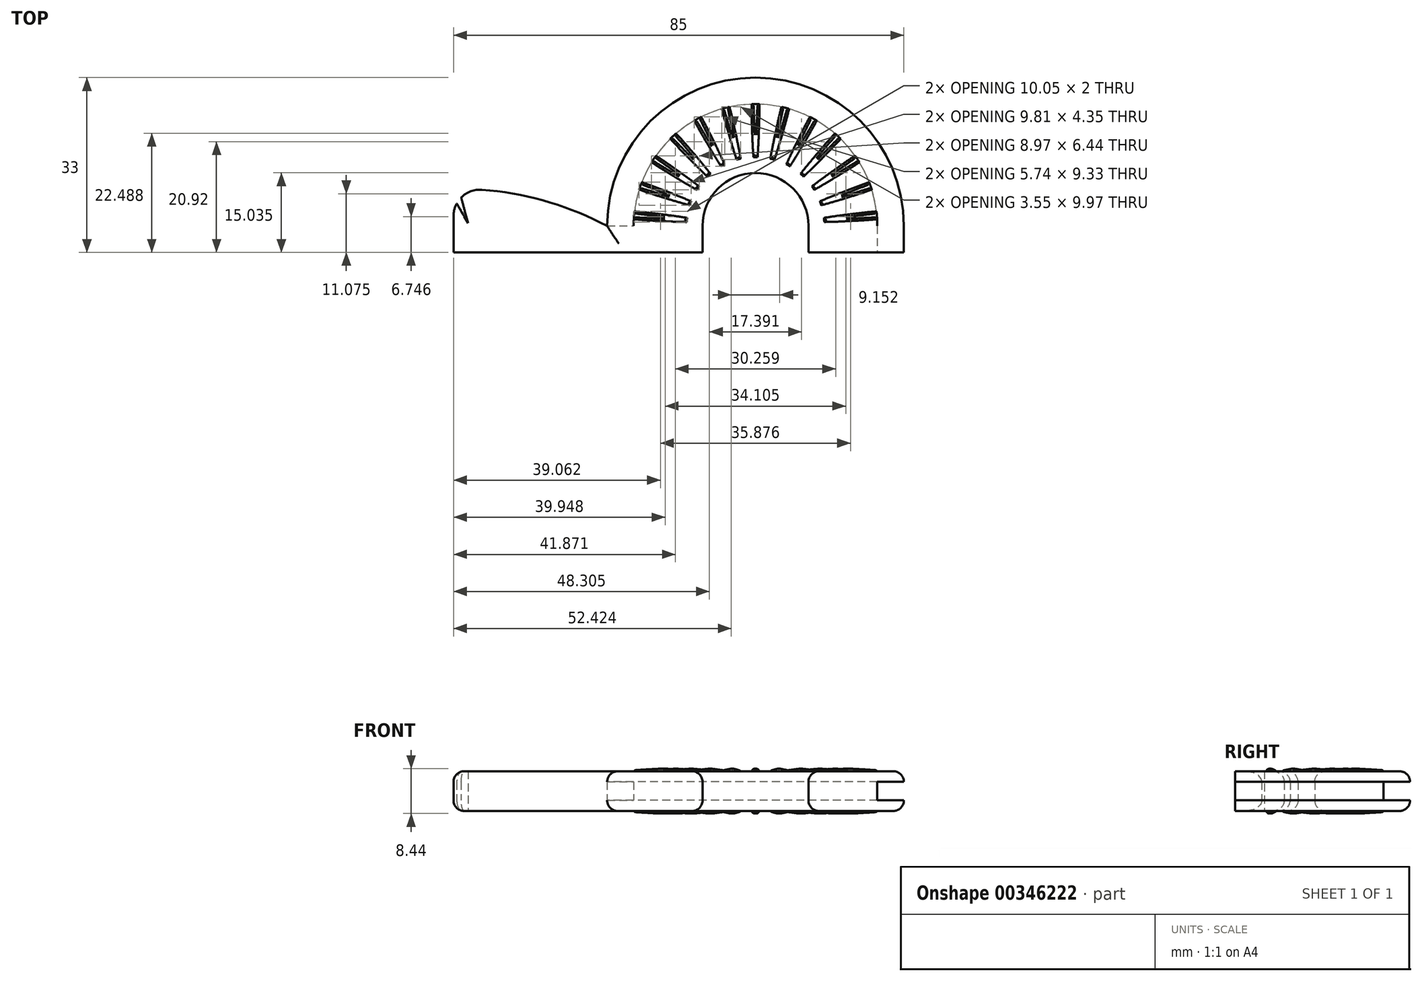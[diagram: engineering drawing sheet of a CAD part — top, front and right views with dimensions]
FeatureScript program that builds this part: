
annotation { "Feature Type Name" : "Feature", "Feature Type Description" : "" }
export const myFeature = defineFeature(function(context is Context, id is Id, definition is map)
    precondition{}
    {
        {
            var Q0;
            Q0=qCreatedBy(makeId("Top.planeOp"),FACE);
            var sketch = newSketch(context, id + "F0", { "sketchPlane" : qUnion([Q0])});
            skLineSegment(sketch, "E0", {"start": v(-57, 0) * mm, "end": v(28, 0) * mm});
            skLineSegment(sketch, "E1", {"start": v(-57, 0) * mm, "end": v(-57, 12) * mm});
            skArc(sketch, "E2", {"start": v(28, 5) * mm, "mid": v(0, 33) * mm, "end": v(-28, 5) * mm});
            skLineSegment(sketch, "E3", {"start": v(28, 5) * mm, "end": v(28, 0) * mm});
            skArc(sketch, "E4", {"start": v(23, 5) * mm, "mid": v(0, 28) * mm, "end": v(-23, 5) * mm});
            skLineSegment(sketch, "E5", {"start": v(-28, 5) * mm, "end": v(-23, 5) * mm});
            skLineSegment(sketch, "E6", {"start": v(23, 5) * mm, "end": v(28, 5) * mm});
            skLineSegment(sketch, "E7", {"start": v(23, 5) * mm, "end": v(23, 0) * mm});
            skLineSegment(sketch, "E8", {"start": v(-57, 12) * mm, "end": v(-42, 12) * mm});
            skLineSegment(sketch, "E9", {"start": v(-42, 12) * mm, "end": v(-28, 5) * mm});
            skPoint(sketch, "E10", {"position": v(-10, 0) * mm});
            skPoint(sketch, "E11", {"position": v(10, 0) * mm});
            skArc(sketch, "E12", {"start": v(10, 5) * mm, "mid": v(0, 15) * mm, "end": v(-10, 5) * mm});
            skLineSegment(sketch, "E13", {"start": v(-13, 5) * mm, "end": v(0, 5) * mm, "construction": true});
            skLineSegment(sketch, "E14", {"start": v(10, 5) * mm, "end": v(10, 0) * mm});
            skLineSegment(sketch, "E15", {"start": v(-10, 5) * mm, "end": v(-10, 0) * mm});
            skLineSegment(sketch, "E16", {"start": v(-22.97, 6.19) * mm, "end": v(-12.98, 5.67) * mm});
            skLineSegment(sketch, "E17", {"start": v(-12.9, 6.6) * mm, "end": v(-22.83, 7.82) * mm});
            skLineSegment(sketch, "E18.1.0", {"start": v(-21.98, 11.77) * mm, "end": v(-12.42, 8.83) * mm});
            skLineSegment(sketch, "E18.1.1", {"start": v(-12.12, 9.7) * mm, "end": v(-21.44, 13.32) * mm});
            skLineSegment(sketch, "E18.2.0", {"start": v(-19.66, 16.94) * mm, "end": v(-11.1, 11.75) * mm});
            skLineSegment(sketch, "E18.2.1", {"start": v(-10.6, 12.53) * mm, "end": v(-18.75, 18.32) * mm});
            skLineSegment(sketch, "E18.anchor1", {"start": v(-12.98, 5.67) * mm, "end": v(-22.97, 6.19) * mm, "construction": true});
            skLineSegment(sketch, "E18.anchor2", {"start": v(12.9, 6.6) * mm, "end": v(22.83, 7.82) * mm, "construction": true});
            skLineSegment(sketch, "E19.1.3.0", {"start": v(-16.13, 21.4) * mm, "end": v(-9.12, 14.26) * mm});
            skLineSegment(sketch, "E19.3.3.0", {"start": v(-8.43, 14.9) * mm, "end": v(-14.92, 22.5) * mm});
            skLineSegment(sketch, "E19.1.4.0", {"start": v(-11.63, 24.84) * mm, "end": v(-6.57, 16.21) * mm});
            skLineSegment(sketch, "E19.3.4.0", {"start": v(-5.76, 16.66) * mm, "end": v(-10.19, 25.62) * mm});
            skLineSegment(sketch, "E19.1.5.0", {"start": v(-6.42, 27.09) * mm, "end": v(-3.63, 17.48) * mm});
            skLineSegment(sketch, "E19.3.5.0", {"start": v(-2.73, 17.71) * mm, "end": v(-4.83, 27.49) * mm});
            skLineSegment(sketch, "E19.1.6.0", {"start": v(-0.82, 27.99) * mm, "end": v(-0.46, 18) * mm});
            skLineSegment(sketch, "E19.3.6.0", {"start": v(0.46, 18) * mm, "end": v(0.82, 27.99) * mm});
            skLineSegment(sketch, "E19.1.7.0", {"start": v(4.83, 27.49) * mm, "end": v(2.73, 17.71) * mm});
            skLineSegment(sketch, "E19.3.7.0", {"start": v(3.63, 17.48) * mm, "end": v(6.42, 27.09) * mm});
            skLineSegment(sketch, "E19.1.8.0", {"start": v(10.19, 25.62) * mm, "end": v(5.76, 16.66) * mm});
            skLineSegment(sketch, "E19.3.8.0", {"start": v(6.57, 16.21) * mm, "end": v(11.63, 24.84) * mm});
            skLineSegment(sketch, "E19.1.9.0", {"start": v(14.92, 22.5) * mm, "end": v(8.43, 14.9) * mm});
            skLineSegment(sketch, "E19.3.9.0", {"start": v(9.12, 14.26) * mm, "end": v(16.13, 21.4) * mm});
            skLineSegment(sketch, "E19.1.10.0", {"start": v(18.75, 18.32) * mm, "end": v(10.6, 12.53) * mm});
            skLineSegment(sketch, "E19.3.10.0", {"start": v(11.1, 11.75) * mm, "end": v(19.66, 16.94) * mm});
            skLineSegment(sketch, "E19.1.11.0", {"start": v(21.44, 13.32) * mm, "end": v(12.12, 9.7) * mm});
            skLineSegment(sketch, "E19.3.11.0", {"start": v(12.42, 8.83) * mm, "end": v(21.98, 11.77) * mm});
            skLineSegment(sketch, "E19.1.12.0", {"start": v(22.83, 7.82) * mm, "end": v(12.9, 6.6) * mm});
            skLineSegment(sketch, "E19.3.12.0", {"start": v(12.98, 5.67) * mm, "end": v(22.97, 6.19) * mm});
            skArc(sketch, "E20", {"start": v(13, 5) * mm, "mid": v(0, 18) * mm, "end": v(-13, 5) * mm});
            skLineSegment(sketch, "E21.trimOffspring", {"start": v(10, 5) * mm, "end": v(13, 5) * mm, "construction": true});
            skPoint(sketch, "E22.orphan", {"position": v(-27.79, 8.43) * mm});
            skPoint(sketch, "E23.orphan", {"position": v(-26.76, 13.24) * mm});
            skPoint(sketch, "E24.orphan", {"position": v(-27.96, 6.44) * mm});
            skPoint(sketch, "E25.orphan", {"position": v(-26.1, 15.13) * mm});
            skPoint(sketch, "E26.orphan", {"position": v(-23.93, 19.54) * mm});
            skPoint(sketch, "E27.orphan", {"position": v(-22.83, 21.21) * mm});
            skPoint(sketch, "E28.orphan", {"position": v(-19.64, 24.96) * mm});
            skPoint(sketch, "E29.orphan", {"position": v(-18.17, 26.3) * mm});
            skPoint(sketch, "E30.orphan", {"position": v(-14.16, 29.16) * mm});
            skPoint(sketch, "E31.orphan", {"position": v(-12.4, 30.1) * mm});
            skPoint(sketch, "E32.orphan", {"position": v(-7.82, 31.89) * mm});
            skPoint(sketch, "E33.orphan", {"position": v(-5.88, 32.38) * mm});
            skPoint(sketch, "E34.orphan", {"position": v(-1, 32.98) * mm});
            skPoint(sketch, "E35.orphan", {"position": v(1, 32.98) * mm});
            skPoint(sketch, "E36.orphan", {"position": v(5.88, 32.38) * mm});
            skPoint(sketch, "E37.orphan", {"position": v(7.82, 31.89) * mm});
            skPoint(sketch, "E38.orphan", {"position": v(12.4, 30.1) * mm});
            skPoint(sketch, "E39.orphan", {"position": v(14.16, 29.16) * mm});
            skPoint(sketch, "E40.orphan", {"position": v(18.17, 26.3) * mm});
            skPoint(sketch, "E41.orphan", {"position": v(19.64, 24.96) * mm});
            skPoint(sketch, "E42.orphan", {"position": v(22.83, 21.21) * mm});
            skPoint(sketch, "E43.orphan", {"position": v(23.93, 19.54) * mm});
            skPoint(sketch, "E44.orphan", {"position": v(26.1, 15.13) * mm});
            skPoint(sketch, "E45.orphan", {"position": v(26.76, 13.24) * mm});
            skPoint(sketch, "E46.orphan", {"position": v(27.79, 8.43) * mm});
            skPoint(sketch, "E47.orphan", {"position": v(27.96, 6.44) * mm});
            skLineSegment(sketch, "E48", {"start": v(-57, 10.29) * mm, "end": v(-54.25, 5.53) * mm});
            skLineSegment(sketch, "E49", {"start": v(-54.25, 5.53) * mm, "end": v(-55.98, 12) * mm});
            skSolve(sketch);
        }
        {
            var Q0;
            {var subQ0=sQuery(id+"F0.wireOp",EDGE,"E3");Q0=makeQuery(id+"F0.imprint","IMPRINT",FACE,{"disambiguationData":[TD([[makeQuery(id+"F0.imprint","IMPRINT",EDGE,{"derivedFrom":subQ0}),-1.0]])]});}
            var Q1;
            {var subQ0=sQuery(id+"F0.wireOp",EDGE,"E5");Q1=makeQuery(id+"F0.imprint","IMPRINT",FACE,{"disambiguationData":[TD([[makeQuery(id+"F0.imprint","IMPRINT",EDGE,{"derivedFrom":subQ0}),1.0]])]});}
            var Q2;
            {var subQ4=sQuery(id+"F0.wireOp",EDGE,"E1");Q2=makeQuery(id+"F0.imprint","IMPRINT",FACE,{"disambiguationData":[TD([[makeQuery(id+"F0.imprint","IMPRINT",EDGE,{"derivedFrom":subQ4}),-1.0]])]});}
            var Q3;
            {var subQ0=sQuery(id+"F0.wireOp",EDGE,"E6");Q3=makeQuery(id+"F0.imprint","IMPRINT",FACE,{"disambiguationData":[TD([[makeQuery(id+"F0.imprint","IMPRINT",EDGE,{"derivedFrom":subQ0}),1.0]])]});}
            var Q4;
            {var subQ0=sQuery(id+"F0.wireOp",EDGE,"E19.1.12.0");var subQ1=sQuery(id+"F0.wireOp",EDGE,"E2");var subQ2=makeQuery(id+"F0.imprint","INTERSECT",VERTEX,{"derivedFrom":[subQ1,subQ0]});Q4=makeQuery(id+"F0.imprint","IMPRINT",FACE,{"disambiguationData":[TD([[makeQuery(id+"F0.imprint","IMPRINT",EDGE,{"disambiguationData":[TD([[subQ2,1.0]])],"derivedFrom":subQ1}),1.0]])]});}
            var Q5;
            {var subQ0=sQuery(id+"F0.wireOp",EDGE,"E19.3.11.0");var subQ1=sQuery(id+"F0.wireOp",EDGE,"E2");var subQ2=makeQuery(id+"F0.imprint","INTERSECT",VERTEX,{"derivedFrom":[subQ1,subQ0]});Q5=makeQuery(id+"F0.imprint","IMPRINT",FACE,{"disambiguationData":[TD([[makeQuery(id+"F0.imprint","IMPRINT",EDGE,{"disambiguationData":[TD([[subQ2,1.0]])],"derivedFrom":subQ1}),1.0]])]});}
            var Q6;
            {var subQ0=sQuery(id+"F0.wireOp",EDGE,"E19.1.11.0");var subQ1=sQuery(id+"F0.wireOp",EDGE,"E2");var subQ2=makeQuery(id+"F0.imprint","INTERSECT",VERTEX,{"derivedFrom":[subQ1,subQ0]});Q6=makeQuery(id+"F0.imprint","IMPRINT",FACE,{"disambiguationData":[TD([[makeQuery(id+"F0.imprint","IMPRINT",EDGE,{"disambiguationData":[TD([[subQ2,1.0]])],"derivedFrom":subQ1}),1.0]])]});}
            var Q7;
            {var subQ0=sQuery(id+"F0.wireOp",EDGE,"E19.3.10.0");var subQ1=sQuery(id+"F0.wireOp",EDGE,"E2");var subQ2=makeQuery(id+"F0.imprint","INTERSECT",VERTEX,{"derivedFrom":[subQ1,subQ0]});Q7=makeQuery(id+"F0.imprint","IMPRINT",FACE,{"disambiguationData":[TD([[makeQuery(id+"F0.imprint","IMPRINT",EDGE,{"disambiguationData":[TD([[subQ2,1.0]])],"derivedFrom":subQ1}),1.0]])]});}
            var Q8;
            {var subQ0=sQuery(id+"F0.wireOp",EDGE,"E19.1.10.0");var subQ1=sQuery(id+"F0.wireOp",EDGE,"E2");var subQ2=makeQuery(id+"F0.imprint","INTERSECT",VERTEX,{"derivedFrom":[subQ1,subQ0]});Q8=makeQuery(id+"F0.imprint","IMPRINT",FACE,{"disambiguationData":[TD([[makeQuery(id+"F0.imprint","IMPRINT",EDGE,{"disambiguationData":[TD([[subQ2,1.0]])],"derivedFrom":subQ1}),1.0]])]});}
            var Q9;
            {var subQ0=sQuery(id+"F0.wireOp",EDGE,"E19.3.9.0");var subQ1=sQuery(id+"F0.wireOp",EDGE,"E2");var subQ2=makeQuery(id+"F0.imprint","INTERSECT",VERTEX,{"derivedFrom":[subQ1,subQ0]});Q9=makeQuery(id+"F0.imprint","IMPRINT",FACE,{"disambiguationData":[TD([[makeQuery(id+"F0.imprint","IMPRINT",EDGE,{"disambiguationData":[TD([[subQ2,1.0]])],"derivedFrom":subQ1}),1.0]])]});}
            var Q10;
            {var subQ0=sQuery(id+"F0.wireOp",EDGE,"E19.1.9.0");var subQ1=sQuery(id+"F0.wireOp",EDGE,"E2");var subQ2=makeQuery(id+"F0.imprint","INTERSECT",VERTEX,{"derivedFrom":[subQ1,subQ0]});Q10=makeQuery(id+"F0.imprint","IMPRINT",FACE,{"disambiguationData":[TD([[makeQuery(id+"F0.imprint","IMPRINT",EDGE,{"disambiguationData":[TD([[subQ2,1.0]])],"derivedFrom":subQ1}),1.0]])]});}
            var Q11;
            {var subQ0=sQuery(id+"F0.wireOp",EDGE,"E19.3.8.0");var subQ1=sQuery(id+"F0.wireOp",EDGE,"E2");var subQ2=makeQuery(id+"F0.imprint","INTERSECT",VERTEX,{"derivedFrom":[subQ1,subQ0]});Q11=makeQuery(id+"F0.imprint","IMPRINT",FACE,{"disambiguationData":[TD([[makeQuery(id+"F0.imprint","IMPRINT",EDGE,{"disambiguationData":[TD([[subQ2,1.0]])],"derivedFrom":subQ1}),1.0]])]});}
            var Q12;
            {var subQ0=sQuery(id+"F0.wireOp",EDGE,"E19.1.8.0");var subQ1=sQuery(id+"F0.wireOp",EDGE,"E2");var subQ2=makeQuery(id+"F0.imprint","INTERSECT",VERTEX,{"derivedFrom":[subQ1,subQ0]});Q12=makeQuery(id+"F0.imprint","IMPRINT",FACE,{"disambiguationData":[TD([[makeQuery(id+"F0.imprint","IMPRINT",EDGE,{"disambiguationData":[TD([[subQ2,1.0]])],"derivedFrom":subQ1}),1.0]])]});}
            var Q13;
            {var subQ0=sQuery(id+"F0.wireOp",EDGE,"E19.3.7.0");var subQ1=sQuery(id+"F0.wireOp",EDGE,"E2");var subQ2=makeQuery(id+"F0.imprint","INTERSECT",VERTEX,{"derivedFrom":[subQ1,subQ0]});Q13=makeQuery(id+"F0.imprint","IMPRINT",FACE,{"disambiguationData":[TD([[makeQuery(id+"F0.imprint","IMPRINT",EDGE,{"disambiguationData":[TD([[subQ2,1.0]])],"derivedFrom":subQ1}),1.0]])]});}
            var Q14;
            {var subQ0=sQuery(id+"F0.wireOp",EDGE,"E19.1.7.0");var subQ1=sQuery(id+"F0.wireOp",EDGE,"E2");var subQ2=makeQuery(id+"F0.imprint","INTERSECT",VERTEX,{"derivedFrom":[subQ1,subQ0]});Q14=makeQuery(id+"F0.imprint","IMPRINT",FACE,{"disambiguationData":[TD([[makeQuery(id+"F0.imprint","IMPRINT",EDGE,{"disambiguationData":[TD([[subQ2,1.0]])],"derivedFrom":subQ1}),1.0]])]});}
            var Q15;
            {var subQ0=sQuery(id+"F0.wireOp",EDGE,"E19.3.6.0");var subQ1=sQuery(id+"F0.wireOp",EDGE,"E2");var subQ2=makeQuery(id+"F0.imprint","INTERSECT",VERTEX,{"derivedFrom":[subQ1,subQ0]});Q15=makeQuery(id+"F0.imprint","IMPRINT",FACE,{"disambiguationData":[TD([[makeQuery(id+"F0.imprint","IMPRINT",EDGE,{"disambiguationData":[TD([[subQ2,1.0]])],"derivedFrom":subQ1}),1.0]])]});}
            var Q16;
            {var subQ0=sQuery(id+"F0.wireOp",EDGE,"E19.1.6.0");var subQ1=sQuery(id+"F0.wireOp",EDGE,"E2");var subQ2=makeQuery(id+"F0.imprint","INTERSECT",VERTEX,{"derivedFrom":[subQ1,subQ0]});Q16=makeQuery(id+"F0.imprint","IMPRINT",FACE,{"disambiguationData":[TD([[makeQuery(id+"F0.imprint","IMPRINT",EDGE,{"disambiguationData":[TD([[subQ2,1.0]])],"derivedFrom":subQ1}),1.0]])]});}
            var Q17;
            {var subQ0=sQuery(id+"F0.wireOp",EDGE,"E19.3.5.0");var subQ1=sQuery(id+"F0.wireOp",EDGE,"E2");var subQ2=makeQuery(id+"F0.imprint","INTERSECT",VERTEX,{"derivedFrom":[subQ1,subQ0]});Q17=makeQuery(id+"F0.imprint","IMPRINT",FACE,{"disambiguationData":[TD([[makeQuery(id+"F0.imprint","IMPRINT",EDGE,{"disambiguationData":[TD([[subQ2,1.0]])],"derivedFrom":subQ1}),1.0]])]});}
            var Q18;
            {var subQ0=sQuery(id+"F0.wireOp",EDGE,"E19.1.5.0");var subQ1=sQuery(id+"F0.wireOp",EDGE,"E2");var subQ2=makeQuery(id+"F0.imprint","INTERSECT",VERTEX,{"derivedFrom":[subQ1,subQ0]});Q18=makeQuery(id+"F0.imprint","IMPRINT",FACE,{"disambiguationData":[TD([[makeQuery(id+"F0.imprint","IMPRINT",EDGE,{"disambiguationData":[TD([[subQ2,1.0]])],"derivedFrom":subQ1}),1.0]])]});}
            var Q19;
            {var subQ0=sQuery(id+"F0.wireOp",EDGE,"E19.3.4.0");var subQ1=sQuery(id+"F0.wireOp",EDGE,"E2");var subQ2=makeQuery(id+"F0.imprint","INTERSECT",VERTEX,{"derivedFrom":[subQ1,subQ0]});Q19=makeQuery(id+"F0.imprint","IMPRINT",FACE,{"disambiguationData":[TD([[makeQuery(id+"F0.imprint","IMPRINT",EDGE,{"disambiguationData":[TD([[subQ2,1.0]])],"derivedFrom":subQ1}),1.0]])]});}
            var Q20;
            {var subQ0=sQuery(id+"F0.wireOp",EDGE,"E19.1.4.0");var subQ1=sQuery(id+"F0.wireOp",EDGE,"E2");var subQ2=makeQuery(id+"F0.imprint","INTERSECT",VERTEX,{"derivedFrom":[subQ1,subQ0]});Q20=makeQuery(id+"F0.imprint","IMPRINT",FACE,{"disambiguationData":[TD([[makeQuery(id+"F0.imprint","IMPRINT",EDGE,{"disambiguationData":[TD([[subQ2,1.0]])],"derivedFrom":subQ1}),1.0]])]});}
            var Q21;
            {var subQ0=sQuery(id+"F0.wireOp",EDGE,"E19.3.3.0");var subQ1=sQuery(id+"F0.wireOp",EDGE,"E2");var subQ2=makeQuery(id+"F0.imprint","INTERSECT",VERTEX,{"derivedFrom":[subQ1,subQ0]});Q21=makeQuery(id+"F0.imprint","IMPRINT",FACE,{"disambiguationData":[TD([[makeQuery(id+"F0.imprint","IMPRINT",EDGE,{"disambiguationData":[TD([[subQ2,1.0]])],"derivedFrom":subQ1}),1.0]])]});}
            var Q22;
            {var subQ0=sQuery(id+"F0.wireOp",EDGE,"E19.1.3.0");var subQ1=sQuery(id+"F0.wireOp",EDGE,"E2");var subQ2=makeQuery(id+"F0.imprint","INTERSECT",VERTEX,{"derivedFrom":[subQ1,subQ0]});Q22=makeQuery(id+"F0.imprint","IMPRINT",FACE,{"disambiguationData":[TD([[makeQuery(id+"F0.imprint","IMPRINT",EDGE,{"disambiguationData":[TD([[subQ2,1.0]])],"derivedFrom":subQ1}),1.0]])]});}
            var Q23;
            {var subQ0=sQuery(id+"F0.wireOp",EDGE,"E18.2.1");var subQ1=sQuery(id+"F0.wireOp",EDGE,"E2");var subQ2=makeQuery(id+"F0.imprint","INTERSECT",VERTEX,{"derivedFrom":[subQ1,subQ0]});Q23=makeQuery(id+"F0.imprint","IMPRINT",FACE,{"disambiguationData":[TD([[makeQuery(id+"F0.imprint","IMPRINT",EDGE,{"disambiguationData":[TD([[subQ2,1.0]])],"derivedFrom":subQ1}),1.0]])]});}
            var Q24;
            {var subQ0=sQuery(id+"F0.wireOp",EDGE,"E18.2.0");var subQ1=sQuery(id+"F0.wireOp",EDGE,"E2");var subQ2=makeQuery(id+"F0.imprint","INTERSECT",VERTEX,{"derivedFrom":[subQ1,subQ0]});Q24=makeQuery(id+"F0.imprint","IMPRINT",FACE,{"disambiguationData":[TD([[makeQuery(id+"F0.imprint","IMPRINT",EDGE,{"disambiguationData":[TD([[subQ2,1.0]])],"derivedFrom":subQ1}),1.0]])]});}
            var Q25;
            {var subQ0=sQuery(id+"F0.wireOp",EDGE,"E18.1.1");var subQ1=sQuery(id+"F0.wireOp",EDGE,"E2");var subQ2=makeQuery(id+"F0.imprint","INTERSECT",VERTEX,{"derivedFrom":[subQ1,subQ0]});Q25=makeQuery(id+"F0.imprint","IMPRINT",FACE,{"disambiguationData":[TD([[makeQuery(id+"F0.imprint","IMPRINT",EDGE,{"disambiguationData":[TD([[subQ2,1.0]])],"derivedFrom":subQ1}),1.0]])]});}
            var Q26;
            {var subQ0=sQuery(id+"F0.wireOp",EDGE,"E18.1.0");var subQ1=sQuery(id+"F0.wireOp",EDGE,"E2");var subQ2=makeQuery(id+"F0.imprint","INTERSECT",VERTEX,{"derivedFrom":[subQ1,subQ0]});Q26=makeQuery(id+"F0.imprint","IMPRINT",FACE,{"disambiguationData":[TD([[makeQuery(id+"F0.imprint","IMPRINT",EDGE,{"disambiguationData":[TD([[subQ2,1.0]])],"derivedFrom":subQ1}),1.0]])]});}
            var Q27;
            {var subQ0=sQuery(id+"F0.wireOp",EDGE,"E17");var subQ1=sQuery(id+"F0.wireOp",EDGE,"E2");var subQ2=makeQuery(id+"F0.imprint","INTERSECT",VERTEX,{"derivedFrom":[subQ1,subQ0]});Q27=makeQuery(id+"F0.imprint","IMPRINT",FACE,{"disambiguationData":[TD([[makeQuery(id+"F0.imprint","IMPRINT",EDGE,{"disambiguationData":[TD([[subQ2,1.0]])],"derivedFrom":subQ1}),1.0]])]});}
            var Q28;
            {var subQ0=sQuery(id+"F0.wireOp",EDGE,"E16");var subQ1=sQuery(id+"F0.wireOp",EDGE,"E2");var subQ2=makeQuery(id+"F0.imprint","INTERSECT",VERTEX,{"derivedFrom":[subQ1,subQ0]});Q28=makeQuery(id+"F0.imprint","IMPRINT",FACE,{"disambiguationData":[TD([[makeQuery(id+"F0.imprint","IMPRINT",EDGE,{"disambiguationData":[TD([[subQ2,1.0]])],"derivedFrom":subQ1}),1.0]])]});}
            var Q29;
            {var subQ4=sQuery(id+"F0.wireOp",EDGE,"E7");Q29=makeQuery(id+"F0.imprint","IMPRINT",FACE,{"disambiguationData":[TD([[makeQuery(id+"F0.imprint","IMPRINT",EDGE,{"derivedFrom":subQ4}),-1.0]])]});}
            var Q30;
            {var subQ0=sQuery(id+"F0.wireOp",EDGE,"E17");var subQ1=sQuery(id+"F0.wireOp",EDGE,"E4");var subQ2=makeQuery(id+"F0.imprint","INTERSECT",VERTEX,{"derivedFrom":[subQ1,subQ0]});Q30=makeQuery(id+"F0.imprint","IMPRINT",FACE,{"disambiguationData":[TD([[makeQuery(id+"F0.imprint","IMPRINT",EDGE,{"disambiguationData":[TD([[subQ2,-1.0]])],"derivedFrom":subQ1}),1.0]])]});}
            var Q31;
            {var subQ0=sQuery(id+"F0.wireOp",EDGE,"E18.1.0");var subQ1=sQuery(id+"F0.wireOp",EDGE,"E4");var subQ2=makeQuery(id+"F0.imprint","INTERSECT",VERTEX,{"derivedFrom":[subQ1,subQ0]});Q31=makeQuery(id+"F0.imprint","IMPRINT",FACE,{"disambiguationData":[TD([[makeQuery(id+"F0.imprint","IMPRINT",EDGE,{"disambiguationData":[TD([[subQ2,-1.0]])],"derivedFrom":subQ1}),1.0]])]});}
            var Q32;
            {var subQ0=sQuery(id+"F0.wireOp",EDGE,"E18.1.1");var subQ1=sQuery(id+"F0.wireOp",EDGE,"E4");var subQ2=makeQuery(id+"F0.imprint","INTERSECT",VERTEX,{"derivedFrom":[subQ1,subQ0]});Q32=makeQuery(id+"F0.imprint","IMPRINT",FACE,{"disambiguationData":[TD([[makeQuery(id+"F0.imprint","IMPRINT",EDGE,{"disambiguationData":[TD([[subQ2,-1.0]])],"derivedFrom":subQ1}),1.0]])]});}
            var Q33;
            {var subQ0=sQuery(id+"F0.wireOp",EDGE,"E18.2.0");var subQ1=sQuery(id+"F0.wireOp",EDGE,"E4");var subQ2=makeQuery(id+"F0.imprint","INTERSECT",VERTEX,{"derivedFrom":[subQ1,subQ0]});Q33=makeQuery(id+"F0.imprint","IMPRINT",FACE,{"disambiguationData":[TD([[makeQuery(id+"F0.imprint","IMPRINT",EDGE,{"disambiguationData":[TD([[subQ2,-1.0]])],"derivedFrom":subQ1}),1.0]])]});}
            var Q34;
            {var subQ0=sQuery(id+"F0.wireOp",EDGE,"E18.2.1");var subQ1=sQuery(id+"F0.wireOp",EDGE,"E4");var subQ2=makeQuery(id+"F0.imprint","INTERSECT",VERTEX,{"derivedFrom":[subQ1,subQ0]});Q34=makeQuery(id+"F0.imprint","IMPRINT",FACE,{"disambiguationData":[TD([[makeQuery(id+"F0.imprint","IMPRINT",EDGE,{"disambiguationData":[TD([[subQ2,-1.0]])],"derivedFrom":subQ1}),1.0]])]});}
            var Q35;
            {var subQ0=sQuery(id+"F0.wireOp",EDGE,"E19.1.3.0");var subQ1=sQuery(id+"F0.wireOp",EDGE,"E4");var subQ2=makeQuery(id+"F0.imprint","INTERSECT",VERTEX,{"derivedFrom":[subQ1,subQ0]});Q35=makeQuery(id+"F0.imprint","IMPRINT",FACE,{"disambiguationData":[TD([[makeQuery(id+"F0.imprint","IMPRINT",EDGE,{"disambiguationData":[TD([[subQ2,-1.0]])],"derivedFrom":subQ1}),1.0]])]});}
            var Q36;
            {var subQ0=sQuery(id+"F0.wireOp",EDGE,"E19.3.5.0");var subQ1=sQuery(id+"F0.wireOp",EDGE,"E4");var subQ2=makeQuery(id+"F0.imprint","INTERSECT",VERTEX,{"derivedFrom":[subQ1,subQ0]});Q36=makeQuery(id+"F0.imprint","IMPRINT",FACE,{"disambiguationData":[TD([[makeQuery(id+"F0.imprint","IMPRINT",EDGE,{"disambiguationData":[TD([[subQ2,-1.0]])],"derivedFrom":subQ1}),1.0]])]});}
            var Q37;
            {var subQ0=sQuery(id+"F0.wireOp",EDGE,"E19.3.3.0");var subQ1=sQuery(id+"F0.wireOp",EDGE,"E4");var subQ2=makeQuery(id+"F0.imprint","INTERSECT",VERTEX,{"derivedFrom":[subQ1,subQ0]});Q37=makeQuery(id+"F0.imprint","IMPRINT",FACE,{"disambiguationData":[TD([[makeQuery(id+"F0.imprint","IMPRINT",EDGE,{"disambiguationData":[TD([[subQ2,-1.0]])],"derivedFrom":subQ1}),1.0]])]});}
            var Q38;
            {var subQ0=sQuery(id+"F0.wireOp",EDGE,"E19.1.4.0");var subQ1=sQuery(id+"F0.wireOp",EDGE,"E4");var subQ2=makeQuery(id+"F0.imprint","INTERSECT",VERTEX,{"derivedFrom":[subQ1,subQ0]});Q38=makeQuery(id+"F0.imprint","IMPRINT",FACE,{"disambiguationData":[TD([[makeQuery(id+"F0.imprint","IMPRINT",EDGE,{"disambiguationData":[TD([[subQ2,-1.0]])],"derivedFrom":subQ1}),1.0]])]});}
            var Q39;
            {var subQ0=sQuery(id+"F0.wireOp",EDGE,"E19.3.4.0");var subQ1=sQuery(id+"F0.wireOp",EDGE,"E4");var subQ2=makeQuery(id+"F0.imprint","INTERSECT",VERTEX,{"derivedFrom":[subQ1,subQ0]});Q39=makeQuery(id+"F0.imprint","IMPRINT",FACE,{"disambiguationData":[TD([[makeQuery(id+"F0.imprint","IMPRINT",EDGE,{"disambiguationData":[TD([[subQ2,-1.0]])],"derivedFrom":subQ1}),1.0]])]});}
            var Q40;
            {var subQ0=sQuery(id+"F0.wireOp",EDGE,"E19.1.5.0");var subQ1=sQuery(id+"F0.wireOp",EDGE,"E4");var subQ2=makeQuery(id+"F0.imprint","INTERSECT",VERTEX,{"derivedFrom":[subQ1,subQ0]});Q40=makeQuery(id+"F0.imprint","IMPRINT",FACE,{"disambiguationData":[TD([[makeQuery(id+"F0.imprint","IMPRINT",EDGE,{"disambiguationData":[TD([[subQ2,-1.0]])],"derivedFrom":subQ1}),1.0]])]});}
            var Q41;
            {var subQ0=sQuery(id+"F0.wireOp",EDGE,"E19.1.7.0");var subQ1=sQuery(id+"F0.wireOp",EDGE,"E4");var subQ2=makeQuery(id+"F0.imprint","INTERSECT",VERTEX,{"derivedFrom":[subQ1,subQ0]});Q41=makeQuery(id+"F0.imprint","IMPRINT",FACE,{"disambiguationData":[TD([[makeQuery(id+"F0.imprint","IMPRINT",EDGE,{"disambiguationData":[TD([[subQ2,-1.0]])],"derivedFrom":subQ1}),1.0]])]});}
            var Q42;
            {var subQ0=sQuery(id+"F0.wireOp",EDGE,"E19.3.11.0");var subQ1=sQuery(id+"F0.wireOp",EDGE,"E4");var subQ2=makeQuery(id+"F0.imprint","INTERSECT",VERTEX,{"derivedFrom":[subQ1,subQ0]});Q42=makeQuery(id+"F0.imprint","IMPRINT",FACE,{"disambiguationData":[TD([[makeQuery(id+"F0.imprint","IMPRINT",EDGE,{"disambiguationData":[TD([[subQ2,-1.0]])],"derivedFrom":subQ1}),1.0]])]});}
            var Q43;
            {var subQ0=sQuery(id+"F0.wireOp",EDGE,"E19.3.6.0");var subQ1=sQuery(id+"F0.wireOp",EDGE,"E4");var subQ2=makeQuery(id+"F0.imprint","INTERSECT",VERTEX,{"derivedFrom":[subQ1,subQ0]});Q43=makeQuery(id+"F0.imprint","IMPRINT",FACE,{"disambiguationData":[TD([[makeQuery(id+"F0.imprint","IMPRINT",EDGE,{"disambiguationData":[TD([[subQ2,-1.0]])],"derivedFrom":subQ1}),1.0]])]});}
            var Q44;
            {var subQ0=sQuery(id+"F0.wireOp",EDGE,"E19.1.10.0");var subQ1=sQuery(id+"F0.wireOp",EDGE,"E4");var subQ2=makeQuery(id+"F0.imprint","INTERSECT",VERTEX,{"derivedFrom":[subQ1,subQ0]});Q44=makeQuery(id+"F0.imprint","IMPRINT",FACE,{"disambiguationData":[TD([[makeQuery(id+"F0.imprint","IMPRINT",EDGE,{"disambiguationData":[TD([[subQ2,-1.0]])],"derivedFrom":subQ1}),1.0]])]});}
            var Q45;
            {var subQ0=sQuery(id+"F0.wireOp",EDGE,"E19.3.8.0");var subQ1=sQuery(id+"F0.wireOp",EDGE,"E4");var subQ2=makeQuery(id+"F0.imprint","INTERSECT",VERTEX,{"derivedFrom":[subQ1,subQ0]});Q45=makeQuery(id+"F0.imprint","IMPRINT",FACE,{"disambiguationData":[TD([[makeQuery(id+"F0.imprint","IMPRINT",EDGE,{"disambiguationData":[TD([[subQ2,-1.0]])],"derivedFrom":subQ1}),1.0]])]});}
            var Q46;
            {var subQ0=sQuery(id+"F0.wireOp",EDGE,"E19.1.11.0");var subQ1=sQuery(id+"F0.wireOp",EDGE,"E4");var subQ2=makeQuery(id+"F0.imprint","INTERSECT",VERTEX,{"derivedFrom":[subQ1,subQ0]});Q46=makeQuery(id+"F0.imprint","IMPRINT",FACE,{"disambiguationData":[TD([[makeQuery(id+"F0.imprint","IMPRINT",EDGE,{"disambiguationData":[TD([[subQ2,-1.0]])],"derivedFrom":subQ1}),1.0]])]});}
            var Q47;
            {var subQ0=sQuery(id+"F0.wireOp",EDGE,"E19.1.6.0");var subQ1=sQuery(id+"F0.wireOp",EDGE,"E4");var subQ2=makeQuery(id+"F0.imprint","INTERSECT",VERTEX,{"derivedFrom":[subQ1,subQ0]});Q47=makeQuery(id+"F0.imprint","IMPRINT",FACE,{"disambiguationData":[TD([[makeQuery(id+"F0.imprint","IMPRINT",EDGE,{"disambiguationData":[TD([[subQ2,-1.0]])],"derivedFrom":subQ1}),1.0]])]});}
            var Q48;
            {var subQ0=sQuery(id+"F0.wireOp",EDGE,"E19.3.9.0");var subQ1=sQuery(id+"F0.wireOp",EDGE,"E4");var subQ2=makeQuery(id+"F0.imprint","INTERSECT",VERTEX,{"derivedFrom":[subQ1,subQ0]});Q48=makeQuery(id+"F0.imprint","IMPRINT",FACE,{"disambiguationData":[TD([[makeQuery(id+"F0.imprint","IMPRINT",EDGE,{"disambiguationData":[TD([[subQ2,-1.0]])],"derivedFrom":subQ1}),1.0]])]});}
            var Q49;
            {var subQ0=sQuery(id+"F0.wireOp",EDGE,"E19.1.8.0");var subQ1=sQuery(id+"F0.wireOp",EDGE,"E4");var subQ2=makeQuery(id+"F0.imprint","INTERSECT",VERTEX,{"derivedFrom":[subQ1,subQ0]});Q49=makeQuery(id+"F0.imprint","IMPRINT",FACE,{"disambiguationData":[TD([[makeQuery(id+"F0.imprint","IMPRINT",EDGE,{"disambiguationData":[TD([[subQ2,-1.0]])],"derivedFrom":subQ1}),1.0]])]});}
            var Q50;
            {var subQ0=sQuery(id+"F0.wireOp",EDGE,"E19.3.10.0");var subQ1=sQuery(id+"F0.wireOp",EDGE,"E4");var subQ2=makeQuery(id+"F0.imprint","INTERSECT",VERTEX,{"derivedFrom":[subQ1,subQ0]});Q50=makeQuery(id+"F0.imprint","IMPRINT",FACE,{"disambiguationData":[TD([[makeQuery(id+"F0.imprint","IMPRINT",EDGE,{"disambiguationData":[TD([[subQ2,-1.0]])],"derivedFrom":subQ1}),1.0]])]});}
            var Q51;
            {var subQ0=sQuery(id+"F0.wireOp",EDGE,"E19.3.12.0");var subQ1=sQuery(id+"F0.wireOp",EDGE,"E4");var subQ2=makeQuery(id+"F0.imprint","INTERSECT",VERTEX,{"derivedFrom":[subQ1,subQ0]});Q51=makeQuery(id+"F0.imprint","IMPRINT",FACE,{"disambiguationData":[TD([[makeQuery(id+"F0.imprint","IMPRINT",EDGE,{"disambiguationData":[TD([[subQ2,-1.0]])],"derivedFrom":subQ1}),1.0]])]});}
            var Q52;
            {var subQ0=sQuery(id+"F0.wireOp",EDGE,"E19.3.7.0");var subQ1=sQuery(id+"F0.wireOp",EDGE,"E4");var subQ2=makeQuery(id+"F0.imprint","INTERSECT",VERTEX,{"derivedFrom":[subQ1,subQ0]});Q52=makeQuery(id+"F0.imprint","IMPRINT",FACE,{"disambiguationData":[TD([[makeQuery(id+"F0.imprint","IMPRINT",EDGE,{"disambiguationData":[TD([[subQ2,-1.0]])],"derivedFrom":subQ1}),1.0]])]});}
            var Q53;
            {var subQ0=sQuery(id+"F0.wireOp",EDGE,"E19.1.12.0");var subQ1=sQuery(id+"F0.wireOp",EDGE,"E4");var subQ2=makeQuery(id+"F0.imprint","INTERSECT",VERTEX,{"derivedFrom":[subQ1,subQ0]});Q53=makeQuery(id+"F0.imprint","IMPRINT",FACE,{"disambiguationData":[TD([[makeQuery(id+"F0.imprint","IMPRINT",EDGE,{"disambiguationData":[TD([[subQ2,-1.0]])],"derivedFrom":subQ1}),1.0]])]});}
            var Q54;
            {var subQ0=sQuery(id+"F0.wireOp",EDGE,"E19.1.9.0");var subQ1=sQuery(id+"F0.wireOp",EDGE,"E4");var subQ2=makeQuery(id+"F0.imprint","INTERSECT",VERTEX,{"derivedFrom":[subQ1,subQ0]});Q54=makeQuery(id+"F0.imprint","IMPRINT",FACE,{"disambiguationData":[TD([[makeQuery(id+"F0.imprint","IMPRINT",EDGE,{"disambiguationData":[TD([[subQ2,-1.0]])],"derivedFrom":subQ1}),1.0]])]});}
            extrude(context, id + "F1", {"entities" : qUnion([Q0, Q1, Q2, Q3, Q4, Q5, Q6, Q7, Q8, Q9, Q10, Q11, Q12, Q13, Q14, Q15, Q16, Q17, Q18, Q19, Q20, Q21, Q22, Q23, Q24, Q25, Q26, Q27, Q28, Q29, Q30, Q31, Q32, Q33, Q34, Q35, Q36, Q37, Q38, Q39, Q40, Q41, Q42, Q43, Q44, Q45, Q46, Q47, Q48, Q49, Q50, Q51, Q52, Q53, Q54]), "depth" : 7.5 * mm});
        }
        {
            var Q0;
            {var subQ0=sQuery(id+"F0.wireOp",EDGE,"E19.1.12.0");Q0=makeQuery(id+"F0.imprint","IMPRINT",FACE,{"disambiguationData":[TD([[makeQuery(id+"F0.imprint","IMPRINT",EDGE,{"derivedFrom":subQ0}),1.0]])]});}
            var Q1;
            {var subQ0=sQuery(id+"F0.wireOp",EDGE,"E19.1.11.0");Q1=makeQuery(id+"F0.imprint","IMPRINT",FACE,{"disambiguationData":[TD([[makeQuery(id+"F0.imprint","IMPRINT",EDGE,{"derivedFrom":subQ0}),1.0]])]});}
            var Q2;
            {var subQ0=sQuery(id+"F0.wireOp",EDGE,"E19.1.10.0");Q2=makeQuery(id+"F0.imprint","IMPRINT",FACE,{"disambiguationData":[TD([[makeQuery(id+"F0.imprint","IMPRINT",EDGE,{"derivedFrom":subQ0}),1.0]])]});}
            var Q3;
            {var subQ0=sQuery(id+"F0.wireOp",EDGE,"E19.1.9.0");Q3=makeQuery(id+"F0.imprint","IMPRINT",FACE,{"disambiguationData":[TD([[makeQuery(id+"F0.imprint","IMPRINT",EDGE,{"derivedFrom":subQ0}),1.0]])]});}
            var Q4;
            {var subQ0=sQuery(id+"F0.wireOp",EDGE,"E19.1.8.0");Q4=makeQuery(id+"F0.imprint","IMPRINT",FACE,{"disambiguationData":[TD([[makeQuery(id+"F0.imprint","IMPRINT",EDGE,{"derivedFrom":subQ0}),1.0]])]});}
            var Q5;
            {var subQ0=sQuery(id+"F0.wireOp",EDGE,"E19.1.7.0");Q5=makeQuery(id+"F0.imprint","IMPRINT",FACE,{"disambiguationData":[TD([[makeQuery(id+"F0.imprint","IMPRINT",EDGE,{"derivedFrom":subQ0}),1.0]])]});}
            var Q6;
            {var subQ0=sQuery(id+"F0.wireOp",EDGE,"E19.1.6.0");Q6=makeQuery(id+"F0.imprint","IMPRINT",FACE,{"disambiguationData":[TD([[makeQuery(id+"F0.imprint","IMPRINT",EDGE,{"derivedFrom":subQ0}),1.0]])]});}
            var Q7;
            {var subQ0=sQuery(id+"F0.wireOp",EDGE,"E19.1.5.0");Q7=makeQuery(id+"F0.imprint","IMPRINT",FACE,{"disambiguationData":[TD([[makeQuery(id+"F0.imprint","IMPRINT",EDGE,{"derivedFrom":subQ0}),1.0]])]});}
            var Q8;
            {var subQ0=sQuery(id+"F0.wireOp",EDGE,"E19.1.4.0");Q8=makeQuery(id+"F0.imprint","IMPRINT",FACE,{"disambiguationData":[TD([[makeQuery(id+"F0.imprint","IMPRINT",EDGE,{"derivedFrom":subQ0}),1.0]])]});}
            var Q9;
            {var subQ0=sQuery(id+"F0.wireOp",EDGE,"E19.1.3.0");Q9=makeQuery(id+"F0.imprint","IMPRINT",FACE,{"disambiguationData":[TD([[makeQuery(id+"F0.imprint","IMPRINT",EDGE,{"derivedFrom":subQ0}),1.0]])]});}
            var Q10;
            {var subQ0=sQuery(id+"F0.wireOp",EDGE,"E18.2.0");Q10=makeQuery(id+"F0.imprint","IMPRINT",FACE,{"disambiguationData":[TD([[makeQuery(id+"F0.imprint","IMPRINT",EDGE,{"derivedFrom":subQ0}),1.0]])]});}
            var Q11;
            {var subQ0=sQuery(id+"F0.wireOp",EDGE,"E18.1.0");Q11=makeQuery(id+"F0.imprint","IMPRINT",FACE,{"disambiguationData":[TD([[makeQuery(id+"F0.imprint","IMPRINT",EDGE,{"derivedFrom":subQ0}),1.0]])]});}
            var Q12;
            {var subQ0=sQuery(id+"F0.wireOp",EDGE,"E16");Q12=makeQuery(id+"F0.imprint","IMPRINT",FACE,{"disambiguationData":[TD([[makeQuery(id+"F0.imprint","IMPRINT",EDGE,{"derivedFrom":subQ0}),1.0]])]});}
            extrude(context, id + "F2", {"entities" : qUnion([Q0, Q1, Q2, Q3, Q4, Q5, Q6, Q7, Q8, Q9, Q10, Q11, Q12]), "operationType" : NewBodyOperationType.ADD, "depth" : 8 * mm, "hasSecondDirection" : true, "secondDirectionOppositeDirection" : true, "secondDirectionDepth" : 0.5 * mm});
        }
        {
            var Q0;
            Q0=makeQuery(id+"F0.imprint","IMPRINT",FACE,{"disambiguationData":[TD([[makeQuery(id+"F0.imprint","IMPRINT",EDGE,{"derivedFrom":sQuery(id+"F0.wireOp",EDGE,"E2")}),1.0]])]});
            var Q1;
            {var subQ0=sQuery(id+"F0.wireOp",EDGE,"E3");Q1=makeQuery(id+"F0.imprint","IMPRINT",FACE,{"disambiguationData":[TD([[makeQuery(id+"F0.imprint","IMPRINT",EDGE,{"derivedFrom":subQ0}),-1.0]])]});}
            extrude(context, id + "F3", {"entities" : qUnion([Q0, Q1]), "operationType" : NewBodyOperationType.REMOVE, "depth" : 5.5 * mm, "hasSecondDirection" : true, "secondDirectionOppositeDirection" : false, "secondDirectionDepth" : 2 * mm});
        }
        {
            var Q0;
            Q0=makeQuery(id+"F1.opExtrude","SWEPT_EDGE",EDGE,{"disambiguationData":[OSD([sQuery(id+"F0.wireOp",EDGE,"E8"),sQuery(id+"F0.wireOp",EDGE,"E9")])]});
            fillet(context, id + "F4", {"entities" : qUnion([Q0]), "radius" : 60 * mm, "tangentPropagation" : true, "allowEdgeOverflow" : false});
        }
        {
            var Q0;
            Q0=makeQuery(id+"F1.opExtrude","SWEPT_EDGE",EDGE,{"disambiguationData":[OSD([sQuery(id+"F0.wireOp",EDGE,"E1"),sQuery(id+"F0.wireOp",EDGE,"E8")])]});
            fillet(context, id + "F5", {"entities" : qUnion([Q0]), "radius" : 5 * mm, "tangentPropagation" : true, "allowEdgeOverflow" : false});
        }
        {
            var Q0;
            Q0=makeQuery(id+"F1.opExtrude","CAP_EDGE",EDGE,{"disambiguationData":[OSD([sQuery(id+"F0.wireOp",EDGE,"E12")])],"isStart":false});
            var Q1;
            Q1=makeQuery(id+"F1.opExtrude","CAP_EDGE",EDGE,{"disambiguationData":[OSD([sQuery(id+"F0.wireOp",EDGE,"E12")])],"isStart":true});
            var Q2;
            Q2=makeQuery(id+"F1.opExtrude","CAP_EDGE",EDGE,{"disambiguationData":[OSD([sQuery(id+"F0.wireOp",EDGE,"E2")])],"isStart":false});
            var Q3;
            Q3=makeQuery(id+"F1.opExtrude","CAP_EDGE",EDGE,{"disambiguationData":[OSD([sQuery(id+"F0.wireOp",EDGE,"E2")])],"isStart":true});
            var Q4;
            {var subQ0=sQuery(id+"F0.wireOp",EDGE,"E9");var subQ1=sQuery(id+"F0.wireOp",EDGE,"E8");Q4=makeQuery(id+"F4.opFillet","BLEND_EDGE",EDGE,{"blendedFrom":[makeQuery(id+"F1.opExtrude","SWEPT_EDGE",EDGE,{"disambiguationData":[OSD([subQ1,subQ0])]}),makeQuery(id+"F1.opExtrude","CAP_FACE",FACE,{"disambiguationData":[OSD([sQuery(id+"F0.wireOp",EDGE,"E0"),sQuery(id+"F0.wireOp",EDGE,"E1"),sQuery(id+"F0.wireOp",EDGE,"E2"),sQuery(id+"F0.wireOp",EDGE,"E3"),subQ1,subQ0,sQuery(id+"F0.wireOp",EDGE,"E12"),sQuery(id+"F0.wireOp",EDGE,"E14"),sQuery(id+"F0.wireOp",EDGE,"E15")])],"isStart":false})],"blendedInto":[makeQuery(id+"F1.opExtrude","CAP_FACE",FACE,{"disambiguationData":[OSD([sQuery(id+"F0.wireOp",EDGE,"E0"),sQuery(id+"F0.wireOp",EDGE,"E1"),sQuery(id+"F0.wireOp",EDGE,"E2"),sQuery(id+"F0.wireOp",EDGE,"E3"),subQ1,subQ0,sQuery(id+"F0.wireOp",EDGE,"E12"),sQuery(id+"F0.wireOp",EDGE,"E14"),sQuery(id+"F0.wireOp",EDGE,"E15")])],"isStart":false})]});}
            var Q5;
            {var subQ0=sQuery(id+"F0.wireOp",EDGE,"E9");var subQ1=sQuery(id+"F0.wireOp",EDGE,"E8");Q5=makeQuery(id+"F4.opFillet","BLEND_EDGE",EDGE,{"blendedFrom":[makeQuery(id+"F1.opExtrude","SWEPT_EDGE",EDGE,{"disambiguationData":[OSD([subQ1,subQ0])]}),makeQuery(id+"F1.opExtrude","CAP_FACE",FACE,{"disambiguationData":[OSD([sQuery(id+"F0.wireOp",EDGE,"E0"),sQuery(id+"F0.wireOp",EDGE,"E1"),sQuery(id+"F0.wireOp",EDGE,"E2"),sQuery(id+"F0.wireOp",EDGE,"E3"),subQ1,subQ0,sQuery(id+"F0.wireOp",EDGE,"E12"),sQuery(id+"F0.wireOp",EDGE,"E14"),sQuery(id+"F0.wireOp",EDGE,"E15")])],"isStart":true})],"blendedInto":[makeQuery(id+"F1.opExtrude","CAP_FACE",FACE,{"disambiguationData":[OSD([sQuery(id+"F0.wireOp",EDGE,"E0"),sQuery(id+"F0.wireOp",EDGE,"E1"),sQuery(id+"F0.wireOp",EDGE,"E2"),sQuery(id+"F0.wireOp",EDGE,"E3"),subQ1,subQ0,sQuery(id+"F0.wireOp",EDGE,"E12"),sQuery(id+"F0.wireOp",EDGE,"E14"),sQuery(id+"F0.wireOp",EDGE,"E15")])],"isStart":true})]});}
            fillet(context, id + "F6", {"entities" : qUnion([Q0, Q1, Q2, Q3, Q4, Q5]), "radius" : 2 * mm, "tangentPropagation" : true, "allowEdgeOverflow" : false});
        }
        {
            var Q0;
            {var subQ0=sQuery(id+"F0.wireOp",EDGE,"E4");Q0=makeQuery(id+"F2.opExtrude","CAP_EDGE",EDGE,{"disambiguationData":[OSD([subQ0]),TDD([makeQuery(id+"F0.imprint","IMPRINT",EDGE,{"disambiguationData":[TD([[makeQuery(id+"F0.imprint","INTERSECT",VERTEX,{"derivedFrom":[subQ0,sQuery(id+"F0.wireOp",EDGE,"E16")]}),1.0]])],"derivedFrom":subQ0})])],"isStart":false});}
            var Q1;
            {var subQ0=sQuery(id+"F0.wireOp",EDGE,"E20");Q1=makeQuery(id+"F2.opExtrude","CAP_EDGE",EDGE,{"disambiguationData":[OSD([subQ0]),TDD([makeQuery(id+"F0.imprint","IMPRINT",EDGE,{"disambiguationData":[TD([[makeQuery(id+"F0.imprint","INTERSECT",VERTEX,{"derivedFrom":[sQuery(id+"F0.wireOp",EDGE,"E16"),subQ0]}),1.0]])],"derivedFrom":subQ0})])],"isStart":false});}
            chamfer(context, id + "F7", {"entities" : qUnion([Q0, Q1]), "chamferType" : ChamferType.TWO_OFFSETS, "width1" : 0.3 * mm, "oppositeDirection" : true, "width2" : 5 * mm, "tangentPropagation" : true});
        }
        {
            var Q0;
            {var subQ0=sQuery(id+"F0.wireOp",EDGE,"E4");Q0=makeQuery(id+"F2.opExtrude","CAP_EDGE",EDGE,{"disambiguationData":[OSD([subQ0]),TDD([makeQuery(id+"F0.imprint","IMPRINT",EDGE,{"disambiguationData":[TD([[makeQuery(id+"F0.imprint","INTERSECT",VERTEX,{"derivedFrom":[subQ0,sQuery(id+"F0.wireOp",EDGE,"E18.1.0")]}),1.0]])],"derivedFrom":subQ0})])],"isStart":false});}
            var Q1;
            {var subQ0=sQuery(id+"F0.wireOp",EDGE,"E4");Q1=makeQuery(id+"F2.opExtrude","CAP_EDGE",EDGE,{"disambiguationData":[OSD([subQ0]),TDD([makeQuery(id+"F0.imprint","IMPRINT",EDGE,{"disambiguationData":[TD([[makeQuery(id+"F0.imprint","INTERSECT",VERTEX,{"derivedFrom":[subQ0,sQuery(id+"F0.wireOp",EDGE,"E18.2.0")]}),1.0]])],"derivedFrom":subQ0})])],"isStart":false});}
            var Q2;
            {var subQ0=sQuery(id+"F0.wireOp",EDGE,"E4");Q2=makeQuery(id+"F2.opExtrude","CAP_EDGE",EDGE,{"disambiguationData":[OSD([subQ0]),TDD([makeQuery(id+"F0.imprint","IMPRINT",EDGE,{"disambiguationData":[TD([[makeQuery(id+"F0.imprint","INTERSECT",VERTEX,{"derivedFrom":[subQ0,sQuery(id+"F0.wireOp",EDGE,"E19.1.3.0")]}),1.0]])],"derivedFrom":subQ0})])],"isStart":false});}
            var Q3;
            {var subQ0=sQuery(id+"F0.wireOp",EDGE,"E4");Q3=makeQuery(id+"F2.opExtrude","CAP_EDGE",EDGE,{"disambiguationData":[OSD([subQ0]),TDD([makeQuery(id+"F0.imprint","IMPRINT",EDGE,{"disambiguationData":[TD([[makeQuery(id+"F0.imprint","INTERSECT",VERTEX,{"derivedFrom":[subQ0,sQuery(id+"F0.wireOp",EDGE,"E19.1.4.0")]}),1.0]])],"derivedFrom":subQ0})])],"isStart":false});}
            var Q4;
            {var subQ0=sQuery(id+"F0.wireOp",EDGE,"E4");Q4=makeQuery(id+"F2.opExtrude","CAP_EDGE",EDGE,{"disambiguationData":[OSD([subQ0]),TDD([makeQuery(id+"F0.imprint","IMPRINT",EDGE,{"disambiguationData":[TD([[makeQuery(id+"F0.imprint","INTERSECT",VERTEX,{"derivedFrom":[subQ0,sQuery(id+"F0.wireOp",EDGE,"E19.1.5.0")]}),1.0]])],"derivedFrom":subQ0})])],"isStart":false});}
            var Q5;
            {var subQ0=sQuery(id+"F0.wireOp",EDGE,"E4");Q5=makeQuery(id+"F2.opExtrude","CAP_EDGE",EDGE,{"disambiguationData":[OSD([subQ0]),TDD([makeQuery(id+"F0.imprint","IMPRINT",EDGE,{"disambiguationData":[TD([[makeQuery(id+"F0.imprint","INTERSECT",VERTEX,{"derivedFrom":[subQ0,sQuery(id+"F0.wireOp",EDGE,"E19.1.6.0")]}),1.0]])],"derivedFrom":subQ0})])],"isStart":false});}
            var Q6;
            {var subQ0=sQuery(id+"F0.wireOp",EDGE,"E4");Q6=makeQuery(id+"F2.opExtrude","CAP_EDGE",EDGE,{"disambiguationData":[OSD([subQ0]),TDD([makeQuery(id+"F0.imprint","IMPRINT",EDGE,{"disambiguationData":[TD([[makeQuery(id+"F0.imprint","INTERSECT",VERTEX,{"derivedFrom":[subQ0,sQuery(id+"F0.wireOp",EDGE,"E19.1.7.0")]}),1.0]])],"derivedFrom":subQ0})])],"isStart":false});}
            var Q7;
            {var subQ0=sQuery(id+"F0.wireOp",EDGE,"E4");Q7=makeQuery(id+"F2.opExtrude","CAP_EDGE",EDGE,{"disambiguationData":[OSD([subQ0]),TDD([makeQuery(id+"F0.imprint","IMPRINT",EDGE,{"disambiguationData":[TD([[makeQuery(id+"F0.imprint","INTERSECT",VERTEX,{"derivedFrom":[subQ0,sQuery(id+"F0.wireOp",EDGE,"E19.1.8.0")]}),1.0]])],"derivedFrom":subQ0})])],"isStart":false});}
            var Q8;
            {var subQ0=sQuery(id+"F0.wireOp",EDGE,"E4");Q8=makeQuery(id+"F2.opExtrude","CAP_EDGE",EDGE,{"disambiguationData":[OSD([subQ0]),TDD([makeQuery(id+"F0.imprint","IMPRINT",EDGE,{"disambiguationData":[TD([[makeQuery(id+"F0.imprint","INTERSECT",VERTEX,{"derivedFrom":[subQ0,sQuery(id+"F0.wireOp",EDGE,"E19.1.9.0")]}),1.0]])],"derivedFrom":subQ0})])],"isStart":false});}
            var Q9;
            {var subQ0=sQuery(id+"F0.wireOp",EDGE,"E4");Q9=makeQuery(id+"F2.opExtrude","CAP_EDGE",EDGE,{"disambiguationData":[OSD([subQ0]),TDD([makeQuery(id+"F0.imprint","IMPRINT",EDGE,{"disambiguationData":[TD([[makeQuery(id+"F0.imprint","INTERSECT",VERTEX,{"derivedFrom":[subQ0,sQuery(id+"F0.wireOp",EDGE,"E19.1.10.0")]}),1.0]])],"derivedFrom":subQ0})])],"isStart":false});}
            var Q10;
            {var subQ0=sQuery(id+"F0.wireOp",EDGE,"E4");Q10=makeQuery(id+"F2.opExtrude","CAP_EDGE",EDGE,{"disambiguationData":[OSD([subQ0]),TDD([makeQuery(id+"F0.imprint","IMPRINT",EDGE,{"disambiguationData":[TD([[makeQuery(id+"F0.imprint","INTERSECT",VERTEX,{"derivedFrom":[subQ0,sQuery(id+"F0.wireOp",EDGE,"E19.1.11.0")]}),1.0]])],"derivedFrom":subQ0})])],"isStart":false});}
            var Q11;
            {var subQ0=sQuery(id+"F0.wireOp",EDGE,"E4");Q11=makeQuery(id+"F2.opExtrude","CAP_EDGE",EDGE,{"disambiguationData":[OSD([subQ0]),TDD([makeQuery(id+"F0.imprint","IMPRINT",EDGE,{"disambiguationData":[TD([[makeQuery(id+"F0.imprint","INTERSECT",VERTEX,{"derivedFrom":[subQ0,sQuery(id+"F0.wireOp",EDGE,"E19.1.12.0")]}),1.0]])],"derivedFrom":subQ0})])],"isStart":false});}
            var Q12;
            {var subQ0=sQuery(id+"F0.wireOp",EDGE,"E20");Q12=makeQuery(id+"F2.opExtrude","CAP_EDGE",EDGE,{"disambiguationData":[OSD([subQ0]),TDD([makeQuery(id+"F0.imprint","IMPRINT",EDGE,{"disambiguationData":[TD([[makeQuery(id+"F0.imprint","INTERSECT",VERTEX,{"derivedFrom":[sQuery(id+"F0.wireOp",EDGE,"E19.1.12.0"),subQ0]}),1.0]])],"derivedFrom":subQ0})])],"isStart":true});}
            var Q13;
            {var subQ0=sQuery(id+"F0.wireOp",EDGE,"E20");Q13=makeQuery(id+"F2.opExtrude","CAP_EDGE",EDGE,{"disambiguationData":[OSD([subQ0]),TDD([makeQuery(id+"F0.imprint","IMPRINT",EDGE,{"disambiguationData":[TD([[makeQuery(id+"F0.imprint","INTERSECT",VERTEX,{"derivedFrom":[sQuery(id+"F0.wireOp",EDGE,"E19.1.11.0"),subQ0]}),1.0]])],"derivedFrom":subQ0})])],"isStart":true});}
            var Q14;
            {var subQ0=sQuery(id+"F0.wireOp",EDGE,"E20");Q14=makeQuery(id+"F2.opExtrude","CAP_EDGE",EDGE,{"disambiguationData":[OSD([subQ0]),TDD([makeQuery(id+"F0.imprint","IMPRINT",EDGE,{"disambiguationData":[TD([[makeQuery(id+"F0.imprint","INTERSECT",VERTEX,{"derivedFrom":[sQuery(id+"F0.wireOp",EDGE,"E19.1.10.0"),subQ0]}),1.0]])],"derivedFrom":subQ0})])],"isStart":true});}
            var Q15;
            {var subQ0=sQuery(id+"F0.wireOp",EDGE,"E20");Q15=makeQuery(id+"F2.opExtrude","CAP_EDGE",EDGE,{"disambiguationData":[OSD([subQ0]),TDD([makeQuery(id+"F0.imprint","IMPRINT",EDGE,{"disambiguationData":[TD([[makeQuery(id+"F0.imprint","INTERSECT",VERTEX,{"derivedFrom":[sQuery(id+"F0.wireOp",EDGE,"E19.1.9.0"),subQ0]}),1.0]])],"derivedFrom":subQ0})])],"isStart":true});}
            var Q16;
            {var subQ0=sQuery(id+"F0.wireOp",EDGE,"E20");Q16=makeQuery(id+"F2.opExtrude","CAP_EDGE",EDGE,{"disambiguationData":[OSD([subQ0]),TDD([makeQuery(id+"F0.imprint","IMPRINT",EDGE,{"disambiguationData":[TD([[makeQuery(id+"F0.imprint","INTERSECT",VERTEX,{"derivedFrom":[sQuery(id+"F0.wireOp",EDGE,"E19.1.8.0"),subQ0]}),1.0]])],"derivedFrom":subQ0})])],"isStart":true});}
            var Q17;
            {var subQ0=sQuery(id+"F0.wireOp",EDGE,"E20");Q17=makeQuery(id+"F2.opExtrude","CAP_EDGE",EDGE,{"disambiguationData":[OSD([subQ0]),TDD([makeQuery(id+"F0.imprint","IMPRINT",EDGE,{"disambiguationData":[TD([[makeQuery(id+"F0.imprint","INTERSECT",VERTEX,{"derivedFrom":[sQuery(id+"F0.wireOp",EDGE,"E19.1.7.0"),subQ0]}),1.0]])],"derivedFrom":subQ0})])],"isStart":true});}
            var Q18;
            {var subQ0=sQuery(id+"F0.wireOp",EDGE,"E20");Q18=makeQuery(id+"F2.opExtrude","CAP_EDGE",EDGE,{"disambiguationData":[OSD([subQ0]),TDD([makeQuery(id+"F0.imprint","IMPRINT",EDGE,{"disambiguationData":[TD([[makeQuery(id+"F0.imprint","INTERSECT",VERTEX,{"derivedFrom":[sQuery(id+"F0.wireOp",EDGE,"E19.1.6.0"),subQ0]}),1.0]])],"derivedFrom":subQ0})])],"isStart":true});}
            var Q19;
            {var subQ0=sQuery(id+"F0.wireOp",EDGE,"E20");Q19=makeQuery(id+"F2.opExtrude","CAP_EDGE",EDGE,{"disambiguationData":[OSD([subQ0]),TDD([makeQuery(id+"F0.imprint","IMPRINT",EDGE,{"disambiguationData":[TD([[makeQuery(id+"F0.imprint","INTERSECT",VERTEX,{"derivedFrom":[sQuery(id+"F0.wireOp",EDGE,"E19.1.5.0"),subQ0]}),1.0]])],"derivedFrom":subQ0})])],"isStart":true});}
            var Q20;
            {var subQ0=sQuery(id+"F0.wireOp",EDGE,"E20");Q20=makeQuery(id+"F2.opExtrude","CAP_EDGE",EDGE,{"disambiguationData":[OSD([subQ0]),TDD([makeQuery(id+"F0.imprint","IMPRINT",EDGE,{"disambiguationData":[TD([[makeQuery(id+"F0.imprint","INTERSECT",VERTEX,{"derivedFrom":[sQuery(id+"F0.wireOp",EDGE,"E16"),subQ0]}),1.0]])],"derivedFrom":subQ0})])],"isStart":true});}
            var Q21;
            {var subQ0=sQuery(id+"F0.wireOp",EDGE,"E20");Q21=makeQuery(id+"F2.opExtrude","CAP_EDGE",EDGE,{"disambiguationData":[OSD([subQ0]),TDD([makeQuery(id+"F0.imprint","IMPRINT",EDGE,{"disambiguationData":[TD([[makeQuery(id+"F0.imprint","INTERSECT",VERTEX,{"derivedFrom":[sQuery(id+"F0.wireOp",EDGE,"E18.1.0"),subQ0]}),1.0]])],"derivedFrom":subQ0})])],"isStart":true});}
            var Q22;
            {var subQ0=sQuery(id+"F0.wireOp",EDGE,"E20");Q22=makeQuery(id+"F2.opExtrude","CAP_EDGE",EDGE,{"disambiguationData":[OSD([subQ0]),TDD([makeQuery(id+"F0.imprint","IMPRINT",EDGE,{"disambiguationData":[TD([[makeQuery(id+"F0.imprint","INTERSECT",VERTEX,{"derivedFrom":[sQuery(id+"F0.wireOp",EDGE,"E18.2.0"),subQ0]}),1.0]])],"derivedFrom":subQ0})])],"isStart":true});}
            var Q23;
            {var subQ0=sQuery(id+"F0.wireOp",EDGE,"E20");Q23=makeQuery(id+"F2.opExtrude","CAP_EDGE",EDGE,{"disambiguationData":[OSD([subQ0]),TDD([makeQuery(id+"F0.imprint","IMPRINT",EDGE,{"disambiguationData":[TD([[makeQuery(id+"F0.imprint","INTERSECT",VERTEX,{"derivedFrom":[sQuery(id+"F0.wireOp",EDGE,"E19.1.3.0"),subQ0]}),1.0]])],"derivedFrom":subQ0})])],"isStart":true});}
            var Q24;
            {var subQ0=sQuery(id+"F0.wireOp",EDGE,"E20");Q24=makeQuery(id+"F2.opExtrude","CAP_EDGE",EDGE,{"disambiguationData":[OSD([subQ0]),TDD([makeQuery(id+"F0.imprint","IMPRINT",EDGE,{"disambiguationData":[TD([[makeQuery(id+"F0.imprint","INTERSECT",VERTEX,{"derivedFrom":[sQuery(id+"F0.wireOp",EDGE,"E19.1.4.0"),subQ0]}),1.0]])],"derivedFrom":subQ0})])],"isStart":true});}
            chamfer(context, id + "F8", {"entities" : qUnion([Q0, Q1, Q2, Q3, Q4, Q5, Q6, Q7, Q8, Q9, Q10, Q11, Q12, Q13, Q14, Q15, Q16, Q17, Q18, Q19, Q20, Q21, Q22, Q23, Q24]), "chamferType" : ChamferType.TWO_OFFSETS, "width1" : 0.3 * mm, "oppositeDirection" : true, "width2" : 5 * mm, "tangentPropagation" : true});
        }
        {
            var Q0;
            {var subQ0=sQuery(id+"F0.wireOp",EDGE,"E4");Q0=makeQuery(id+"F2.opExtrude","CAP_EDGE",EDGE,{"disambiguationData":[OSD([subQ0]),TDD([makeQuery(id+"F0.imprint","IMPRINT",EDGE,{"disambiguationData":[TD([[makeQuery(id+"F0.imprint","INTERSECT",VERTEX,{"derivedFrom":[subQ0,sQuery(id+"F0.wireOp",EDGE,"E19.1.12.0")]}),1.0]])],"derivedFrom":subQ0})])],"isStart":true});}
            var Q1;
            {var subQ0=sQuery(id+"F0.wireOp",EDGE,"E4");Q1=makeQuery(id+"F2.opExtrude","CAP_EDGE",EDGE,{"disambiguationData":[OSD([subQ0]),TDD([makeQuery(id+"F0.imprint","IMPRINT",EDGE,{"disambiguationData":[TD([[makeQuery(id+"F0.imprint","INTERSECT",VERTEX,{"derivedFrom":[subQ0,sQuery(id+"F0.wireOp",EDGE,"E19.1.11.0")]}),1.0]])],"derivedFrom":subQ0})])],"isStart":true});}
            var Q2;
            {var subQ0=sQuery(id+"F0.wireOp",EDGE,"E4");Q2=makeQuery(id+"F2.opExtrude","CAP_EDGE",EDGE,{"disambiguationData":[OSD([subQ0]),TDD([makeQuery(id+"F0.imprint","IMPRINT",EDGE,{"disambiguationData":[TD([[makeQuery(id+"F0.imprint","INTERSECT",VERTEX,{"derivedFrom":[subQ0,sQuery(id+"F0.wireOp",EDGE,"E19.1.10.0")]}),1.0]])],"derivedFrom":subQ0})])],"isStart":true});}
            var Q3;
            {var subQ0=sQuery(id+"F0.wireOp",EDGE,"E4");Q3=makeQuery(id+"F2.opExtrude","CAP_EDGE",EDGE,{"disambiguationData":[OSD([subQ0]),TDD([makeQuery(id+"F0.imprint","IMPRINT",EDGE,{"disambiguationData":[TD([[makeQuery(id+"F0.imprint","INTERSECT",VERTEX,{"derivedFrom":[subQ0,sQuery(id+"F0.wireOp",EDGE,"E19.1.9.0")]}),1.0]])],"derivedFrom":subQ0})])],"isStart":true});}
            var Q4;
            {var subQ0=sQuery(id+"F0.wireOp",EDGE,"E4");Q4=makeQuery(id+"F2.opExtrude","CAP_EDGE",EDGE,{"disambiguationData":[OSD([subQ0]),TDD([makeQuery(id+"F0.imprint","IMPRINT",EDGE,{"disambiguationData":[TD([[makeQuery(id+"F0.imprint","INTERSECT",VERTEX,{"derivedFrom":[subQ0,sQuery(id+"F0.wireOp",EDGE,"E19.1.8.0")]}),1.0]])],"derivedFrom":subQ0})])],"isStart":true});}
            var Q5;
            {var subQ0=sQuery(id+"F0.wireOp",EDGE,"E4");Q5=makeQuery(id+"F2.opExtrude","CAP_EDGE",EDGE,{"disambiguationData":[OSD([subQ0]),TDD([makeQuery(id+"F0.imprint","IMPRINT",EDGE,{"disambiguationData":[TD([[makeQuery(id+"F0.imprint","INTERSECT",VERTEX,{"derivedFrom":[subQ0,sQuery(id+"F0.wireOp",EDGE,"E19.1.7.0")]}),1.0]])],"derivedFrom":subQ0})])],"isStart":true});}
            var Q6;
            {var subQ0=sQuery(id+"F0.wireOp",EDGE,"E4");Q6=makeQuery(id+"F2.opExtrude","CAP_EDGE",EDGE,{"disambiguationData":[OSD([subQ0]),TDD([makeQuery(id+"F0.imprint","IMPRINT",EDGE,{"disambiguationData":[TD([[makeQuery(id+"F0.imprint","INTERSECT",VERTEX,{"derivedFrom":[subQ0,sQuery(id+"F0.wireOp",EDGE,"E19.1.6.0")]}),1.0]])],"derivedFrom":subQ0})])],"isStart":true});}
            var Q7;
            {var subQ0=sQuery(id+"F0.wireOp",EDGE,"E4");Q7=makeQuery(id+"F2.opExtrude","CAP_EDGE",EDGE,{"disambiguationData":[OSD([subQ0]),TDD([makeQuery(id+"F0.imprint","IMPRINT",EDGE,{"disambiguationData":[TD([[makeQuery(id+"F0.imprint","INTERSECT",VERTEX,{"derivedFrom":[subQ0,sQuery(id+"F0.wireOp",EDGE,"E19.1.5.0")]}),1.0]])],"derivedFrom":subQ0})])],"isStart":true});}
            var Q8;
            {var subQ0=sQuery(id+"F0.wireOp",EDGE,"E4");Q8=makeQuery(id+"F2.opExtrude","CAP_EDGE",EDGE,{"disambiguationData":[OSD([subQ0]),TDD([makeQuery(id+"F0.imprint","IMPRINT",EDGE,{"disambiguationData":[TD([[makeQuery(id+"F0.imprint","INTERSECT",VERTEX,{"derivedFrom":[subQ0,sQuery(id+"F0.wireOp",EDGE,"E19.1.4.0")]}),1.0]])],"derivedFrom":subQ0})])],"isStart":true});}
            var Q9;
            {var subQ0=sQuery(id+"F0.wireOp",EDGE,"E4");Q9=makeQuery(id+"F2.opExtrude","CAP_EDGE",EDGE,{"disambiguationData":[OSD([subQ0]),TDD([makeQuery(id+"F0.imprint","IMPRINT",EDGE,{"disambiguationData":[TD([[makeQuery(id+"F0.imprint","INTERSECT",VERTEX,{"derivedFrom":[subQ0,sQuery(id+"F0.wireOp",EDGE,"E19.1.3.0")]}),1.0]])],"derivedFrom":subQ0})])],"isStart":true});}
            var Q10;
            {var subQ0=sQuery(id+"F0.wireOp",EDGE,"E4");Q10=makeQuery(id+"F2.opExtrude","CAP_EDGE",EDGE,{"disambiguationData":[OSD([subQ0]),TDD([makeQuery(id+"F0.imprint","IMPRINT",EDGE,{"disambiguationData":[TD([[makeQuery(id+"F0.imprint","INTERSECT",VERTEX,{"derivedFrom":[subQ0,sQuery(id+"F0.wireOp",EDGE,"E18.2.0")]}),1.0]])],"derivedFrom":subQ0})])],"isStart":true});}
            var Q11;
            {var subQ0=sQuery(id+"F0.wireOp",EDGE,"E4");Q11=makeQuery(id+"F2.opExtrude","CAP_EDGE",EDGE,{"disambiguationData":[OSD([subQ0]),TDD([makeQuery(id+"F0.imprint","IMPRINT",EDGE,{"disambiguationData":[TD([[makeQuery(id+"F0.imprint","INTERSECT",VERTEX,{"derivedFrom":[subQ0,sQuery(id+"F0.wireOp",EDGE,"E18.1.0")]}),1.0]])],"derivedFrom":subQ0})])],"isStart":true});}
            var Q12;
            {var subQ0=sQuery(id+"F0.wireOp",EDGE,"E4");Q12=makeQuery(id+"F2.opExtrude","CAP_EDGE",EDGE,{"disambiguationData":[OSD([subQ0]),TDD([makeQuery(id+"F0.imprint","IMPRINT",EDGE,{"disambiguationData":[TD([[makeQuery(id+"F0.imprint","INTERSECT",VERTEX,{"derivedFrom":[subQ0,sQuery(id+"F0.wireOp",EDGE,"E16")]}),1.0]])],"derivedFrom":subQ0})])],"isStart":true});}
            var Q13;
            {var subQ0=sQuery(id+"F0.wireOp",EDGE,"E20");Q13=makeQuery(id+"F2.opExtrude","CAP_EDGE",EDGE,{"disambiguationData":[OSD([subQ0]),TDD([makeQuery(id+"F0.imprint","IMPRINT",EDGE,{"disambiguationData":[TD([[makeQuery(id+"F0.imprint","INTERSECT",VERTEX,{"derivedFrom":[sQuery(id+"F0.wireOp",EDGE,"E18.1.0"),subQ0]}),1.0]])],"derivedFrom":subQ0})])],"isStart":false});}
            var Q14;
            {var subQ0=sQuery(id+"F0.wireOp",EDGE,"E20");Q14=makeQuery(id+"F2.opExtrude","CAP_EDGE",EDGE,{"disambiguationData":[OSD([subQ0]),TDD([makeQuery(id+"F0.imprint","IMPRINT",EDGE,{"disambiguationData":[TD([[makeQuery(id+"F0.imprint","INTERSECT",VERTEX,{"derivedFrom":[sQuery(id+"F0.wireOp",EDGE,"E18.2.0"),subQ0]}),1.0]])],"derivedFrom":subQ0})])],"isStart":false});}
            var Q15;
            {var subQ0=sQuery(id+"F0.wireOp",EDGE,"E20");Q15=makeQuery(id+"F2.opExtrude","CAP_EDGE",EDGE,{"disambiguationData":[OSD([subQ0]),TDD([makeQuery(id+"F0.imprint","IMPRINT",EDGE,{"disambiguationData":[TD([[makeQuery(id+"F0.imprint","INTERSECT",VERTEX,{"derivedFrom":[sQuery(id+"F0.wireOp",EDGE,"E19.1.3.0"),subQ0]}),1.0]])],"derivedFrom":subQ0})])],"isStart":false});}
            var Q16;
            {var subQ0=sQuery(id+"F0.wireOp",EDGE,"E20");Q16=makeQuery(id+"F2.opExtrude","CAP_EDGE",EDGE,{"disambiguationData":[OSD([subQ0]),TDD([makeQuery(id+"F0.imprint","IMPRINT",EDGE,{"disambiguationData":[TD([[makeQuery(id+"F0.imprint","INTERSECT",VERTEX,{"derivedFrom":[sQuery(id+"F0.wireOp",EDGE,"E19.1.4.0"),subQ0]}),1.0]])],"derivedFrom":subQ0})])],"isStart":false});}
            var Q17;
            {var subQ0=sQuery(id+"F0.wireOp",EDGE,"E20");Q17=makeQuery(id+"F2.opExtrude","CAP_EDGE",EDGE,{"disambiguationData":[OSD([subQ0]),TDD([makeQuery(id+"F0.imprint","IMPRINT",EDGE,{"disambiguationData":[TD([[makeQuery(id+"F0.imprint","INTERSECT",VERTEX,{"derivedFrom":[sQuery(id+"F0.wireOp",EDGE,"E19.1.5.0"),subQ0]}),1.0]])],"derivedFrom":subQ0})])],"isStart":false});}
            var Q18;
            {var subQ0=sQuery(id+"F0.wireOp",EDGE,"E20");Q18=makeQuery(id+"F2.opExtrude","CAP_EDGE",EDGE,{"disambiguationData":[OSD([subQ0]),TDD([makeQuery(id+"F0.imprint","IMPRINT",EDGE,{"disambiguationData":[TD([[makeQuery(id+"F0.imprint","INTERSECT",VERTEX,{"derivedFrom":[sQuery(id+"F0.wireOp",EDGE,"E19.1.6.0"),subQ0]}),1.0]])],"derivedFrom":subQ0})])],"isStart":false});}
            var Q19;
            {var subQ0=sQuery(id+"F0.wireOp",EDGE,"E20");Q19=makeQuery(id+"F2.opExtrude","CAP_EDGE",EDGE,{"disambiguationData":[OSD([subQ0]),TDD([makeQuery(id+"F0.imprint","IMPRINT",EDGE,{"disambiguationData":[TD([[makeQuery(id+"F0.imprint","INTERSECT",VERTEX,{"derivedFrom":[sQuery(id+"F0.wireOp",EDGE,"E19.1.7.0"),subQ0]}),1.0]])],"derivedFrom":subQ0})])],"isStart":false});}
            var Q20;
            {var subQ0=sQuery(id+"F0.wireOp",EDGE,"E20");Q20=makeQuery(id+"F2.opExtrude","CAP_EDGE",EDGE,{"disambiguationData":[OSD([subQ0]),TDD([makeQuery(id+"F0.imprint","IMPRINT",EDGE,{"disambiguationData":[TD([[makeQuery(id+"F0.imprint","INTERSECT",VERTEX,{"derivedFrom":[sQuery(id+"F0.wireOp",EDGE,"E19.1.8.0"),subQ0]}),1.0]])],"derivedFrom":subQ0})])],"isStart":false});}
            var Q21;
            {var subQ0=sQuery(id+"F0.wireOp",EDGE,"E20");Q21=makeQuery(id+"F2.opExtrude","CAP_EDGE",EDGE,{"disambiguationData":[OSD([subQ0]),TDD([makeQuery(id+"F0.imprint","IMPRINT",EDGE,{"disambiguationData":[TD([[makeQuery(id+"F0.imprint","INTERSECT",VERTEX,{"derivedFrom":[sQuery(id+"F0.wireOp",EDGE,"E19.1.9.0"),subQ0]}),1.0]])],"derivedFrom":subQ0})])],"isStart":false});}
            var Q22;
            {var subQ0=sQuery(id+"F0.wireOp",EDGE,"E20");Q22=makeQuery(id+"F2.opExtrude","CAP_EDGE",EDGE,{"disambiguationData":[OSD([subQ0]),TDD([makeQuery(id+"F0.imprint","IMPRINT",EDGE,{"disambiguationData":[TD([[makeQuery(id+"F0.imprint","INTERSECT",VERTEX,{"derivedFrom":[sQuery(id+"F0.wireOp",EDGE,"E19.1.10.0"),subQ0]}),1.0]])],"derivedFrom":subQ0})])],"isStart":false});}
            var Q23;
            {var subQ0=sQuery(id+"F0.wireOp",EDGE,"E20");Q23=makeQuery(id+"F2.opExtrude","CAP_EDGE",EDGE,{"disambiguationData":[OSD([subQ0]),TDD([makeQuery(id+"F0.imprint","IMPRINT",EDGE,{"disambiguationData":[TD([[makeQuery(id+"F0.imprint","INTERSECT",VERTEX,{"derivedFrom":[sQuery(id+"F0.wireOp",EDGE,"E19.1.11.0"),subQ0]}),1.0]])],"derivedFrom":subQ0})])],"isStart":false});}
            var Q24;
            {var subQ0=sQuery(id+"F0.wireOp",EDGE,"E20");Q24=makeQuery(id+"F2.opExtrude","CAP_EDGE",EDGE,{"disambiguationData":[OSD([subQ0]),TDD([makeQuery(id+"F0.imprint","IMPRINT",EDGE,{"disambiguationData":[TD([[makeQuery(id+"F0.imprint","INTERSECT",VERTEX,{"derivedFrom":[sQuery(id+"F0.wireOp",EDGE,"E19.1.12.0"),subQ0]}),1.0]])],"derivedFrom":subQ0})])],"isStart":false});}
            chamfer(context, id + "F9", {"entities" : qUnion([Q0, Q1, Q2, Q3, Q4, Q5, Q6, Q7, Q8, Q9, Q10, Q11, Q12, Q13, Q14, Q15, Q16, Q17, Q18, Q19, Q20, Q21, Q22, Q23, Q24]), "chamferType" : ChamferType.TWO_OFFSETS, "width1" : 0.3 * mm, "oppositeDirection" : false, "width2" : 5 * mm, "tangentPropagation" : true});
        }
        {
            var Q0;
            {var subQ0=sQuery(id+"F0.wireOp",EDGE,"E16");var subQ1=sQuery(id+"F0.wireOp",EDGE,"E4");var subQ2=sQuery(id+"F0.wireOp",EDGE,"E17");var subQ3=makeQuery(id+"F0.imprint","IMPRINT",EDGE,{"disambiguationData":[TD([[makeQuery(id+"F0.imprint","INTERSECT",VERTEX,{"derivedFrom":[subQ1,subQ0]}),1.0]])],"derivedFrom":subQ1});var subQ4=sQuery(id+"F0.wireOp",EDGE,"E20");Q0=makeQuery(id+"F7.opChamfer","BLEND_EDGE",EDGE,{"blendedFrom":[makeQuery(id+"F2.opExtrude","CAP_EDGE",EDGE,{"disambiguationData":[OSD([subQ1]),TDD([subQ3])],"isStart":false}),makeQuery(id+"F2.boolean.opBoolean","SPLIT",FACE,{"disambiguationData":[TD([makeQuery(id+"F2.opExtrude","CAP_FACE",FACE,{"disambiguationData":[OSD([subQ1,subQ0,subQ2,subQ4])],"isStart":false})])],"derivedFrom":makeQuery(id+"F2.opExtrude","SWEPT_FACE",FACE,{"disambiguationData":[OSD([subQ0])]})})],"blendedInto":[makeQuery(id+"F2.boolean.opBoolean","SPLIT",FACE,{"disambiguationData":[TD([makeQuery(id+"F2.opExtrude","CAP_FACE",FACE,{"disambiguationData":[OSD([subQ1,subQ0,subQ2,subQ4])],"isStart":false})])],"derivedFrom":makeQuery(id+"F2.opExtrude","SWEPT_FACE",FACE,{"disambiguationData":[OSD([subQ0])]})})]});}
            var Q1;
            {var subQ0=sQuery(id+"F0.wireOp",EDGE,"E16");var subQ1=sQuery(id+"F0.wireOp",EDGE,"E4");var subQ2=sQuery(id+"F0.wireOp",EDGE,"E17");var subQ3=makeQuery(id+"F0.imprint","IMPRINT",EDGE,{"disambiguationData":[TD([[makeQuery(id+"F0.imprint","INTERSECT",VERTEX,{"derivedFrom":[subQ1,subQ0]}),1.0]])],"derivedFrom":subQ1});var subQ4=sQuery(id+"F0.wireOp",EDGE,"E20");Q1=makeQuery(id+"F7.opChamfer","BLEND_EDGE",EDGE,{"blendedFrom":[makeQuery(id+"F2.opExtrude","CAP_EDGE",EDGE,{"disambiguationData":[OSD([subQ1]),TDD([subQ3])],"isStart":false}),makeQuery(id+"F2.boolean.opBoolean","SPLIT",FACE,{"disambiguationData":[TD([makeQuery(id+"F2.opExtrude","CAP_FACE",FACE,{"disambiguationData":[OSD([subQ1,subQ0,subQ2,subQ4])],"isStart":false})])],"derivedFrom":makeQuery(id+"F2.opExtrude","SWEPT_FACE",FACE,{"disambiguationData":[OSD([subQ2])]})})],"blendedInto":[makeQuery(id+"F2.boolean.opBoolean","SPLIT",FACE,{"disambiguationData":[TD([makeQuery(id+"F2.opExtrude","CAP_FACE",FACE,{"disambiguationData":[OSD([subQ1,subQ0,subQ2,subQ4])],"isStart":false})])],"derivedFrom":makeQuery(id+"F2.opExtrude","SWEPT_FACE",FACE,{"disambiguationData":[OSD([subQ2])]})})]});}
            var Q2;
            {var subQ0=sQuery(id+"F0.wireOp",EDGE,"E20");var subQ1=sQuery(id+"F0.wireOp",EDGE,"E17");var subQ2=sQuery(id+"F0.wireOp",EDGE,"E16");var subQ3=makeQuery(id+"F0.imprint","IMPRINT",EDGE,{"disambiguationData":[TD([[makeQuery(id+"F0.imprint","INTERSECT",VERTEX,{"derivedFrom":[subQ2,subQ0]}),1.0]])],"derivedFrom":subQ0});Q2=makeQuery(id+"F7.opChamfer","BLEND_EDGE",EDGE,{"blendedFrom":[makeQuery(id+"F2.opExtrude","CAP_EDGE",EDGE,{"disambiguationData":[OSD([subQ0]),TDD([subQ3])],"isStart":false}),makeQuery(id+"F2.boolean.opBoolean","SPLIT",FACE,{"disambiguationData":[TD([makeQuery(id+"F2.opExtrude","CAP_FACE",FACE,{"disambiguationData":[OSD([sQuery(id+"F0.wireOp",EDGE,"E4"),subQ2,subQ1,subQ0])],"isStart":false})])],"derivedFrom":makeQuery(id+"F2.opExtrude","SWEPT_FACE",FACE,{"disambiguationData":[OSD([subQ0]),TDD([subQ3])]})})],"blendedInto":[makeQuery(id+"F2.boolean.opBoolean","SPLIT",FACE,{"disambiguationData":[TD([makeQuery(id+"F2.opExtrude","CAP_FACE",FACE,{"disambiguationData":[OSD([sQuery(id+"F0.wireOp",EDGE,"E4"),subQ2,subQ1,subQ0])],"isStart":false})])],"derivedFrom":makeQuery(id+"F2.opExtrude","SWEPT_FACE",FACE,{"disambiguationData":[OSD([subQ0]),TDD([subQ3])]})})]});}
            var Q3;
            {var subQ0=sQuery(id+"F0.wireOp",EDGE,"E16");var subQ1=sQuery(id+"F0.wireOp",EDGE,"E4");var subQ2=sQuery(id+"F0.wireOp",EDGE,"E17");var subQ3=sQuery(id+"F0.wireOp",EDGE,"E20");var subQ4=makeQuery(id+"F0.imprint","IMPRINT",EDGE,{"disambiguationData":[TD([[makeQuery(id+"F0.imprint","INTERSECT",VERTEX,{"derivedFrom":[subQ0,subQ3]}),1.0]])],"derivedFrom":subQ3});Q3=makeQuery(id+"F7.opChamfer","BLEND_EDGE",EDGE,{"blendedFrom":[makeQuery(id+"F2.opExtrude","CAP_EDGE",EDGE,{"disambiguationData":[OSD([subQ3]),TDD([subQ4])],"isStart":false}),makeQuery(id+"F2.boolean.opBoolean","SPLIT",FACE,{"disambiguationData":[TD([makeQuery(id+"F2.opExtrude","CAP_FACE",FACE,{"disambiguationData":[OSD([subQ1,subQ0,subQ2,subQ3])],"isStart":false})])],"derivedFrom":makeQuery(id+"F2.opExtrude","SWEPT_FACE",FACE,{"disambiguationData":[OSD([subQ0])]})})],"blendedInto":[makeQuery(id+"F2.boolean.opBoolean","SPLIT",FACE,{"disambiguationData":[TD([makeQuery(id+"F2.opExtrude","CAP_FACE",FACE,{"disambiguationData":[OSD([subQ1,subQ0,subQ2,subQ3])],"isStart":false})])],"derivedFrom":makeQuery(id+"F2.opExtrude","SWEPT_FACE",FACE,{"disambiguationData":[OSD([subQ0])]})})]});}
            var Q4;
            {var subQ0=sQuery(id+"F0.wireOp",EDGE,"E16");var subQ1=sQuery(id+"F0.wireOp",EDGE,"E4");var subQ2=sQuery(id+"F0.wireOp",EDGE,"E17");var subQ3=sQuery(id+"F0.wireOp",EDGE,"E20");var subQ4=makeQuery(id+"F0.imprint","IMPRINT",EDGE,{"disambiguationData":[TD([[makeQuery(id+"F0.imprint","INTERSECT",VERTEX,{"derivedFrom":[subQ0,subQ3]}),1.0]])],"derivedFrom":subQ3});Q4=makeQuery(id+"F7.opChamfer","BLEND_EDGE",EDGE,{"blendedFrom":[makeQuery(id+"F2.opExtrude","CAP_EDGE",EDGE,{"disambiguationData":[OSD([subQ3]),TDD([subQ4])],"isStart":false}),makeQuery(id+"F2.boolean.opBoolean","SPLIT",FACE,{"disambiguationData":[TD([makeQuery(id+"F2.opExtrude","CAP_FACE",FACE,{"disambiguationData":[OSD([subQ1,subQ0,subQ2,subQ3])],"isStart":false})])],"derivedFrom":makeQuery(id+"F2.opExtrude","SWEPT_FACE",FACE,{"disambiguationData":[OSD([subQ2])]})})],"blendedInto":[makeQuery(id+"F2.boolean.opBoolean","SPLIT",FACE,{"disambiguationData":[TD([makeQuery(id+"F2.opExtrude","CAP_FACE",FACE,{"disambiguationData":[OSD([subQ1,subQ0,subQ2,subQ3])],"isStart":false})])],"derivedFrom":makeQuery(id+"F2.opExtrude","SWEPT_FACE",FACE,{"disambiguationData":[OSD([subQ2])]})})]});}
            var Q5;
            {var subQ0=sQuery(id+"F0.wireOp",EDGE,"E17");var subQ1=sQuery(id+"F0.wireOp",EDGE,"E16");var subQ2=sQuery(id+"F0.wireOp",EDGE,"E4");var subQ3=makeQuery(id+"F0.imprint","IMPRINT",EDGE,{"disambiguationData":[TD([[makeQuery(id+"F0.imprint","INTERSECT",VERTEX,{"derivedFrom":[subQ2,subQ1]}),1.0]])],"derivedFrom":subQ2});Q5=makeQuery(id+"F7.opChamfer","BLEND_EDGE",EDGE,{"blendedFrom":[makeQuery(id+"F2.opExtrude","CAP_EDGE",EDGE,{"disambiguationData":[OSD([subQ2]),TDD([subQ3])],"isStart":false}),makeQuery(id+"F2.boolean.opBoolean","SPLIT",FACE,{"disambiguationData":[TD([makeQuery(id+"F2.opExtrude","CAP_FACE",FACE,{"disambiguationData":[OSD([subQ2,subQ1,subQ0,sQuery(id+"F0.wireOp",EDGE,"E20")])],"isStart":false})])],"derivedFrom":makeQuery(id+"F2.opExtrude","SWEPT_FACE",FACE,{"disambiguationData":[OSD([subQ2]),TDD([subQ3])]})})],"blendedInto":[makeQuery(id+"F2.boolean.opBoolean","SPLIT",FACE,{"disambiguationData":[TD([makeQuery(id+"F2.opExtrude","CAP_FACE",FACE,{"disambiguationData":[OSD([subQ2,subQ1,subQ0,sQuery(id+"F0.wireOp",EDGE,"E20")])],"isStart":false})])],"derivedFrom":makeQuery(id+"F2.opExtrude","SWEPT_FACE",FACE,{"disambiguationData":[OSD([subQ2]),TDD([subQ3])]})})]});}
            var Q6;
            {var subQ0=sQuery(id+"F0.wireOp",EDGE,"E20");var subQ1=sQuery(id+"F0.wireOp",EDGE,"E18.1.0");var subQ2=sQuery(id+"F0.wireOp",EDGE,"E18.1.1");var subQ3=sQuery(id+"F0.wireOp",EDGE,"E4");var subQ4=makeQuery(id+"F0.imprint","IMPRINT",EDGE,{"disambiguationData":[TD([[makeQuery(id+"F0.imprint","INTERSECT",VERTEX,{"derivedFrom":[subQ3,subQ1]}),1.0]])],"derivedFrom":subQ3});Q6=makeQuery(id+"F8.opChamfer","BLEND_EDGE",EDGE,{"blendedFrom":[makeQuery(id+"F2.opExtrude","CAP_EDGE",EDGE,{"disambiguationData":[OSD([subQ3]),TDD([subQ4])],"isStart":false}),makeQuery(id+"F2.boolean.opBoolean","SPLIT",FACE,{"disambiguationData":[TD([makeQuery(id+"F2.opExtrude","CAP_FACE",FACE,{"disambiguationData":[OSD([subQ3,subQ1,subQ2,subQ0])],"isStart":false})])],"derivedFrom":makeQuery(id+"F2.opExtrude","SWEPT_FACE",FACE,{"disambiguationData":[OSD([subQ1])]})})],"blendedInto":[makeQuery(id+"F2.boolean.opBoolean","SPLIT",FACE,{"disambiguationData":[TD([makeQuery(id+"F2.opExtrude","CAP_FACE",FACE,{"disambiguationData":[OSD([subQ3,subQ1,subQ2,subQ0])],"isStart":false})])],"derivedFrom":makeQuery(id+"F2.opExtrude","SWEPT_FACE",FACE,{"disambiguationData":[OSD([subQ1])]})})]});}
            var Q7;
            {var subQ0=sQuery(id+"F0.wireOp",EDGE,"E20");var subQ1=sQuery(id+"F0.wireOp",EDGE,"E18.1.0");var subQ2=sQuery(id+"F0.wireOp",EDGE,"E18.1.1");var subQ3=makeQuery(id+"F0.imprint","IMPRINT",EDGE,{"disambiguationData":[TD([[makeQuery(id+"F0.imprint","INTERSECT",VERTEX,{"derivedFrom":[subQ1,subQ0]}),1.0]])],"derivedFrom":subQ0});var subQ4=sQuery(id+"F0.wireOp",EDGE,"E4");Q7=makeQuery(id+"F9.opChamfer","BLEND_EDGE",EDGE,{"blendedFrom":[makeQuery(id+"F2.opExtrude","CAP_EDGE",EDGE,{"disambiguationData":[OSD([subQ0]),TDD([subQ3])],"isStart":false}),makeQuery(id+"F2.boolean.opBoolean","SPLIT",FACE,{"disambiguationData":[TD([makeQuery(id+"F2.opExtrude","CAP_FACE",FACE,{"disambiguationData":[OSD([subQ4,subQ1,subQ2,subQ0])],"isStart":false})])],"derivedFrom":makeQuery(id+"F2.opExtrude","SWEPT_FACE",FACE,{"disambiguationData":[OSD([subQ1])]})})],"blendedInto":[makeQuery(id+"F2.boolean.opBoolean","SPLIT",FACE,{"disambiguationData":[TD([makeQuery(id+"F2.opExtrude","CAP_FACE",FACE,{"disambiguationData":[OSD([subQ4,subQ1,subQ2,subQ0])],"isStart":false})])],"derivedFrom":makeQuery(id+"F2.opExtrude","SWEPT_FACE",FACE,{"disambiguationData":[OSD([subQ1])]})})]});}
            var Q8;
            {var subQ0=sQuery(id+"F0.wireOp",EDGE,"E18.1.0");var subQ1=sQuery(id+"F0.wireOp",EDGE,"E20");var subQ2=sQuery(id+"F0.wireOp",EDGE,"E18.1.1");var subQ3=makeQuery(id+"F0.imprint","IMPRINT",EDGE,{"disambiguationData":[TD([[makeQuery(id+"F0.imprint","INTERSECT",VERTEX,{"derivedFrom":[subQ0,subQ1]}),1.0]])],"derivedFrom":subQ1});Q8=makeQuery(id+"F9.opChamfer","BLEND_EDGE",EDGE,{"blendedFrom":[makeQuery(id+"F2.opExtrude","CAP_EDGE",EDGE,{"disambiguationData":[OSD([subQ1]),TDD([subQ3])],"isStart":false}),makeQuery(id+"F2.boolean.opBoolean","SPLIT",FACE,{"disambiguationData":[TD([makeQuery(id+"F2.opExtrude","CAP_FACE",FACE,{"disambiguationData":[OSD([sQuery(id+"F0.wireOp",EDGE,"E4"),subQ0,subQ2,subQ1])],"isStart":false})])],"derivedFrom":makeQuery(id+"F2.opExtrude","SWEPT_FACE",FACE,{"disambiguationData":[OSD([subQ1]),TDD([subQ3])]})})],"blendedInto":[makeQuery(id+"F2.boolean.opBoolean","SPLIT",FACE,{"disambiguationData":[TD([makeQuery(id+"F2.opExtrude","CAP_FACE",FACE,{"disambiguationData":[OSD([sQuery(id+"F0.wireOp",EDGE,"E4"),subQ0,subQ2,subQ1])],"isStart":false})])],"derivedFrom":makeQuery(id+"F2.opExtrude","SWEPT_FACE",FACE,{"disambiguationData":[OSD([subQ1]),TDD([subQ3])]})})]});}
            var Q9;
            {var subQ0=sQuery(id+"F0.wireOp",EDGE,"E20");var subQ1=sQuery(id+"F0.wireOp",EDGE,"E18.1.0");var subQ2=sQuery(id+"F0.wireOp",EDGE,"E18.1.1");var subQ3=makeQuery(id+"F0.imprint","IMPRINT",EDGE,{"disambiguationData":[TD([[makeQuery(id+"F0.imprint","INTERSECT",VERTEX,{"derivedFrom":[subQ1,subQ0]}),1.0]])],"derivedFrom":subQ0});var subQ4=sQuery(id+"F0.wireOp",EDGE,"E4");Q9=makeQuery(id+"F9.opChamfer","BLEND_EDGE",EDGE,{"blendedFrom":[makeQuery(id+"F2.opExtrude","CAP_EDGE",EDGE,{"disambiguationData":[OSD([subQ0]),TDD([subQ3])],"isStart":false}),makeQuery(id+"F2.boolean.opBoolean","SPLIT",FACE,{"disambiguationData":[TD([makeQuery(id+"F2.opExtrude","CAP_FACE",FACE,{"disambiguationData":[OSD([subQ4,subQ1,subQ2,subQ0])],"isStart":false})])],"derivedFrom":makeQuery(id+"F2.opExtrude","SWEPT_FACE",FACE,{"disambiguationData":[OSD([subQ2])]})})],"blendedInto":[makeQuery(id+"F2.boolean.opBoolean","SPLIT",FACE,{"disambiguationData":[TD([makeQuery(id+"F2.opExtrude","CAP_FACE",FACE,{"disambiguationData":[OSD([subQ4,subQ1,subQ2,subQ0])],"isStart":false})])],"derivedFrom":makeQuery(id+"F2.opExtrude","SWEPT_FACE",FACE,{"disambiguationData":[OSD([subQ2])]})})]});}
            var Q10;
            {var subQ0=sQuery(id+"F0.wireOp",EDGE,"E20");var subQ1=sQuery(id+"F0.wireOp",EDGE,"E18.1.0");var subQ2=sQuery(id+"F0.wireOp",EDGE,"E18.1.1");var subQ3=sQuery(id+"F0.wireOp",EDGE,"E4");var subQ4=makeQuery(id+"F0.imprint","IMPRINT",EDGE,{"disambiguationData":[TD([[makeQuery(id+"F0.imprint","INTERSECT",VERTEX,{"derivedFrom":[subQ3,subQ1]}),1.0]])],"derivedFrom":subQ3});Q10=makeQuery(id+"F8.opChamfer","BLEND_EDGE",EDGE,{"blendedFrom":[makeQuery(id+"F2.opExtrude","CAP_EDGE",EDGE,{"disambiguationData":[OSD([subQ3]),TDD([subQ4])],"isStart":false}),makeQuery(id+"F2.boolean.opBoolean","SPLIT",FACE,{"disambiguationData":[TD([makeQuery(id+"F2.opExtrude","CAP_FACE",FACE,{"disambiguationData":[OSD([subQ3,subQ1,subQ2,subQ0])],"isStart":false})])],"derivedFrom":makeQuery(id+"F2.opExtrude","SWEPT_FACE",FACE,{"disambiguationData":[OSD([subQ2])]})})],"blendedInto":[makeQuery(id+"F2.boolean.opBoolean","SPLIT",FACE,{"disambiguationData":[TD([makeQuery(id+"F2.opExtrude","CAP_FACE",FACE,{"disambiguationData":[OSD([subQ3,subQ1,subQ2,subQ0])],"isStart":false})])],"derivedFrom":makeQuery(id+"F2.opExtrude","SWEPT_FACE",FACE,{"disambiguationData":[OSD([subQ2])]})})]});}
            var Q11;
            {var subQ0=sQuery(id+"F0.wireOp",EDGE,"E18.1.0");var subQ1=sQuery(id+"F0.wireOp",EDGE,"E18.1.1");var subQ2=sQuery(id+"F0.wireOp",EDGE,"E4");var subQ3=makeQuery(id+"F0.imprint","IMPRINT",EDGE,{"disambiguationData":[TD([[makeQuery(id+"F0.imprint","INTERSECT",VERTEX,{"derivedFrom":[subQ2,subQ0]}),1.0]])],"derivedFrom":subQ2});Q11=makeQuery(id+"F8.opChamfer","BLEND_EDGE",EDGE,{"blendedFrom":[makeQuery(id+"F2.opExtrude","CAP_EDGE",EDGE,{"disambiguationData":[OSD([subQ2]),TDD([subQ3])],"isStart":false}),makeQuery(id+"F2.boolean.opBoolean","SPLIT",FACE,{"disambiguationData":[TD([makeQuery(id+"F2.opExtrude","CAP_FACE",FACE,{"disambiguationData":[OSD([subQ2,subQ0,subQ1,sQuery(id+"F0.wireOp",EDGE,"E20")])],"isStart":false})])],"derivedFrom":makeQuery(id+"F2.opExtrude","SWEPT_FACE",FACE,{"disambiguationData":[OSD([subQ2]),TDD([subQ3])]})})],"blendedInto":[makeQuery(id+"F2.boolean.opBoolean","SPLIT",FACE,{"disambiguationData":[TD([makeQuery(id+"F2.opExtrude","CAP_FACE",FACE,{"disambiguationData":[OSD([subQ2,subQ0,subQ1,sQuery(id+"F0.wireOp",EDGE,"E20")])],"isStart":false})])],"derivedFrom":makeQuery(id+"F2.opExtrude","SWEPT_FACE",FACE,{"disambiguationData":[OSD([subQ2]),TDD([subQ3])]})})]});}
            var Q12;
            {var subQ0=sQuery(id+"F0.wireOp",EDGE,"E18.2.1");var subQ1=sQuery(id+"F0.wireOp",EDGE,"E18.2.0");var subQ2=sQuery(id+"F0.wireOp",EDGE,"E4");var subQ3=makeQuery(id+"F0.imprint","IMPRINT",EDGE,{"disambiguationData":[TD([[makeQuery(id+"F0.imprint","INTERSECT",VERTEX,{"derivedFrom":[subQ2,subQ1]}),1.0]])],"derivedFrom":subQ2});Q12=makeQuery(id+"F8.opChamfer","BLEND_EDGE",EDGE,{"blendedFrom":[makeQuery(id+"F2.opExtrude","CAP_EDGE",EDGE,{"disambiguationData":[OSD([subQ2]),TDD([subQ3])],"isStart":false}),makeQuery(id+"F2.boolean.opBoolean","SPLIT",FACE,{"disambiguationData":[TD([makeQuery(id+"F2.opExtrude","CAP_FACE",FACE,{"disambiguationData":[OSD([subQ2,subQ1,subQ0,sQuery(id+"F0.wireOp",EDGE,"E20")])],"isStart":false})])],"derivedFrom":makeQuery(id+"F2.opExtrude","SWEPT_FACE",FACE,{"disambiguationData":[OSD([subQ2]),TDD([subQ3])]})})],"blendedInto":[makeQuery(id+"F2.boolean.opBoolean","SPLIT",FACE,{"disambiguationData":[TD([makeQuery(id+"F2.opExtrude","CAP_FACE",FACE,{"disambiguationData":[OSD([subQ2,subQ1,subQ0,sQuery(id+"F0.wireOp",EDGE,"E20")])],"isStart":false})])],"derivedFrom":makeQuery(id+"F2.opExtrude","SWEPT_FACE",FACE,{"disambiguationData":[OSD([subQ2]),TDD([subQ3])]})})]});}
            var Q13;
            {var subQ0=sQuery(id+"F0.wireOp",EDGE,"E18.2.0");var subQ1=sQuery(id+"F0.wireOp",EDGE,"E4");var subQ2=sQuery(id+"F0.wireOp",EDGE,"E18.2.1");var subQ3=makeQuery(id+"F0.imprint","IMPRINT",EDGE,{"disambiguationData":[TD([[makeQuery(id+"F0.imprint","INTERSECT",VERTEX,{"derivedFrom":[subQ1,subQ0]}),1.0]])],"derivedFrom":subQ1});var subQ4=sQuery(id+"F0.wireOp",EDGE,"E20");Q13=makeQuery(id+"F8.opChamfer","BLEND_EDGE",EDGE,{"blendedFrom":[makeQuery(id+"F2.opExtrude","CAP_EDGE",EDGE,{"disambiguationData":[OSD([subQ1]),TDD([subQ3])],"isStart":false}),makeQuery(id+"F2.boolean.opBoolean","SPLIT",FACE,{"disambiguationData":[TD([makeQuery(id+"F2.opExtrude","CAP_FACE",FACE,{"disambiguationData":[OSD([subQ1,subQ0,subQ2,subQ4])],"isStart":false})])],"derivedFrom":makeQuery(id+"F2.opExtrude","SWEPT_FACE",FACE,{"disambiguationData":[OSD([subQ0])]})})],"blendedInto":[makeQuery(id+"F2.boolean.opBoolean","SPLIT",FACE,{"disambiguationData":[TD([makeQuery(id+"F2.opExtrude","CAP_FACE",FACE,{"disambiguationData":[OSD([subQ1,subQ0,subQ2,subQ4])],"isStart":false})])],"derivedFrom":makeQuery(id+"F2.opExtrude","SWEPT_FACE",FACE,{"disambiguationData":[OSD([subQ0])]})})]});}
            var Q14;
            {var subQ0=sQuery(id+"F0.wireOp",EDGE,"E18.2.0");var subQ1=sQuery(id+"F0.wireOp",EDGE,"E4");var subQ2=sQuery(id+"F0.wireOp",EDGE,"E18.2.1");var subQ3=makeQuery(id+"F0.imprint","IMPRINT",EDGE,{"disambiguationData":[TD([[makeQuery(id+"F0.imprint","INTERSECT",VERTEX,{"derivedFrom":[subQ1,subQ0]}),1.0]])],"derivedFrom":subQ1});var subQ4=sQuery(id+"F0.wireOp",EDGE,"E20");Q14=makeQuery(id+"F8.opChamfer","BLEND_EDGE",EDGE,{"blendedFrom":[makeQuery(id+"F2.opExtrude","CAP_EDGE",EDGE,{"disambiguationData":[OSD([subQ1]),TDD([subQ3])],"isStart":false}),makeQuery(id+"F2.boolean.opBoolean","SPLIT",FACE,{"disambiguationData":[TD([makeQuery(id+"F2.opExtrude","CAP_FACE",FACE,{"disambiguationData":[OSD([subQ1,subQ0,subQ2,subQ4])],"isStart":false})])],"derivedFrom":makeQuery(id+"F2.opExtrude","SWEPT_FACE",FACE,{"disambiguationData":[OSD([subQ2])]})})],"blendedInto":[makeQuery(id+"F2.boolean.opBoolean","SPLIT",FACE,{"disambiguationData":[TD([makeQuery(id+"F2.opExtrude","CAP_FACE",FACE,{"disambiguationData":[OSD([subQ1,subQ0,subQ2,subQ4])],"isStart":false})])],"derivedFrom":makeQuery(id+"F2.opExtrude","SWEPT_FACE",FACE,{"disambiguationData":[OSD([subQ2])]})})]});}
            var Q15;
            {var subQ0=sQuery(id+"F0.wireOp",EDGE,"E18.2.0");var subQ1=sQuery(id+"F0.wireOp",EDGE,"E4");var subQ2=sQuery(id+"F0.wireOp",EDGE,"E18.2.1");var subQ3=sQuery(id+"F0.wireOp",EDGE,"E20");var subQ4=makeQuery(id+"F0.imprint","IMPRINT",EDGE,{"disambiguationData":[TD([[makeQuery(id+"F0.imprint","INTERSECT",VERTEX,{"derivedFrom":[subQ0,subQ3]}),1.0]])],"derivedFrom":subQ3});Q15=makeQuery(id+"F9.opChamfer","BLEND_EDGE",EDGE,{"blendedFrom":[makeQuery(id+"F2.opExtrude","CAP_EDGE",EDGE,{"disambiguationData":[OSD([subQ3]),TDD([subQ4])],"isStart":false}),makeQuery(id+"F2.boolean.opBoolean","SPLIT",FACE,{"disambiguationData":[TD([makeQuery(id+"F2.opExtrude","CAP_FACE",FACE,{"disambiguationData":[OSD([subQ1,subQ0,subQ2,subQ3])],"isStart":false})])],"derivedFrom":makeQuery(id+"F2.opExtrude","SWEPT_FACE",FACE,{"disambiguationData":[OSD([subQ2])]})})],"blendedInto":[makeQuery(id+"F2.boolean.opBoolean","SPLIT",FACE,{"disambiguationData":[TD([makeQuery(id+"F2.opExtrude","CAP_FACE",FACE,{"disambiguationData":[OSD([subQ1,subQ0,subQ2,subQ3])],"isStart":false})])],"derivedFrom":makeQuery(id+"F2.opExtrude","SWEPT_FACE",FACE,{"disambiguationData":[OSD([subQ2])]})})]});}
            var Q16;
            {var subQ0=sQuery(id+"F0.wireOp",EDGE,"E18.2.0");var subQ1=sQuery(id+"F0.wireOp",EDGE,"E4");var subQ2=sQuery(id+"F0.wireOp",EDGE,"E18.2.1");var subQ3=sQuery(id+"F0.wireOp",EDGE,"E20");var subQ4=makeQuery(id+"F0.imprint","IMPRINT",EDGE,{"disambiguationData":[TD([[makeQuery(id+"F0.imprint","INTERSECT",VERTEX,{"derivedFrom":[subQ0,subQ3]}),1.0]])],"derivedFrom":subQ3});Q16=makeQuery(id+"F9.opChamfer","BLEND_EDGE",EDGE,{"blendedFrom":[makeQuery(id+"F2.opExtrude","CAP_EDGE",EDGE,{"disambiguationData":[OSD([subQ3]),TDD([subQ4])],"isStart":false}),makeQuery(id+"F2.boolean.opBoolean","SPLIT",FACE,{"disambiguationData":[TD([makeQuery(id+"F2.opExtrude","CAP_FACE",FACE,{"disambiguationData":[OSD([subQ1,subQ0,subQ2,subQ3])],"isStart":false})])],"derivedFrom":makeQuery(id+"F2.opExtrude","SWEPT_FACE",FACE,{"disambiguationData":[OSD([subQ0])]})})],"blendedInto":[makeQuery(id+"F2.boolean.opBoolean","SPLIT",FACE,{"disambiguationData":[TD([makeQuery(id+"F2.opExtrude","CAP_FACE",FACE,{"disambiguationData":[OSD([subQ1,subQ0,subQ2,subQ3])],"isStart":false})])],"derivedFrom":makeQuery(id+"F2.opExtrude","SWEPT_FACE",FACE,{"disambiguationData":[OSD([subQ0])]})})]});}
            var Q17;
            {var subQ0=sQuery(id+"F0.wireOp",EDGE,"E20");var subQ1=sQuery(id+"F0.wireOp",EDGE,"E18.2.1");var subQ2=sQuery(id+"F0.wireOp",EDGE,"E18.2.0");var subQ3=makeQuery(id+"F0.imprint","IMPRINT",EDGE,{"disambiguationData":[TD([[makeQuery(id+"F0.imprint","INTERSECT",VERTEX,{"derivedFrom":[subQ2,subQ0]}),1.0]])],"derivedFrom":subQ0});Q17=makeQuery(id+"F9.opChamfer","BLEND_EDGE",EDGE,{"blendedFrom":[makeQuery(id+"F2.opExtrude","CAP_EDGE",EDGE,{"disambiguationData":[OSD([subQ0]),TDD([subQ3])],"isStart":false}),makeQuery(id+"F2.boolean.opBoolean","SPLIT",FACE,{"disambiguationData":[TD([makeQuery(id+"F2.opExtrude","CAP_FACE",FACE,{"disambiguationData":[OSD([sQuery(id+"F0.wireOp",EDGE,"E4"),subQ2,subQ1,subQ0])],"isStart":false})])],"derivedFrom":makeQuery(id+"F2.opExtrude","SWEPT_FACE",FACE,{"disambiguationData":[OSD([subQ0]),TDD([subQ3])]})})],"blendedInto":[makeQuery(id+"F2.boolean.opBoolean","SPLIT",FACE,{"disambiguationData":[TD([makeQuery(id+"F2.opExtrude","CAP_FACE",FACE,{"disambiguationData":[OSD([sQuery(id+"F0.wireOp",EDGE,"E4"),subQ2,subQ1,subQ0])],"isStart":false})])],"derivedFrom":makeQuery(id+"F2.opExtrude","SWEPT_FACE",FACE,{"disambiguationData":[OSD([subQ0]),TDD([subQ3])]})})]});}
            var Q18;
            {var subQ0=sQuery(id+"F0.wireOp",EDGE,"E19.1.3.0");var subQ1=sQuery(id+"F0.wireOp",EDGE,"E4");var subQ2=sQuery(id+"F0.wireOp",EDGE,"E19.3.3.0");var subQ3=sQuery(id+"F0.wireOp",EDGE,"E20");var subQ4=makeQuery(id+"F0.imprint","IMPRINT",EDGE,{"disambiguationData":[TD([[makeQuery(id+"F0.imprint","INTERSECT",VERTEX,{"derivedFrom":[subQ0,subQ3]}),1.0]])],"derivedFrom":subQ3});Q18=makeQuery(id+"F9.opChamfer","BLEND_EDGE",EDGE,{"blendedFrom":[makeQuery(id+"F2.opExtrude","CAP_EDGE",EDGE,{"disambiguationData":[OSD([subQ3]),TDD([subQ4])],"isStart":false}),makeQuery(id+"F2.boolean.opBoolean","SPLIT",FACE,{"disambiguationData":[TD([makeQuery(id+"F2.opExtrude","CAP_FACE",FACE,{"disambiguationData":[OSD([subQ1,subQ0,subQ2,subQ3])],"isStart":false})])],"derivedFrom":makeQuery(id+"F2.opExtrude","SWEPT_FACE",FACE,{"disambiguationData":[OSD([subQ0])]})})],"blendedInto":[makeQuery(id+"F2.boolean.opBoolean","SPLIT",FACE,{"disambiguationData":[TD([makeQuery(id+"F2.opExtrude","CAP_FACE",FACE,{"disambiguationData":[OSD([subQ1,subQ0,subQ2,subQ3])],"isStart":false})])],"derivedFrom":makeQuery(id+"F2.opExtrude","SWEPT_FACE",FACE,{"disambiguationData":[OSD([subQ0])]})})]});}
            var Q19;
            {var subQ0=sQuery(id+"F0.wireOp",EDGE,"E19.1.3.0");var subQ1=sQuery(id+"F0.wireOp",EDGE,"E4");var subQ2=sQuery(id+"F0.wireOp",EDGE,"E19.3.3.0");var subQ3=makeQuery(id+"F0.imprint","IMPRINT",EDGE,{"disambiguationData":[TD([[makeQuery(id+"F0.imprint","INTERSECT",VERTEX,{"derivedFrom":[subQ1,subQ0]}),1.0]])],"derivedFrom":subQ1});var subQ4=sQuery(id+"F0.wireOp",EDGE,"E20");Q19=makeQuery(id+"F8.opChamfer","BLEND_EDGE",EDGE,{"blendedFrom":[makeQuery(id+"F2.opExtrude","CAP_EDGE",EDGE,{"disambiguationData":[OSD([subQ1]),TDD([subQ3])],"isStart":false}),makeQuery(id+"F2.boolean.opBoolean","SPLIT",FACE,{"disambiguationData":[TD([makeQuery(id+"F2.opExtrude","CAP_FACE",FACE,{"disambiguationData":[OSD([subQ1,subQ0,subQ2,subQ4])],"isStart":false})])],"derivedFrom":makeQuery(id+"F2.opExtrude","SWEPT_FACE",FACE,{"disambiguationData":[OSD([subQ0])]})})],"blendedInto":[makeQuery(id+"F2.boolean.opBoolean","SPLIT",FACE,{"disambiguationData":[TD([makeQuery(id+"F2.opExtrude","CAP_FACE",FACE,{"disambiguationData":[OSD([subQ1,subQ0,subQ2,subQ4])],"isStart":false})])],"derivedFrom":makeQuery(id+"F2.opExtrude","SWEPT_FACE",FACE,{"disambiguationData":[OSD([subQ0])]})})]});}
            var Q20;
            {var subQ0=sQuery(id+"F0.wireOp",EDGE,"E19.1.3.0");var subQ1=sQuery(id+"F0.wireOp",EDGE,"E4");var subQ2=sQuery(id+"F0.wireOp",EDGE,"E19.3.3.0");var subQ3=makeQuery(id+"F0.imprint","IMPRINT",EDGE,{"disambiguationData":[TD([[makeQuery(id+"F0.imprint","INTERSECT",VERTEX,{"derivedFrom":[subQ1,subQ0]}),1.0]])],"derivedFrom":subQ1});var subQ4=sQuery(id+"F0.wireOp",EDGE,"E20");Q20=makeQuery(id+"F8.opChamfer","BLEND_EDGE",EDGE,{"blendedFrom":[makeQuery(id+"F2.opExtrude","CAP_EDGE",EDGE,{"disambiguationData":[OSD([subQ1]),TDD([subQ3])],"isStart":false}),makeQuery(id+"F2.boolean.opBoolean","SPLIT",FACE,{"disambiguationData":[TD([makeQuery(id+"F2.opExtrude","CAP_FACE",FACE,{"disambiguationData":[OSD([subQ1,subQ0,subQ2,subQ4])],"isStart":false})])],"derivedFrom":makeQuery(id+"F2.opExtrude","SWEPT_FACE",FACE,{"disambiguationData":[OSD([subQ2])]})})],"blendedInto":[makeQuery(id+"F2.boolean.opBoolean","SPLIT",FACE,{"disambiguationData":[TD([makeQuery(id+"F2.opExtrude","CAP_FACE",FACE,{"disambiguationData":[OSD([subQ1,subQ0,subQ2,subQ4])],"isStart":false})])],"derivedFrom":makeQuery(id+"F2.opExtrude","SWEPT_FACE",FACE,{"disambiguationData":[OSD([subQ2])]})})]});}
            var Q21;
            {var subQ0=sQuery(id+"F0.wireOp",EDGE,"E19.1.3.0");var subQ1=sQuery(id+"F0.wireOp",EDGE,"E4");var subQ2=sQuery(id+"F0.wireOp",EDGE,"E19.3.3.0");var subQ3=sQuery(id+"F0.wireOp",EDGE,"E20");var subQ4=makeQuery(id+"F0.imprint","IMPRINT",EDGE,{"disambiguationData":[TD([[makeQuery(id+"F0.imprint","INTERSECT",VERTEX,{"derivedFrom":[subQ0,subQ3]}),1.0]])],"derivedFrom":subQ3});Q21=makeQuery(id+"F9.opChamfer","BLEND_EDGE",EDGE,{"blendedFrom":[makeQuery(id+"F2.opExtrude","CAP_EDGE",EDGE,{"disambiguationData":[OSD([subQ3]),TDD([subQ4])],"isStart":false}),makeQuery(id+"F2.boolean.opBoolean","SPLIT",FACE,{"disambiguationData":[TD([makeQuery(id+"F2.opExtrude","CAP_FACE",FACE,{"disambiguationData":[OSD([subQ1,subQ0,subQ2,subQ3])],"isStart":false})])],"derivedFrom":makeQuery(id+"F2.opExtrude","SWEPT_FACE",FACE,{"disambiguationData":[OSD([subQ2])]})})],"blendedInto":[makeQuery(id+"F2.boolean.opBoolean","SPLIT",FACE,{"disambiguationData":[TD([makeQuery(id+"F2.opExtrude","CAP_FACE",FACE,{"disambiguationData":[OSD([subQ1,subQ0,subQ2,subQ3])],"isStart":false})])],"derivedFrom":makeQuery(id+"F2.opExtrude","SWEPT_FACE",FACE,{"disambiguationData":[OSD([subQ2])]})})]});}
            var Q22;
            {var subQ0=sQuery(id+"F0.wireOp",EDGE,"E19.3.3.0");var subQ1=sQuery(id+"F0.wireOp",EDGE,"E20");var subQ2=sQuery(id+"F0.wireOp",EDGE,"E19.1.3.0");var subQ3=makeQuery(id+"F0.imprint","IMPRINT",EDGE,{"disambiguationData":[TD([[makeQuery(id+"F0.imprint","INTERSECT",VERTEX,{"derivedFrom":[subQ2,subQ1]}),1.0]])],"derivedFrom":subQ1});Q22=makeQuery(id+"F9.opChamfer","BLEND_EDGE",EDGE,{"blendedFrom":[makeQuery(id+"F2.opExtrude","CAP_EDGE",EDGE,{"disambiguationData":[OSD([subQ1]),TDD([subQ3])],"isStart":false}),makeQuery(id+"F2.boolean.opBoolean","SPLIT",FACE,{"disambiguationData":[TD([makeQuery(id+"F2.opExtrude","CAP_FACE",FACE,{"disambiguationData":[OSD([sQuery(id+"F0.wireOp",EDGE,"E4"),subQ2,subQ0,subQ1])],"isStart":false})])],"derivedFrom":makeQuery(id+"F2.opExtrude","SWEPT_FACE",FACE,{"disambiguationData":[OSD([subQ1]),TDD([subQ3])]})})],"blendedInto":[makeQuery(id+"F2.boolean.opBoolean","SPLIT",FACE,{"disambiguationData":[TD([makeQuery(id+"F2.opExtrude","CAP_FACE",FACE,{"disambiguationData":[OSD([sQuery(id+"F0.wireOp",EDGE,"E4"),subQ2,subQ0,subQ1])],"isStart":false})])],"derivedFrom":makeQuery(id+"F2.opExtrude","SWEPT_FACE",FACE,{"disambiguationData":[OSD([subQ1]),TDD([subQ3])]})})]});}
            var Q23;
            {var subQ0=sQuery(id+"F0.wireOp",EDGE,"E20");var subQ1=sQuery(id+"F0.wireOp",EDGE,"E19.3.4.0");var subQ2=sQuery(id+"F0.wireOp",EDGE,"E19.1.4.0");var subQ3=makeQuery(id+"F0.imprint","IMPRINT",EDGE,{"disambiguationData":[TD([[makeQuery(id+"F0.imprint","INTERSECT",VERTEX,{"derivedFrom":[subQ2,subQ0]}),1.0]])],"derivedFrom":subQ0});Q23=makeQuery(id+"F9.opChamfer","BLEND_EDGE",EDGE,{"blendedFrom":[makeQuery(id+"F2.opExtrude","CAP_EDGE",EDGE,{"disambiguationData":[OSD([subQ0]),TDD([subQ3])],"isStart":false}),makeQuery(id+"F2.boolean.opBoolean","SPLIT",FACE,{"disambiguationData":[TD([makeQuery(id+"F2.opExtrude","CAP_FACE",FACE,{"disambiguationData":[OSD([sQuery(id+"F0.wireOp",EDGE,"E4"),subQ2,subQ1,subQ0])],"isStart":false})])],"derivedFrom":makeQuery(id+"F2.opExtrude","SWEPT_FACE",FACE,{"disambiguationData":[OSD([subQ0]),TDD([subQ3])]})})],"blendedInto":[makeQuery(id+"F2.boolean.opBoolean","SPLIT",FACE,{"disambiguationData":[TD([makeQuery(id+"F2.opExtrude","CAP_FACE",FACE,{"disambiguationData":[OSD([sQuery(id+"F0.wireOp",EDGE,"E4"),subQ2,subQ1,subQ0])],"isStart":false})])],"derivedFrom":makeQuery(id+"F2.opExtrude","SWEPT_FACE",FACE,{"disambiguationData":[OSD([subQ0]),TDD([subQ3])]})})]});}
            var Q24;
            {var subQ0=sQuery(id+"F0.wireOp",EDGE,"E20");var subQ1=sQuery(id+"F0.wireOp",EDGE,"E19.3.4.0");var subQ2=sQuery(id+"F0.wireOp",EDGE,"E19.1.4.0");var subQ3=sQuery(id+"F0.wireOp",EDGE,"E4");var subQ4=makeQuery(id+"F0.imprint","IMPRINT",EDGE,{"disambiguationData":[TD([[makeQuery(id+"F0.imprint","INTERSECT",VERTEX,{"derivedFrom":[subQ2,subQ0]}),1.0]])],"derivedFrom":subQ0});Q24=makeQuery(id+"F9.opChamfer","BLEND_EDGE",EDGE,{"blendedFrom":[makeQuery(id+"F2.opExtrude","CAP_EDGE",EDGE,{"disambiguationData":[OSD([subQ0]),TDD([subQ4])],"isStart":false}),makeQuery(id+"F2.boolean.opBoolean","SPLIT",FACE,{"disambiguationData":[TD([makeQuery(id+"F2.opExtrude","CAP_FACE",FACE,{"disambiguationData":[OSD([subQ3,subQ2,subQ1,subQ0])],"isStart":false})])],"derivedFrom":makeQuery(id+"F2.opExtrude","SWEPT_FACE",FACE,{"disambiguationData":[OSD([subQ2])]})})],"blendedInto":[makeQuery(id+"F2.boolean.opBoolean","SPLIT",FACE,{"disambiguationData":[TD([makeQuery(id+"F2.opExtrude","CAP_FACE",FACE,{"disambiguationData":[OSD([subQ3,subQ2,subQ1,subQ0])],"isStart":false})])],"derivedFrom":makeQuery(id+"F2.opExtrude","SWEPT_FACE",FACE,{"disambiguationData":[OSD([subQ2])]})})]});}
            var Q25;
            {var subQ0=sQuery(id+"F0.wireOp",EDGE,"E20");var subQ1=sQuery(id+"F0.wireOp",EDGE,"E19.3.4.0");var subQ2=sQuery(id+"F0.wireOp",EDGE,"E19.1.4.0");var subQ3=sQuery(id+"F0.wireOp",EDGE,"E4");var subQ4=makeQuery(id+"F0.imprint","IMPRINT",EDGE,{"disambiguationData":[TD([[makeQuery(id+"F0.imprint","INTERSECT",VERTEX,{"derivedFrom":[subQ2,subQ0]}),1.0]])],"derivedFrom":subQ0});Q25=makeQuery(id+"F9.opChamfer","BLEND_EDGE",EDGE,{"blendedFrom":[makeQuery(id+"F2.opExtrude","CAP_EDGE",EDGE,{"disambiguationData":[OSD([subQ0]),TDD([subQ4])],"isStart":false}),makeQuery(id+"F2.boolean.opBoolean","SPLIT",FACE,{"disambiguationData":[TD([makeQuery(id+"F2.opExtrude","CAP_FACE",FACE,{"disambiguationData":[OSD([subQ3,subQ2,subQ1,subQ0])],"isStart":false})])],"derivedFrom":makeQuery(id+"F2.opExtrude","SWEPT_FACE",FACE,{"disambiguationData":[OSD([subQ1])]})})],"blendedInto":[makeQuery(id+"F2.boolean.opBoolean","SPLIT",FACE,{"disambiguationData":[TD([makeQuery(id+"F2.opExtrude","CAP_FACE",FACE,{"disambiguationData":[OSD([subQ3,subQ2,subQ1,subQ0])],"isStart":false})])],"derivedFrom":makeQuery(id+"F2.opExtrude","SWEPT_FACE",FACE,{"disambiguationData":[OSD([subQ1])]})})]});}
            var Q26;
            {var subQ0=sQuery(id+"F0.wireOp",EDGE,"E20");var subQ1=sQuery(id+"F0.wireOp",EDGE,"E19.3.4.0");var subQ2=sQuery(id+"F0.wireOp",EDGE,"E19.1.4.0");var subQ3=sQuery(id+"F0.wireOp",EDGE,"E4");var subQ4=makeQuery(id+"F0.imprint","IMPRINT",EDGE,{"disambiguationData":[TD([[makeQuery(id+"F0.imprint","INTERSECT",VERTEX,{"derivedFrom":[subQ3,subQ2]}),1.0]])],"derivedFrom":subQ3});Q26=makeQuery(id+"F8.opChamfer","BLEND_EDGE",EDGE,{"blendedFrom":[makeQuery(id+"F2.opExtrude","CAP_EDGE",EDGE,{"disambiguationData":[OSD([subQ3]),TDD([subQ4])],"isStart":false}),makeQuery(id+"F2.boolean.opBoolean","SPLIT",FACE,{"disambiguationData":[TD([makeQuery(id+"F2.opExtrude","CAP_FACE",FACE,{"disambiguationData":[OSD([subQ3,subQ2,subQ1,subQ0])],"isStart":false})])],"derivedFrom":makeQuery(id+"F2.opExtrude","SWEPT_FACE",FACE,{"disambiguationData":[OSD([subQ2])]})})],"blendedInto":[makeQuery(id+"F2.boolean.opBoolean","SPLIT",FACE,{"disambiguationData":[TD([makeQuery(id+"F2.opExtrude","CAP_FACE",FACE,{"disambiguationData":[OSD([subQ3,subQ2,subQ1,subQ0])],"isStart":false})])],"derivedFrom":makeQuery(id+"F2.opExtrude","SWEPT_FACE",FACE,{"disambiguationData":[OSD([subQ2])]})})]});}
            var Q27;
            {var subQ0=sQuery(id+"F0.wireOp",EDGE,"E20");var subQ1=sQuery(id+"F0.wireOp",EDGE,"E19.3.4.0");var subQ2=sQuery(id+"F0.wireOp",EDGE,"E19.1.4.0");var subQ3=sQuery(id+"F0.wireOp",EDGE,"E4");var subQ4=makeQuery(id+"F0.imprint","IMPRINT",EDGE,{"disambiguationData":[TD([[makeQuery(id+"F0.imprint","INTERSECT",VERTEX,{"derivedFrom":[subQ3,subQ2]}),1.0]])],"derivedFrom":subQ3});Q27=makeQuery(id+"F8.opChamfer","BLEND_EDGE",EDGE,{"blendedFrom":[makeQuery(id+"F2.opExtrude","CAP_EDGE",EDGE,{"disambiguationData":[OSD([subQ3]),TDD([subQ4])],"isStart":false}),makeQuery(id+"F2.boolean.opBoolean","SPLIT",FACE,{"disambiguationData":[TD([makeQuery(id+"F2.opExtrude","CAP_FACE",FACE,{"disambiguationData":[OSD([subQ3,subQ2,subQ1,subQ0])],"isStart":false})])],"derivedFrom":makeQuery(id+"F2.opExtrude","SWEPT_FACE",FACE,{"disambiguationData":[OSD([subQ1])]})})],"blendedInto":[makeQuery(id+"F2.boolean.opBoolean","SPLIT",FACE,{"disambiguationData":[TD([makeQuery(id+"F2.opExtrude","CAP_FACE",FACE,{"disambiguationData":[OSD([subQ3,subQ2,subQ1,subQ0])],"isStart":false})])],"derivedFrom":makeQuery(id+"F2.opExtrude","SWEPT_FACE",FACE,{"disambiguationData":[OSD([subQ1])]})})]});}
            var Q28;
            {var subQ0=sQuery(id+"F0.wireOp",EDGE,"E19.3.4.0");var subQ1=sQuery(id+"F0.wireOp",EDGE,"E19.1.4.0");var subQ2=sQuery(id+"F0.wireOp",EDGE,"E4");var subQ3=makeQuery(id+"F0.imprint","IMPRINT",EDGE,{"disambiguationData":[TD([[makeQuery(id+"F0.imprint","INTERSECT",VERTEX,{"derivedFrom":[subQ2,subQ1]}),1.0]])],"derivedFrom":subQ2});Q28=makeQuery(id+"F8.opChamfer","BLEND_EDGE",EDGE,{"blendedFrom":[makeQuery(id+"F2.opExtrude","CAP_EDGE",EDGE,{"disambiguationData":[OSD([subQ2]),TDD([subQ3])],"isStart":false}),makeQuery(id+"F2.boolean.opBoolean","SPLIT",FACE,{"disambiguationData":[TD([makeQuery(id+"F2.opExtrude","CAP_FACE",FACE,{"disambiguationData":[OSD([subQ2,subQ1,subQ0,sQuery(id+"F0.wireOp",EDGE,"E20")])],"isStart":false})])],"derivedFrom":makeQuery(id+"F2.opExtrude","SWEPT_FACE",FACE,{"disambiguationData":[OSD([subQ2]),TDD([subQ3])]})})],"blendedInto":[makeQuery(id+"F2.boolean.opBoolean","SPLIT",FACE,{"disambiguationData":[TD([makeQuery(id+"F2.opExtrude","CAP_FACE",FACE,{"disambiguationData":[OSD([subQ2,subQ1,subQ0,sQuery(id+"F0.wireOp",EDGE,"E20")])],"isStart":false})])],"derivedFrom":makeQuery(id+"F2.opExtrude","SWEPT_FACE",FACE,{"disambiguationData":[OSD([subQ2]),TDD([subQ3])]})})]});}
            var Q29;
            {var subQ0=sQuery(id+"F0.wireOp",EDGE,"E19.3.3.0");var subQ1=sQuery(id+"F0.wireOp",EDGE,"E19.1.3.0");var subQ2=sQuery(id+"F0.wireOp",EDGE,"E4");var subQ3=makeQuery(id+"F0.imprint","IMPRINT",EDGE,{"disambiguationData":[TD([[makeQuery(id+"F0.imprint","INTERSECT",VERTEX,{"derivedFrom":[subQ2,subQ1]}),1.0]])],"derivedFrom":subQ2});Q29=makeQuery(id+"F8.opChamfer","BLEND_EDGE",EDGE,{"blendedFrom":[makeQuery(id+"F2.opExtrude","CAP_EDGE",EDGE,{"disambiguationData":[OSD([subQ2]),TDD([subQ3])],"isStart":false}),makeQuery(id+"F2.boolean.opBoolean","SPLIT",FACE,{"disambiguationData":[TD([makeQuery(id+"F2.opExtrude","CAP_FACE",FACE,{"disambiguationData":[OSD([subQ2,subQ1,subQ0,sQuery(id+"F0.wireOp",EDGE,"E20")])],"isStart":false})])],"derivedFrom":makeQuery(id+"F2.opExtrude","SWEPT_FACE",FACE,{"disambiguationData":[OSD([subQ2]),TDD([subQ3])]})})],"blendedInto":[makeQuery(id+"F2.boolean.opBoolean","SPLIT",FACE,{"disambiguationData":[TD([makeQuery(id+"F2.opExtrude","CAP_FACE",FACE,{"disambiguationData":[OSD([subQ2,subQ1,subQ0,sQuery(id+"F0.wireOp",EDGE,"E20")])],"isStart":false})])],"derivedFrom":makeQuery(id+"F2.opExtrude","SWEPT_FACE",FACE,{"disambiguationData":[OSD([subQ2]),TDD([subQ3])]})})]});}
            var Q30;
            {var subQ0=sQuery(id+"F0.wireOp",EDGE,"E19.1.5.0");var subQ1=sQuery(id+"F0.wireOp",EDGE,"E4");var subQ2=sQuery(id+"F0.wireOp",EDGE,"E19.3.5.0");var subQ3=sQuery(id+"F0.wireOp",EDGE,"E20");var subQ4=makeQuery(id+"F0.imprint","IMPRINT",EDGE,{"disambiguationData":[TD([[makeQuery(id+"F0.imprint","INTERSECT",VERTEX,{"derivedFrom":[subQ0,subQ3]}),1.0]])],"derivedFrom":subQ3});Q30=makeQuery(id+"F9.opChamfer","BLEND_EDGE",EDGE,{"blendedFrom":[makeQuery(id+"F2.opExtrude","CAP_EDGE",EDGE,{"disambiguationData":[OSD([subQ3]),TDD([subQ4])],"isStart":false}),makeQuery(id+"F2.boolean.opBoolean","SPLIT",FACE,{"disambiguationData":[TD([makeQuery(id+"F2.opExtrude","CAP_FACE",FACE,{"disambiguationData":[OSD([subQ1,subQ0,subQ2,subQ3])],"isStart":false})])],"derivedFrom":makeQuery(id+"F2.opExtrude","SWEPT_FACE",FACE,{"disambiguationData":[OSD([subQ0])]})})],"blendedInto":[makeQuery(id+"F2.boolean.opBoolean","SPLIT",FACE,{"disambiguationData":[TD([makeQuery(id+"F2.opExtrude","CAP_FACE",FACE,{"disambiguationData":[OSD([subQ1,subQ0,subQ2,subQ3])],"isStart":false})])],"derivedFrom":makeQuery(id+"F2.opExtrude","SWEPT_FACE",FACE,{"disambiguationData":[OSD([subQ0])]})})]});}
            var Q31;
            {var subQ0=sQuery(id+"F0.wireOp",EDGE,"E20");var subQ1=sQuery(id+"F0.wireOp",EDGE,"E19.3.5.0");var subQ2=sQuery(id+"F0.wireOp",EDGE,"E19.1.5.0");var subQ3=makeQuery(id+"F0.imprint","IMPRINT",EDGE,{"disambiguationData":[TD([[makeQuery(id+"F0.imprint","INTERSECT",VERTEX,{"derivedFrom":[subQ2,subQ0]}),1.0]])],"derivedFrom":subQ0});Q31=makeQuery(id+"F9.opChamfer","BLEND_EDGE",EDGE,{"blendedFrom":[makeQuery(id+"F2.opExtrude","CAP_EDGE",EDGE,{"disambiguationData":[OSD([subQ0]),TDD([subQ3])],"isStart":false}),makeQuery(id+"F2.boolean.opBoolean","SPLIT",FACE,{"disambiguationData":[TD([makeQuery(id+"F2.opExtrude","CAP_FACE",FACE,{"disambiguationData":[OSD([sQuery(id+"F0.wireOp",EDGE,"E4"),subQ2,subQ1,subQ0])],"isStart":false})])],"derivedFrom":makeQuery(id+"F2.opExtrude","SWEPT_FACE",FACE,{"disambiguationData":[OSD([subQ0]),TDD([subQ3])]})})],"blendedInto":[makeQuery(id+"F2.boolean.opBoolean","SPLIT",FACE,{"disambiguationData":[TD([makeQuery(id+"F2.opExtrude","CAP_FACE",FACE,{"disambiguationData":[OSD([sQuery(id+"F0.wireOp",EDGE,"E4"),subQ2,subQ1,subQ0])],"isStart":false})])],"derivedFrom":makeQuery(id+"F2.opExtrude","SWEPT_FACE",FACE,{"disambiguationData":[OSD([subQ0]),TDD([subQ3])]})})]});}
            var Q32;
            {var subQ0=sQuery(id+"F0.wireOp",EDGE,"E19.1.5.0");var subQ1=sQuery(id+"F0.wireOp",EDGE,"E4");var subQ2=sQuery(id+"F0.wireOp",EDGE,"E19.3.5.0");var subQ3=sQuery(id+"F0.wireOp",EDGE,"E20");var subQ4=makeQuery(id+"F0.imprint","IMPRINT",EDGE,{"disambiguationData":[TD([[makeQuery(id+"F0.imprint","INTERSECT",VERTEX,{"derivedFrom":[subQ0,subQ3]}),1.0]])],"derivedFrom":subQ3});Q32=makeQuery(id+"F9.opChamfer","BLEND_EDGE",EDGE,{"blendedFrom":[makeQuery(id+"F2.opExtrude","CAP_EDGE",EDGE,{"disambiguationData":[OSD([subQ3]),TDD([subQ4])],"isStart":false}),makeQuery(id+"F2.boolean.opBoolean","SPLIT",FACE,{"disambiguationData":[TD([makeQuery(id+"F2.opExtrude","CAP_FACE",FACE,{"disambiguationData":[OSD([subQ1,subQ0,subQ2,subQ3])],"isStart":false})])],"derivedFrom":makeQuery(id+"F2.opExtrude","SWEPT_FACE",FACE,{"disambiguationData":[OSD([subQ2])]})})],"blendedInto":[makeQuery(id+"F2.boolean.opBoolean","SPLIT",FACE,{"disambiguationData":[TD([makeQuery(id+"F2.opExtrude","CAP_FACE",FACE,{"disambiguationData":[OSD([subQ1,subQ0,subQ2,subQ3])],"isStart":false})])],"derivedFrom":makeQuery(id+"F2.opExtrude","SWEPT_FACE",FACE,{"disambiguationData":[OSD([subQ2])]})})]});}
            var Q33;
            {var subQ0=sQuery(id+"F0.wireOp",EDGE,"E19.1.5.0");var subQ1=sQuery(id+"F0.wireOp",EDGE,"E4");var subQ2=sQuery(id+"F0.wireOp",EDGE,"E19.3.5.0");var subQ3=makeQuery(id+"F0.imprint","IMPRINT",EDGE,{"disambiguationData":[TD([[makeQuery(id+"F0.imprint","INTERSECT",VERTEX,{"derivedFrom":[subQ1,subQ0]}),1.0]])],"derivedFrom":subQ1});var subQ4=sQuery(id+"F0.wireOp",EDGE,"E20");Q33=makeQuery(id+"F8.opChamfer","BLEND_EDGE",EDGE,{"blendedFrom":[makeQuery(id+"F2.opExtrude","CAP_EDGE",EDGE,{"disambiguationData":[OSD([subQ1]),TDD([subQ3])],"isStart":false}),makeQuery(id+"F2.boolean.opBoolean","SPLIT",FACE,{"disambiguationData":[TD([makeQuery(id+"F2.opExtrude","CAP_FACE",FACE,{"disambiguationData":[OSD([subQ1,subQ0,subQ2,subQ4])],"isStart":false})])],"derivedFrom":makeQuery(id+"F2.opExtrude","SWEPT_FACE",FACE,{"disambiguationData":[OSD([subQ2])]})})],"blendedInto":[makeQuery(id+"F2.boolean.opBoolean","SPLIT",FACE,{"disambiguationData":[TD([makeQuery(id+"F2.opExtrude","CAP_FACE",FACE,{"disambiguationData":[OSD([subQ1,subQ0,subQ2,subQ4])],"isStart":false})])],"derivedFrom":makeQuery(id+"F2.opExtrude","SWEPT_FACE",FACE,{"disambiguationData":[OSD([subQ2])]})})]});}
            var Q34;
            {var subQ0=sQuery(id+"F0.wireOp",EDGE,"E19.3.5.0");var subQ1=sQuery(id+"F0.wireOp",EDGE,"E19.1.5.0");var subQ2=sQuery(id+"F0.wireOp",EDGE,"E4");var subQ3=makeQuery(id+"F0.imprint","IMPRINT",EDGE,{"disambiguationData":[TD([[makeQuery(id+"F0.imprint","INTERSECT",VERTEX,{"derivedFrom":[subQ2,subQ1]}),1.0]])],"derivedFrom":subQ2});Q34=makeQuery(id+"F8.opChamfer","BLEND_EDGE",EDGE,{"blendedFrom":[makeQuery(id+"F2.opExtrude","CAP_EDGE",EDGE,{"disambiguationData":[OSD([subQ2]),TDD([subQ3])],"isStart":false}),makeQuery(id+"F2.boolean.opBoolean","SPLIT",FACE,{"disambiguationData":[TD([makeQuery(id+"F2.opExtrude","CAP_FACE",FACE,{"disambiguationData":[OSD([subQ2,subQ1,subQ0,sQuery(id+"F0.wireOp",EDGE,"E20")])],"isStart":false})])],"derivedFrom":makeQuery(id+"F2.opExtrude","SWEPT_FACE",FACE,{"disambiguationData":[OSD([subQ2]),TDD([subQ3])]})})],"blendedInto":[makeQuery(id+"F2.boolean.opBoolean","SPLIT",FACE,{"disambiguationData":[TD([makeQuery(id+"F2.opExtrude","CAP_FACE",FACE,{"disambiguationData":[OSD([subQ2,subQ1,subQ0,sQuery(id+"F0.wireOp",EDGE,"E20")])],"isStart":false})])],"derivedFrom":makeQuery(id+"F2.opExtrude","SWEPT_FACE",FACE,{"disambiguationData":[OSD([subQ2]),TDD([subQ3])]})})]});}
            var Q35;
            {var subQ0=sQuery(id+"F0.wireOp",EDGE,"E19.1.5.0");var subQ1=sQuery(id+"F0.wireOp",EDGE,"E4");var subQ2=sQuery(id+"F0.wireOp",EDGE,"E19.3.5.0");var subQ3=makeQuery(id+"F0.imprint","IMPRINT",EDGE,{"disambiguationData":[TD([[makeQuery(id+"F0.imprint","INTERSECT",VERTEX,{"derivedFrom":[subQ1,subQ0]}),1.0]])],"derivedFrom":subQ1});var subQ4=sQuery(id+"F0.wireOp",EDGE,"E20");Q35=makeQuery(id+"F8.opChamfer","BLEND_EDGE",EDGE,{"blendedFrom":[makeQuery(id+"F2.opExtrude","CAP_EDGE",EDGE,{"disambiguationData":[OSD([subQ1]),TDD([subQ3])],"isStart":false}),makeQuery(id+"F2.boolean.opBoolean","SPLIT",FACE,{"disambiguationData":[TD([makeQuery(id+"F2.opExtrude","CAP_FACE",FACE,{"disambiguationData":[OSD([subQ1,subQ0,subQ2,subQ4])],"isStart":false})])],"derivedFrom":makeQuery(id+"F2.opExtrude","SWEPT_FACE",FACE,{"disambiguationData":[OSD([subQ0])]})})],"blendedInto":[makeQuery(id+"F2.boolean.opBoolean","SPLIT",FACE,{"disambiguationData":[TD([makeQuery(id+"F2.opExtrude","CAP_FACE",FACE,{"disambiguationData":[OSD([subQ1,subQ0,subQ2,subQ4])],"isStart":false})])],"derivedFrom":makeQuery(id+"F2.opExtrude","SWEPT_FACE",FACE,{"disambiguationData":[OSD([subQ0])]})})]});}
            var Q36;
            {var subQ0=sQuery(id+"F0.wireOp",EDGE,"E19.1.6.0");var subQ1=sQuery(id+"F0.wireOp",EDGE,"E19.3.6.0");var subQ2=sQuery(id+"F0.wireOp",EDGE,"E4");var subQ3=makeQuery(id+"F0.imprint","IMPRINT",EDGE,{"disambiguationData":[TD([[makeQuery(id+"F0.imprint","INTERSECT",VERTEX,{"derivedFrom":[subQ2,subQ0]}),1.0]])],"derivedFrom":subQ2});Q36=makeQuery(id+"F8.opChamfer","BLEND_EDGE",EDGE,{"blendedFrom":[makeQuery(id+"F2.opExtrude","CAP_EDGE",EDGE,{"disambiguationData":[OSD([subQ2]),TDD([subQ3])],"isStart":false}),makeQuery(id+"F2.boolean.opBoolean","SPLIT",FACE,{"disambiguationData":[TD([makeQuery(id+"F2.opExtrude","CAP_FACE",FACE,{"disambiguationData":[OSD([subQ2,subQ0,subQ1,sQuery(id+"F0.wireOp",EDGE,"E20")])],"isStart":false})])],"derivedFrom":makeQuery(id+"F2.opExtrude","SWEPT_FACE",FACE,{"disambiguationData":[OSD([subQ2]),TDD([subQ3])]})})],"blendedInto":[makeQuery(id+"F2.boolean.opBoolean","SPLIT",FACE,{"disambiguationData":[TD([makeQuery(id+"F2.opExtrude","CAP_FACE",FACE,{"disambiguationData":[OSD([subQ2,subQ0,subQ1,sQuery(id+"F0.wireOp",EDGE,"E20")])],"isStart":false})])],"derivedFrom":makeQuery(id+"F2.opExtrude","SWEPT_FACE",FACE,{"disambiguationData":[OSD([subQ2]),TDD([subQ3])]})})]});}
            var Q37;
            {var subQ0=sQuery(id+"F0.wireOp",EDGE,"E20");var subQ1=sQuery(id+"F0.wireOp",EDGE,"E19.1.6.0");var subQ2=sQuery(id+"F0.wireOp",EDGE,"E19.3.6.0");var subQ3=sQuery(id+"F0.wireOp",EDGE,"E4");var subQ4=makeQuery(id+"F0.imprint","IMPRINT",EDGE,{"disambiguationData":[TD([[makeQuery(id+"F0.imprint","INTERSECT",VERTEX,{"derivedFrom":[subQ3,subQ1]}),1.0]])],"derivedFrom":subQ3});Q37=makeQuery(id+"F8.opChamfer","BLEND_EDGE",EDGE,{"blendedFrom":[makeQuery(id+"F2.opExtrude","CAP_EDGE",EDGE,{"disambiguationData":[OSD([subQ3]),TDD([subQ4])],"isStart":false}),makeQuery(id+"F2.boolean.opBoolean","SPLIT",FACE,{"disambiguationData":[TD([makeQuery(id+"F2.opExtrude","CAP_FACE",FACE,{"disambiguationData":[OSD([subQ3,subQ1,subQ2,subQ0])],"isStart":false})])],"derivedFrom":makeQuery(id+"F2.opExtrude","SWEPT_FACE",FACE,{"disambiguationData":[OSD([subQ1])]})})],"blendedInto":[makeQuery(id+"F2.boolean.opBoolean","SPLIT",FACE,{"disambiguationData":[TD([makeQuery(id+"F2.opExtrude","CAP_FACE",FACE,{"disambiguationData":[OSD([subQ3,subQ1,subQ2,subQ0])],"isStart":false})])],"derivedFrom":makeQuery(id+"F2.opExtrude","SWEPT_FACE",FACE,{"disambiguationData":[OSD([subQ1])]})})]});}
            var Q38;
            {var subQ0=sQuery(id+"F0.wireOp",EDGE,"E20");var subQ1=sQuery(id+"F0.wireOp",EDGE,"E19.1.6.0");var subQ2=sQuery(id+"F0.wireOp",EDGE,"E19.3.6.0");var subQ3=sQuery(id+"F0.wireOp",EDGE,"E4");var subQ4=makeQuery(id+"F0.imprint","IMPRINT",EDGE,{"disambiguationData":[TD([[makeQuery(id+"F0.imprint","INTERSECT",VERTEX,{"derivedFrom":[subQ3,subQ1]}),1.0]])],"derivedFrom":subQ3});Q38=makeQuery(id+"F8.opChamfer","BLEND_EDGE",EDGE,{"blendedFrom":[makeQuery(id+"F2.opExtrude","CAP_EDGE",EDGE,{"disambiguationData":[OSD([subQ3]),TDD([subQ4])],"isStart":false}),makeQuery(id+"F2.boolean.opBoolean","SPLIT",FACE,{"disambiguationData":[TD([makeQuery(id+"F2.opExtrude","CAP_FACE",FACE,{"disambiguationData":[OSD([subQ3,subQ1,subQ2,subQ0])],"isStart":false})])],"derivedFrom":makeQuery(id+"F2.opExtrude","SWEPT_FACE",FACE,{"disambiguationData":[OSD([subQ2])]})})],"blendedInto":[makeQuery(id+"F2.boolean.opBoolean","SPLIT",FACE,{"disambiguationData":[TD([makeQuery(id+"F2.opExtrude","CAP_FACE",FACE,{"disambiguationData":[OSD([subQ3,subQ1,subQ2,subQ0])],"isStart":false})])],"derivedFrom":makeQuery(id+"F2.opExtrude","SWEPT_FACE",FACE,{"disambiguationData":[OSD([subQ2])]})})]});}
            var Q39;
            {var subQ0=sQuery(id+"F0.wireOp",EDGE,"E20");var subQ1=sQuery(id+"F0.wireOp",EDGE,"E19.1.6.0");var subQ2=sQuery(id+"F0.wireOp",EDGE,"E19.3.6.0");var subQ3=makeQuery(id+"F0.imprint","IMPRINT",EDGE,{"disambiguationData":[TD([[makeQuery(id+"F0.imprint","INTERSECT",VERTEX,{"derivedFrom":[subQ1,subQ0]}),1.0]])],"derivedFrom":subQ0});var subQ4=sQuery(id+"F0.wireOp",EDGE,"E4");Q39=makeQuery(id+"F9.opChamfer","BLEND_EDGE",EDGE,{"blendedFrom":[makeQuery(id+"F2.opExtrude","CAP_EDGE",EDGE,{"disambiguationData":[OSD([subQ0]),TDD([subQ3])],"isStart":false}),makeQuery(id+"F2.boolean.opBoolean","SPLIT",FACE,{"disambiguationData":[TD([makeQuery(id+"F2.opExtrude","CAP_FACE",FACE,{"disambiguationData":[OSD([subQ4,subQ1,subQ2,subQ0])],"isStart":false})])],"derivedFrom":makeQuery(id+"F2.opExtrude","SWEPT_FACE",FACE,{"disambiguationData":[OSD([subQ1])]})})],"blendedInto":[makeQuery(id+"F2.boolean.opBoolean","SPLIT",FACE,{"disambiguationData":[TD([makeQuery(id+"F2.opExtrude","CAP_FACE",FACE,{"disambiguationData":[OSD([subQ4,subQ1,subQ2,subQ0])],"isStart":false})])],"derivedFrom":makeQuery(id+"F2.opExtrude","SWEPT_FACE",FACE,{"disambiguationData":[OSD([subQ1])]})})]});}
            var Q40;
            {var subQ0=sQuery(id+"F0.wireOp",EDGE,"E20");var subQ1=sQuery(id+"F0.wireOp",EDGE,"E19.1.6.0");var subQ2=sQuery(id+"F0.wireOp",EDGE,"E19.3.6.0");var subQ3=makeQuery(id+"F0.imprint","IMPRINT",EDGE,{"disambiguationData":[TD([[makeQuery(id+"F0.imprint","INTERSECT",VERTEX,{"derivedFrom":[subQ1,subQ0]}),1.0]])],"derivedFrom":subQ0});var subQ4=sQuery(id+"F0.wireOp",EDGE,"E4");Q40=makeQuery(id+"F9.opChamfer","BLEND_EDGE",EDGE,{"blendedFrom":[makeQuery(id+"F2.opExtrude","CAP_EDGE",EDGE,{"disambiguationData":[OSD([subQ0]),TDD([subQ3])],"isStart":false}),makeQuery(id+"F2.boolean.opBoolean","SPLIT",FACE,{"disambiguationData":[TD([makeQuery(id+"F2.opExtrude","CAP_FACE",FACE,{"disambiguationData":[OSD([subQ4,subQ1,subQ2,subQ0])],"isStart":false})])],"derivedFrom":makeQuery(id+"F2.opExtrude","SWEPT_FACE",FACE,{"disambiguationData":[OSD([subQ2])]})})],"blendedInto":[makeQuery(id+"F2.boolean.opBoolean","SPLIT",FACE,{"disambiguationData":[TD([makeQuery(id+"F2.opExtrude","CAP_FACE",FACE,{"disambiguationData":[OSD([subQ4,subQ1,subQ2,subQ0])],"isStart":false})])],"derivedFrom":makeQuery(id+"F2.opExtrude","SWEPT_FACE",FACE,{"disambiguationData":[OSD([subQ2])]})})]});}
            var Q41;
            {var subQ0=sQuery(id+"F0.wireOp",EDGE,"E19.1.6.0");var subQ1=sQuery(id+"F0.wireOp",EDGE,"E20");var subQ2=sQuery(id+"F0.wireOp",EDGE,"E19.3.6.0");var subQ3=makeQuery(id+"F0.imprint","IMPRINT",EDGE,{"disambiguationData":[TD([[makeQuery(id+"F0.imprint","INTERSECT",VERTEX,{"derivedFrom":[subQ0,subQ1]}),1.0]])],"derivedFrom":subQ1});Q41=makeQuery(id+"F9.opChamfer","BLEND_EDGE",EDGE,{"blendedFrom":[makeQuery(id+"F2.opExtrude","CAP_EDGE",EDGE,{"disambiguationData":[OSD([subQ1]),TDD([subQ3])],"isStart":false}),makeQuery(id+"F2.boolean.opBoolean","SPLIT",FACE,{"disambiguationData":[TD([makeQuery(id+"F2.opExtrude","CAP_FACE",FACE,{"disambiguationData":[OSD([sQuery(id+"F0.wireOp",EDGE,"E4"),subQ0,subQ2,subQ1])],"isStart":false})])],"derivedFrom":makeQuery(id+"F2.opExtrude","SWEPT_FACE",FACE,{"disambiguationData":[OSD([subQ1]),TDD([subQ3])]})})],"blendedInto":[makeQuery(id+"F2.boolean.opBoolean","SPLIT",FACE,{"disambiguationData":[TD([makeQuery(id+"F2.opExtrude","CAP_FACE",FACE,{"disambiguationData":[OSD([sQuery(id+"F0.wireOp",EDGE,"E4"),subQ0,subQ2,subQ1])],"isStart":false})])],"derivedFrom":makeQuery(id+"F2.opExtrude","SWEPT_FACE",FACE,{"disambiguationData":[OSD([subQ1]),TDD([subQ3])]})})]});}
            var Q42;
            {var subQ0=sQuery(id+"F0.wireOp",EDGE,"E19.1.7.0");var subQ1=sQuery(id+"F0.wireOp",EDGE,"E4");var subQ2=sQuery(id+"F0.wireOp",EDGE,"E19.3.7.0");var subQ3=sQuery(id+"F0.wireOp",EDGE,"E20");var subQ4=makeQuery(id+"F0.imprint","IMPRINT",EDGE,{"disambiguationData":[TD([[makeQuery(id+"F0.imprint","INTERSECT",VERTEX,{"derivedFrom":[subQ0,subQ3]}),1.0]])],"derivedFrom":subQ3});Q42=makeQuery(id+"F9.opChamfer","BLEND_EDGE",EDGE,{"blendedFrom":[makeQuery(id+"F2.opExtrude","CAP_EDGE",EDGE,{"disambiguationData":[OSD([subQ3]),TDD([subQ4])],"isStart":false}),makeQuery(id+"F2.boolean.opBoolean","SPLIT",FACE,{"disambiguationData":[TD([makeQuery(id+"F2.opExtrude","CAP_FACE",FACE,{"disambiguationData":[OSD([subQ1,subQ0,subQ2,subQ3])],"isStart":false})])],"derivedFrom":makeQuery(id+"F2.opExtrude","SWEPT_FACE",FACE,{"disambiguationData":[OSD([subQ0])]})})],"blendedInto":[makeQuery(id+"F2.boolean.opBoolean","SPLIT",FACE,{"disambiguationData":[TD([makeQuery(id+"F2.opExtrude","CAP_FACE",FACE,{"disambiguationData":[OSD([subQ1,subQ0,subQ2,subQ3])],"isStart":false})])],"derivedFrom":makeQuery(id+"F2.opExtrude","SWEPT_FACE",FACE,{"disambiguationData":[OSD([subQ0])]})})]});}
            var Q43;
            {var subQ0=sQuery(id+"F0.wireOp",EDGE,"E19.1.7.0");var subQ1=sQuery(id+"F0.wireOp",EDGE,"E4");var subQ2=sQuery(id+"F0.wireOp",EDGE,"E19.3.7.0");var subQ3=sQuery(id+"F0.wireOp",EDGE,"E20");var subQ4=makeQuery(id+"F0.imprint","IMPRINT",EDGE,{"disambiguationData":[TD([[makeQuery(id+"F0.imprint","INTERSECT",VERTEX,{"derivedFrom":[subQ0,subQ3]}),1.0]])],"derivedFrom":subQ3});Q43=makeQuery(id+"F9.opChamfer","BLEND_EDGE",EDGE,{"blendedFrom":[makeQuery(id+"F2.opExtrude","CAP_EDGE",EDGE,{"disambiguationData":[OSD([subQ3]),TDD([subQ4])],"isStart":false}),makeQuery(id+"F2.boolean.opBoolean","SPLIT",FACE,{"disambiguationData":[TD([makeQuery(id+"F2.opExtrude","CAP_FACE",FACE,{"disambiguationData":[OSD([subQ1,subQ0,subQ2,subQ3])],"isStart":false})])],"derivedFrom":makeQuery(id+"F2.opExtrude","SWEPT_FACE",FACE,{"disambiguationData":[OSD([subQ2])]})})],"blendedInto":[makeQuery(id+"F2.boolean.opBoolean","SPLIT",FACE,{"disambiguationData":[TD([makeQuery(id+"F2.opExtrude","CAP_FACE",FACE,{"disambiguationData":[OSD([subQ1,subQ0,subQ2,subQ3])],"isStart":false})])],"derivedFrom":makeQuery(id+"F2.opExtrude","SWEPT_FACE",FACE,{"disambiguationData":[OSD([subQ2])]})})]});}
            var Q44;
            {var subQ0=sQuery(id+"F0.wireOp",EDGE,"E19.1.7.0");var subQ1=sQuery(id+"F0.wireOp",EDGE,"E4");var subQ2=sQuery(id+"F0.wireOp",EDGE,"E19.3.7.0");var subQ3=makeQuery(id+"F0.imprint","IMPRINT",EDGE,{"disambiguationData":[TD([[makeQuery(id+"F0.imprint","INTERSECT",VERTEX,{"derivedFrom":[subQ1,subQ0]}),1.0]])],"derivedFrom":subQ1});var subQ4=sQuery(id+"F0.wireOp",EDGE,"E20");Q44=makeQuery(id+"F8.opChamfer","BLEND_EDGE",EDGE,{"blendedFrom":[makeQuery(id+"F2.opExtrude","CAP_EDGE",EDGE,{"disambiguationData":[OSD([subQ1]),TDD([subQ3])],"isStart":false}),makeQuery(id+"F2.boolean.opBoolean","SPLIT",FACE,{"disambiguationData":[TD([makeQuery(id+"F2.opExtrude","CAP_FACE",FACE,{"disambiguationData":[OSD([subQ1,subQ0,subQ2,subQ4])],"isStart":false})])],"derivedFrom":makeQuery(id+"F2.opExtrude","SWEPT_FACE",FACE,{"disambiguationData":[OSD([subQ0])]})})],"blendedInto":[makeQuery(id+"F2.boolean.opBoolean","SPLIT",FACE,{"disambiguationData":[TD([makeQuery(id+"F2.opExtrude","CAP_FACE",FACE,{"disambiguationData":[OSD([subQ1,subQ0,subQ2,subQ4])],"isStart":false})])],"derivedFrom":makeQuery(id+"F2.opExtrude","SWEPT_FACE",FACE,{"disambiguationData":[OSD([subQ0])]})})]});}
            var Q45;
            {var subQ0=sQuery(id+"F0.wireOp",EDGE,"E19.1.7.0");var subQ1=sQuery(id+"F0.wireOp",EDGE,"E4");var subQ2=sQuery(id+"F0.wireOp",EDGE,"E19.3.7.0");var subQ3=makeQuery(id+"F0.imprint","IMPRINT",EDGE,{"disambiguationData":[TD([[makeQuery(id+"F0.imprint","INTERSECT",VERTEX,{"derivedFrom":[subQ1,subQ0]}),1.0]])],"derivedFrom":subQ1});var subQ4=sQuery(id+"F0.wireOp",EDGE,"E20");Q45=makeQuery(id+"F8.opChamfer","BLEND_EDGE",EDGE,{"blendedFrom":[makeQuery(id+"F2.opExtrude","CAP_EDGE",EDGE,{"disambiguationData":[OSD([subQ1]),TDD([subQ3])],"isStart":false}),makeQuery(id+"F2.boolean.opBoolean","SPLIT",FACE,{"disambiguationData":[TD([makeQuery(id+"F2.opExtrude","CAP_FACE",FACE,{"disambiguationData":[OSD([subQ1,subQ0,subQ2,subQ4])],"isStart":false})])],"derivedFrom":makeQuery(id+"F2.opExtrude","SWEPT_FACE",FACE,{"disambiguationData":[OSD([subQ2])]})})],"blendedInto":[makeQuery(id+"F2.boolean.opBoolean","SPLIT",FACE,{"disambiguationData":[TD([makeQuery(id+"F2.opExtrude","CAP_FACE",FACE,{"disambiguationData":[OSD([subQ1,subQ0,subQ2,subQ4])],"isStart":false})])],"derivedFrom":makeQuery(id+"F2.opExtrude","SWEPT_FACE",FACE,{"disambiguationData":[OSD([subQ2])]})})]});}
            var Q46;
            {var subQ0=sQuery(id+"F0.wireOp",EDGE,"E19.3.7.0");var subQ1=sQuery(id+"F0.wireOp",EDGE,"E19.1.7.0");var subQ2=sQuery(id+"F0.wireOp",EDGE,"E4");var subQ3=makeQuery(id+"F0.imprint","IMPRINT",EDGE,{"disambiguationData":[TD([[makeQuery(id+"F0.imprint","INTERSECT",VERTEX,{"derivedFrom":[subQ2,subQ1]}),1.0]])],"derivedFrom":subQ2});Q46=makeQuery(id+"F8.opChamfer","BLEND_EDGE",EDGE,{"blendedFrom":[makeQuery(id+"F2.opExtrude","CAP_EDGE",EDGE,{"disambiguationData":[OSD([subQ2]),TDD([subQ3])],"isStart":false}),makeQuery(id+"F2.boolean.opBoolean","SPLIT",FACE,{"disambiguationData":[TD([makeQuery(id+"F2.opExtrude","CAP_FACE",FACE,{"disambiguationData":[OSD([subQ2,subQ1,subQ0,sQuery(id+"F0.wireOp",EDGE,"E20")])],"isStart":false})])],"derivedFrom":makeQuery(id+"F2.opExtrude","SWEPT_FACE",FACE,{"disambiguationData":[OSD([subQ2]),TDD([subQ3])]})})],"blendedInto":[makeQuery(id+"F2.boolean.opBoolean","SPLIT",FACE,{"disambiguationData":[TD([makeQuery(id+"F2.opExtrude","CAP_FACE",FACE,{"disambiguationData":[OSD([subQ2,subQ1,subQ0,sQuery(id+"F0.wireOp",EDGE,"E20")])],"isStart":false})])],"derivedFrom":makeQuery(id+"F2.opExtrude","SWEPT_FACE",FACE,{"disambiguationData":[OSD([subQ2]),TDD([subQ3])]})})]});}
            var Q47;
            {var subQ0=sQuery(id+"F0.wireOp",EDGE,"E19.3.8.0");var subQ1=sQuery(id+"F0.wireOp",EDGE,"E19.1.8.0");var subQ2=sQuery(id+"F0.wireOp",EDGE,"E4");var subQ3=makeQuery(id+"F0.imprint","IMPRINT",EDGE,{"disambiguationData":[TD([[makeQuery(id+"F0.imprint","INTERSECT",VERTEX,{"derivedFrom":[subQ2,subQ1]}),1.0]])],"derivedFrom":subQ2});Q47=makeQuery(id+"F8.opChamfer","BLEND_EDGE",EDGE,{"blendedFrom":[makeQuery(id+"F2.opExtrude","CAP_EDGE",EDGE,{"disambiguationData":[OSD([subQ2]),TDD([subQ3])],"isStart":false}),makeQuery(id+"F2.boolean.opBoolean","SPLIT",FACE,{"disambiguationData":[TD([makeQuery(id+"F2.opExtrude","CAP_FACE",FACE,{"disambiguationData":[OSD([subQ2,subQ1,subQ0,sQuery(id+"F0.wireOp",EDGE,"E20")])],"isStart":false})])],"derivedFrom":makeQuery(id+"F2.opExtrude","SWEPT_FACE",FACE,{"disambiguationData":[OSD([subQ2]),TDD([subQ3])]})})],"blendedInto":[makeQuery(id+"F2.boolean.opBoolean","SPLIT",FACE,{"disambiguationData":[TD([makeQuery(id+"F2.opExtrude","CAP_FACE",FACE,{"disambiguationData":[OSD([subQ2,subQ1,subQ0,sQuery(id+"F0.wireOp",EDGE,"E20")])],"isStart":false})])],"derivedFrom":makeQuery(id+"F2.opExtrude","SWEPT_FACE",FACE,{"disambiguationData":[OSD([subQ2]),TDD([subQ3])]})})]});}
            var Q48;
            {var subQ0=sQuery(id+"F0.wireOp",EDGE,"E19.1.8.0");var subQ1=sQuery(id+"F0.wireOp",EDGE,"E4");var subQ2=sQuery(id+"F0.wireOp",EDGE,"E19.3.8.0");var subQ3=makeQuery(id+"F0.imprint","IMPRINT",EDGE,{"disambiguationData":[TD([[makeQuery(id+"F0.imprint","INTERSECT",VERTEX,{"derivedFrom":[subQ1,subQ0]}),1.0]])],"derivedFrom":subQ1});var subQ4=sQuery(id+"F0.wireOp",EDGE,"E20");Q48=makeQuery(id+"F8.opChamfer","BLEND_EDGE",EDGE,{"blendedFrom":[makeQuery(id+"F2.opExtrude","CAP_EDGE",EDGE,{"disambiguationData":[OSD([subQ1]),TDD([subQ3])],"isStart":false}),makeQuery(id+"F2.boolean.opBoolean","SPLIT",FACE,{"disambiguationData":[TD([makeQuery(id+"F2.opExtrude","CAP_FACE",FACE,{"disambiguationData":[OSD([subQ1,subQ0,subQ2,subQ4])],"isStart":false})])],"derivedFrom":makeQuery(id+"F2.opExtrude","SWEPT_FACE",FACE,{"disambiguationData":[OSD([subQ0])]})})],"blendedInto":[makeQuery(id+"F2.boolean.opBoolean","SPLIT",FACE,{"disambiguationData":[TD([makeQuery(id+"F2.opExtrude","CAP_FACE",FACE,{"disambiguationData":[OSD([subQ1,subQ0,subQ2,subQ4])],"isStart":false})])],"derivedFrom":makeQuery(id+"F2.opExtrude","SWEPT_FACE",FACE,{"disambiguationData":[OSD([subQ0])]})})]});}
            var Q49;
            {var subQ0=sQuery(id+"F0.wireOp",EDGE,"E19.1.8.0");var subQ1=sQuery(id+"F0.wireOp",EDGE,"E4");var subQ2=sQuery(id+"F0.wireOp",EDGE,"E19.3.8.0");var subQ3=sQuery(id+"F0.wireOp",EDGE,"E20");var subQ4=makeQuery(id+"F0.imprint","IMPRINT",EDGE,{"disambiguationData":[TD([[makeQuery(id+"F0.imprint","INTERSECT",VERTEX,{"derivedFrom":[subQ0,subQ3]}),1.0]])],"derivedFrom":subQ3});Q49=makeQuery(id+"F9.opChamfer","BLEND_EDGE",EDGE,{"blendedFrom":[makeQuery(id+"F2.opExtrude","CAP_EDGE",EDGE,{"disambiguationData":[OSD([subQ3]),TDD([subQ4])],"isStart":false}),makeQuery(id+"F2.boolean.opBoolean","SPLIT",FACE,{"disambiguationData":[TD([makeQuery(id+"F2.opExtrude","CAP_FACE",FACE,{"disambiguationData":[OSD([subQ1,subQ0,subQ2,subQ3])],"isStart":false})])],"derivedFrom":makeQuery(id+"F2.opExtrude","SWEPT_FACE",FACE,{"disambiguationData":[OSD([subQ0])]})})],"blendedInto":[makeQuery(id+"F2.boolean.opBoolean","SPLIT",FACE,{"disambiguationData":[TD([makeQuery(id+"F2.opExtrude","CAP_FACE",FACE,{"disambiguationData":[OSD([subQ1,subQ0,subQ2,subQ3])],"isStart":false})])],"derivedFrom":makeQuery(id+"F2.opExtrude","SWEPT_FACE",FACE,{"disambiguationData":[OSD([subQ0])]})})]});}
            var Q50;
            {var subQ0=sQuery(id+"F0.wireOp",EDGE,"E19.3.8.0");var subQ1=sQuery(id+"F0.wireOp",EDGE,"E20");var subQ2=sQuery(id+"F0.wireOp",EDGE,"E19.1.8.0");var subQ3=makeQuery(id+"F0.imprint","IMPRINT",EDGE,{"disambiguationData":[TD([[makeQuery(id+"F0.imprint","INTERSECT",VERTEX,{"derivedFrom":[subQ2,subQ1]}),1.0]])],"derivedFrom":subQ1});Q50=makeQuery(id+"F9.opChamfer","BLEND_EDGE",EDGE,{"blendedFrom":[makeQuery(id+"F2.opExtrude","CAP_EDGE",EDGE,{"disambiguationData":[OSD([subQ1]),TDD([subQ3])],"isStart":false}),makeQuery(id+"F2.boolean.opBoolean","SPLIT",FACE,{"disambiguationData":[TD([makeQuery(id+"F2.opExtrude","CAP_FACE",FACE,{"disambiguationData":[OSD([sQuery(id+"F0.wireOp",EDGE,"E4"),subQ2,subQ0,subQ1])],"isStart":false})])],"derivedFrom":makeQuery(id+"F2.opExtrude","SWEPT_FACE",FACE,{"disambiguationData":[OSD([subQ1]),TDD([subQ3])]})})],"blendedInto":[makeQuery(id+"F2.boolean.opBoolean","SPLIT",FACE,{"disambiguationData":[TD([makeQuery(id+"F2.opExtrude","CAP_FACE",FACE,{"disambiguationData":[OSD([sQuery(id+"F0.wireOp",EDGE,"E4"),subQ2,subQ0,subQ1])],"isStart":false})])],"derivedFrom":makeQuery(id+"F2.opExtrude","SWEPT_FACE",FACE,{"disambiguationData":[OSD([subQ1]),TDD([subQ3])]})})]});}
            var Q51;
            {var subQ0=sQuery(id+"F0.wireOp",EDGE,"E19.1.8.0");var subQ1=sQuery(id+"F0.wireOp",EDGE,"E4");var subQ2=sQuery(id+"F0.wireOp",EDGE,"E19.3.8.0");var subQ3=sQuery(id+"F0.wireOp",EDGE,"E20");var subQ4=makeQuery(id+"F0.imprint","IMPRINT",EDGE,{"disambiguationData":[TD([[makeQuery(id+"F0.imprint","INTERSECT",VERTEX,{"derivedFrom":[subQ0,subQ3]}),1.0]])],"derivedFrom":subQ3});Q51=makeQuery(id+"F9.opChamfer","BLEND_EDGE",EDGE,{"blendedFrom":[makeQuery(id+"F2.opExtrude","CAP_EDGE",EDGE,{"disambiguationData":[OSD([subQ3]),TDD([subQ4])],"isStart":false}),makeQuery(id+"F2.boolean.opBoolean","SPLIT",FACE,{"disambiguationData":[TD([makeQuery(id+"F2.opExtrude","CAP_FACE",FACE,{"disambiguationData":[OSD([subQ1,subQ0,subQ2,subQ3])],"isStart":false})])],"derivedFrom":makeQuery(id+"F2.opExtrude","SWEPT_FACE",FACE,{"disambiguationData":[OSD([subQ2])]})})],"blendedInto":[makeQuery(id+"F2.boolean.opBoolean","SPLIT",FACE,{"disambiguationData":[TD([makeQuery(id+"F2.opExtrude","CAP_FACE",FACE,{"disambiguationData":[OSD([subQ1,subQ0,subQ2,subQ3])],"isStart":false})])],"derivedFrom":makeQuery(id+"F2.opExtrude","SWEPT_FACE",FACE,{"disambiguationData":[OSD([subQ2])]})})]});}
            var Q52;
            {var subQ0=sQuery(id+"F0.wireOp",EDGE,"E19.1.8.0");var subQ1=sQuery(id+"F0.wireOp",EDGE,"E4");var subQ2=sQuery(id+"F0.wireOp",EDGE,"E19.3.8.0");var subQ3=makeQuery(id+"F0.imprint","IMPRINT",EDGE,{"disambiguationData":[TD([[makeQuery(id+"F0.imprint","INTERSECT",VERTEX,{"derivedFrom":[subQ1,subQ0]}),1.0]])],"derivedFrom":subQ1});var subQ4=sQuery(id+"F0.wireOp",EDGE,"E20");Q52=makeQuery(id+"F8.opChamfer","BLEND_EDGE",EDGE,{"blendedFrom":[makeQuery(id+"F2.opExtrude","CAP_EDGE",EDGE,{"disambiguationData":[OSD([subQ1]),TDD([subQ3])],"isStart":false}),makeQuery(id+"F2.boolean.opBoolean","SPLIT",FACE,{"disambiguationData":[TD([makeQuery(id+"F2.opExtrude","CAP_FACE",FACE,{"disambiguationData":[OSD([subQ1,subQ0,subQ2,subQ4])],"isStart":false})])],"derivedFrom":makeQuery(id+"F2.opExtrude","SWEPT_FACE",FACE,{"disambiguationData":[OSD([subQ2])]})})],"blendedInto":[makeQuery(id+"F2.boolean.opBoolean","SPLIT",FACE,{"disambiguationData":[TD([makeQuery(id+"F2.opExtrude","CAP_FACE",FACE,{"disambiguationData":[OSD([subQ1,subQ0,subQ2,subQ4])],"isStart":false})])],"derivedFrom":makeQuery(id+"F2.opExtrude","SWEPT_FACE",FACE,{"disambiguationData":[OSD([subQ2])]})})]});}
            var Q53;
            {var subQ0=sQuery(id+"F0.wireOp",EDGE,"E20");var subQ1=sQuery(id+"F0.wireOp",EDGE,"E19.3.7.0");var subQ2=sQuery(id+"F0.wireOp",EDGE,"E19.1.7.0");var subQ3=makeQuery(id+"F0.imprint","IMPRINT",EDGE,{"disambiguationData":[TD([[makeQuery(id+"F0.imprint","INTERSECT",VERTEX,{"derivedFrom":[subQ2,subQ0]}),1.0]])],"derivedFrom":subQ0});Q53=makeQuery(id+"F9.opChamfer","BLEND_EDGE",EDGE,{"blendedFrom":[makeQuery(id+"F2.opExtrude","CAP_EDGE",EDGE,{"disambiguationData":[OSD([subQ0]),TDD([subQ3])],"isStart":false}),makeQuery(id+"F2.boolean.opBoolean","SPLIT",FACE,{"disambiguationData":[TD([makeQuery(id+"F2.opExtrude","CAP_FACE",FACE,{"disambiguationData":[OSD([sQuery(id+"F0.wireOp",EDGE,"E4"),subQ2,subQ1,subQ0])],"isStart":false})])],"derivedFrom":makeQuery(id+"F2.opExtrude","SWEPT_FACE",FACE,{"disambiguationData":[OSD([subQ0]),TDD([subQ3])]})})],"blendedInto":[makeQuery(id+"F2.boolean.opBoolean","SPLIT",FACE,{"disambiguationData":[TD([makeQuery(id+"F2.opExtrude","CAP_FACE",FACE,{"disambiguationData":[OSD([sQuery(id+"F0.wireOp",EDGE,"E4"),subQ2,subQ1,subQ0])],"isStart":false})])],"derivedFrom":makeQuery(id+"F2.opExtrude","SWEPT_FACE",FACE,{"disambiguationData":[OSD([subQ0]),TDD([subQ3])]})})]});}
            var Q54;
            {var subQ0=sQuery(id+"F0.wireOp",EDGE,"E20");var subQ1=sQuery(id+"F0.wireOp",EDGE,"E19.3.9.0");var subQ2=sQuery(id+"F0.wireOp",EDGE,"E19.1.9.0");var subQ3=makeQuery(id+"F0.imprint","IMPRINT",EDGE,{"disambiguationData":[TD([[makeQuery(id+"F0.imprint","INTERSECT",VERTEX,{"derivedFrom":[subQ2,subQ0]}),1.0]])],"derivedFrom":subQ0});Q54=makeQuery(id+"F9.opChamfer","BLEND_EDGE",EDGE,{"blendedFrom":[makeQuery(id+"F2.opExtrude","CAP_EDGE",EDGE,{"disambiguationData":[OSD([subQ0]),TDD([subQ3])],"isStart":false}),makeQuery(id+"F2.boolean.opBoolean","SPLIT",FACE,{"disambiguationData":[TD([makeQuery(id+"F2.opExtrude","CAP_FACE",FACE,{"disambiguationData":[OSD([sQuery(id+"F0.wireOp",EDGE,"E4"),subQ2,subQ1,subQ0])],"isStart":false})])],"derivedFrom":makeQuery(id+"F2.opExtrude","SWEPT_FACE",FACE,{"disambiguationData":[OSD([subQ0]),TDD([subQ3])]})})],"blendedInto":[makeQuery(id+"F2.boolean.opBoolean","SPLIT",FACE,{"disambiguationData":[TD([makeQuery(id+"F2.opExtrude","CAP_FACE",FACE,{"disambiguationData":[OSD([sQuery(id+"F0.wireOp",EDGE,"E4"),subQ2,subQ1,subQ0])],"isStart":false})])],"derivedFrom":makeQuery(id+"F2.opExtrude","SWEPT_FACE",FACE,{"disambiguationData":[OSD([subQ0]),TDD([subQ3])]})})]});}
            var Q55;
            {var subQ0=sQuery(id+"F0.wireOp",EDGE,"E20");var subQ1=sQuery(id+"F0.wireOp",EDGE,"E19.3.9.0");var subQ2=sQuery(id+"F0.wireOp",EDGE,"E19.1.9.0");var subQ3=sQuery(id+"F0.wireOp",EDGE,"E4");var subQ4=makeQuery(id+"F0.imprint","IMPRINT",EDGE,{"disambiguationData":[TD([[makeQuery(id+"F0.imprint","INTERSECT",VERTEX,{"derivedFrom":[subQ2,subQ0]}),1.0]])],"derivedFrom":subQ0});Q55=makeQuery(id+"F9.opChamfer","BLEND_EDGE",EDGE,{"blendedFrom":[makeQuery(id+"F2.opExtrude","CAP_EDGE",EDGE,{"disambiguationData":[OSD([subQ0]),TDD([subQ4])],"isStart":false}),makeQuery(id+"F2.boolean.opBoolean","SPLIT",FACE,{"disambiguationData":[TD([makeQuery(id+"F2.opExtrude","CAP_FACE",FACE,{"disambiguationData":[OSD([subQ3,subQ2,subQ1,subQ0])],"isStart":false})])],"derivedFrom":makeQuery(id+"F2.opExtrude","SWEPT_FACE",FACE,{"disambiguationData":[OSD([subQ2])]})})],"blendedInto":[makeQuery(id+"F2.boolean.opBoolean","SPLIT",FACE,{"disambiguationData":[TD([makeQuery(id+"F2.opExtrude","CAP_FACE",FACE,{"disambiguationData":[OSD([subQ3,subQ2,subQ1,subQ0])],"isStart":false})])],"derivedFrom":makeQuery(id+"F2.opExtrude","SWEPT_FACE",FACE,{"disambiguationData":[OSD([subQ2])]})})]});}
            var Q56;
            {var subQ0=sQuery(id+"F0.wireOp",EDGE,"E20");var subQ1=sQuery(id+"F0.wireOp",EDGE,"E19.3.9.0");var subQ2=sQuery(id+"F0.wireOp",EDGE,"E19.1.9.0");var subQ3=sQuery(id+"F0.wireOp",EDGE,"E4");var subQ4=makeQuery(id+"F0.imprint","IMPRINT",EDGE,{"disambiguationData":[TD([[makeQuery(id+"F0.imprint","INTERSECT",VERTEX,{"derivedFrom":[subQ2,subQ0]}),1.0]])],"derivedFrom":subQ0});Q56=makeQuery(id+"F9.opChamfer","BLEND_EDGE",EDGE,{"blendedFrom":[makeQuery(id+"F2.opExtrude","CAP_EDGE",EDGE,{"disambiguationData":[OSD([subQ0]),TDD([subQ4])],"isStart":false}),makeQuery(id+"F2.boolean.opBoolean","SPLIT",FACE,{"disambiguationData":[TD([makeQuery(id+"F2.opExtrude","CAP_FACE",FACE,{"disambiguationData":[OSD([subQ3,subQ2,subQ1,subQ0])],"isStart":false})])],"derivedFrom":makeQuery(id+"F2.opExtrude","SWEPT_FACE",FACE,{"disambiguationData":[OSD([subQ1])]})})],"blendedInto":[makeQuery(id+"F2.boolean.opBoolean","SPLIT",FACE,{"disambiguationData":[TD([makeQuery(id+"F2.opExtrude","CAP_FACE",FACE,{"disambiguationData":[OSD([subQ3,subQ2,subQ1,subQ0])],"isStart":false})])],"derivedFrom":makeQuery(id+"F2.opExtrude","SWEPT_FACE",FACE,{"disambiguationData":[OSD([subQ1])]})})]});}
            var Q57;
            {var subQ0=sQuery(id+"F0.wireOp",EDGE,"E20");var subQ1=sQuery(id+"F0.wireOp",EDGE,"E19.3.9.0");var subQ2=sQuery(id+"F0.wireOp",EDGE,"E19.1.9.0");var subQ3=sQuery(id+"F0.wireOp",EDGE,"E4");var subQ4=makeQuery(id+"F0.imprint","IMPRINT",EDGE,{"disambiguationData":[TD([[makeQuery(id+"F0.imprint","INTERSECT",VERTEX,{"derivedFrom":[subQ3,subQ2]}),1.0]])],"derivedFrom":subQ3});Q57=makeQuery(id+"F8.opChamfer","BLEND_EDGE",EDGE,{"blendedFrom":[makeQuery(id+"F2.opExtrude","CAP_EDGE",EDGE,{"disambiguationData":[OSD([subQ3]),TDD([subQ4])],"isStart":false}),makeQuery(id+"F2.boolean.opBoolean","SPLIT",FACE,{"disambiguationData":[TD([makeQuery(id+"F2.opExtrude","CAP_FACE",FACE,{"disambiguationData":[OSD([subQ3,subQ2,subQ1,subQ0])],"isStart":false})])],"derivedFrom":makeQuery(id+"F2.opExtrude","SWEPT_FACE",FACE,{"disambiguationData":[OSD([subQ1])]})})],"blendedInto":[makeQuery(id+"F2.boolean.opBoolean","SPLIT",FACE,{"disambiguationData":[TD([makeQuery(id+"F2.opExtrude","CAP_FACE",FACE,{"disambiguationData":[OSD([subQ3,subQ2,subQ1,subQ0])],"isStart":false})])],"derivedFrom":makeQuery(id+"F2.opExtrude","SWEPT_FACE",FACE,{"disambiguationData":[OSD([subQ1])]})})]});}
            var Q58;
            {var subQ0=sQuery(id+"F0.wireOp",EDGE,"E20");var subQ1=sQuery(id+"F0.wireOp",EDGE,"E19.3.9.0");var subQ2=sQuery(id+"F0.wireOp",EDGE,"E19.1.9.0");var subQ3=sQuery(id+"F0.wireOp",EDGE,"E4");var subQ4=makeQuery(id+"F0.imprint","IMPRINT",EDGE,{"disambiguationData":[TD([[makeQuery(id+"F0.imprint","INTERSECT",VERTEX,{"derivedFrom":[subQ3,subQ2]}),1.0]])],"derivedFrom":subQ3});Q58=makeQuery(id+"F8.opChamfer","BLEND_EDGE",EDGE,{"blendedFrom":[makeQuery(id+"F2.opExtrude","CAP_EDGE",EDGE,{"disambiguationData":[OSD([subQ3]),TDD([subQ4])],"isStart":false}),makeQuery(id+"F2.boolean.opBoolean","SPLIT",FACE,{"disambiguationData":[TD([makeQuery(id+"F2.opExtrude","CAP_FACE",FACE,{"disambiguationData":[OSD([subQ3,subQ2,subQ1,subQ0])],"isStart":false})])],"derivedFrom":makeQuery(id+"F2.opExtrude","SWEPT_FACE",FACE,{"disambiguationData":[OSD([subQ2])]})})],"blendedInto":[makeQuery(id+"F2.boolean.opBoolean","SPLIT",FACE,{"disambiguationData":[TD([makeQuery(id+"F2.opExtrude","CAP_FACE",FACE,{"disambiguationData":[OSD([subQ3,subQ2,subQ1,subQ0])],"isStart":false})])],"derivedFrom":makeQuery(id+"F2.opExtrude","SWEPT_FACE",FACE,{"disambiguationData":[OSD([subQ2])]})})]});}
            var Q59;
            {var subQ0=sQuery(id+"F0.wireOp",EDGE,"E19.3.9.0");var subQ1=sQuery(id+"F0.wireOp",EDGE,"E19.1.9.0");var subQ2=sQuery(id+"F0.wireOp",EDGE,"E4");var subQ3=makeQuery(id+"F0.imprint","IMPRINT",EDGE,{"disambiguationData":[TD([[makeQuery(id+"F0.imprint","INTERSECT",VERTEX,{"derivedFrom":[subQ2,subQ1]}),1.0]])],"derivedFrom":subQ2});Q59=makeQuery(id+"F8.opChamfer","BLEND_EDGE",EDGE,{"blendedFrom":[makeQuery(id+"F2.opExtrude","CAP_EDGE",EDGE,{"disambiguationData":[OSD([subQ2]),TDD([subQ3])],"isStart":false}),makeQuery(id+"F2.boolean.opBoolean","SPLIT",FACE,{"disambiguationData":[TD([makeQuery(id+"F2.opExtrude","CAP_FACE",FACE,{"disambiguationData":[OSD([subQ2,subQ1,subQ0,sQuery(id+"F0.wireOp",EDGE,"E20")])],"isStart":false})])],"derivedFrom":makeQuery(id+"F2.opExtrude","SWEPT_FACE",FACE,{"disambiguationData":[OSD([subQ2]),TDD([subQ3])]})})],"blendedInto":[makeQuery(id+"F2.boolean.opBoolean","SPLIT",FACE,{"disambiguationData":[TD([makeQuery(id+"F2.opExtrude","CAP_FACE",FACE,{"disambiguationData":[OSD([subQ2,subQ1,subQ0,sQuery(id+"F0.wireOp",EDGE,"E20")])],"isStart":false})])],"derivedFrom":makeQuery(id+"F2.opExtrude","SWEPT_FACE",FACE,{"disambiguationData":[OSD([subQ2]),TDD([subQ3])]})})]});}
            var Q60;
            {var subQ0=sQuery(id+"F0.wireOp",EDGE,"E19.1.10.0");var subQ1=sQuery(id+"F0.wireOp",EDGE,"E4");var subQ2=sQuery(id+"F0.wireOp",EDGE,"E19.3.10.0");var subQ3=makeQuery(id+"F0.imprint","IMPRINT",EDGE,{"disambiguationData":[TD([[makeQuery(id+"F0.imprint","INTERSECT",VERTEX,{"derivedFrom":[subQ1,subQ0]}),1.0]])],"derivedFrom":subQ1});var subQ4=sQuery(id+"F0.wireOp",EDGE,"E20");Q60=makeQuery(id+"F8.opChamfer","BLEND_EDGE",EDGE,{"blendedFrom":[makeQuery(id+"F2.opExtrude","CAP_EDGE",EDGE,{"disambiguationData":[OSD([subQ1]),TDD([subQ3])],"isStart":false}),makeQuery(id+"F2.boolean.opBoolean","SPLIT",FACE,{"disambiguationData":[TD([makeQuery(id+"F2.opExtrude","CAP_FACE",FACE,{"disambiguationData":[OSD([subQ1,subQ0,subQ2,subQ4])],"isStart":false})])],"derivedFrom":makeQuery(id+"F2.opExtrude","SWEPT_FACE",FACE,{"disambiguationData":[OSD([subQ0])]})})],"blendedInto":[makeQuery(id+"F2.boolean.opBoolean","SPLIT",FACE,{"disambiguationData":[TD([makeQuery(id+"F2.opExtrude","CAP_FACE",FACE,{"disambiguationData":[OSD([subQ1,subQ0,subQ2,subQ4])],"isStart":false})])],"derivedFrom":makeQuery(id+"F2.opExtrude","SWEPT_FACE",FACE,{"disambiguationData":[OSD([subQ0])]})})]});}
            var Q61;
            {var subQ0=sQuery(id+"F0.wireOp",EDGE,"E19.3.10.0");var subQ1=sQuery(id+"F0.wireOp",EDGE,"E19.1.10.0");var subQ2=sQuery(id+"F0.wireOp",EDGE,"E4");var subQ3=makeQuery(id+"F0.imprint","IMPRINT",EDGE,{"disambiguationData":[TD([[makeQuery(id+"F0.imprint","INTERSECT",VERTEX,{"derivedFrom":[subQ2,subQ1]}),1.0]])],"derivedFrom":subQ2});Q61=makeQuery(id+"F8.opChamfer","BLEND_EDGE",EDGE,{"blendedFrom":[makeQuery(id+"F2.opExtrude","CAP_EDGE",EDGE,{"disambiguationData":[OSD([subQ2]),TDD([subQ3])],"isStart":false}),makeQuery(id+"F2.boolean.opBoolean","SPLIT",FACE,{"disambiguationData":[TD([makeQuery(id+"F2.opExtrude","CAP_FACE",FACE,{"disambiguationData":[OSD([subQ2,subQ1,subQ0,sQuery(id+"F0.wireOp",EDGE,"E20")])],"isStart":false})])],"derivedFrom":makeQuery(id+"F2.opExtrude","SWEPT_FACE",FACE,{"disambiguationData":[OSD([subQ2]),TDD([subQ3])]})})],"blendedInto":[makeQuery(id+"F2.boolean.opBoolean","SPLIT",FACE,{"disambiguationData":[TD([makeQuery(id+"F2.opExtrude","CAP_FACE",FACE,{"disambiguationData":[OSD([subQ2,subQ1,subQ0,sQuery(id+"F0.wireOp",EDGE,"E20")])],"isStart":false})])],"derivedFrom":makeQuery(id+"F2.opExtrude","SWEPT_FACE",FACE,{"disambiguationData":[OSD([subQ2]),TDD([subQ3])]})})]});}
            var Q62;
            {var subQ0=sQuery(id+"F0.wireOp",EDGE,"E19.1.10.0");var subQ1=sQuery(id+"F0.wireOp",EDGE,"E4");var subQ2=sQuery(id+"F0.wireOp",EDGE,"E19.3.10.0");var subQ3=makeQuery(id+"F0.imprint","IMPRINT",EDGE,{"disambiguationData":[TD([[makeQuery(id+"F0.imprint","INTERSECT",VERTEX,{"derivedFrom":[subQ1,subQ0]}),1.0]])],"derivedFrom":subQ1});var subQ4=sQuery(id+"F0.wireOp",EDGE,"E20");Q62=makeQuery(id+"F8.opChamfer","BLEND_EDGE",EDGE,{"blendedFrom":[makeQuery(id+"F2.opExtrude","CAP_EDGE",EDGE,{"disambiguationData":[OSD([subQ1]),TDD([subQ3])],"isStart":false}),makeQuery(id+"F2.boolean.opBoolean","SPLIT",FACE,{"disambiguationData":[TD([makeQuery(id+"F2.opExtrude","CAP_FACE",FACE,{"disambiguationData":[OSD([subQ1,subQ0,subQ2,subQ4])],"isStart":false})])],"derivedFrom":makeQuery(id+"F2.opExtrude","SWEPT_FACE",FACE,{"disambiguationData":[OSD([subQ2])]})})],"blendedInto":[makeQuery(id+"F2.boolean.opBoolean","SPLIT",FACE,{"disambiguationData":[TD([makeQuery(id+"F2.opExtrude","CAP_FACE",FACE,{"disambiguationData":[OSD([subQ1,subQ0,subQ2,subQ4])],"isStart":false})])],"derivedFrom":makeQuery(id+"F2.opExtrude","SWEPT_FACE",FACE,{"disambiguationData":[OSD([subQ2])]})})]});}
            var Q63;
            {var subQ0=sQuery(id+"F0.wireOp",EDGE,"E19.1.10.0");var subQ1=sQuery(id+"F0.wireOp",EDGE,"E4");var subQ2=sQuery(id+"F0.wireOp",EDGE,"E19.3.10.0");var subQ3=sQuery(id+"F0.wireOp",EDGE,"E20");var subQ4=makeQuery(id+"F0.imprint","IMPRINT",EDGE,{"disambiguationData":[TD([[makeQuery(id+"F0.imprint","INTERSECT",VERTEX,{"derivedFrom":[subQ0,subQ3]}),1.0]])],"derivedFrom":subQ3});Q63=makeQuery(id+"F9.opChamfer","BLEND_EDGE",EDGE,{"blendedFrom":[makeQuery(id+"F2.opExtrude","CAP_EDGE",EDGE,{"disambiguationData":[OSD([subQ3]),TDD([subQ4])],"isStart":false}),makeQuery(id+"F2.boolean.opBoolean","SPLIT",FACE,{"disambiguationData":[TD([makeQuery(id+"F2.opExtrude","CAP_FACE",FACE,{"disambiguationData":[OSD([subQ1,subQ0,subQ2,subQ3])],"isStart":false})])],"derivedFrom":makeQuery(id+"F2.opExtrude","SWEPT_FACE",FACE,{"disambiguationData":[OSD([subQ2])]})})],"blendedInto":[makeQuery(id+"F2.boolean.opBoolean","SPLIT",FACE,{"disambiguationData":[TD([makeQuery(id+"F2.opExtrude","CAP_FACE",FACE,{"disambiguationData":[OSD([subQ1,subQ0,subQ2,subQ3])],"isStart":false})])],"derivedFrom":makeQuery(id+"F2.opExtrude","SWEPT_FACE",FACE,{"disambiguationData":[OSD([subQ2])]})})]});}
            var Q64;
            {var subQ0=sQuery(id+"F0.wireOp",EDGE,"E19.1.10.0");var subQ1=sQuery(id+"F0.wireOp",EDGE,"E4");var subQ2=sQuery(id+"F0.wireOp",EDGE,"E19.3.10.0");var subQ3=sQuery(id+"F0.wireOp",EDGE,"E20");var subQ4=makeQuery(id+"F0.imprint","IMPRINT",EDGE,{"disambiguationData":[TD([[makeQuery(id+"F0.imprint","INTERSECT",VERTEX,{"derivedFrom":[subQ0,subQ3]}),1.0]])],"derivedFrom":subQ3});Q64=makeQuery(id+"F9.opChamfer","BLEND_EDGE",EDGE,{"blendedFrom":[makeQuery(id+"F2.opExtrude","CAP_EDGE",EDGE,{"disambiguationData":[OSD([subQ3]),TDD([subQ4])],"isStart":false}),makeQuery(id+"F2.boolean.opBoolean","SPLIT",FACE,{"disambiguationData":[TD([makeQuery(id+"F2.opExtrude","CAP_FACE",FACE,{"disambiguationData":[OSD([subQ1,subQ0,subQ2,subQ3])],"isStart":false})])],"derivedFrom":makeQuery(id+"F2.opExtrude","SWEPT_FACE",FACE,{"disambiguationData":[OSD([subQ0])]})})],"blendedInto":[makeQuery(id+"F2.boolean.opBoolean","SPLIT",FACE,{"disambiguationData":[TD([makeQuery(id+"F2.opExtrude","CAP_FACE",FACE,{"disambiguationData":[OSD([subQ1,subQ0,subQ2,subQ3])],"isStart":false})])],"derivedFrom":makeQuery(id+"F2.opExtrude","SWEPT_FACE",FACE,{"disambiguationData":[OSD([subQ0])]})})]});}
            var Q65;
            {var subQ0=sQuery(id+"F0.wireOp",EDGE,"E20");var subQ1=sQuery(id+"F0.wireOp",EDGE,"E19.3.10.0");var subQ2=sQuery(id+"F0.wireOp",EDGE,"E19.1.10.0");var subQ3=makeQuery(id+"F0.imprint","IMPRINT",EDGE,{"disambiguationData":[TD([[makeQuery(id+"F0.imprint","INTERSECT",VERTEX,{"derivedFrom":[subQ2,subQ0]}),1.0]])],"derivedFrom":subQ0});Q65=makeQuery(id+"F9.opChamfer","BLEND_EDGE",EDGE,{"blendedFrom":[makeQuery(id+"F2.opExtrude","CAP_EDGE",EDGE,{"disambiguationData":[OSD([subQ0]),TDD([subQ3])],"isStart":false}),makeQuery(id+"F2.boolean.opBoolean","SPLIT",FACE,{"disambiguationData":[TD([makeQuery(id+"F2.opExtrude","CAP_FACE",FACE,{"disambiguationData":[OSD([sQuery(id+"F0.wireOp",EDGE,"E4"),subQ2,subQ1,subQ0])],"isStart":false})])],"derivedFrom":makeQuery(id+"F2.opExtrude","SWEPT_FACE",FACE,{"disambiguationData":[OSD([subQ0]),TDD([subQ3])]})})],"blendedInto":[makeQuery(id+"F2.boolean.opBoolean","SPLIT",FACE,{"disambiguationData":[TD([makeQuery(id+"F2.opExtrude","CAP_FACE",FACE,{"disambiguationData":[OSD([sQuery(id+"F0.wireOp",EDGE,"E4"),subQ2,subQ1,subQ0])],"isStart":false})])],"derivedFrom":makeQuery(id+"F2.opExtrude","SWEPT_FACE",FACE,{"disambiguationData":[OSD([subQ0]),TDD([subQ3])]})})]});}
            var Q66;
            {var subQ0=sQuery(id+"F0.wireOp",EDGE,"E19.1.11.0");var subQ1=sQuery(id+"F0.wireOp",EDGE,"E20");var subQ2=sQuery(id+"F0.wireOp",EDGE,"E19.3.11.0");var subQ3=makeQuery(id+"F0.imprint","IMPRINT",EDGE,{"disambiguationData":[TD([[makeQuery(id+"F0.imprint","INTERSECT",VERTEX,{"derivedFrom":[subQ0,subQ1]}),1.0]])],"derivedFrom":subQ1});Q66=makeQuery(id+"F9.opChamfer","BLEND_EDGE",EDGE,{"blendedFrom":[makeQuery(id+"F2.opExtrude","CAP_EDGE",EDGE,{"disambiguationData":[OSD([subQ1]),TDD([subQ3])],"isStart":false}),makeQuery(id+"F2.boolean.opBoolean","SPLIT",FACE,{"disambiguationData":[TD([makeQuery(id+"F2.opExtrude","CAP_FACE",FACE,{"disambiguationData":[OSD([sQuery(id+"F0.wireOp",EDGE,"E4"),subQ0,subQ2,subQ1])],"isStart":false})])],"derivedFrom":makeQuery(id+"F2.opExtrude","SWEPT_FACE",FACE,{"disambiguationData":[OSD([subQ1]),TDD([subQ3])]})})],"blendedInto":[makeQuery(id+"F2.boolean.opBoolean","SPLIT",FACE,{"disambiguationData":[TD([makeQuery(id+"F2.opExtrude","CAP_FACE",FACE,{"disambiguationData":[OSD([sQuery(id+"F0.wireOp",EDGE,"E4"),subQ0,subQ2,subQ1])],"isStart":false})])],"derivedFrom":makeQuery(id+"F2.opExtrude","SWEPT_FACE",FACE,{"disambiguationData":[OSD([subQ1]),TDD([subQ3])]})})]});}
            var Q67;
            {var subQ0=sQuery(id+"F0.wireOp",EDGE,"E20");var subQ1=sQuery(id+"F0.wireOp",EDGE,"E19.1.11.0");var subQ2=sQuery(id+"F0.wireOp",EDGE,"E19.3.11.0");var subQ3=makeQuery(id+"F0.imprint","IMPRINT",EDGE,{"disambiguationData":[TD([[makeQuery(id+"F0.imprint","INTERSECT",VERTEX,{"derivedFrom":[subQ1,subQ0]}),1.0]])],"derivedFrom":subQ0});var subQ4=sQuery(id+"F0.wireOp",EDGE,"E4");Q67=makeQuery(id+"F9.opChamfer","BLEND_EDGE",EDGE,{"blendedFrom":[makeQuery(id+"F2.opExtrude","CAP_EDGE",EDGE,{"disambiguationData":[OSD([subQ0]),TDD([subQ3])],"isStart":false}),makeQuery(id+"F2.boolean.opBoolean","SPLIT",FACE,{"disambiguationData":[TD([makeQuery(id+"F2.opExtrude","CAP_FACE",FACE,{"disambiguationData":[OSD([subQ4,subQ1,subQ2,subQ0])],"isStart":false})])],"derivedFrom":makeQuery(id+"F2.opExtrude","SWEPT_FACE",FACE,{"disambiguationData":[OSD([subQ1])]})})],"blendedInto":[makeQuery(id+"F2.boolean.opBoolean","SPLIT",FACE,{"disambiguationData":[TD([makeQuery(id+"F2.opExtrude","CAP_FACE",FACE,{"disambiguationData":[OSD([subQ4,subQ1,subQ2,subQ0])],"isStart":false})])],"derivedFrom":makeQuery(id+"F2.opExtrude","SWEPT_FACE",FACE,{"disambiguationData":[OSD([subQ1])]})})]});}
            var Q68;
            {var subQ0=sQuery(id+"F0.wireOp",EDGE,"E20");var subQ1=sQuery(id+"F0.wireOp",EDGE,"E19.1.11.0");var subQ2=sQuery(id+"F0.wireOp",EDGE,"E19.3.11.0");var subQ3=makeQuery(id+"F0.imprint","IMPRINT",EDGE,{"disambiguationData":[TD([[makeQuery(id+"F0.imprint","INTERSECT",VERTEX,{"derivedFrom":[subQ1,subQ0]}),1.0]])],"derivedFrom":subQ0});var subQ4=sQuery(id+"F0.wireOp",EDGE,"E4");Q68=makeQuery(id+"F9.opChamfer","BLEND_EDGE",EDGE,{"blendedFrom":[makeQuery(id+"F2.opExtrude","CAP_EDGE",EDGE,{"disambiguationData":[OSD([subQ0]),TDD([subQ3])],"isStart":false}),makeQuery(id+"F2.boolean.opBoolean","SPLIT",FACE,{"disambiguationData":[TD([makeQuery(id+"F2.opExtrude","CAP_FACE",FACE,{"disambiguationData":[OSD([subQ4,subQ1,subQ2,subQ0])],"isStart":false})])],"derivedFrom":makeQuery(id+"F2.opExtrude","SWEPT_FACE",FACE,{"disambiguationData":[OSD([subQ2])]})})],"blendedInto":[makeQuery(id+"F2.boolean.opBoolean","SPLIT",FACE,{"disambiguationData":[TD([makeQuery(id+"F2.opExtrude","CAP_FACE",FACE,{"disambiguationData":[OSD([subQ4,subQ1,subQ2,subQ0])],"isStart":false})])],"derivedFrom":makeQuery(id+"F2.opExtrude","SWEPT_FACE",FACE,{"disambiguationData":[OSD([subQ2])]})})]});}
            var Q69;
            {var subQ0=sQuery(id+"F0.wireOp",EDGE,"E20");var subQ1=sQuery(id+"F0.wireOp",EDGE,"E19.1.11.0");var subQ2=sQuery(id+"F0.wireOp",EDGE,"E19.3.11.0");var subQ3=sQuery(id+"F0.wireOp",EDGE,"E4");var subQ4=makeQuery(id+"F0.imprint","IMPRINT",EDGE,{"disambiguationData":[TD([[makeQuery(id+"F0.imprint","INTERSECT",VERTEX,{"derivedFrom":[subQ3,subQ1]}),1.0]])],"derivedFrom":subQ3});Q69=makeQuery(id+"F8.opChamfer","BLEND_EDGE",EDGE,{"blendedFrom":[makeQuery(id+"F2.opExtrude","CAP_EDGE",EDGE,{"disambiguationData":[OSD([subQ3]),TDD([subQ4])],"isStart":false}),makeQuery(id+"F2.boolean.opBoolean","SPLIT",FACE,{"disambiguationData":[TD([makeQuery(id+"F2.opExtrude","CAP_FACE",FACE,{"disambiguationData":[OSD([subQ3,subQ1,subQ2,subQ0])],"isStart":false})])],"derivedFrom":makeQuery(id+"F2.opExtrude","SWEPT_FACE",FACE,{"disambiguationData":[OSD([subQ2])]})})],"blendedInto":[makeQuery(id+"F2.boolean.opBoolean","SPLIT",FACE,{"disambiguationData":[TD([makeQuery(id+"F2.opExtrude","CAP_FACE",FACE,{"disambiguationData":[OSD([subQ3,subQ1,subQ2,subQ0])],"isStart":false})])],"derivedFrom":makeQuery(id+"F2.opExtrude","SWEPT_FACE",FACE,{"disambiguationData":[OSD([subQ2])]})})]});}
            var Q70;
            {var subQ0=sQuery(id+"F0.wireOp",EDGE,"E20");var subQ1=sQuery(id+"F0.wireOp",EDGE,"E19.1.11.0");var subQ2=sQuery(id+"F0.wireOp",EDGE,"E19.3.11.0");var subQ3=sQuery(id+"F0.wireOp",EDGE,"E4");var subQ4=makeQuery(id+"F0.imprint","IMPRINT",EDGE,{"disambiguationData":[TD([[makeQuery(id+"F0.imprint","INTERSECT",VERTEX,{"derivedFrom":[subQ3,subQ1]}),1.0]])],"derivedFrom":subQ3});Q70=makeQuery(id+"F8.opChamfer","BLEND_EDGE",EDGE,{"blendedFrom":[makeQuery(id+"F2.opExtrude","CAP_EDGE",EDGE,{"disambiguationData":[OSD([subQ3]),TDD([subQ4])],"isStart":false}),makeQuery(id+"F2.boolean.opBoolean","SPLIT",FACE,{"disambiguationData":[TD([makeQuery(id+"F2.opExtrude","CAP_FACE",FACE,{"disambiguationData":[OSD([subQ3,subQ1,subQ2,subQ0])],"isStart":false})])],"derivedFrom":makeQuery(id+"F2.opExtrude","SWEPT_FACE",FACE,{"disambiguationData":[OSD([subQ1])]})})],"blendedInto":[makeQuery(id+"F2.boolean.opBoolean","SPLIT",FACE,{"disambiguationData":[TD([makeQuery(id+"F2.opExtrude","CAP_FACE",FACE,{"disambiguationData":[OSD([subQ3,subQ1,subQ2,subQ0])],"isStart":false})])],"derivedFrom":makeQuery(id+"F2.opExtrude","SWEPT_FACE",FACE,{"disambiguationData":[OSD([subQ1])]})})]});}
            var Q71;
            {var subQ0=sQuery(id+"F0.wireOp",EDGE,"E19.1.11.0");var subQ1=sQuery(id+"F0.wireOp",EDGE,"E19.3.11.0");var subQ2=sQuery(id+"F0.wireOp",EDGE,"E4");var subQ3=makeQuery(id+"F0.imprint","IMPRINT",EDGE,{"disambiguationData":[TD([[makeQuery(id+"F0.imprint","INTERSECT",VERTEX,{"derivedFrom":[subQ2,subQ0]}),1.0]])],"derivedFrom":subQ2});Q71=makeQuery(id+"F8.opChamfer","BLEND_EDGE",EDGE,{"blendedFrom":[makeQuery(id+"F2.opExtrude","CAP_EDGE",EDGE,{"disambiguationData":[OSD([subQ2]),TDD([subQ3])],"isStart":false}),makeQuery(id+"F2.boolean.opBoolean","SPLIT",FACE,{"disambiguationData":[TD([makeQuery(id+"F2.opExtrude","CAP_FACE",FACE,{"disambiguationData":[OSD([subQ2,subQ0,subQ1,sQuery(id+"F0.wireOp",EDGE,"E20")])],"isStart":false})])],"derivedFrom":makeQuery(id+"F2.opExtrude","SWEPT_FACE",FACE,{"disambiguationData":[OSD([subQ2]),TDD([subQ3])]})})],"blendedInto":[makeQuery(id+"F2.boolean.opBoolean","SPLIT",FACE,{"disambiguationData":[TD([makeQuery(id+"F2.opExtrude","CAP_FACE",FACE,{"disambiguationData":[OSD([subQ2,subQ0,subQ1,sQuery(id+"F0.wireOp",EDGE,"E20")])],"isStart":false})])],"derivedFrom":makeQuery(id+"F2.opExtrude","SWEPT_FACE",FACE,{"disambiguationData":[OSD([subQ2]),TDD([subQ3])]})})]});}
            var Q72;
            {var subQ0=sQuery(id+"F0.wireOp",EDGE,"E19.3.12.0");var subQ1=sQuery(id+"F0.wireOp",EDGE,"E19.1.12.0");var subQ2=sQuery(id+"F0.wireOp",EDGE,"E4");var subQ3=makeQuery(id+"F0.imprint","IMPRINT",EDGE,{"disambiguationData":[TD([[makeQuery(id+"F0.imprint","INTERSECT",VERTEX,{"derivedFrom":[subQ2,subQ1]}),1.0]])],"derivedFrom":subQ2});Q72=makeQuery(id+"F8.opChamfer","BLEND_EDGE",EDGE,{"blendedFrom":[makeQuery(id+"F2.opExtrude","CAP_EDGE",EDGE,{"disambiguationData":[OSD([subQ2]),TDD([subQ3])],"isStart":false}),makeQuery(id+"F2.boolean.opBoolean","SPLIT",FACE,{"disambiguationData":[TD([makeQuery(id+"F2.opExtrude","CAP_FACE",FACE,{"disambiguationData":[OSD([subQ2,subQ1,subQ0,sQuery(id+"F0.wireOp",EDGE,"E20")])],"isStart":false})])],"derivedFrom":makeQuery(id+"F2.opExtrude","SWEPT_FACE",FACE,{"disambiguationData":[OSD([subQ2]),TDD([subQ3])]})})],"blendedInto":[makeQuery(id+"F2.boolean.opBoolean","SPLIT",FACE,{"disambiguationData":[TD([makeQuery(id+"F2.opExtrude","CAP_FACE",FACE,{"disambiguationData":[OSD([subQ2,subQ1,subQ0,sQuery(id+"F0.wireOp",EDGE,"E20")])],"isStart":false})])],"derivedFrom":makeQuery(id+"F2.opExtrude","SWEPT_FACE",FACE,{"disambiguationData":[OSD([subQ2]),TDD([subQ3])]})})]});}
            var Q73;
            {var subQ0=sQuery(id+"F0.wireOp",EDGE,"E19.1.12.0");var subQ1=sQuery(id+"F0.wireOp",EDGE,"E4");var subQ2=sQuery(id+"F0.wireOp",EDGE,"E19.3.12.0");var subQ3=makeQuery(id+"F0.imprint","IMPRINT",EDGE,{"disambiguationData":[TD([[makeQuery(id+"F0.imprint","INTERSECT",VERTEX,{"derivedFrom":[subQ1,subQ0]}),1.0]])],"derivedFrom":subQ1});var subQ4=sQuery(id+"F0.wireOp",EDGE,"E20");Q73=makeQuery(id+"F8.opChamfer","BLEND_EDGE",EDGE,{"blendedFrom":[makeQuery(id+"F2.opExtrude","CAP_EDGE",EDGE,{"disambiguationData":[OSD([subQ1]),TDD([subQ3])],"isStart":false}),makeQuery(id+"F2.boolean.opBoolean","SPLIT",FACE,{"disambiguationData":[TD([makeQuery(id+"F2.opExtrude","CAP_FACE",FACE,{"disambiguationData":[OSD([subQ1,subQ0,subQ2,subQ4])],"isStart":false})])],"derivedFrom":makeQuery(id+"F2.opExtrude","SWEPT_FACE",FACE,{"disambiguationData":[OSD([subQ0])]})})],"blendedInto":[makeQuery(id+"F2.boolean.opBoolean","SPLIT",FACE,{"disambiguationData":[TD([makeQuery(id+"F2.opExtrude","CAP_FACE",FACE,{"disambiguationData":[OSD([subQ1,subQ0,subQ2,subQ4])],"isStart":false})])],"derivedFrom":makeQuery(id+"F2.opExtrude","SWEPT_FACE",FACE,{"disambiguationData":[OSD([subQ0])]})})]});}
            var Q74;
            {var subQ0=sQuery(id+"F0.wireOp",EDGE,"E19.1.12.0");var subQ1=sQuery(id+"F0.wireOp",EDGE,"E4");var subQ2=sQuery(id+"F0.wireOp",EDGE,"E19.3.12.0");var subQ3=makeQuery(id+"F0.imprint","IMPRINT",EDGE,{"disambiguationData":[TD([[makeQuery(id+"F0.imprint","INTERSECT",VERTEX,{"derivedFrom":[subQ1,subQ0]}),1.0]])],"derivedFrom":subQ1});var subQ4=sQuery(id+"F0.wireOp",EDGE,"E20");Q74=makeQuery(id+"F8.opChamfer","BLEND_EDGE",EDGE,{"blendedFrom":[makeQuery(id+"F2.opExtrude","CAP_EDGE",EDGE,{"disambiguationData":[OSD([subQ1]),TDD([subQ3])],"isStart":false}),makeQuery(id+"F2.boolean.opBoolean","SPLIT",FACE,{"disambiguationData":[TD([makeQuery(id+"F2.opExtrude","CAP_FACE",FACE,{"disambiguationData":[OSD([subQ1,subQ0,subQ2,subQ4])],"isStart":false})])],"derivedFrom":makeQuery(id+"F2.opExtrude","SWEPT_FACE",FACE,{"disambiguationData":[OSD([subQ2])]})})],"blendedInto":[makeQuery(id+"F2.boolean.opBoolean","SPLIT",FACE,{"disambiguationData":[TD([makeQuery(id+"F2.opExtrude","CAP_FACE",FACE,{"disambiguationData":[OSD([subQ1,subQ0,subQ2,subQ4])],"isStart":false})])],"derivedFrom":makeQuery(id+"F2.opExtrude","SWEPT_FACE",FACE,{"disambiguationData":[OSD([subQ2])]})})]});}
            var Q75;
            {var subQ0=sQuery(id+"F0.wireOp",EDGE,"E19.1.12.0");var subQ1=sQuery(id+"F0.wireOp",EDGE,"E4");var subQ2=sQuery(id+"F0.wireOp",EDGE,"E19.3.12.0");var subQ3=sQuery(id+"F0.wireOp",EDGE,"E20");var subQ4=makeQuery(id+"F0.imprint","IMPRINT",EDGE,{"disambiguationData":[TD([[makeQuery(id+"F0.imprint","INTERSECT",VERTEX,{"derivedFrom":[subQ0,subQ3]}),1.0]])],"derivedFrom":subQ3});Q75=makeQuery(id+"F9.opChamfer","BLEND_EDGE",EDGE,{"blendedFrom":[makeQuery(id+"F2.opExtrude","CAP_EDGE",EDGE,{"disambiguationData":[OSD([subQ3]),TDD([subQ4])],"isStart":false}),makeQuery(id+"F2.boolean.opBoolean","SPLIT",FACE,{"disambiguationData":[TD([makeQuery(id+"F2.opExtrude","CAP_FACE",FACE,{"disambiguationData":[OSD([subQ1,subQ0,subQ2,subQ3])],"isStart":false})])],"derivedFrom":makeQuery(id+"F2.opExtrude","SWEPT_FACE",FACE,{"disambiguationData":[OSD([subQ0])]})})],"blendedInto":[makeQuery(id+"F2.boolean.opBoolean","SPLIT",FACE,{"disambiguationData":[TD([makeQuery(id+"F2.opExtrude","CAP_FACE",FACE,{"disambiguationData":[OSD([subQ1,subQ0,subQ2,subQ3])],"isStart":false})])],"derivedFrom":makeQuery(id+"F2.opExtrude","SWEPT_FACE",FACE,{"disambiguationData":[OSD([subQ0])]})})]});}
            var Q76;
            {var subQ0=sQuery(id+"F0.wireOp",EDGE,"E19.1.12.0");var subQ1=sQuery(id+"F0.wireOp",EDGE,"E4");var subQ2=sQuery(id+"F0.wireOp",EDGE,"E19.3.12.0");var subQ3=sQuery(id+"F0.wireOp",EDGE,"E20");var subQ4=makeQuery(id+"F0.imprint","IMPRINT",EDGE,{"disambiguationData":[TD([[makeQuery(id+"F0.imprint","INTERSECT",VERTEX,{"derivedFrom":[subQ0,subQ3]}),1.0]])],"derivedFrom":subQ3});Q76=makeQuery(id+"F9.opChamfer","BLEND_EDGE",EDGE,{"blendedFrom":[makeQuery(id+"F2.opExtrude","CAP_EDGE",EDGE,{"disambiguationData":[OSD([subQ3]),TDD([subQ4])],"isStart":false}),makeQuery(id+"F2.boolean.opBoolean","SPLIT",FACE,{"disambiguationData":[TD([makeQuery(id+"F2.opExtrude","CAP_FACE",FACE,{"disambiguationData":[OSD([subQ1,subQ0,subQ2,subQ3])],"isStart":false})])],"derivedFrom":makeQuery(id+"F2.opExtrude","SWEPT_FACE",FACE,{"disambiguationData":[OSD([subQ2])]})})],"blendedInto":[makeQuery(id+"F2.boolean.opBoolean","SPLIT",FACE,{"disambiguationData":[TD([makeQuery(id+"F2.opExtrude","CAP_FACE",FACE,{"disambiguationData":[OSD([subQ1,subQ0,subQ2,subQ3])],"isStart":false})])],"derivedFrom":makeQuery(id+"F2.opExtrude","SWEPT_FACE",FACE,{"disambiguationData":[OSD([subQ2])]})})]});}
            var Q77;
            {var subQ0=sQuery(id+"F0.wireOp",EDGE,"E20");var subQ1=sQuery(id+"F0.wireOp",EDGE,"E19.3.12.0");var subQ2=sQuery(id+"F0.wireOp",EDGE,"E19.1.12.0");var subQ3=makeQuery(id+"F0.imprint","IMPRINT",EDGE,{"disambiguationData":[TD([[makeQuery(id+"F0.imprint","INTERSECT",VERTEX,{"derivedFrom":[subQ2,subQ0]}),1.0]])],"derivedFrom":subQ0});Q77=makeQuery(id+"F9.opChamfer","BLEND_EDGE",EDGE,{"blendedFrom":[makeQuery(id+"F2.opExtrude","CAP_EDGE",EDGE,{"disambiguationData":[OSD([subQ0]),TDD([subQ3])],"isStart":false}),makeQuery(id+"F2.boolean.opBoolean","SPLIT",FACE,{"disambiguationData":[TD([makeQuery(id+"F2.opExtrude","CAP_FACE",FACE,{"disambiguationData":[OSD([sQuery(id+"F0.wireOp",EDGE,"E4"),subQ2,subQ1,subQ0])],"isStart":false})])],"derivedFrom":makeQuery(id+"F2.opExtrude","SWEPT_FACE",FACE,{"disambiguationData":[OSD([subQ0]),TDD([subQ3])]})})],"blendedInto":[makeQuery(id+"F2.boolean.opBoolean","SPLIT",FACE,{"disambiguationData":[TD([makeQuery(id+"F2.opExtrude","CAP_FACE",FACE,{"disambiguationData":[OSD([sQuery(id+"F0.wireOp",EDGE,"E4"),subQ2,subQ1,subQ0])],"isStart":false})])],"derivedFrom":makeQuery(id+"F2.opExtrude","SWEPT_FACE",FACE,{"disambiguationData":[OSD([subQ0]),TDD([subQ3])]})})]});}
            var Q78;
            {var subQ0=sQuery(id+"F0.wireOp",EDGE,"E20");var subQ1=sQuery(id+"F0.wireOp",EDGE,"E19.3.12.0");var subQ2=sQuery(id+"F0.wireOp",EDGE,"E19.1.12.0");var subQ3=makeQuery(id+"F0.imprint","IMPRINT",EDGE,{"disambiguationData":[TD([[makeQuery(id+"F0.imprint","INTERSECT",VERTEX,{"derivedFrom":[subQ2,subQ0]}),1.0]])],"derivedFrom":subQ0});Q78=makeQuery(id+"F8.opChamfer","BLEND_EDGE",EDGE,{"blendedFrom":[makeQuery(id+"F2.opExtrude","CAP_EDGE",EDGE,{"disambiguationData":[OSD([subQ0]),TDD([subQ3])],"isStart":true}),makeQuery(id+"F2.boolean.opBoolean","SPLIT",FACE,{"disambiguationData":[TD([makeQuery(id+"F2.opExtrude","CAP_FACE",FACE,{"disambiguationData":[OSD([sQuery(id+"F0.wireOp",EDGE,"E4"),subQ2,subQ1,subQ0])],"isStart":true})])],"derivedFrom":makeQuery(id+"F2.opExtrude","SWEPT_FACE",FACE,{"disambiguationData":[OSD([subQ0]),TDD([subQ3])]})})],"blendedInto":[makeQuery(id+"F2.boolean.opBoolean","SPLIT",FACE,{"disambiguationData":[TD([makeQuery(id+"F2.opExtrude","CAP_FACE",FACE,{"disambiguationData":[OSD([sQuery(id+"F0.wireOp",EDGE,"E4"),subQ2,subQ1,subQ0])],"isStart":true})])],"derivedFrom":makeQuery(id+"F2.opExtrude","SWEPT_FACE",FACE,{"disambiguationData":[OSD([subQ0]),TDD([subQ3])]})})]});}
            var Q79;
            {var subQ0=sQuery(id+"F0.wireOp",EDGE,"E19.3.12.0");var subQ1=sQuery(id+"F0.wireOp",EDGE,"E19.1.12.0");var subQ2=sQuery(id+"F0.wireOp",EDGE,"E4");var subQ3=makeQuery(id+"F0.imprint","IMPRINT",EDGE,{"disambiguationData":[TD([[makeQuery(id+"F0.imprint","INTERSECT",VERTEX,{"derivedFrom":[subQ2,subQ1]}),1.0]])],"derivedFrom":subQ2});Q79=makeQuery(id+"F9.opChamfer","BLEND_EDGE",EDGE,{"blendedFrom":[makeQuery(id+"F2.opExtrude","CAP_EDGE",EDGE,{"disambiguationData":[OSD([subQ2]),TDD([subQ3])],"isStart":true}),makeQuery(id+"F2.boolean.opBoolean","SPLIT",FACE,{"disambiguationData":[TD([makeQuery(id+"F2.opExtrude","CAP_FACE",FACE,{"disambiguationData":[OSD([subQ2,subQ1,subQ0,sQuery(id+"F0.wireOp",EDGE,"E20")])],"isStart":true})])],"derivedFrom":makeQuery(id+"F2.opExtrude","SWEPT_FACE",FACE,{"disambiguationData":[OSD([subQ2]),TDD([subQ3])]})})],"blendedInto":[makeQuery(id+"F2.boolean.opBoolean","SPLIT",FACE,{"disambiguationData":[TD([makeQuery(id+"F2.opExtrude","CAP_FACE",FACE,{"disambiguationData":[OSD([subQ2,subQ1,subQ0,sQuery(id+"F0.wireOp",EDGE,"E20")])],"isStart":true})])],"derivedFrom":makeQuery(id+"F2.opExtrude","SWEPT_FACE",FACE,{"disambiguationData":[OSD([subQ2]),TDD([subQ3])]})})]});}
            var Q80;
            {var subQ0=sQuery(id+"F0.wireOp",EDGE,"E19.1.12.0");var subQ1=sQuery(id+"F0.wireOp",EDGE,"E4");var subQ2=sQuery(id+"F0.wireOp",EDGE,"E19.3.12.0");var subQ3=makeQuery(id+"F0.imprint","IMPRINT",EDGE,{"disambiguationData":[TD([[makeQuery(id+"F0.imprint","INTERSECT",VERTEX,{"derivedFrom":[subQ1,subQ0]}),1.0]])],"derivedFrom":subQ1});var subQ4=sQuery(id+"F0.wireOp",EDGE,"E20");Q80=makeQuery(id+"F9.opChamfer","BLEND_EDGE",EDGE,{"blendedFrom":[makeQuery(id+"F2.opExtrude","CAP_EDGE",EDGE,{"disambiguationData":[OSD([subQ1]),TDD([subQ3])],"isStart":true}),makeQuery(id+"F2.boolean.opBoolean","SPLIT",FACE,{"disambiguationData":[TD([makeQuery(id+"F2.opExtrude","CAP_FACE",FACE,{"disambiguationData":[OSD([subQ1,subQ0,subQ2,subQ4])],"isStart":true})])],"derivedFrom":makeQuery(id+"F2.opExtrude","SWEPT_FACE",FACE,{"disambiguationData":[OSD([subQ0])]})})],"blendedInto":[makeQuery(id+"F2.boolean.opBoolean","SPLIT",FACE,{"disambiguationData":[TD([makeQuery(id+"F2.opExtrude","CAP_FACE",FACE,{"disambiguationData":[OSD([subQ1,subQ0,subQ2,subQ4])],"isStart":true})])],"derivedFrom":makeQuery(id+"F2.opExtrude","SWEPT_FACE",FACE,{"disambiguationData":[OSD([subQ0])]})})]});}
            var Q81;
            {var subQ0=sQuery(id+"F0.wireOp",EDGE,"E19.1.12.0");var subQ1=sQuery(id+"F0.wireOp",EDGE,"E4");var subQ2=sQuery(id+"F0.wireOp",EDGE,"E19.3.12.0");var subQ3=makeQuery(id+"F0.imprint","IMPRINT",EDGE,{"disambiguationData":[TD([[makeQuery(id+"F0.imprint","INTERSECT",VERTEX,{"derivedFrom":[subQ1,subQ0]}),1.0]])],"derivedFrom":subQ1});var subQ4=sQuery(id+"F0.wireOp",EDGE,"E20");Q81=makeQuery(id+"F9.opChamfer","BLEND_EDGE",EDGE,{"blendedFrom":[makeQuery(id+"F2.opExtrude","CAP_EDGE",EDGE,{"disambiguationData":[OSD([subQ1]),TDD([subQ3])],"isStart":true}),makeQuery(id+"F2.boolean.opBoolean","SPLIT",FACE,{"disambiguationData":[TD([makeQuery(id+"F2.opExtrude","CAP_FACE",FACE,{"disambiguationData":[OSD([subQ1,subQ0,subQ2,subQ4])],"isStart":true})])],"derivedFrom":makeQuery(id+"F2.opExtrude","SWEPT_FACE",FACE,{"disambiguationData":[OSD([subQ2])]})})],"blendedInto":[makeQuery(id+"F2.boolean.opBoolean","SPLIT",FACE,{"disambiguationData":[TD([makeQuery(id+"F2.opExtrude","CAP_FACE",FACE,{"disambiguationData":[OSD([subQ1,subQ0,subQ2,subQ4])],"isStart":true})])],"derivedFrom":makeQuery(id+"F2.opExtrude","SWEPT_FACE",FACE,{"disambiguationData":[OSD([subQ2])]})})]});}
            var Q82;
            {var subQ0=sQuery(id+"F0.wireOp",EDGE,"E19.1.12.0");var subQ1=sQuery(id+"F0.wireOp",EDGE,"E4");var subQ2=sQuery(id+"F0.wireOp",EDGE,"E19.3.12.0");var subQ3=sQuery(id+"F0.wireOp",EDGE,"E20");var subQ4=makeQuery(id+"F0.imprint","IMPRINT",EDGE,{"disambiguationData":[TD([[makeQuery(id+"F0.imprint","INTERSECT",VERTEX,{"derivedFrom":[subQ0,subQ3]}),1.0]])],"derivedFrom":subQ3});Q82=makeQuery(id+"F8.opChamfer","BLEND_EDGE",EDGE,{"blendedFrom":[makeQuery(id+"F2.opExtrude","CAP_EDGE",EDGE,{"disambiguationData":[OSD([subQ3]),TDD([subQ4])],"isStart":true}),makeQuery(id+"F2.boolean.opBoolean","SPLIT",FACE,{"disambiguationData":[TD([makeQuery(id+"F2.opExtrude","CAP_FACE",FACE,{"disambiguationData":[OSD([subQ1,subQ0,subQ2,subQ3])],"isStart":true})])],"derivedFrom":makeQuery(id+"F2.opExtrude","SWEPT_FACE",FACE,{"disambiguationData":[OSD([subQ2])]})})],"blendedInto":[makeQuery(id+"F2.boolean.opBoolean","SPLIT",FACE,{"disambiguationData":[TD([makeQuery(id+"F2.opExtrude","CAP_FACE",FACE,{"disambiguationData":[OSD([subQ1,subQ0,subQ2,subQ3])],"isStart":true})])],"derivedFrom":makeQuery(id+"F2.opExtrude","SWEPT_FACE",FACE,{"disambiguationData":[OSD([subQ2])]})})]});}
            var Q83;
            {var subQ0=sQuery(id+"F0.wireOp",EDGE,"E19.1.12.0");var subQ1=sQuery(id+"F0.wireOp",EDGE,"E4");var subQ2=sQuery(id+"F0.wireOp",EDGE,"E19.3.12.0");var subQ3=sQuery(id+"F0.wireOp",EDGE,"E20");var subQ4=makeQuery(id+"F0.imprint","IMPRINT",EDGE,{"disambiguationData":[TD([[makeQuery(id+"F0.imprint","INTERSECT",VERTEX,{"derivedFrom":[subQ0,subQ3]}),1.0]])],"derivedFrom":subQ3});Q83=makeQuery(id+"F8.opChamfer","BLEND_EDGE",EDGE,{"blendedFrom":[makeQuery(id+"F2.opExtrude","CAP_EDGE",EDGE,{"disambiguationData":[OSD([subQ3]),TDD([subQ4])],"isStart":true}),makeQuery(id+"F2.boolean.opBoolean","SPLIT",FACE,{"disambiguationData":[TD([makeQuery(id+"F2.opExtrude","CAP_FACE",FACE,{"disambiguationData":[OSD([subQ1,subQ0,subQ2,subQ3])],"isStart":true})])],"derivedFrom":makeQuery(id+"F2.opExtrude","SWEPT_FACE",FACE,{"disambiguationData":[OSD([subQ0])]})})],"blendedInto":[makeQuery(id+"F2.boolean.opBoolean","SPLIT",FACE,{"disambiguationData":[TD([makeQuery(id+"F2.opExtrude","CAP_FACE",FACE,{"disambiguationData":[OSD([subQ1,subQ0,subQ2,subQ3])],"isStart":true})])],"derivedFrom":makeQuery(id+"F2.opExtrude","SWEPT_FACE",FACE,{"disambiguationData":[OSD([subQ0])]})})]});}
            var Q84;
            {var subQ0=sQuery(id+"F0.wireOp",EDGE,"E20");var subQ1=sQuery(id+"F0.wireOp",EDGE,"E19.3.11.0");var subQ2=sQuery(id+"F0.wireOp",EDGE,"E19.1.11.0");var subQ3=makeQuery(id+"F0.imprint","IMPRINT",EDGE,{"disambiguationData":[TD([[makeQuery(id+"F0.imprint","INTERSECT",VERTEX,{"derivedFrom":[subQ2,subQ0]}),1.0]])],"derivedFrom":subQ0});Q84=makeQuery(id+"F8.opChamfer","BLEND_EDGE",EDGE,{"blendedFrom":[makeQuery(id+"F2.opExtrude","CAP_EDGE",EDGE,{"disambiguationData":[OSD([subQ0]),TDD([subQ3])],"isStart":true}),makeQuery(id+"F2.boolean.opBoolean","SPLIT",FACE,{"disambiguationData":[TD([makeQuery(id+"F2.opExtrude","CAP_FACE",FACE,{"disambiguationData":[OSD([sQuery(id+"F0.wireOp",EDGE,"E4"),subQ2,subQ1,subQ0])],"isStart":true})])],"derivedFrom":makeQuery(id+"F2.opExtrude","SWEPT_FACE",FACE,{"disambiguationData":[OSD([subQ0]),TDD([subQ3])]})})],"blendedInto":[makeQuery(id+"F2.boolean.opBoolean","SPLIT",FACE,{"disambiguationData":[TD([makeQuery(id+"F2.opExtrude","CAP_FACE",FACE,{"disambiguationData":[OSD([sQuery(id+"F0.wireOp",EDGE,"E4"),subQ2,subQ1,subQ0])],"isStart":true})])],"derivedFrom":makeQuery(id+"F2.opExtrude","SWEPT_FACE",FACE,{"disambiguationData":[OSD([subQ0]),TDD([subQ3])]})})]});}
            var Q85;
            {var subQ0=sQuery(id+"F0.wireOp",EDGE,"E19.1.11.0");var subQ1=sQuery(id+"F0.wireOp",EDGE,"E4");var subQ2=sQuery(id+"F0.wireOp",EDGE,"E19.3.11.0");var subQ3=sQuery(id+"F0.wireOp",EDGE,"E20");var subQ4=makeQuery(id+"F0.imprint","IMPRINT",EDGE,{"disambiguationData":[TD([[makeQuery(id+"F0.imprint","INTERSECT",VERTEX,{"derivedFrom":[subQ0,subQ3]}),1.0]])],"derivedFrom":subQ3});Q85=makeQuery(id+"F8.opChamfer","BLEND_EDGE",EDGE,{"blendedFrom":[makeQuery(id+"F2.opExtrude","CAP_EDGE",EDGE,{"disambiguationData":[OSD([subQ3]),TDD([subQ4])],"isStart":true}),makeQuery(id+"F2.boolean.opBoolean","SPLIT",FACE,{"disambiguationData":[TD([makeQuery(id+"F2.opExtrude","CAP_FACE",FACE,{"disambiguationData":[OSD([subQ1,subQ0,subQ2,subQ3])],"isStart":true})])],"derivedFrom":makeQuery(id+"F2.opExtrude","SWEPT_FACE",FACE,{"disambiguationData":[OSD([subQ0])]})})],"blendedInto":[makeQuery(id+"F2.boolean.opBoolean","SPLIT",FACE,{"disambiguationData":[TD([makeQuery(id+"F2.opExtrude","CAP_FACE",FACE,{"disambiguationData":[OSD([subQ1,subQ0,subQ2,subQ3])],"isStart":true})])],"derivedFrom":makeQuery(id+"F2.opExtrude","SWEPT_FACE",FACE,{"disambiguationData":[OSD([subQ0])]})})]});}
            var Q86;
            {var subQ0=sQuery(id+"F0.wireOp",EDGE,"E19.1.11.0");var subQ1=sQuery(id+"F0.wireOp",EDGE,"E4");var subQ2=sQuery(id+"F0.wireOp",EDGE,"E19.3.11.0");var subQ3=sQuery(id+"F0.wireOp",EDGE,"E20");var subQ4=makeQuery(id+"F0.imprint","IMPRINT",EDGE,{"disambiguationData":[TD([[makeQuery(id+"F0.imprint","INTERSECT",VERTEX,{"derivedFrom":[subQ0,subQ3]}),1.0]])],"derivedFrom":subQ3});Q86=makeQuery(id+"F8.opChamfer","BLEND_EDGE",EDGE,{"blendedFrom":[makeQuery(id+"F2.opExtrude","CAP_EDGE",EDGE,{"disambiguationData":[OSD([subQ3]),TDD([subQ4])],"isStart":true}),makeQuery(id+"F2.boolean.opBoolean","SPLIT",FACE,{"disambiguationData":[TD([makeQuery(id+"F2.opExtrude","CAP_FACE",FACE,{"disambiguationData":[OSD([subQ1,subQ0,subQ2,subQ3])],"isStart":true})])],"derivedFrom":makeQuery(id+"F2.opExtrude","SWEPT_FACE",FACE,{"disambiguationData":[OSD([subQ2])]})})],"blendedInto":[makeQuery(id+"F2.boolean.opBoolean","SPLIT",FACE,{"disambiguationData":[TD([makeQuery(id+"F2.opExtrude","CAP_FACE",FACE,{"disambiguationData":[OSD([subQ1,subQ0,subQ2,subQ3])],"isStart":true})])],"derivedFrom":makeQuery(id+"F2.opExtrude","SWEPT_FACE",FACE,{"disambiguationData":[OSD([subQ2])]})})]});}
            var Q87;
            {var subQ0=sQuery(id+"F0.wireOp",EDGE,"E19.1.11.0");var subQ1=sQuery(id+"F0.wireOp",EDGE,"E4");var subQ2=sQuery(id+"F0.wireOp",EDGE,"E19.3.11.0");var subQ3=makeQuery(id+"F0.imprint","IMPRINT",EDGE,{"disambiguationData":[TD([[makeQuery(id+"F0.imprint","INTERSECT",VERTEX,{"derivedFrom":[subQ1,subQ0]}),1.0]])],"derivedFrom":subQ1});var subQ4=sQuery(id+"F0.wireOp",EDGE,"E20");Q87=makeQuery(id+"F9.opChamfer","BLEND_EDGE",EDGE,{"blendedFrom":[makeQuery(id+"F2.opExtrude","CAP_EDGE",EDGE,{"disambiguationData":[OSD([subQ1]),TDD([subQ3])],"isStart":true}),makeQuery(id+"F2.boolean.opBoolean","SPLIT",FACE,{"disambiguationData":[TD([makeQuery(id+"F2.opExtrude","CAP_FACE",FACE,{"disambiguationData":[OSD([subQ1,subQ0,subQ2,subQ4])],"isStart":true})])],"derivedFrom":makeQuery(id+"F2.opExtrude","SWEPT_FACE",FACE,{"disambiguationData":[OSD([subQ2])]})})],"blendedInto":[makeQuery(id+"F2.boolean.opBoolean","SPLIT",FACE,{"disambiguationData":[TD([makeQuery(id+"F2.opExtrude","CAP_FACE",FACE,{"disambiguationData":[OSD([subQ1,subQ0,subQ2,subQ4])],"isStart":true})])],"derivedFrom":makeQuery(id+"F2.opExtrude","SWEPT_FACE",FACE,{"disambiguationData":[OSD([subQ2])]})})]});}
            var Q88;
            {var subQ0=sQuery(id+"F0.wireOp",EDGE,"E19.3.11.0");var subQ1=sQuery(id+"F0.wireOp",EDGE,"E19.1.11.0");var subQ2=sQuery(id+"F0.wireOp",EDGE,"E4");var subQ3=makeQuery(id+"F0.imprint","IMPRINT",EDGE,{"disambiguationData":[TD([[makeQuery(id+"F0.imprint","INTERSECT",VERTEX,{"derivedFrom":[subQ2,subQ1]}),1.0]])],"derivedFrom":subQ2});Q88=makeQuery(id+"F9.opChamfer","BLEND_EDGE",EDGE,{"blendedFrom":[makeQuery(id+"F2.opExtrude","CAP_EDGE",EDGE,{"disambiguationData":[OSD([subQ2]),TDD([subQ3])],"isStart":true}),makeQuery(id+"F2.boolean.opBoolean","SPLIT",FACE,{"disambiguationData":[TD([makeQuery(id+"F2.opExtrude","CAP_FACE",FACE,{"disambiguationData":[OSD([subQ2,subQ1,subQ0,sQuery(id+"F0.wireOp",EDGE,"E20")])],"isStart":true})])],"derivedFrom":makeQuery(id+"F2.opExtrude","SWEPT_FACE",FACE,{"disambiguationData":[OSD([subQ2]),TDD([subQ3])]})})],"blendedInto":[makeQuery(id+"F2.boolean.opBoolean","SPLIT",FACE,{"disambiguationData":[TD([makeQuery(id+"F2.opExtrude","CAP_FACE",FACE,{"disambiguationData":[OSD([subQ2,subQ1,subQ0,sQuery(id+"F0.wireOp",EDGE,"E20")])],"isStart":true})])],"derivedFrom":makeQuery(id+"F2.opExtrude","SWEPT_FACE",FACE,{"disambiguationData":[OSD([subQ2]),TDD([subQ3])]})})]});}
            var Q89;
            {var subQ0=sQuery(id+"F0.wireOp",EDGE,"E19.1.11.0");var subQ1=sQuery(id+"F0.wireOp",EDGE,"E4");var subQ2=sQuery(id+"F0.wireOp",EDGE,"E19.3.11.0");var subQ3=makeQuery(id+"F0.imprint","IMPRINT",EDGE,{"disambiguationData":[TD([[makeQuery(id+"F0.imprint","INTERSECT",VERTEX,{"derivedFrom":[subQ1,subQ0]}),1.0]])],"derivedFrom":subQ1});var subQ4=sQuery(id+"F0.wireOp",EDGE,"E20");Q89=makeQuery(id+"F9.opChamfer","BLEND_EDGE",EDGE,{"blendedFrom":[makeQuery(id+"F2.opExtrude","CAP_EDGE",EDGE,{"disambiguationData":[OSD([subQ1]),TDD([subQ3])],"isStart":true}),makeQuery(id+"F2.boolean.opBoolean","SPLIT",FACE,{"disambiguationData":[TD([makeQuery(id+"F2.opExtrude","CAP_FACE",FACE,{"disambiguationData":[OSD([subQ1,subQ0,subQ2,subQ4])],"isStart":true})])],"derivedFrom":makeQuery(id+"F2.opExtrude","SWEPT_FACE",FACE,{"disambiguationData":[OSD([subQ0])]})})],"blendedInto":[makeQuery(id+"F2.boolean.opBoolean","SPLIT",FACE,{"disambiguationData":[TD([makeQuery(id+"F2.opExtrude","CAP_FACE",FACE,{"disambiguationData":[OSD([subQ1,subQ0,subQ2,subQ4])],"isStart":true})])],"derivedFrom":makeQuery(id+"F2.opExtrude","SWEPT_FACE",FACE,{"disambiguationData":[OSD([subQ0])]})})]});}
            var Q90;
            {var subQ0=sQuery(id+"F0.wireOp",EDGE,"E19.3.10.0");var subQ1=sQuery(id+"F0.wireOp",EDGE,"E20");var subQ2=sQuery(id+"F0.wireOp",EDGE,"E19.1.10.0");var subQ3=makeQuery(id+"F0.imprint","IMPRINT",EDGE,{"disambiguationData":[TD([[makeQuery(id+"F0.imprint","INTERSECT",VERTEX,{"derivedFrom":[subQ2,subQ1]}),1.0]])],"derivedFrom":subQ1});Q90=makeQuery(id+"F8.opChamfer","BLEND_EDGE",EDGE,{"blendedFrom":[makeQuery(id+"F2.opExtrude","CAP_EDGE",EDGE,{"disambiguationData":[OSD([subQ1]),TDD([subQ3])],"isStart":true}),makeQuery(id+"F2.boolean.opBoolean","SPLIT",FACE,{"disambiguationData":[TD([makeQuery(id+"F2.opExtrude","CAP_FACE",FACE,{"disambiguationData":[OSD([sQuery(id+"F0.wireOp",EDGE,"E4"),subQ2,subQ0,subQ1])],"isStart":true})])],"derivedFrom":makeQuery(id+"F2.opExtrude","SWEPT_FACE",FACE,{"disambiguationData":[OSD([subQ1]),TDD([subQ3])]})})],"blendedInto":[makeQuery(id+"F2.boolean.opBoolean","SPLIT",FACE,{"disambiguationData":[TD([makeQuery(id+"F2.opExtrude","CAP_FACE",FACE,{"disambiguationData":[OSD([sQuery(id+"F0.wireOp",EDGE,"E4"),subQ2,subQ0,subQ1])],"isStart":true})])],"derivedFrom":makeQuery(id+"F2.opExtrude","SWEPT_FACE",FACE,{"disambiguationData":[OSD([subQ1]),TDD([subQ3])]})})]});}
            var Q91;
            {var subQ0=sQuery(id+"F0.wireOp",EDGE,"E19.1.10.0");var subQ1=sQuery(id+"F0.wireOp",EDGE,"E4");var subQ2=sQuery(id+"F0.wireOp",EDGE,"E19.3.10.0");var subQ3=sQuery(id+"F0.wireOp",EDGE,"E20");var subQ4=makeQuery(id+"F0.imprint","IMPRINT",EDGE,{"disambiguationData":[TD([[makeQuery(id+"F0.imprint","INTERSECT",VERTEX,{"derivedFrom":[subQ0,subQ3]}),1.0]])],"derivedFrom":subQ3});Q91=makeQuery(id+"F8.opChamfer","BLEND_EDGE",EDGE,{"blendedFrom":[makeQuery(id+"F2.opExtrude","CAP_EDGE",EDGE,{"disambiguationData":[OSD([subQ3]),TDD([subQ4])],"isStart":true}),makeQuery(id+"F2.boolean.opBoolean","SPLIT",FACE,{"disambiguationData":[TD([makeQuery(id+"F2.opExtrude","CAP_FACE",FACE,{"disambiguationData":[OSD([subQ1,subQ0,subQ2,subQ3])],"isStart":true})])],"derivedFrom":makeQuery(id+"F2.opExtrude","SWEPT_FACE",FACE,{"disambiguationData":[OSD([subQ2])]})})],"blendedInto":[makeQuery(id+"F2.boolean.opBoolean","SPLIT",FACE,{"disambiguationData":[TD([makeQuery(id+"F2.opExtrude","CAP_FACE",FACE,{"disambiguationData":[OSD([subQ1,subQ0,subQ2,subQ3])],"isStart":true})])],"derivedFrom":makeQuery(id+"F2.opExtrude","SWEPT_FACE",FACE,{"disambiguationData":[OSD([subQ2])]})})]});}
            var Q92;
            {var subQ0=sQuery(id+"F0.wireOp",EDGE,"E19.1.10.0");var subQ1=sQuery(id+"F0.wireOp",EDGE,"E4");var subQ2=sQuery(id+"F0.wireOp",EDGE,"E19.3.10.0");var subQ3=sQuery(id+"F0.wireOp",EDGE,"E20");var subQ4=makeQuery(id+"F0.imprint","IMPRINT",EDGE,{"disambiguationData":[TD([[makeQuery(id+"F0.imprint","INTERSECT",VERTEX,{"derivedFrom":[subQ0,subQ3]}),1.0]])],"derivedFrom":subQ3});Q92=makeQuery(id+"F8.opChamfer","BLEND_EDGE",EDGE,{"blendedFrom":[makeQuery(id+"F2.opExtrude","CAP_EDGE",EDGE,{"disambiguationData":[OSD([subQ3]),TDD([subQ4])],"isStart":true}),makeQuery(id+"F2.boolean.opBoolean","SPLIT",FACE,{"disambiguationData":[TD([makeQuery(id+"F2.opExtrude","CAP_FACE",FACE,{"disambiguationData":[OSD([subQ1,subQ0,subQ2,subQ3])],"isStart":true})])],"derivedFrom":makeQuery(id+"F2.opExtrude","SWEPT_FACE",FACE,{"disambiguationData":[OSD([subQ0])]})})],"blendedInto":[makeQuery(id+"F2.boolean.opBoolean","SPLIT",FACE,{"disambiguationData":[TD([makeQuery(id+"F2.opExtrude","CAP_FACE",FACE,{"disambiguationData":[OSD([subQ1,subQ0,subQ2,subQ3])],"isStart":true})])],"derivedFrom":makeQuery(id+"F2.opExtrude","SWEPT_FACE",FACE,{"disambiguationData":[OSD([subQ0])]})})]});}
            var Q93;
            {var subQ0=sQuery(id+"F0.wireOp",EDGE,"E19.1.10.0");var subQ1=sQuery(id+"F0.wireOp",EDGE,"E4");var subQ2=sQuery(id+"F0.wireOp",EDGE,"E19.3.10.0");var subQ3=makeQuery(id+"F0.imprint","IMPRINT",EDGE,{"disambiguationData":[TD([[makeQuery(id+"F0.imprint","INTERSECT",VERTEX,{"derivedFrom":[subQ1,subQ0]}),1.0]])],"derivedFrom":subQ1});var subQ4=sQuery(id+"F0.wireOp",EDGE,"E20");Q93=makeQuery(id+"F9.opChamfer","BLEND_EDGE",EDGE,{"blendedFrom":[makeQuery(id+"F2.opExtrude","CAP_EDGE",EDGE,{"disambiguationData":[OSD([subQ1]),TDD([subQ3])],"isStart":true}),makeQuery(id+"F2.boolean.opBoolean","SPLIT",FACE,{"disambiguationData":[TD([makeQuery(id+"F2.opExtrude","CAP_FACE",FACE,{"disambiguationData":[OSD([subQ1,subQ0,subQ2,subQ4])],"isStart":true})])],"derivedFrom":makeQuery(id+"F2.opExtrude","SWEPT_FACE",FACE,{"disambiguationData":[OSD([subQ0])]})})],"blendedInto":[makeQuery(id+"F2.boolean.opBoolean","SPLIT",FACE,{"disambiguationData":[TD([makeQuery(id+"F2.opExtrude","CAP_FACE",FACE,{"disambiguationData":[OSD([subQ1,subQ0,subQ2,subQ4])],"isStart":true})])],"derivedFrom":makeQuery(id+"F2.opExtrude","SWEPT_FACE",FACE,{"disambiguationData":[OSD([subQ0])]})})]});}
            var Q94;
            {var subQ0=sQuery(id+"F0.wireOp",EDGE,"E19.1.10.0");var subQ1=sQuery(id+"F0.wireOp",EDGE,"E4");var subQ2=sQuery(id+"F0.wireOp",EDGE,"E19.3.10.0");var subQ3=makeQuery(id+"F0.imprint","IMPRINT",EDGE,{"disambiguationData":[TD([[makeQuery(id+"F0.imprint","INTERSECT",VERTEX,{"derivedFrom":[subQ1,subQ0]}),1.0]])],"derivedFrom":subQ1});var subQ4=sQuery(id+"F0.wireOp",EDGE,"E20");Q94=makeQuery(id+"F9.opChamfer","BLEND_EDGE",EDGE,{"blendedFrom":[makeQuery(id+"F2.opExtrude","CAP_EDGE",EDGE,{"disambiguationData":[OSD([subQ1]),TDD([subQ3])],"isStart":true}),makeQuery(id+"F2.boolean.opBoolean","SPLIT",FACE,{"disambiguationData":[TD([makeQuery(id+"F2.opExtrude","CAP_FACE",FACE,{"disambiguationData":[OSD([subQ1,subQ0,subQ2,subQ4])],"isStart":true})])],"derivedFrom":makeQuery(id+"F2.opExtrude","SWEPT_FACE",FACE,{"disambiguationData":[OSD([subQ2])]})})],"blendedInto":[makeQuery(id+"F2.boolean.opBoolean","SPLIT",FACE,{"disambiguationData":[TD([makeQuery(id+"F2.opExtrude","CAP_FACE",FACE,{"disambiguationData":[OSD([subQ1,subQ0,subQ2,subQ4])],"isStart":true})])],"derivedFrom":makeQuery(id+"F2.opExtrude","SWEPT_FACE",FACE,{"disambiguationData":[OSD([subQ2])]})})]});}
            var Q95;
            {var subQ0=sQuery(id+"F0.wireOp",EDGE,"E19.3.10.0");var subQ1=sQuery(id+"F0.wireOp",EDGE,"E19.1.10.0");var subQ2=sQuery(id+"F0.wireOp",EDGE,"E4");var subQ3=makeQuery(id+"F0.imprint","IMPRINT",EDGE,{"disambiguationData":[TD([[makeQuery(id+"F0.imprint","INTERSECT",VERTEX,{"derivedFrom":[subQ2,subQ1]}),1.0]])],"derivedFrom":subQ2});Q95=makeQuery(id+"F9.opChamfer","BLEND_EDGE",EDGE,{"blendedFrom":[makeQuery(id+"F2.opExtrude","CAP_EDGE",EDGE,{"disambiguationData":[OSD([subQ2]),TDD([subQ3])],"isStart":true}),makeQuery(id+"F2.boolean.opBoolean","SPLIT",FACE,{"disambiguationData":[TD([makeQuery(id+"F2.opExtrude","CAP_FACE",FACE,{"disambiguationData":[OSD([subQ2,subQ1,subQ0,sQuery(id+"F0.wireOp",EDGE,"E20")])],"isStart":true})])],"derivedFrom":makeQuery(id+"F2.opExtrude","SWEPT_FACE",FACE,{"disambiguationData":[OSD([subQ2]),TDD([subQ3])]})})],"blendedInto":[makeQuery(id+"F2.boolean.opBoolean","SPLIT",FACE,{"disambiguationData":[TD([makeQuery(id+"F2.opExtrude","CAP_FACE",FACE,{"disambiguationData":[OSD([subQ2,subQ1,subQ0,sQuery(id+"F0.wireOp",EDGE,"E20")])],"isStart":true})])],"derivedFrom":makeQuery(id+"F2.opExtrude","SWEPT_FACE",FACE,{"disambiguationData":[OSD([subQ2]),TDD([subQ3])]})})]});}
            var Q96;
            {var subQ0=sQuery(id+"F0.wireOp",EDGE,"E19.3.9.0");var subQ1=sQuery(id+"F0.wireOp",EDGE,"E19.1.9.0");var subQ2=sQuery(id+"F0.wireOp",EDGE,"E4");var subQ3=makeQuery(id+"F0.imprint","IMPRINT",EDGE,{"disambiguationData":[TD([[makeQuery(id+"F0.imprint","INTERSECT",VERTEX,{"derivedFrom":[subQ2,subQ1]}),1.0]])],"derivedFrom":subQ2});Q96=makeQuery(id+"F9.opChamfer","BLEND_EDGE",EDGE,{"blendedFrom":[makeQuery(id+"F2.opExtrude","CAP_EDGE",EDGE,{"disambiguationData":[OSD([subQ2]),TDD([subQ3])],"isStart":true}),makeQuery(id+"F2.boolean.opBoolean","SPLIT",FACE,{"disambiguationData":[TD([makeQuery(id+"F2.opExtrude","CAP_FACE",FACE,{"disambiguationData":[OSD([subQ2,subQ1,subQ0,sQuery(id+"F0.wireOp",EDGE,"E20")])],"isStart":true})])],"derivedFrom":makeQuery(id+"F2.opExtrude","SWEPT_FACE",FACE,{"disambiguationData":[OSD([subQ2]),TDD([subQ3])]})})],"blendedInto":[makeQuery(id+"F2.boolean.opBoolean","SPLIT",FACE,{"disambiguationData":[TD([makeQuery(id+"F2.opExtrude","CAP_FACE",FACE,{"disambiguationData":[OSD([subQ2,subQ1,subQ0,sQuery(id+"F0.wireOp",EDGE,"E20")])],"isStart":true})])],"derivedFrom":makeQuery(id+"F2.opExtrude","SWEPT_FACE",FACE,{"disambiguationData":[OSD([subQ2]),TDD([subQ3])]})})]});}
            var Q97;
            {var subQ0=sQuery(id+"F0.wireOp",EDGE,"E20");var subQ1=sQuery(id+"F0.wireOp",EDGE,"E19.3.9.0");var subQ2=sQuery(id+"F0.wireOp",EDGE,"E19.1.9.0");var subQ3=sQuery(id+"F0.wireOp",EDGE,"E4");var subQ4=makeQuery(id+"F0.imprint","IMPRINT",EDGE,{"disambiguationData":[TD([[makeQuery(id+"F0.imprint","INTERSECT",VERTEX,{"derivedFrom":[subQ3,subQ2]}),1.0]])],"derivedFrom":subQ3});Q97=makeQuery(id+"F9.opChamfer","BLEND_EDGE",EDGE,{"blendedFrom":[makeQuery(id+"F2.opExtrude","CAP_EDGE",EDGE,{"disambiguationData":[OSD([subQ3]),TDD([subQ4])],"isStart":true}),makeQuery(id+"F2.boolean.opBoolean","SPLIT",FACE,{"disambiguationData":[TD([makeQuery(id+"F2.opExtrude","CAP_FACE",FACE,{"disambiguationData":[OSD([subQ3,subQ2,subQ1,subQ0])],"isStart":true})])],"derivedFrom":makeQuery(id+"F2.opExtrude","SWEPT_FACE",FACE,{"disambiguationData":[OSD([subQ1])]})})],"blendedInto":[makeQuery(id+"F2.boolean.opBoolean","SPLIT",FACE,{"disambiguationData":[TD([makeQuery(id+"F2.opExtrude","CAP_FACE",FACE,{"disambiguationData":[OSD([subQ3,subQ2,subQ1,subQ0])],"isStart":true})])],"derivedFrom":makeQuery(id+"F2.opExtrude","SWEPT_FACE",FACE,{"disambiguationData":[OSD([subQ1])]})})]});}
            var Q98;
            {var subQ0=sQuery(id+"F0.wireOp",EDGE,"E20");var subQ1=sQuery(id+"F0.wireOp",EDGE,"E19.3.9.0");var subQ2=sQuery(id+"F0.wireOp",EDGE,"E19.1.9.0");var subQ3=sQuery(id+"F0.wireOp",EDGE,"E4");var subQ4=makeQuery(id+"F0.imprint","IMPRINT",EDGE,{"disambiguationData":[TD([[makeQuery(id+"F0.imprint","INTERSECT",VERTEX,{"derivedFrom":[subQ2,subQ0]}),1.0]])],"derivedFrom":subQ0});Q98=makeQuery(id+"F8.opChamfer","BLEND_EDGE",EDGE,{"blendedFrom":[makeQuery(id+"F2.opExtrude","CAP_EDGE",EDGE,{"disambiguationData":[OSD([subQ0]),TDD([subQ4])],"isStart":true}),makeQuery(id+"F2.boolean.opBoolean","SPLIT",FACE,{"disambiguationData":[TD([makeQuery(id+"F2.opExtrude","CAP_FACE",FACE,{"disambiguationData":[OSD([subQ3,subQ2,subQ1,subQ0])],"isStart":true})])],"derivedFrom":makeQuery(id+"F2.opExtrude","SWEPT_FACE",FACE,{"disambiguationData":[OSD([subQ1])]})})],"blendedInto":[makeQuery(id+"F2.boolean.opBoolean","SPLIT",FACE,{"disambiguationData":[TD([makeQuery(id+"F2.opExtrude","CAP_FACE",FACE,{"disambiguationData":[OSD([subQ3,subQ2,subQ1,subQ0])],"isStart":true})])],"derivedFrom":makeQuery(id+"F2.opExtrude","SWEPT_FACE",FACE,{"disambiguationData":[OSD([subQ1])]})})]});}
            var Q99;
            {var subQ0=sQuery(id+"F0.wireOp",EDGE,"E20");var subQ1=sQuery(id+"F0.wireOp",EDGE,"E19.3.9.0");var subQ2=sQuery(id+"F0.wireOp",EDGE,"E19.1.9.0");var subQ3=sQuery(id+"F0.wireOp",EDGE,"E4");var subQ4=makeQuery(id+"F0.imprint","IMPRINT",EDGE,{"disambiguationData":[TD([[makeQuery(id+"F0.imprint","INTERSECT",VERTEX,{"derivedFrom":[subQ2,subQ0]}),1.0]])],"derivedFrom":subQ0});Q99=makeQuery(id+"F8.opChamfer","BLEND_EDGE",EDGE,{"blendedFrom":[makeQuery(id+"F2.opExtrude","CAP_EDGE",EDGE,{"disambiguationData":[OSD([subQ0]),TDD([subQ4])],"isStart":true}),makeQuery(id+"F2.boolean.opBoolean","SPLIT",FACE,{"disambiguationData":[TD([makeQuery(id+"F2.opExtrude","CAP_FACE",FACE,{"disambiguationData":[OSD([subQ3,subQ2,subQ1,subQ0])],"isStart":true})])],"derivedFrom":makeQuery(id+"F2.opExtrude","SWEPT_FACE",FACE,{"disambiguationData":[OSD([subQ2])]})})],"blendedInto":[makeQuery(id+"F2.boolean.opBoolean","SPLIT",FACE,{"disambiguationData":[TD([makeQuery(id+"F2.opExtrude","CAP_FACE",FACE,{"disambiguationData":[OSD([subQ3,subQ2,subQ1,subQ0])],"isStart":true})])],"derivedFrom":makeQuery(id+"F2.opExtrude","SWEPT_FACE",FACE,{"disambiguationData":[OSD([subQ2])]})})]});}
            var Q100;
            {var subQ0=sQuery(id+"F0.wireOp",EDGE,"E20");var subQ1=sQuery(id+"F0.wireOp",EDGE,"E19.3.9.0");var subQ2=sQuery(id+"F0.wireOp",EDGE,"E19.1.9.0");var subQ3=makeQuery(id+"F0.imprint","IMPRINT",EDGE,{"disambiguationData":[TD([[makeQuery(id+"F0.imprint","INTERSECT",VERTEX,{"derivedFrom":[subQ2,subQ0]}),1.0]])],"derivedFrom":subQ0});Q100=makeQuery(id+"F8.opChamfer","BLEND_EDGE",EDGE,{"blendedFrom":[makeQuery(id+"F2.opExtrude","CAP_EDGE",EDGE,{"disambiguationData":[OSD([subQ0]),TDD([subQ3])],"isStart":true}),makeQuery(id+"F2.boolean.opBoolean","SPLIT",FACE,{"disambiguationData":[TD([makeQuery(id+"F2.opExtrude","CAP_FACE",FACE,{"disambiguationData":[OSD([sQuery(id+"F0.wireOp",EDGE,"E4"),subQ2,subQ1,subQ0])],"isStart":true})])],"derivedFrom":makeQuery(id+"F2.opExtrude","SWEPT_FACE",FACE,{"disambiguationData":[OSD([subQ0]),TDD([subQ3])]})})],"blendedInto":[makeQuery(id+"F2.boolean.opBoolean","SPLIT",FACE,{"disambiguationData":[TD([makeQuery(id+"F2.opExtrude","CAP_FACE",FACE,{"disambiguationData":[OSD([sQuery(id+"F0.wireOp",EDGE,"E4"),subQ2,subQ1,subQ0])],"isStart":true})])],"derivedFrom":makeQuery(id+"F2.opExtrude","SWEPT_FACE",FACE,{"disambiguationData":[OSD([subQ0]),TDD([subQ3])]})})]});}
            var Q101;
            {var subQ0=sQuery(id+"F0.wireOp",EDGE,"E19.1.8.0");var subQ1=sQuery(id+"F0.wireOp",EDGE,"E20");var subQ2=sQuery(id+"F0.wireOp",EDGE,"E19.3.8.0");var subQ3=makeQuery(id+"F0.imprint","IMPRINT",EDGE,{"disambiguationData":[TD([[makeQuery(id+"F0.imprint","INTERSECT",VERTEX,{"derivedFrom":[subQ0,subQ1]}),1.0]])],"derivedFrom":subQ1});Q101=makeQuery(id+"F8.opChamfer","BLEND_EDGE",EDGE,{"blendedFrom":[makeQuery(id+"F2.opExtrude","CAP_EDGE",EDGE,{"disambiguationData":[OSD([subQ1]),TDD([subQ3])],"isStart":true}),makeQuery(id+"F2.boolean.opBoolean","SPLIT",FACE,{"disambiguationData":[TD([makeQuery(id+"F2.opExtrude","CAP_FACE",FACE,{"disambiguationData":[OSD([sQuery(id+"F0.wireOp",EDGE,"E4"),subQ0,subQ2,subQ1])],"isStart":true})])],"derivedFrom":makeQuery(id+"F2.opExtrude","SWEPT_FACE",FACE,{"disambiguationData":[OSD([subQ1]),TDD([subQ3])]})})],"blendedInto":[makeQuery(id+"F2.boolean.opBoolean","SPLIT",FACE,{"disambiguationData":[TD([makeQuery(id+"F2.opExtrude","CAP_FACE",FACE,{"disambiguationData":[OSD([sQuery(id+"F0.wireOp",EDGE,"E4"),subQ0,subQ2,subQ1])],"isStart":true})])],"derivedFrom":makeQuery(id+"F2.opExtrude","SWEPT_FACE",FACE,{"disambiguationData":[OSD([subQ1]),TDD([subQ3])]})})]});}
            var Q102;
            {var subQ0=sQuery(id+"F0.wireOp",EDGE,"E19.1.8.0");var subQ1=sQuery(id+"F0.wireOp",EDGE,"E4");var subQ2=sQuery(id+"F0.wireOp",EDGE,"E19.3.8.0");var subQ3=sQuery(id+"F0.wireOp",EDGE,"E20");var subQ4=makeQuery(id+"F0.imprint","IMPRINT",EDGE,{"disambiguationData":[TD([[makeQuery(id+"F0.imprint","INTERSECT",VERTEX,{"derivedFrom":[subQ0,subQ3]}),1.0]])],"derivedFrom":subQ3});Q102=makeQuery(id+"F8.opChamfer","BLEND_EDGE",EDGE,{"blendedFrom":[makeQuery(id+"F2.opExtrude","CAP_EDGE",EDGE,{"disambiguationData":[OSD([subQ3]),TDD([subQ4])],"isStart":true}),makeQuery(id+"F2.boolean.opBoolean","SPLIT",FACE,{"disambiguationData":[TD([makeQuery(id+"F2.opExtrude","CAP_FACE",FACE,{"disambiguationData":[OSD([subQ1,subQ0,subQ2,subQ3])],"isStart":true})])],"derivedFrom":makeQuery(id+"F2.opExtrude","SWEPT_FACE",FACE,{"disambiguationData":[OSD([subQ2])]})})],"blendedInto":[makeQuery(id+"F2.boolean.opBoolean","SPLIT",FACE,{"disambiguationData":[TD([makeQuery(id+"F2.opExtrude","CAP_FACE",FACE,{"disambiguationData":[OSD([subQ1,subQ0,subQ2,subQ3])],"isStart":true})])],"derivedFrom":makeQuery(id+"F2.opExtrude","SWEPT_FACE",FACE,{"disambiguationData":[OSD([subQ2])]})})]});}
            var Q103;
            {var subQ0=sQuery(id+"F0.wireOp",EDGE,"E19.1.8.0");var subQ1=sQuery(id+"F0.wireOp",EDGE,"E4");var subQ2=sQuery(id+"F0.wireOp",EDGE,"E19.3.8.0");var subQ3=sQuery(id+"F0.wireOp",EDGE,"E20");var subQ4=makeQuery(id+"F0.imprint","IMPRINT",EDGE,{"disambiguationData":[TD([[makeQuery(id+"F0.imprint","INTERSECT",VERTEX,{"derivedFrom":[subQ0,subQ3]}),1.0]])],"derivedFrom":subQ3});Q103=makeQuery(id+"F8.opChamfer","BLEND_EDGE",EDGE,{"blendedFrom":[makeQuery(id+"F2.opExtrude","CAP_EDGE",EDGE,{"disambiguationData":[OSD([subQ3]),TDD([subQ4])],"isStart":true}),makeQuery(id+"F2.boolean.opBoolean","SPLIT",FACE,{"disambiguationData":[TD([makeQuery(id+"F2.opExtrude","CAP_FACE",FACE,{"disambiguationData":[OSD([subQ1,subQ0,subQ2,subQ3])],"isStart":true})])],"derivedFrom":makeQuery(id+"F2.opExtrude","SWEPT_FACE",FACE,{"disambiguationData":[OSD([subQ0])]})})],"blendedInto":[makeQuery(id+"F2.boolean.opBoolean","SPLIT",FACE,{"disambiguationData":[TD([makeQuery(id+"F2.opExtrude","CAP_FACE",FACE,{"disambiguationData":[OSD([subQ1,subQ0,subQ2,subQ3])],"isStart":true})])],"derivedFrom":makeQuery(id+"F2.opExtrude","SWEPT_FACE",FACE,{"disambiguationData":[OSD([subQ0])]})})]});}
            var Q104;
            {var subQ0=sQuery(id+"F0.wireOp",EDGE,"E19.1.8.0");var subQ1=sQuery(id+"F0.wireOp",EDGE,"E4");var subQ2=sQuery(id+"F0.wireOp",EDGE,"E19.3.8.0");var subQ3=makeQuery(id+"F0.imprint","IMPRINT",EDGE,{"disambiguationData":[TD([[makeQuery(id+"F0.imprint","INTERSECT",VERTEX,{"derivedFrom":[subQ1,subQ0]}),1.0]])],"derivedFrom":subQ1});var subQ4=sQuery(id+"F0.wireOp",EDGE,"E20");Q104=makeQuery(id+"F9.opChamfer","BLEND_EDGE",EDGE,{"blendedFrom":[makeQuery(id+"F2.opExtrude","CAP_EDGE",EDGE,{"disambiguationData":[OSD([subQ1]),TDD([subQ3])],"isStart":true}),makeQuery(id+"F2.boolean.opBoolean","SPLIT",FACE,{"disambiguationData":[TD([makeQuery(id+"F2.opExtrude","CAP_FACE",FACE,{"disambiguationData":[OSD([subQ1,subQ0,subQ2,subQ4])],"isStart":true})])],"derivedFrom":makeQuery(id+"F2.opExtrude","SWEPT_FACE",FACE,{"disambiguationData":[OSD([subQ2])]})})],"blendedInto":[makeQuery(id+"F2.boolean.opBoolean","SPLIT",FACE,{"disambiguationData":[TD([makeQuery(id+"F2.opExtrude","CAP_FACE",FACE,{"disambiguationData":[OSD([subQ1,subQ0,subQ2,subQ4])],"isStart":true})])],"derivedFrom":makeQuery(id+"F2.opExtrude","SWEPT_FACE",FACE,{"disambiguationData":[OSD([subQ2])]})})]});}
            var Q105;
            {var subQ0=sQuery(id+"F0.wireOp",EDGE,"E19.1.8.0");var subQ1=sQuery(id+"F0.wireOp",EDGE,"E4");var subQ2=sQuery(id+"F0.wireOp",EDGE,"E19.3.8.0");var subQ3=makeQuery(id+"F0.imprint","IMPRINT",EDGE,{"disambiguationData":[TD([[makeQuery(id+"F0.imprint","INTERSECT",VERTEX,{"derivedFrom":[subQ1,subQ0]}),1.0]])],"derivedFrom":subQ1});var subQ4=sQuery(id+"F0.wireOp",EDGE,"E20");Q105=makeQuery(id+"F9.opChamfer","BLEND_EDGE",EDGE,{"blendedFrom":[makeQuery(id+"F2.opExtrude","CAP_EDGE",EDGE,{"disambiguationData":[OSD([subQ1]),TDD([subQ3])],"isStart":true}),makeQuery(id+"F2.boolean.opBoolean","SPLIT",FACE,{"disambiguationData":[TD([makeQuery(id+"F2.opExtrude","CAP_FACE",FACE,{"disambiguationData":[OSD([subQ1,subQ0,subQ2,subQ4])],"isStart":true})])],"derivedFrom":makeQuery(id+"F2.opExtrude","SWEPT_FACE",FACE,{"disambiguationData":[OSD([subQ0])]})})],"blendedInto":[makeQuery(id+"F2.boolean.opBoolean","SPLIT",FACE,{"disambiguationData":[TD([makeQuery(id+"F2.opExtrude","CAP_FACE",FACE,{"disambiguationData":[OSD([subQ1,subQ0,subQ2,subQ4])],"isStart":true})])],"derivedFrom":makeQuery(id+"F2.opExtrude","SWEPT_FACE",FACE,{"disambiguationData":[OSD([subQ0])]})})]});}
            var Q106;
            {var subQ0=sQuery(id+"F0.wireOp",EDGE,"E19.1.8.0");var subQ1=sQuery(id+"F0.wireOp",EDGE,"E19.3.8.0");var subQ2=sQuery(id+"F0.wireOp",EDGE,"E4");var subQ3=makeQuery(id+"F0.imprint","IMPRINT",EDGE,{"disambiguationData":[TD([[makeQuery(id+"F0.imprint","INTERSECT",VERTEX,{"derivedFrom":[subQ2,subQ0]}),1.0]])],"derivedFrom":subQ2});Q106=makeQuery(id+"F9.opChamfer","BLEND_EDGE",EDGE,{"blendedFrom":[makeQuery(id+"F2.opExtrude","CAP_EDGE",EDGE,{"disambiguationData":[OSD([subQ2]),TDD([subQ3])],"isStart":true}),makeQuery(id+"F2.boolean.opBoolean","SPLIT",FACE,{"disambiguationData":[TD([makeQuery(id+"F2.opExtrude","CAP_FACE",FACE,{"disambiguationData":[OSD([subQ2,subQ0,subQ1,sQuery(id+"F0.wireOp",EDGE,"E20")])],"isStart":true})])],"derivedFrom":makeQuery(id+"F2.opExtrude","SWEPT_FACE",FACE,{"disambiguationData":[OSD([subQ2]),TDD([subQ3])]})})],"blendedInto":[makeQuery(id+"F2.boolean.opBoolean","SPLIT",FACE,{"disambiguationData":[TD([makeQuery(id+"F2.opExtrude","CAP_FACE",FACE,{"disambiguationData":[OSD([subQ2,subQ0,subQ1,sQuery(id+"F0.wireOp",EDGE,"E20")])],"isStart":true})])],"derivedFrom":makeQuery(id+"F2.opExtrude","SWEPT_FACE",FACE,{"disambiguationData":[OSD([subQ2]),TDD([subQ3])]})})]});}
            var Q107;
            {var subQ0=sQuery(id+"F0.wireOp",EDGE,"E19.3.7.0");var subQ1=sQuery(id+"F0.wireOp",EDGE,"E19.1.7.0");var subQ2=sQuery(id+"F0.wireOp",EDGE,"E4");var subQ3=makeQuery(id+"F0.imprint","IMPRINT",EDGE,{"disambiguationData":[TD([[makeQuery(id+"F0.imprint","INTERSECT",VERTEX,{"derivedFrom":[subQ2,subQ1]}),1.0]])],"derivedFrom":subQ2});Q107=makeQuery(id+"F9.opChamfer","BLEND_EDGE",EDGE,{"blendedFrom":[makeQuery(id+"F2.opExtrude","CAP_EDGE",EDGE,{"disambiguationData":[OSD([subQ2]),TDD([subQ3])],"isStart":true}),makeQuery(id+"F2.boolean.opBoolean","SPLIT",FACE,{"disambiguationData":[TD([makeQuery(id+"F2.opExtrude","CAP_FACE",FACE,{"disambiguationData":[OSD([subQ2,subQ1,subQ0,sQuery(id+"F0.wireOp",EDGE,"E20")])],"isStart":true})])],"derivedFrom":makeQuery(id+"F2.opExtrude","SWEPT_FACE",FACE,{"disambiguationData":[OSD([subQ2]),TDD([subQ3])]})})],"blendedInto":[makeQuery(id+"F2.boolean.opBoolean","SPLIT",FACE,{"disambiguationData":[TD([makeQuery(id+"F2.opExtrude","CAP_FACE",FACE,{"disambiguationData":[OSD([subQ2,subQ1,subQ0,sQuery(id+"F0.wireOp",EDGE,"E20")])],"isStart":true})])],"derivedFrom":makeQuery(id+"F2.opExtrude","SWEPT_FACE",FACE,{"disambiguationData":[OSD([subQ2]),TDD([subQ3])]})})]});}
            var Q108;
            {var subQ0=sQuery(id+"F0.wireOp",EDGE,"E19.1.7.0");var subQ1=sQuery(id+"F0.wireOp",EDGE,"E4");var subQ2=sQuery(id+"F0.wireOp",EDGE,"E19.3.7.0");var subQ3=makeQuery(id+"F0.imprint","IMPRINT",EDGE,{"disambiguationData":[TD([[makeQuery(id+"F0.imprint","INTERSECT",VERTEX,{"derivedFrom":[subQ1,subQ0]}),1.0]])],"derivedFrom":subQ1});var subQ4=sQuery(id+"F0.wireOp",EDGE,"E20");Q108=makeQuery(id+"F9.opChamfer","BLEND_EDGE",EDGE,{"blendedFrom":[makeQuery(id+"F2.opExtrude","CAP_EDGE",EDGE,{"disambiguationData":[OSD([subQ1]),TDD([subQ3])],"isStart":true}),makeQuery(id+"F2.boolean.opBoolean","SPLIT",FACE,{"disambiguationData":[TD([makeQuery(id+"F2.opExtrude","CAP_FACE",FACE,{"disambiguationData":[OSD([subQ1,subQ0,subQ2,subQ4])],"isStart":true})])],"derivedFrom":makeQuery(id+"F2.opExtrude","SWEPT_FACE",FACE,{"disambiguationData":[OSD([subQ2])]})})],"blendedInto":[makeQuery(id+"F2.boolean.opBoolean","SPLIT",FACE,{"disambiguationData":[TD([makeQuery(id+"F2.opExtrude","CAP_FACE",FACE,{"disambiguationData":[OSD([subQ1,subQ0,subQ2,subQ4])],"isStart":true})])],"derivedFrom":makeQuery(id+"F2.opExtrude","SWEPT_FACE",FACE,{"disambiguationData":[OSD([subQ2])]})})]});}
            var Q109;
            {var subQ0=sQuery(id+"F0.wireOp",EDGE,"E19.1.7.0");var subQ1=sQuery(id+"F0.wireOp",EDGE,"E4");var subQ2=sQuery(id+"F0.wireOp",EDGE,"E19.3.7.0");var subQ3=makeQuery(id+"F0.imprint","IMPRINT",EDGE,{"disambiguationData":[TD([[makeQuery(id+"F0.imprint","INTERSECT",VERTEX,{"derivedFrom":[subQ1,subQ0]}),1.0]])],"derivedFrom":subQ1});var subQ4=sQuery(id+"F0.wireOp",EDGE,"E20");Q109=makeQuery(id+"F9.opChamfer","BLEND_EDGE",EDGE,{"blendedFrom":[makeQuery(id+"F2.opExtrude","CAP_EDGE",EDGE,{"disambiguationData":[OSD([subQ1]),TDD([subQ3])],"isStart":true}),makeQuery(id+"F2.boolean.opBoolean","SPLIT",FACE,{"disambiguationData":[TD([makeQuery(id+"F2.opExtrude","CAP_FACE",FACE,{"disambiguationData":[OSD([subQ1,subQ0,subQ2,subQ4])],"isStart":true})])],"derivedFrom":makeQuery(id+"F2.opExtrude","SWEPT_FACE",FACE,{"disambiguationData":[OSD([subQ0])]})})],"blendedInto":[makeQuery(id+"F2.boolean.opBoolean","SPLIT",FACE,{"disambiguationData":[TD([makeQuery(id+"F2.opExtrude","CAP_FACE",FACE,{"disambiguationData":[OSD([subQ1,subQ0,subQ2,subQ4])],"isStart":true})])],"derivedFrom":makeQuery(id+"F2.opExtrude","SWEPT_FACE",FACE,{"disambiguationData":[OSD([subQ0])]})})]});}
            var Q110;
            {var subQ0=sQuery(id+"F0.wireOp",EDGE,"E19.1.7.0");var subQ1=sQuery(id+"F0.wireOp",EDGE,"E4");var subQ2=sQuery(id+"F0.wireOp",EDGE,"E19.3.7.0");var subQ3=sQuery(id+"F0.wireOp",EDGE,"E20");var subQ4=makeQuery(id+"F0.imprint","IMPRINT",EDGE,{"disambiguationData":[TD([[makeQuery(id+"F0.imprint","INTERSECT",VERTEX,{"derivedFrom":[subQ0,subQ3]}),1.0]])],"derivedFrom":subQ3});Q110=makeQuery(id+"F8.opChamfer","BLEND_EDGE",EDGE,{"blendedFrom":[makeQuery(id+"F2.opExtrude","CAP_EDGE",EDGE,{"disambiguationData":[OSD([subQ3]),TDD([subQ4])],"isStart":true}),makeQuery(id+"F2.boolean.opBoolean","SPLIT",FACE,{"disambiguationData":[TD([makeQuery(id+"F2.opExtrude","CAP_FACE",FACE,{"disambiguationData":[OSD([subQ1,subQ0,subQ2,subQ3])],"isStart":true})])],"derivedFrom":makeQuery(id+"F2.opExtrude","SWEPT_FACE",FACE,{"disambiguationData":[OSD([subQ0])]})})],"blendedInto":[makeQuery(id+"F2.boolean.opBoolean","SPLIT",FACE,{"disambiguationData":[TD([makeQuery(id+"F2.opExtrude","CAP_FACE",FACE,{"disambiguationData":[OSD([subQ1,subQ0,subQ2,subQ3])],"isStart":true})])],"derivedFrom":makeQuery(id+"F2.opExtrude","SWEPT_FACE",FACE,{"disambiguationData":[OSD([subQ0])]})})]});}
            var Q111;
            {var subQ0=sQuery(id+"F0.wireOp",EDGE,"E19.1.7.0");var subQ1=sQuery(id+"F0.wireOp",EDGE,"E4");var subQ2=sQuery(id+"F0.wireOp",EDGE,"E19.3.7.0");var subQ3=sQuery(id+"F0.wireOp",EDGE,"E20");var subQ4=makeQuery(id+"F0.imprint","IMPRINT",EDGE,{"disambiguationData":[TD([[makeQuery(id+"F0.imprint","INTERSECT",VERTEX,{"derivedFrom":[subQ0,subQ3]}),1.0]])],"derivedFrom":subQ3});Q111=makeQuery(id+"F8.opChamfer","BLEND_EDGE",EDGE,{"blendedFrom":[makeQuery(id+"F2.opExtrude","CAP_EDGE",EDGE,{"disambiguationData":[OSD([subQ3]),TDD([subQ4])],"isStart":true}),makeQuery(id+"F2.boolean.opBoolean","SPLIT",FACE,{"disambiguationData":[TD([makeQuery(id+"F2.opExtrude","CAP_FACE",FACE,{"disambiguationData":[OSD([subQ1,subQ0,subQ2,subQ3])],"isStart":true})])],"derivedFrom":makeQuery(id+"F2.opExtrude","SWEPT_FACE",FACE,{"disambiguationData":[OSD([subQ2])]})})],"blendedInto":[makeQuery(id+"F2.boolean.opBoolean","SPLIT",FACE,{"disambiguationData":[TD([makeQuery(id+"F2.opExtrude","CAP_FACE",FACE,{"disambiguationData":[OSD([subQ1,subQ0,subQ2,subQ3])],"isStart":true})])],"derivedFrom":makeQuery(id+"F2.opExtrude","SWEPT_FACE",FACE,{"disambiguationData":[OSD([subQ2])]})})]});}
            var Q112;
            {var subQ0=sQuery(id+"F0.wireOp",EDGE,"E20");var subQ1=sQuery(id+"F0.wireOp",EDGE,"E19.3.7.0");var subQ2=sQuery(id+"F0.wireOp",EDGE,"E19.1.7.0");var subQ3=makeQuery(id+"F0.imprint","IMPRINT",EDGE,{"disambiguationData":[TD([[makeQuery(id+"F0.imprint","INTERSECT",VERTEX,{"derivedFrom":[subQ2,subQ0]}),1.0]])],"derivedFrom":subQ0});Q112=makeQuery(id+"F8.opChamfer","BLEND_EDGE",EDGE,{"blendedFrom":[makeQuery(id+"F2.opExtrude","CAP_EDGE",EDGE,{"disambiguationData":[OSD([subQ0]),TDD([subQ3])],"isStart":true}),makeQuery(id+"F2.boolean.opBoolean","SPLIT",FACE,{"disambiguationData":[TD([makeQuery(id+"F2.opExtrude","CAP_FACE",FACE,{"disambiguationData":[OSD([sQuery(id+"F0.wireOp",EDGE,"E4"),subQ2,subQ1,subQ0])],"isStart":true})])],"derivedFrom":makeQuery(id+"F2.opExtrude","SWEPT_FACE",FACE,{"disambiguationData":[OSD([subQ0]),TDD([subQ3])]})})],"blendedInto":[makeQuery(id+"F2.boolean.opBoolean","SPLIT",FACE,{"disambiguationData":[TD([makeQuery(id+"F2.opExtrude","CAP_FACE",FACE,{"disambiguationData":[OSD([sQuery(id+"F0.wireOp",EDGE,"E4"),subQ2,subQ1,subQ0])],"isStart":true})])],"derivedFrom":makeQuery(id+"F2.opExtrude","SWEPT_FACE",FACE,{"disambiguationData":[OSD([subQ0]),TDD([subQ3])]})})]});}
            var Q113;
            {var subQ0=sQuery(id+"F0.wireOp",EDGE,"E20");var subQ1=sQuery(id+"F0.wireOp",EDGE,"E19.3.6.0");var subQ2=sQuery(id+"F0.wireOp",EDGE,"E19.1.6.0");var subQ3=makeQuery(id+"F0.imprint","IMPRINT",EDGE,{"disambiguationData":[TD([[makeQuery(id+"F0.imprint","INTERSECT",VERTEX,{"derivedFrom":[subQ2,subQ0]}),1.0]])],"derivedFrom":subQ0});Q113=makeQuery(id+"F8.opChamfer","BLEND_EDGE",EDGE,{"blendedFrom":[makeQuery(id+"F2.opExtrude","CAP_EDGE",EDGE,{"disambiguationData":[OSD([subQ0]),TDD([subQ3])],"isStart":true}),makeQuery(id+"F2.boolean.opBoolean","SPLIT",FACE,{"disambiguationData":[TD([makeQuery(id+"F2.opExtrude","CAP_FACE",FACE,{"disambiguationData":[OSD([sQuery(id+"F0.wireOp",EDGE,"E4"),subQ2,subQ1,subQ0])],"isStart":true})])],"derivedFrom":makeQuery(id+"F2.opExtrude","SWEPT_FACE",FACE,{"disambiguationData":[OSD([subQ0]),TDD([subQ3])]})})],"blendedInto":[makeQuery(id+"F2.boolean.opBoolean","SPLIT",FACE,{"disambiguationData":[TD([makeQuery(id+"F2.opExtrude","CAP_FACE",FACE,{"disambiguationData":[OSD([sQuery(id+"F0.wireOp",EDGE,"E4"),subQ2,subQ1,subQ0])],"isStart":true})])],"derivedFrom":makeQuery(id+"F2.opExtrude","SWEPT_FACE",FACE,{"disambiguationData":[OSD([subQ0]),TDD([subQ3])]})})]});}
            var Q114;
            {var subQ0=sQuery(id+"F0.wireOp",EDGE,"E19.1.6.0");var subQ1=sQuery(id+"F0.wireOp",EDGE,"E4");var subQ2=sQuery(id+"F0.wireOp",EDGE,"E19.3.6.0");var subQ3=sQuery(id+"F0.wireOp",EDGE,"E20");var subQ4=makeQuery(id+"F0.imprint","IMPRINT",EDGE,{"disambiguationData":[TD([[makeQuery(id+"F0.imprint","INTERSECT",VERTEX,{"derivedFrom":[subQ0,subQ3]}),1.0]])],"derivedFrom":subQ3});Q114=makeQuery(id+"F8.opChamfer","BLEND_EDGE",EDGE,{"blendedFrom":[makeQuery(id+"F2.opExtrude","CAP_EDGE",EDGE,{"disambiguationData":[OSD([subQ3]),TDD([subQ4])],"isStart":true}),makeQuery(id+"F2.boolean.opBoolean","SPLIT",FACE,{"disambiguationData":[TD([makeQuery(id+"F2.opExtrude","CAP_FACE",FACE,{"disambiguationData":[OSD([subQ1,subQ0,subQ2,subQ3])],"isStart":true})])],"derivedFrom":makeQuery(id+"F2.opExtrude","SWEPT_FACE",FACE,{"disambiguationData":[OSD([subQ2])]})})],"blendedInto":[makeQuery(id+"F2.boolean.opBoolean","SPLIT",FACE,{"disambiguationData":[TD([makeQuery(id+"F2.opExtrude","CAP_FACE",FACE,{"disambiguationData":[OSD([subQ1,subQ0,subQ2,subQ3])],"isStart":true})])],"derivedFrom":makeQuery(id+"F2.opExtrude","SWEPT_FACE",FACE,{"disambiguationData":[OSD([subQ2])]})})]});}
            var Q115;
            {var subQ0=sQuery(id+"F0.wireOp",EDGE,"E19.1.6.0");var subQ1=sQuery(id+"F0.wireOp",EDGE,"E4");var subQ2=sQuery(id+"F0.wireOp",EDGE,"E19.3.6.0");var subQ3=sQuery(id+"F0.wireOp",EDGE,"E20");var subQ4=makeQuery(id+"F0.imprint","IMPRINT",EDGE,{"disambiguationData":[TD([[makeQuery(id+"F0.imprint","INTERSECT",VERTEX,{"derivedFrom":[subQ0,subQ3]}),1.0]])],"derivedFrom":subQ3});Q115=makeQuery(id+"F8.opChamfer","BLEND_EDGE",EDGE,{"blendedFrom":[makeQuery(id+"F2.opExtrude","CAP_EDGE",EDGE,{"disambiguationData":[OSD([subQ3]),TDD([subQ4])],"isStart":true}),makeQuery(id+"F2.boolean.opBoolean","SPLIT",FACE,{"disambiguationData":[TD([makeQuery(id+"F2.opExtrude","CAP_FACE",FACE,{"disambiguationData":[OSD([subQ1,subQ0,subQ2,subQ3])],"isStart":true})])],"derivedFrom":makeQuery(id+"F2.opExtrude","SWEPT_FACE",FACE,{"disambiguationData":[OSD([subQ0])]})})],"blendedInto":[makeQuery(id+"F2.boolean.opBoolean","SPLIT",FACE,{"disambiguationData":[TD([makeQuery(id+"F2.opExtrude","CAP_FACE",FACE,{"disambiguationData":[OSD([subQ1,subQ0,subQ2,subQ3])],"isStart":true})])],"derivedFrom":makeQuery(id+"F2.opExtrude","SWEPT_FACE",FACE,{"disambiguationData":[OSD([subQ0])]})})]});}
            var Q116;
            {var subQ0=sQuery(id+"F0.wireOp",EDGE,"E19.1.6.0");var subQ1=sQuery(id+"F0.wireOp",EDGE,"E4");var subQ2=sQuery(id+"F0.wireOp",EDGE,"E19.3.6.0");var subQ3=makeQuery(id+"F0.imprint","IMPRINT",EDGE,{"disambiguationData":[TD([[makeQuery(id+"F0.imprint","INTERSECT",VERTEX,{"derivedFrom":[subQ1,subQ0]}),1.0]])],"derivedFrom":subQ1});var subQ4=sQuery(id+"F0.wireOp",EDGE,"E20");Q116=makeQuery(id+"F9.opChamfer","BLEND_EDGE",EDGE,{"blendedFrom":[makeQuery(id+"F2.opExtrude","CAP_EDGE",EDGE,{"disambiguationData":[OSD([subQ1]),TDD([subQ3])],"isStart":true}),makeQuery(id+"F2.boolean.opBoolean","SPLIT",FACE,{"disambiguationData":[TD([makeQuery(id+"F2.opExtrude","CAP_FACE",FACE,{"disambiguationData":[OSD([subQ1,subQ0,subQ2,subQ4])],"isStart":true})])],"derivedFrom":makeQuery(id+"F2.opExtrude","SWEPT_FACE",FACE,{"disambiguationData":[OSD([subQ2])]})})],"blendedInto":[makeQuery(id+"F2.boolean.opBoolean","SPLIT",FACE,{"disambiguationData":[TD([makeQuery(id+"F2.opExtrude","CAP_FACE",FACE,{"disambiguationData":[OSD([subQ1,subQ0,subQ2,subQ4])],"isStart":true})])],"derivedFrom":makeQuery(id+"F2.opExtrude","SWEPT_FACE",FACE,{"disambiguationData":[OSD([subQ2])]})})]});}
            var Q117;
            {var subQ0=sQuery(id+"F0.wireOp",EDGE,"E19.3.6.0");var subQ1=sQuery(id+"F0.wireOp",EDGE,"E19.1.6.0");var subQ2=sQuery(id+"F0.wireOp",EDGE,"E4");var subQ3=makeQuery(id+"F0.imprint","IMPRINT",EDGE,{"disambiguationData":[TD([[makeQuery(id+"F0.imprint","INTERSECT",VERTEX,{"derivedFrom":[subQ2,subQ1]}),1.0]])],"derivedFrom":subQ2});Q117=makeQuery(id+"F9.opChamfer","BLEND_EDGE",EDGE,{"blendedFrom":[makeQuery(id+"F2.opExtrude","CAP_EDGE",EDGE,{"disambiguationData":[OSD([subQ2]),TDD([subQ3])],"isStart":true}),makeQuery(id+"F2.boolean.opBoolean","SPLIT",FACE,{"disambiguationData":[TD([makeQuery(id+"F2.opExtrude","CAP_FACE",FACE,{"disambiguationData":[OSD([subQ2,subQ1,subQ0,sQuery(id+"F0.wireOp",EDGE,"E20")])],"isStart":true})])],"derivedFrom":makeQuery(id+"F2.opExtrude","SWEPT_FACE",FACE,{"disambiguationData":[OSD([subQ2]),TDD([subQ3])]})})],"blendedInto":[makeQuery(id+"F2.boolean.opBoolean","SPLIT",FACE,{"disambiguationData":[TD([makeQuery(id+"F2.opExtrude","CAP_FACE",FACE,{"disambiguationData":[OSD([subQ2,subQ1,subQ0,sQuery(id+"F0.wireOp",EDGE,"E20")])],"isStart":true})])],"derivedFrom":makeQuery(id+"F2.opExtrude","SWEPT_FACE",FACE,{"disambiguationData":[OSD([subQ2]),TDD([subQ3])]})})]});}
            var Q118;
            {var subQ0=sQuery(id+"F0.wireOp",EDGE,"E19.1.6.0");var subQ1=sQuery(id+"F0.wireOp",EDGE,"E4");var subQ2=sQuery(id+"F0.wireOp",EDGE,"E19.3.6.0");var subQ3=makeQuery(id+"F0.imprint","IMPRINT",EDGE,{"disambiguationData":[TD([[makeQuery(id+"F0.imprint","INTERSECT",VERTEX,{"derivedFrom":[subQ1,subQ0]}),1.0]])],"derivedFrom":subQ1});var subQ4=sQuery(id+"F0.wireOp",EDGE,"E20");Q118=makeQuery(id+"F9.opChamfer","BLEND_EDGE",EDGE,{"blendedFrom":[makeQuery(id+"F2.opExtrude","CAP_EDGE",EDGE,{"disambiguationData":[OSD([subQ1]),TDD([subQ3])],"isStart":true}),makeQuery(id+"F2.boolean.opBoolean","SPLIT",FACE,{"disambiguationData":[TD([makeQuery(id+"F2.opExtrude","CAP_FACE",FACE,{"disambiguationData":[OSD([subQ1,subQ0,subQ2,subQ4])],"isStart":true})])],"derivedFrom":makeQuery(id+"F2.opExtrude","SWEPT_FACE",FACE,{"disambiguationData":[OSD([subQ0])]})})],"blendedInto":[makeQuery(id+"F2.boolean.opBoolean","SPLIT",FACE,{"disambiguationData":[TD([makeQuery(id+"F2.opExtrude","CAP_FACE",FACE,{"disambiguationData":[OSD([subQ1,subQ0,subQ2,subQ4])],"isStart":true})])],"derivedFrom":makeQuery(id+"F2.opExtrude","SWEPT_FACE",FACE,{"disambiguationData":[OSD([subQ0])]})})]});}
            var Q119;
            {var subQ0=sQuery(id+"F0.wireOp",EDGE,"E19.3.5.0");var subQ1=sQuery(id+"F0.wireOp",EDGE,"E20");var subQ2=sQuery(id+"F0.wireOp",EDGE,"E19.1.5.0");var subQ3=makeQuery(id+"F0.imprint","IMPRINT",EDGE,{"disambiguationData":[TD([[makeQuery(id+"F0.imprint","INTERSECT",VERTEX,{"derivedFrom":[subQ2,subQ1]}),1.0]])],"derivedFrom":subQ1});Q119=makeQuery(id+"F8.opChamfer","BLEND_EDGE",EDGE,{"blendedFrom":[makeQuery(id+"F2.opExtrude","CAP_EDGE",EDGE,{"disambiguationData":[OSD([subQ1]),TDD([subQ3])],"isStart":true}),makeQuery(id+"F2.boolean.opBoolean","SPLIT",FACE,{"disambiguationData":[TD([makeQuery(id+"F2.opExtrude","CAP_FACE",FACE,{"disambiguationData":[OSD([sQuery(id+"F0.wireOp",EDGE,"E4"),subQ2,subQ0,subQ1])],"isStart":true})])],"derivedFrom":makeQuery(id+"F2.opExtrude","SWEPT_FACE",FACE,{"disambiguationData":[OSD([subQ1]),TDD([subQ3])]})})],"blendedInto":[makeQuery(id+"F2.boolean.opBoolean","SPLIT",FACE,{"disambiguationData":[TD([makeQuery(id+"F2.opExtrude","CAP_FACE",FACE,{"disambiguationData":[OSD([sQuery(id+"F0.wireOp",EDGE,"E4"),subQ2,subQ0,subQ1])],"isStart":true})])],"derivedFrom":makeQuery(id+"F2.opExtrude","SWEPT_FACE",FACE,{"disambiguationData":[OSD([subQ1]),TDD([subQ3])]})})]});}
            var Q120;
            {var subQ0=sQuery(id+"F0.wireOp",EDGE,"E19.1.5.0");var subQ1=sQuery(id+"F0.wireOp",EDGE,"E4");var subQ2=sQuery(id+"F0.wireOp",EDGE,"E19.3.5.0");var subQ3=sQuery(id+"F0.wireOp",EDGE,"E20");var subQ4=makeQuery(id+"F0.imprint","IMPRINT",EDGE,{"disambiguationData":[TD([[makeQuery(id+"F0.imprint","INTERSECT",VERTEX,{"derivedFrom":[subQ0,subQ3]}),1.0]])],"derivedFrom":subQ3});Q120=makeQuery(id+"F8.opChamfer","BLEND_EDGE",EDGE,{"blendedFrom":[makeQuery(id+"F2.opExtrude","CAP_EDGE",EDGE,{"disambiguationData":[OSD([subQ3]),TDD([subQ4])],"isStart":true}),makeQuery(id+"F2.boolean.opBoolean","SPLIT",FACE,{"disambiguationData":[TD([makeQuery(id+"F2.opExtrude","CAP_FACE",FACE,{"disambiguationData":[OSD([subQ1,subQ0,subQ2,subQ3])],"isStart":true})])],"derivedFrom":makeQuery(id+"F2.opExtrude","SWEPT_FACE",FACE,{"disambiguationData":[OSD([subQ2])]})})],"blendedInto":[makeQuery(id+"F2.boolean.opBoolean","SPLIT",FACE,{"disambiguationData":[TD([makeQuery(id+"F2.opExtrude","CAP_FACE",FACE,{"disambiguationData":[OSD([subQ1,subQ0,subQ2,subQ3])],"isStart":true})])],"derivedFrom":makeQuery(id+"F2.opExtrude","SWEPT_FACE",FACE,{"disambiguationData":[OSD([subQ2])]})})]});}
            var Q121;
            {var subQ0=sQuery(id+"F0.wireOp",EDGE,"E19.1.5.0");var subQ1=sQuery(id+"F0.wireOp",EDGE,"E4");var subQ2=sQuery(id+"F0.wireOp",EDGE,"E19.3.5.0");var subQ3=sQuery(id+"F0.wireOp",EDGE,"E20");var subQ4=makeQuery(id+"F0.imprint","IMPRINT",EDGE,{"disambiguationData":[TD([[makeQuery(id+"F0.imprint","INTERSECT",VERTEX,{"derivedFrom":[subQ0,subQ3]}),1.0]])],"derivedFrom":subQ3});Q121=makeQuery(id+"F8.opChamfer","BLEND_EDGE",EDGE,{"blendedFrom":[makeQuery(id+"F2.opExtrude","CAP_EDGE",EDGE,{"disambiguationData":[OSD([subQ3]),TDD([subQ4])],"isStart":true}),makeQuery(id+"F2.boolean.opBoolean","SPLIT",FACE,{"disambiguationData":[TD([makeQuery(id+"F2.opExtrude","CAP_FACE",FACE,{"disambiguationData":[OSD([subQ1,subQ0,subQ2,subQ3])],"isStart":true})])],"derivedFrom":makeQuery(id+"F2.opExtrude","SWEPT_FACE",FACE,{"disambiguationData":[OSD([subQ0])]})})],"blendedInto":[makeQuery(id+"F2.boolean.opBoolean","SPLIT",FACE,{"disambiguationData":[TD([makeQuery(id+"F2.opExtrude","CAP_FACE",FACE,{"disambiguationData":[OSD([subQ1,subQ0,subQ2,subQ3])],"isStart":true})])],"derivedFrom":makeQuery(id+"F2.opExtrude","SWEPT_FACE",FACE,{"disambiguationData":[OSD([subQ0])]})})]});}
            var Q122;
            {var subQ0=sQuery(id+"F0.wireOp",EDGE,"E19.1.5.0");var subQ1=sQuery(id+"F0.wireOp",EDGE,"E4");var subQ2=sQuery(id+"F0.wireOp",EDGE,"E19.3.5.0");var subQ3=makeQuery(id+"F0.imprint","IMPRINT",EDGE,{"disambiguationData":[TD([[makeQuery(id+"F0.imprint","INTERSECT",VERTEX,{"derivedFrom":[subQ1,subQ0]}),1.0]])],"derivedFrom":subQ1});var subQ4=sQuery(id+"F0.wireOp",EDGE,"E20");Q122=makeQuery(id+"F9.opChamfer","BLEND_EDGE",EDGE,{"blendedFrom":[makeQuery(id+"F2.opExtrude","CAP_EDGE",EDGE,{"disambiguationData":[OSD([subQ1]),TDD([subQ3])],"isStart":true}),makeQuery(id+"F2.boolean.opBoolean","SPLIT",FACE,{"disambiguationData":[TD([makeQuery(id+"F2.opExtrude","CAP_FACE",FACE,{"disambiguationData":[OSD([subQ1,subQ0,subQ2,subQ4])],"isStart":true})])],"derivedFrom":makeQuery(id+"F2.opExtrude","SWEPT_FACE",FACE,{"disambiguationData":[OSD([subQ2])]})})],"blendedInto":[makeQuery(id+"F2.boolean.opBoolean","SPLIT",FACE,{"disambiguationData":[TD([makeQuery(id+"F2.opExtrude","CAP_FACE",FACE,{"disambiguationData":[OSD([subQ1,subQ0,subQ2,subQ4])],"isStart":true})])],"derivedFrom":makeQuery(id+"F2.opExtrude","SWEPT_FACE",FACE,{"disambiguationData":[OSD([subQ2])]})})]});}
            var Q123;
            {var subQ0=sQuery(id+"F0.wireOp",EDGE,"E19.1.5.0");var subQ1=sQuery(id+"F0.wireOp",EDGE,"E4");var subQ2=sQuery(id+"F0.wireOp",EDGE,"E19.3.5.0");var subQ3=makeQuery(id+"F0.imprint","IMPRINT",EDGE,{"disambiguationData":[TD([[makeQuery(id+"F0.imprint","INTERSECT",VERTEX,{"derivedFrom":[subQ1,subQ0]}),1.0]])],"derivedFrom":subQ1});var subQ4=sQuery(id+"F0.wireOp",EDGE,"E20");Q123=makeQuery(id+"F9.opChamfer","BLEND_EDGE",EDGE,{"blendedFrom":[makeQuery(id+"F2.opExtrude","CAP_EDGE",EDGE,{"disambiguationData":[OSD([subQ1]),TDD([subQ3])],"isStart":true}),makeQuery(id+"F2.boolean.opBoolean","SPLIT",FACE,{"disambiguationData":[TD([makeQuery(id+"F2.opExtrude","CAP_FACE",FACE,{"disambiguationData":[OSD([subQ1,subQ0,subQ2,subQ4])],"isStart":true})])],"derivedFrom":makeQuery(id+"F2.opExtrude","SWEPT_FACE",FACE,{"disambiguationData":[OSD([subQ0])]})})],"blendedInto":[makeQuery(id+"F2.boolean.opBoolean","SPLIT",FACE,{"disambiguationData":[TD([makeQuery(id+"F2.opExtrude","CAP_FACE",FACE,{"disambiguationData":[OSD([subQ1,subQ0,subQ2,subQ4])],"isStart":true})])],"derivedFrom":makeQuery(id+"F2.opExtrude","SWEPT_FACE",FACE,{"disambiguationData":[OSD([subQ0])]})})]});}
            var Q124;
            {var subQ0=sQuery(id+"F0.wireOp",EDGE,"E19.3.5.0");var subQ1=sQuery(id+"F0.wireOp",EDGE,"E19.1.5.0");var subQ2=sQuery(id+"F0.wireOp",EDGE,"E4");var subQ3=makeQuery(id+"F0.imprint","IMPRINT",EDGE,{"disambiguationData":[TD([[makeQuery(id+"F0.imprint","INTERSECT",VERTEX,{"derivedFrom":[subQ2,subQ1]}),1.0]])],"derivedFrom":subQ2});Q124=makeQuery(id+"F9.opChamfer","BLEND_EDGE",EDGE,{"blendedFrom":[makeQuery(id+"F2.opExtrude","CAP_EDGE",EDGE,{"disambiguationData":[OSD([subQ2]),TDD([subQ3])],"isStart":true}),makeQuery(id+"F2.boolean.opBoolean","SPLIT",FACE,{"disambiguationData":[TD([makeQuery(id+"F2.opExtrude","CAP_FACE",FACE,{"disambiguationData":[OSD([subQ2,subQ1,subQ0,sQuery(id+"F0.wireOp",EDGE,"E20")])],"isStart":true})])],"derivedFrom":makeQuery(id+"F2.opExtrude","SWEPT_FACE",FACE,{"disambiguationData":[OSD([subQ2]),TDD([subQ3])]})})],"blendedInto":[makeQuery(id+"F2.boolean.opBoolean","SPLIT",FACE,{"disambiguationData":[TD([makeQuery(id+"F2.opExtrude","CAP_FACE",FACE,{"disambiguationData":[OSD([subQ2,subQ1,subQ0,sQuery(id+"F0.wireOp",EDGE,"E20")])],"isStart":true})])],"derivedFrom":makeQuery(id+"F2.opExtrude","SWEPT_FACE",FACE,{"disambiguationData":[OSD([subQ2]),TDD([subQ3])]})})]});}
            var Q125;
            {var subQ0=sQuery(id+"F0.wireOp",EDGE,"E20");var subQ1=sQuery(id+"F0.wireOp",EDGE,"E19.3.4.0");var subQ2=sQuery(id+"F0.wireOp",EDGE,"E19.1.4.0");var subQ3=makeQuery(id+"F0.imprint","IMPRINT",EDGE,{"disambiguationData":[TD([[makeQuery(id+"F0.imprint","INTERSECT",VERTEX,{"derivedFrom":[subQ2,subQ0]}),1.0]])],"derivedFrom":subQ0});Q125=makeQuery(id+"F8.opChamfer","BLEND_EDGE",EDGE,{"blendedFrom":[makeQuery(id+"F2.opExtrude","CAP_EDGE",EDGE,{"disambiguationData":[OSD([subQ0]),TDD([subQ3])],"isStart":true}),makeQuery(id+"F2.boolean.opBoolean","SPLIT",FACE,{"disambiguationData":[TD([makeQuery(id+"F2.opExtrude","CAP_FACE",FACE,{"disambiguationData":[OSD([sQuery(id+"F0.wireOp",EDGE,"E4"),subQ2,subQ1,subQ0])],"isStart":true})])],"derivedFrom":makeQuery(id+"F2.opExtrude","SWEPT_FACE",FACE,{"disambiguationData":[OSD([subQ0]),TDD([subQ3])]})})],"blendedInto":[makeQuery(id+"F2.boolean.opBoolean","SPLIT",FACE,{"disambiguationData":[TD([makeQuery(id+"F2.opExtrude","CAP_FACE",FACE,{"disambiguationData":[OSD([sQuery(id+"F0.wireOp",EDGE,"E4"),subQ2,subQ1,subQ0])],"isStart":true})])],"derivedFrom":makeQuery(id+"F2.opExtrude","SWEPT_FACE",FACE,{"disambiguationData":[OSD([subQ0]),TDD([subQ3])]})})]});}
            var Q126;
            {var subQ0=sQuery(id+"F0.wireOp",EDGE,"E20");var subQ1=sQuery(id+"F0.wireOp",EDGE,"E19.3.4.0");var subQ2=sQuery(id+"F0.wireOp",EDGE,"E19.1.4.0");var subQ3=sQuery(id+"F0.wireOp",EDGE,"E4");var subQ4=makeQuery(id+"F0.imprint","IMPRINT",EDGE,{"disambiguationData":[TD([[makeQuery(id+"F0.imprint","INTERSECT",VERTEX,{"derivedFrom":[subQ2,subQ0]}),1.0]])],"derivedFrom":subQ0});Q126=makeQuery(id+"F8.opChamfer","BLEND_EDGE",EDGE,{"blendedFrom":[makeQuery(id+"F2.opExtrude","CAP_EDGE",EDGE,{"disambiguationData":[OSD([subQ0]),TDD([subQ4])],"isStart":true}),makeQuery(id+"F2.boolean.opBoolean","SPLIT",FACE,{"disambiguationData":[TD([makeQuery(id+"F2.opExtrude","CAP_FACE",FACE,{"disambiguationData":[OSD([subQ3,subQ2,subQ1,subQ0])],"isStart":true})])],"derivedFrom":makeQuery(id+"F2.opExtrude","SWEPT_FACE",FACE,{"disambiguationData":[OSD([subQ1])]})})],"blendedInto":[makeQuery(id+"F2.boolean.opBoolean","SPLIT",FACE,{"disambiguationData":[TD([makeQuery(id+"F2.opExtrude","CAP_FACE",FACE,{"disambiguationData":[OSD([subQ3,subQ2,subQ1,subQ0])],"isStart":true})])],"derivedFrom":makeQuery(id+"F2.opExtrude","SWEPT_FACE",FACE,{"disambiguationData":[OSD([subQ1])]})})]});}
            var Q127;
            {var subQ0=sQuery(id+"F0.wireOp",EDGE,"E20");var subQ1=sQuery(id+"F0.wireOp",EDGE,"E19.3.4.0");var subQ2=sQuery(id+"F0.wireOp",EDGE,"E19.1.4.0");var subQ3=sQuery(id+"F0.wireOp",EDGE,"E4");var subQ4=makeQuery(id+"F0.imprint","IMPRINT",EDGE,{"disambiguationData":[TD([[makeQuery(id+"F0.imprint","INTERSECT",VERTEX,{"derivedFrom":[subQ2,subQ0]}),1.0]])],"derivedFrom":subQ0});Q127=makeQuery(id+"F8.opChamfer","BLEND_EDGE",EDGE,{"blendedFrom":[makeQuery(id+"F2.opExtrude","CAP_EDGE",EDGE,{"disambiguationData":[OSD([subQ0]),TDD([subQ4])],"isStart":true}),makeQuery(id+"F2.boolean.opBoolean","SPLIT",FACE,{"disambiguationData":[TD([makeQuery(id+"F2.opExtrude","CAP_FACE",FACE,{"disambiguationData":[OSD([subQ3,subQ2,subQ1,subQ0])],"isStart":true})])],"derivedFrom":makeQuery(id+"F2.opExtrude","SWEPT_FACE",FACE,{"disambiguationData":[OSD([subQ2])]})})],"blendedInto":[makeQuery(id+"F2.boolean.opBoolean","SPLIT",FACE,{"disambiguationData":[TD([makeQuery(id+"F2.opExtrude","CAP_FACE",FACE,{"disambiguationData":[OSD([subQ3,subQ2,subQ1,subQ0])],"isStart":true})])],"derivedFrom":makeQuery(id+"F2.opExtrude","SWEPT_FACE",FACE,{"disambiguationData":[OSD([subQ2])]})})]});}
            var Q128;
            {var subQ0=sQuery(id+"F0.wireOp",EDGE,"E20");var subQ1=sQuery(id+"F0.wireOp",EDGE,"E19.3.4.0");var subQ2=sQuery(id+"F0.wireOp",EDGE,"E19.1.4.0");var subQ3=sQuery(id+"F0.wireOp",EDGE,"E4");var subQ4=makeQuery(id+"F0.imprint","IMPRINT",EDGE,{"disambiguationData":[TD([[makeQuery(id+"F0.imprint","INTERSECT",VERTEX,{"derivedFrom":[subQ3,subQ2]}),1.0]])],"derivedFrom":subQ3});Q128=makeQuery(id+"F9.opChamfer","BLEND_EDGE",EDGE,{"blendedFrom":[makeQuery(id+"F2.opExtrude","CAP_EDGE",EDGE,{"disambiguationData":[OSD([subQ3]),TDD([subQ4])],"isStart":true}),makeQuery(id+"F2.boolean.opBoolean","SPLIT",FACE,{"disambiguationData":[TD([makeQuery(id+"F2.opExtrude","CAP_FACE",FACE,{"disambiguationData":[OSD([subQ3,subQ2,subQ1,subQ0])],"isStart":true})])],"derivedFrom":makeQuery(id+"F2.opExtrude","SWEPT_FACE",FACE,{"disambiguationData":[OSD([subQ1])]})})],"blendedInto":[makeQuery(id+"F2.boolean.opBoolean","SPLIT",FACE,{"disambiguationData":[TD([makeQuery(id+"F2.opExtrude","CAP_FACE",FACE,{"disambiguationData":[OSD([subQ3,subQ2,subQ1,subQ0])],"isStart":true})])],"derivedFrom":makeQuery(id+"F2.opExtrude","SWEPT_FACE",FACE,{"disambiguationData":[OSD([subQ1])]})})]});}
            var Q129;
            {var subQ0=sQuery(id+"F0.wireOp",EDGE,"E20");var subQ1=sQuery(id+"F0.wireOp",EDGE,"E19.3.4.0");var subQ2=sQuery(id+"F0.wireOp",EDGE,"E19.1.4.0");var subQ3=sQuery(id+"F0.wireOp",EDGE,"E4");var subQ4=makeQuery(id+"F0.imprint","IMPRINT",EDGE,{"disambiguationData":[TD([[makeQuery(id+"F0.imprint","INTERSECT",VERTEX,{"derivedFrom":[subQ3,subQ2]}),1.0]])],"derivedFrom":subQ3});Q129=makeQuery(id+"F9.opChamfer","BLEND_EDGE",EDGE,{"blendedFrom":[makeQuery(id+"F2.opExtrude","CAP_EDGE",EDGE,{"disambiguationData":[OSD([subQ3]),TDD([subQ4])],"isStart":true}),makeQuery(id+"F2.boolean.opBoolean","SPLIT",FACE,{"disambiguationData":[TD([makeQuery(id+"F2.opExtrude","CAP_FACE",FACE,{"disambiguationData":[OSD([subQ3,subQ2,subQ1,subQ0])],"isStart":true})])],"derivedFrom":makeQuery(id+"F2.opExtrude","SWEPT_FACE",FACE,{"disambiguationData":[OSD([subQ2])]})})],"blendedInto":[makeQuery(id+"F2.boolean.opBoolean","SPLIT",FACE,{"disambiguationData":[TD([makeQuery(id+"F2.opExtrude","CAP_FACE",FACE,{"disambiguationData":[OSD([subQ3,subQ2,subQ1,subQ0])],"isStart":true})])],"derivedFrom":makeQuery(id+"F2.opExtrude","SWEPT_FACE",FACE,{"disambiguationData":[OSD([subQ2])]})})]});}
            var Q130;
            {var subQ0=sQuery(id+"F0.wireOp",EDGE,"E19.3.4.0");var subQ1=sQuery(id+"F0.wireOp",EDGE,"E19.1.4.0");var subQ2=sQuery(id+"F0.wireOp",EDGE,"E4");var subQ3=makeQuery(id+"F0.imprint","IMPRINT",EDGE,{"disambiguationData":[TD([[makeQuery(id+"F0.imprint","INTERSECT",VERTEX,{"derivedFrom":[subQ2,subQ1]}),1.0]])],"derivedFrom":subQ2});Q130=makeQuery(id+"F9.opChamfer","BLEND_EDGE",EDGE,{"blendedFrom":[makeQuery(id+"F2.opExtrude","CAP_EDGE",EDGE,{"disambiguationData":[OSD([subQ2]),TDD([subQ3])],"isStart":true}),makeQuery(id+"F2.boolean.opBoolean","SPLIT",FACE,{"disambiguationData":[TD([makeQuery(id+"F2.opExtrude","CAP_FACE",FACE,{"disambiguationData":[OSD([subQ2,subQ1,subQ0,sQuery(id+"F0.wireOp",EDGE,"E20")])],"isStart":true})])],"derivedFrom":makeQuery(id+"F2.opExtrude","SWEPT_FACE",FACE,{"disambiguationData":[OSD([subQ2]),TDD([subQ3])]})})],"blendedInto":[makeQuery(id+"F2.boolean.opBoolean","SPLIT",FACE,{"disambiguationData":[TD([makeQuery(id+"F2.opExtrude","CAP_FACE",FACE,{"disambiguationData":[OSD([subQ2,subQ1,subQ0,sQuery(id+"F0.wireOp",EDGE,"E20")])],"isStart":true})])],"derivedFrom":makeQuery(id+"F2.opExtrude","SWEPT_FACE",FACE,{"disambiguationData":[OSD([subQ2]),TDD([subQ3])]})})]});}
            var Q131;
            {var subQ0=sQuery(id+"F0.wireOp",EDGE,"E19.1.3.0");var subQ1=sQuery(id+"F0.wireOp",EDGE,"E20");var subQ2=sQuery(id+"F0.wireOp",EDGE,"E19.3.3.0");var subQ3=makeQuery(id+"F0.imprint","IMPRINT",EDGE,{"disambiguationData":[TD([[makeQuery(id+"F0.imprint","INTERSECT",VERTEX,{"derivedFrom":[subQ0,subQ1]}),1.0]])],"derivedFrom":subQ1});Q131=makeQuery(id+"F8.opChamfer","BLEND_EDGE",EDGE,{"blendedFrom":[makeQuery(id+"F2.opExtrude","CAP_EDGE",EDGE,{"disambiguationData":[OSD([subQ1]),TDD([subQ3])],"isStart":true}),makeQuery(id+"F2.boolean.opBoolean","SPLIT",FACE,{"disambiguationData":[TD([makeQuery(id+"F2.opExtrude","CAP_FACE",FACE,{"disambiguationData":[OSD([sQuery(id+"F0.wireOp",EDGE,"E4"),subQ0,subQ2,subQ1])],"isStart":true})])],"derivedFrom":makeQuery(id+"F2.opExtrude","SWEPT_FACE",FACE,{"disambiguationData":[OSD([subQ1]),TDD([subQ3])]})})],"blendedInto":[makeQuery(id+"F2.boolean.opBoolean","SPLIT",FACE,{"disambiguationData":[TD([makeQuery(id+"F2.opExtrude","CAP_FACE",FACE,{"disambiguationData":[OSD([sQuery(id+"F0.wireOp",EDGE,"E4"),subQ0,subQ2,subQ1])],"isStart":true})])],"derivedFrom":makeQuery(id+"F2.opExtrude","SWEPT_FACE",FACE,{"disambiguationData":[OSD([subQ1]),TDD([subQ3])]})})]});}
            var Q132;
            {var subQ0=sQuery(id+"F0.wireOp",EDGE,"E19.1.3.0");var subQ1=sQuery(id+"F0.wireOp",EDGE,"E4");var subQ2=sQuery(id+"F0.wireOp",EDGE,"E19.3.3.0");var subQ3=sQuery(id+"F0.wireOp",EDGE,"E20");var subQ4=makeQuery(id+"F0.imprint","IMPRINT",EDGE,{"disambiguationData":[TD([[makeQuery(id+"F0.imprint","INTERSECT",VERTEX,{"derivedFrom":[subQ0,subQ3]}),1.0]])],"derivedFrom":subQ3});Q132=makeQuery(id+"F8.opChamfer","BLEND_EDGE",EDGE,{"blendedFrom":[makeQuery(id+"F2.opExtrude","CAP_EDGE",EDGE,{"disambiguationData":[OSD([subQ3]),TDD([subQ4])],"isStart":true}),makeQuery(id+"F2.boolean.opBoolean","SPLIT",FACE,{"disambiguationData":[TD([makeQuery(id+"F2.opExtrude","CAP_FACE",FACE,{"disambiguationData":[OSD([subQ1,subQ0,subQ2,subQ3])],"isStart":true})])],"derivedFrom":makeQuery(id+"F2.opExtrude","SWEPT_FACE",FACE,{"disambiguationData":[OSD([subQ2])]})})],"blendedInto":[makeQuery(id+"F2.boolean.opBoolean","SPLIT",FACE,{"disambiguationData":[TD([makeQuery(id+"F2.opExtrude","CAP_FACE",FACE,{"disambiguationData":[OSD([subQ1,subQ0,subQ2,subQ3])],"isStart":true})])],"derivedFrom":makeQuery(id+"F2.opExtrude","SWEPT_FACE",FACE,{"disambiguationData":[OSD([subQ2])]})})]});}
            var Q133;
            {var subQ0=sQuery(id+"F0.wireOp",EDGE,"E19.1.3.0");var subQ1=sQuery(id+"F0.wireOp",EDGE,"E4");var subQ2=sQuery(id+"F0.wireOp",EDGE,"E19.3.3.0");var subQ3=sQuery(id+"F0.wireOp",EDGE,"E20");var subQ4=makeQuery(id+"F0.imprint","IMPRINT",EDGE,{"disambiguationData":[TD([[makeQuery(id+"F0.imprint","INTERSECT",VERTEX,{"derivedFrom":[subQ0,subQ3]}),1.0]])],"derivedFrom":subQ3});Q133=makeQuery(id+"F8.opChamfer","BLEND_EDGE",EDGE,{"blendedFrom":[makeQuery(id+"F2.opExtrude","CAP_EDGE",EDGE,{"disambiguationData":[OSD([subQ3]),TDD([subQ4])],"isStart":true}),makeQuery(id+"F2.boolean.opBoolean","SPLIT",FACE,{"disambiguationData":[TD([makeQuery(id+"F2.opExtrude","CAP_FACE",FACE,{"disambiguationData":[OSD([subQ1,subQ0,subQ2,subQ3])],"isStart":true})])],"derivedFrom":makeQuery(id+"F2.opExtrude","SWEPT_FACE",FACE,{"disambiguationData":[OSD([subQ0])]})})],"blendedInto":[makeQuery(id+"F2.boolean.opBoolean","SPLIT",FACE,{"disambiguationData":[TD([makeQuery(id+"F2.opExtrude","CAP_FACE",FACE,{"disambiguationData":[OSD([subQ1,subQ0,subQ2,subQ3])],"isStart":true})])],"derivedFrom":makeQuery(id+"F2.opExtrude","SWEPT_FACE",FACE,{"disambiguationData":[OSD([subQ0])]})})]});}
            var Q134;
            {var subQ0=sQuery(id+"F0.wireOp",EDGE,"E19.1.3.0");var subQ1=sQuery(id+"F0.wireOp",EDGE,"E4");var subQ2=sQuery(id+"F0.wireOp",EDGE,"E19.3.3.0");var subQ3=makeQuery(id+"F0.imprint","IMPRINT",EDGE,{"disambiguationData":[TD([[makeQuery(id+"F0.imprint","INTERSECT",VERTEX,{"derivedFrom":[subQ1,subQ0]}),1.0]])],"derivedFrom":subQ1});var subQ4=sQuery(id+"F0.wireOp",EDGE,"E20");Q134=makeQuery(id+"F9.opChamfer","BLEND_EDGE",EDGE,{"blendedFrom":[makeQuery(id+"F2.opExtrude","CAP_EDGE",EDGE,{"disambiguationData":[OSD([subQ1]),TDD([subQ3])],"isStart":true}),makeQuery(id+"F2.boolean.opBoolean","SPLIT",FACE,{"disambiguationData":[TD([makeQuery(id+"F2.opExtrude","CAP_FACE",FACE,{"disambiguationData":[OSD([subQ1,subQ0,subQ2,subQ4])],"isStart":true})])],"derivedFrom":makeQuery(id+"F2.opExtrude","SWEPT_FACE",FACE,{"disambiguationData":[OSD([subQ2])]})})],"blendedInto":[makeQuery(id+"F2.boolean.opBoolean","SPLIT",FACE,{"disambiguationData":[TD([makeQuery(id+"F2.opExtrude","CAP_FACE",FACE,{"disambiguationData":[OSD([subQ1,subQ0,subQ2,subQ4])],"isStart":true})])],"derivedFrom":makeQuery(id+"F2.opExtrude","SWEPT_FACE",FACE,{"disambiguationData":[OSD([subQ2])]})})]});}
            var Q135;
            {var subQ0=sQuery(id+"F0.wireOp",EDGE,"E19.1.3.0");var subQ1=sQuery(id+"F0.wireOp",EDGE,"E4");var subQ2=sQuery(id+"F0.wireOp",EDGE,"E19.3.3.0");var subQ3=makeQuery(id+"F0.imprint","IMPRINT",EDGE,{"disambiguationData":[TD([[makeQuery(id+"F0.imprint","INTERSECT",VERTEX,{"derivedFrom":[subQ1,subQ0]}),1.0]])],"derivedFrom":subQ1});var subQ4=sQuery(id+"F0.wireOp",EDGE,"E20");Q135=makeQuery(id+"F9.opChamfer","BLEND_EDGE",EDGE,{"blendedFrom":[makeQuery(id+"F2.opExtrude","CAP_EDGE",EDGE,{"disambiguationData":[OSD([subQ1]),TDD([subQ3])],"isStart":true}),makeQuery(id+"F2.boolean.opBoolean","SPLIT",FACE,{"disambiguationData":[TD([makeQuery(id+"F2.opExtrude","CAP_FACE",FACE,{"disambiguationData":[OSD([subQ1,subQ0,subQ2,subQ4])],"isStart":true})])],"derivedFrom":makeQuery(id+"F2.opExtrude","SWEPT_FACE",FACE,{"disambiguationData":[OSD([subQ0])]})})],"blendedInto":[makeQuery(id+"F2.boolean.opBoolean","SPLIT",FACE,{"disambiguationData":[TD([makeQuery(id+"F2.opExtrude","CAP_FACE",FACE,{"disambiguationData":[OSD([subQ1,subQ0,subQ2,subQ4])],"isStart":true})])],"derivedFrom":makeQuery(id+"F2.opExtrude","SWEPT_FACE",FACE,{"disambiguationData":[OSD([subQ0])]})})]});}
            var Q136;
            {var subQ0=sQuery(id+"F0.wireOp",EDGE,"E19.1.3.0");var subQ1=sQuery(id+"F0.wireOp",EDGE,"E19.3.3.0");var subQ2=sQuery(id+"F0.wireOp",EDGE,"E4");var subQ3=makeQuery(id+"F0.imprint","IMPRINT",EDGE,{"disambiguationData":[TD([[makeQuery(id+"F0.imprint","INTERSECT",VERTEX,{"derivedFrom":[subQ2,subQ0]}),1.0]])],"derivedFrom":subQ2});Q136=makeQuery(id+"F9.opChamfer","BLEND_EDGE",EDGE,{"blendedFrom":[makeQuery(id+"F2.opExtrude","CAP_EDGE",EDGE,{"disambiguationData":[OSD([subQ2]),TDD([subQ3])],"isStart":true}),makeQuery(id+"F2.boolean.opBoolean","SPLIT",FACE,{"disambiguationData":[TD([makeQuery(id+"F2.opExtrude","CAP_FACE",FACE,{"disambiguationData":[OSD([subQ2,subQ0,subQ1,sQuery(id+"F0.wireOp",EDGE,"E20")])],"isStart":true})])],"derivedFrom":makeQuery(id+"F2.opExtrude","SWEPT_FACE",FACE,{"disambiguationData":[OSD([subQ2]),TDD([subQ3])]})})],"blendedInto":[makeQuery(id+"F2.boolean.opBoolean","SPLIT",FACE,{"disambiguationData":[TD([makeQuery(id+"F2.opExtrude","CAP_FACE",FACE,{"disambiguationData":[OSD([subQ2,subQ0,subQ1,sQuery(id+"F0.wireOp",EDGE,"E20")])],"isStart":true})])],"derivedFrom":makeQuery(id+"F2.opExtrude","SWEPT_FACE",FACE,{"disambiguationData":[OSD([subQ2]),TDD([subQ3])]})})]});}
            var Q137;
            {var subQ0=sQuery(id+"F0.wireOp",EDGE,"E20");var subQ1=sQuery(id+"F0.wireOp",EDGE,"E18.2.1");var subQ2=sQuery(id+"F0.wireOp",EDGE,"E18.2.0");var subQ3=makeQuery(id+"F0.imprint","IMPRINT",EDGE,{"disambiguationData":[TD([[makeQuery(id+"F0.imprint","INTERSECT",VERTEX,{"derivedFrom":[subQ2,subQ0]}),1.0]])],"derivedFrom":subQ0});Q137=makeQuery(id+"F8.opChamfer","BLEND_EDGE",EDGE,{"blendedFrom":[makeQuery(id+"F2.opExtrude","CAP_EDGE",EDGE,{"disambiguationData":[OSD([subQ0]),TDD([subQ3])],"isStart":true}),makeQuery(id+"F2.boolean.opBoolean","SPLIT",FACE,{"disambiguationData":[TD([makeQuery(id+"F2.opExtrude","CAP_FACE",FACE,{"disambiguationData":[OSD([sQuery(id+"F0.wireOp",EDGE,"E4"),subQ2,subQ1,subQ0])],"isStart":true})])],"derivedFrom":makeQuery(id+"F2.opExtrude","SWEPT_FACE",FACE,{"disambiguationData":[OSD([subQ0]),TDD([subQ3])]})})],"blendedInto":[makeQuery(id+"F2.boolean.opBoolean","SPLIT",FACE,{"disambiguationData":[TD([makeQuery(id+"F2.opExtrude","CAP_FACE",FACE,{"disambiguationData":[OSD([sQuery(id+"F0.wireOp",EDGE,"E4"),subQ2,subQ1,subQ0])],"isStart":true})])],"derivedFrom":makeQuery(id+"F2.opExtrude","SWEPT_FACE",FACE,{"disambiguationData":[OSD([subQ0]),TDD([subQ3])]})})]});}
            var Q138;
            {var subQ0=sQuery(id+"F0.wireOp",EDGE,"E18.2.0");var subQ1=sQuery(id+"F0.wireOp",EDGE,"E4");var subQ2=sQuery(id+"F0.wireOp",EDGE,"E18.2.1");var subQ3=sQuery(id+"F0.wireOp",EDGE,"E20");var subQ4=makeQuery(id+"F0.imprint","IMPRINT",EDGE,{"disambiguationData":[TD([[makeQuery(id+"F0.imprint","INTERSECT",VERTEX,{"derivedFrom":[subQ0,subQ3]}),1.0]])],"derivedFrom":subQ3});Q138=makeQuery(id+"F8.opChamfer","BLEND_EDGE",EDGE,{"blendedFrom":[makeQuery(id+"F2.opExtrude","CAP_EDGE",EDGE,{"disambiguationData":[OSD([subQ3]),TDD([subQ4])],"isStart":true}),makeQuery(id+"F2.boolean.opBoolean","SPLIT",FACE,{"disambiguationData":[TD([makeQuery(id+"F2.opExtrude","CAP_FACE",FACE,{"disambiguationData":[OSD([subQ1,subQ0,subQ2,subQ3])],"isStart":true})])],"derivedFrom":makeQuery(id+"F2.opExtrude","SWEPT_FACE",FACE,{"disambiguationData":[OSD([subQ2])]})})],"blendedInto":[makeQuery(id+"F2.boolean.opBoolean","SPLIT",FACE,{"disambiguationData":[TD([makeQuery(id+"F2.opExtrude","CAP_FACE",FACE,{"disambiguationData":[OSD([subQ1,subQ0,subQ2,subQ3])],"isStart":true})])],"derivedFrom":makeQuery(id+"F2.opExtrude","SWEPT_FACE",FACE,{"disambiguationData":[OSD([subQ2])]})})]});}
            var Q139;
            {var subQ0=sQuery(id+"F0.wireOp",EDGE,"E18.2.0");var subQ1=sQuery(id+"F0.wireOp",EDGE,"E4");var subQ2=sQuery(id+"F0.wireOp",EDGE,"E18.2.1");var subQ3=sQuery(id+"F0.wireOp",EDGE,"E20");var subQ4=makeQuery(id+"F0.imprint","IMPRINT",EDGE,{"disambiguationData":[TD([[makeQuery(id+"F0.imprint","INTERSECT",VERTEX,{"derivedFrom":[subQ0,subQ3]}),1.0]])],"derivedFrom":subQ3});Q139=makeQuery(id+"F8.opChamfer","BLEND_EDGE",EDGE,{"blendedFrom":[makeQuery(id+"F2.opExtrude","CAP_EDGE",EDGE,{"disambiguationData":[OSD([subQ3]),TDD([subQ4])],"isStart":true}),makeQuery(id+"F2.boolean.opBoolean","SPLIT",FACE,{"disambiguationData":[TD([makeQuery(id+"F2.opExtrude","CAP_FACE",FACE,{"disambiguationData":[OSD([subQ1,subQ0,subQ2,subQ3])],"isStart":true})])],"derivedFrom":makeQuery(id+"F2.opExtrude","SWEPT_FACE",FACE,{"disambiguationData":[OSD([subQ0])]})})],"blendedInto":[makeQuery(id+"F2.boolean.opBoolean","SPLIT",FACE,{"disambiguationData":[TD([makeQuery(id+"F2.opExtrude","CAP_FACE",FACE,{"disambiguationData":[OSD([subQ1,subQ0,subQ2,subQ3])],"isStart":true})])],"derivedFrom":makeQuery(id+"F2.opExtrude","SWEPT_FACE",FACE,{"disambiguationData":[OSD([subQ0])]})})]});}
            var Q140;
            {var subQ0=sQuery(id+"F0.wireOp",EDGE,"E18.2.0");var subQ1=sQuery(id+"F0.wireOp",EDGE,"E4");var subQ2=sQuery(id+"F0.wireOp",EDGE,"E18.2.1");var subQ3=makeQuery(id+"F0.imprint","IMPRINT",EDGE,{"disambiguationData":[TD([[makeQuery(id+"F0.imprint","INTERSECT",VERTEX,{"derivedFrom":[subQ1,subQ0]}),1.0]])],"derivedFrom":subQ1});var subQ4=sQuery(id+"F0.wireOp",EDGE,"E20");Q140=makeQuery(id+"F9.opChamfer","BLEND_EDGE",EDGE,{"blendedFrom":[makeQuery(id+"F2.opExtrude","CAP_EDGE",EDGE,{"disambiguationData":[OSD([subQ1]),TDD([subQ3])],"isStart":true}),makeQuery(id+"F2.boolean.opBoolean","SPLIT",FACE,{"disambiguationData":[TD([makeQuery(id+"F2.opExtrude","CAP_FACE",FACE,{"disambiguationData":[OSD([subQ1,subQ0,subQ2,subQ4])],"isStart":true})])],"derivedFrom":makeQuery(id+"F2.opExtrude","SWEPT_FACE",FACE,{"disambiguationData":[OSD([subQ2])]})})],"blendedInto":[makeQuery(id+"F2.boolean.opBoolean","SPLIT",FACE,{"disambiguationData":[TD([makeQuery(id+"F2.opExtrude","CAP_FACE",FACE,{"disambiguationData":[OSD([subQ1,subQ0,subQ2,subQ4])],"isStart":true})])],"derivedFrom":makeQuery(id+"F2.opExtrude","SWEPT_FACE",FACE,{"disambiguationData":[OSD([subQ2])]})})]});}
            var Q141;
            {var subQ0=sQuery(id+"F0.wireOp",EDGE,"E18.2.0");var subQ1=sQuery(id+"F0.wireOp",EDGE,"E4");var subQ2=sQuery(id+"F0.wireOp",EDGE,"E18.2.1");var subQ3=makeQuery(id+"F0.imprint","IMPRINT",EDGE,{"disambiguationData":[TD([[makeQuery(id+"F0.imprint","INTERSECT",VERTEX,{"derivedFrom":[subQ1,subQ0]}),1.0]])],"derivedFrom":subQ1});var subQ4=sQuery(id+"F0.wireOp",EDGE,"E20");Q141=makeQuery(id+"F9.opChamfer","BLEND_EDGE",EDGE,{"blendedFrom":[makeQuery(id+"F2.opExtrude","CAP_EDGE",EDGE,{"disambiguationData":[OSD([subQ1]),TDD([subQ3])],"isStart":true}),makeQuery(id+"F2.boolean.opBoolean","SPLIT",FACE,{"disambiguationData":[TD([makeQuery(id+"F2.opExtrude","CAP_FACE",FACE,{"disambiguationData":[OSD([subQ1,subQ0,subQ2,subQ4])],"isStart":true})])],"derivedFrom":makeQuery(id+"F2.opExtrude","SWEPT_FACE",FACE,{"disambiguationData":[OSD([subQ0])]})})],"blendedInto":[makeQuery(id+"F2.boolean.opBoolean","SPLIT",FACE,{"disambiguationData":[TD([makeQuery(id+"F2.opExtrude","CAP_FACE",FACE,{"disambiguationData":[OSD([subQ1,subQ0,subQ2,subQ4])],"isStart":true})])],"derivedFrom":makeQuery(id+"F2.opExtrude","SWEPT_FACE",FACE,{"disambiguationData":[OSD([subQ0])]})})]});}
            var Q142;
            {var subQ0=sQuery(id+"F0.wireOp",EDGE,"E18.2.1");var subQ1=sQuery(id+"F0.wireOp",EDGE,"E18.2.0");var subQ2=sQuery(id+"F0.wireOp",EDGE,"E4");var subQ3=makeQuery(id+"F0.imprint","IMPRINT",EDGE,{"disambiguationData":[TD([[makeQuery(id+"F0.imprint","INTERSECT",VERTEX,{"derivedFrom":[subQ2,subQ1]}),1.0]])],"derivedFrom":subQ2});Q142=makeQuery(id+"F9.opChamfer","BLEND_EDGE",EDGE,{"blendedFrom":[makeQuery(id+"F2.opExtrude","CAP_EDGE",EDGE,{"disambiguationData":[OSD([subQ2]),TDD([subQ3])],"isStart":true}),makeQuery(id+"F2.boolean.opBoolean","SPLIT",FACE,{"disambiguationData":[TD([makeQuery(id+"F2.opExtrude","CAP_FACE",FACE,{"disambiguationData":[OSD([subQ2,subQ1,subQ0,sQuery(id+"F0.wireOp",EDGE,"E20")])],"isStart":true})])],"derivedFrom":makeQuery(id+"F2.opExtrude","SWEPT_FACE",FACE,{"disambiguationData":[OSD([subQ2]),TDD([subQ3])]})})],"blendedInto":[makeQuery(id+"F2.boolean.opBoolean","SPLIT",FACE,{"disambiguationData":[TD([makeQuery(id+"F2.opExtrude","CAP_FACE",FACE,{"disambiguationData":[OSD([subQ2,subQ1,subQ0,sQuery(id+"F0.wireOp",EDGE,"E20")])],"isStart":true})])],"derivedFrom":makeQuery(id+"F2.opExtrude","SWEPT_FACE",FACE,{"disambiguationData":[OSD([subQ2]),TDD([subQ3])]})})]});}
            var Q143;
            {var subQ0=sQuery(id+"F0.wireOp",EDGE,"E20");var subQ1=sQuery(id+"F0.wireOp",EDGE,"E18.1.1");var subQ2=sQuery(id+"F0.wireOp",EDGE,"E18.1.0");var subQ3=makeQuery(id+"F0.imprint","IMPRINT",EDGE,{"disambiguationData":[TD([[makeQuery(id+"F0.imprint","INTERSECT",VERTEX,{"derivedFrom":[subQ2,subQ0]}),1.0]])],"derivedFrom":subQ0});Q143=makeQuery(id+"F8.opChamfer","BLEND_EDGE",EDGE,{"blendedFrom":[makeQuery(id+"F2.opExtrude","CAP_EDGE",EDGE,{"disambiguationData":[OSD([subQ0]),TDD([subQ3])],"isStart":true}),makeQuery(id+"F2.boolean.opBoolean","SPLIT",FACE,{"disambiguationData":[TD([makeQuery(id+"F2.opExtrude","CAP_FACE",FACE,{"disambiguationData":[OSD([sQuery(id+"F0.wireOp",EDGE,"E4"),subQ2,subQ1,subQ0])],"isStart":true})])],"derivedFrom":makeQuery(id+"F2.opExtrude","SWEPT_FACE",FACE,{"disambiguationData":[OSD([subQ0]),TDD([subQ3])]})})],"blendedInto":[makeQuery(id+"F2.boolean.opBoolean","SPLIT",FACE,{"disambiguationData":[TD([makeQuery(id+"F2.opExtrude","CAP_FACE",FACE,{"disambiguationData":[OSD([sQuery(id+"F0.wireOp",EDGE,"E4"),subQ2,subQ1,subQ0])],"isStart":true})])],"derivedFrom":makeQuery(id+"F2.opExtrude","SWEPT_FACE",FACE,{"disambiguationData":[OSD([subQ0]),TDD([subQ3])]})})]});}
            var Q144;
            {var subQ0=sQuery(id+"F0.wireOp",EDGE,"E18.1.0");var subQ1=sQuery(id+"F0.wireOp",EDGE,"E4");var subQ2=sQuery(id+"F0.wireOp",EDGE,"E18.1.1");var subQ3=sQuery(id+"F0.wireOp",EDGE,"E20");var subQ4=makeQuery(id+"F0.imprint","IMPRINT",EDGE,{"disambiguationData":[TD([[makeQuery(id+"F0.imprint","INTERSECT",VERTEX,{"derivedFrom":[subQ0,subQ3]}),1.0]])],"derivedFrom":subQ3});Q144=makeQuery(id+"F8.opChamfer","BLEND_EDGE",EDGE,{"blendedFrom":[makeQuery(id+"F2.opExtrude","CAP_EDGE",EDGE,{"disambiguationData":[OSD([subQ3]),TDD([subQ4])],"isStart":true}),makeQuery(id+"F2.boolean.opBoolean","SPLIT",FACE,{"disambiguationData":[TD([makeQuery(id+"F2.opExtrude","CAP_FACE",FACE,{"disambiguationData":[OSD([subQ1,subQ0,subQ2,subQ3])],"isStart":true})])],"derivedFrom":makeQuery(id+"F2.opExtrude","SWEPT_FACE",FACE,{"disambiguationData":[OSD([subQ2])]})})],"blendedInto":[makeQuery(id+"F2.boolean.opBoolean","SPLIT",FACE,{"disambiguationData":[TD([makeQuery(id+"F2.opExtrude","CAP_FACE",FACE,{"disambiguationData":[OSD([subQ1,subQ0,subQ2,subQ3])],"isStart":true})])],"derivedFrom":makeQuery(id+"F2.opExtrude","SWEPT_FACE",FACE,{"disambiguationData":[OSD([subQ2])]})})]});}
            var Q145;
            {var subQ0=sQuery(id+"F0.wireOp",EDGE,"E18.1.0");var subQ1=sQuery(id+"F0.wireOp",EDGE,"E4");var subQ2=sQuery(id+"F0.wireOp",EDGE,"E18.1.1");var subQ3=sQuery(id+"F0.wireOp",EDGE,"E20");var subQ4=makeQuery(id+"F0.imprint","IMPRINT",EDGE,{"disambiguationData":[TD([[makeQuery(id+"F0.imprint","INTERSECT",VERTEX,{"derivedFrom":[subQ0,subQ3]}),1.0]])],"derivedFrom":subQ3});Q145=makeQuery(id+"F8.opChamfer","BLEND_EDGE",EDGE,{"blendedFrom":[makeQuery(id+"F2.opExtrude","CAP_EDGE",EDGE,{"disambiguationData":[OSD([subQ3]),TDD([subQ4])],"isStart":true}),makeQuery(id+"F2.boolean.opBoolean","SPLIT",FACE,{"disambiguationData":[TD([makeQuery(id+"F2.opExtrude","CAP_FACE",FACE,{"disambiguationData":[OSD([subQ1,subQ0,subQ2,subQ3])],"isStart":true})])],"derivedFrom":makeQuery(id+"F2.opExtrude","SWEPT_FACE",FACE,{"disambiguationData":[OSD([subQ0])]})})],"blendedInto":[makeQuery(id+"F2.boolean.opBoolean","SPLIT",FACE,{"disambiguationData":[TD([makeQuery(id+"F2.opExtrude","CAP_FACE",FACE,{"disambiguationData":[OSD([subQ1,subQ0,subQ2,subQ3])],"isStart":true})])],"derivedFrom":makeQuery(id+"F2.opExtrude","SWEPT_FACE",FACE,{"disambiguationData":[OSD([subQ0])]})})]});}
            var Q146;
            {var subQ0=sQuery(id+"F0.wireOp",EDGE,"E18.1.0");var subQ1=sQuery(id+"F0.wireOp",EDGE,"E4");var subQ2=sQuery(id+"F0.wireOp",EDGE,"E18.1.1");var subQ3=makeQuery(id+"F0.imprint","IMPRINT",EDGE,{"disambiguationData":[TD([[makeQuery(id+"F0.imprint","INTERSECT",VERTEX,{"derivedFrom":[subQ1,subQ0]}),1.0]])],"derivedFrom":subQ1});var subQ4=sQuery(id+"F0.wireOp",EDGE,"E20");Q146=makeQuery(id+"F9.opChamfer","BLEND_EDGE",EDGE,{"blendedFrom":[makeQuery(id+"F2.opExtrude","CAP_EDGE",EDGE,{"disambiguationData":[OSD([subQ1]),TDD([subQ3])],"isStart":true}),makeQuery(id+"F2.boolean.opBoolean","SPLIT",FACE,{"disambiguationData":[TD([makeQuery(id+"F2.opExtrude","CAP_FACE",FACE,{"disambiguationData":[OSD([subQ1,subQ0,subQ2,subQ4])],"isStart":true})])],"derivedFrom":makeQuery(id+"F2.opExtrude","SWEPT_FACE",FACE,{"disambiguationData":[OSD([subQ2])]})})],"blendedInto":[makeQuery(id+"F2.boolean.opBoolean","SPLIT",FACE,{"disambiguationData":[TD([makeQuery(id+"F2.opExtrude","CAP_FACE",FACE,{"disambiguationData":[OSD([subQ1,subQ0,subQ2,subQ4])],"isStart":true})])],"derivedFrom":makeQuery(id+"F2.opExtrude","SWEPT_FACE",FACE,{"disambiguationData":[OSD([subQ2])]})})]});}
            var Q147;
            {var subQ0=sQuery(id+"F0.wireOp",EDGE,"E18.1.0");var subQ1=sQuery(id+"F0.wireOp",EDGE,"E4");var subQ2=sQuery(id+"F0.wireOp",EDGE,"E18.1.1");var subQ3=makeQuery(id+"F0.imprint","IMPRINT",EDGE,{"disambiguationData":[TD([[makeQuery(id+"F0.imprint","INTERSECT",VERTEX,{"derivedFrom":[subQ1,subQ0]}),1.0]])],"derivedFrom":subQ1});var subQ4=sQuery(id+"F0.wireOp",EDGE,"E20");Q147=makeQuery(id+"F9.opChamfer","BLEND_EDGE",EDGE,{"blendedFrom":[makeQuery(id+"F2.opExtrude","CAP_EDGE",EDGE,{"disambiguationData":[OSD([subQ1]),TDD([subQ3])],"isStart":true}),makeQuery(id+"F2.boolean.opBoolean","SPLIT",FACE,{"disambiguationData":[TD([makeQuery(id+"F2.opExtrude","CAP_FACE",FACE,{"disambiguationData":[OSD([subQ1,subQ0,subQ2,subQ4])],"isStart":true})])],"derivedFrom":makeQuery(id+"F2.opExtrude","SWEPT_FACE",FACE,{"disambiguationData":[OSD([subQ0])]})})],"blendedInto":[makeQuery(id+"F2.boolean.opBoolean","SPLIT",FACE,{"disambiguationData":[TD([makeQuery(id+"F2.opExtrude","CAP_FACE",FACE,{"disambiguationData":[OSD([subQ1,subQ0,subQ2,subQ4])],"isStart":true})])],"derivedFrom":makeQuery(id+"F2.opExtrude","SWEPT_FACE",FACE,{"disambiguationData":[OSD([subQ0])]})})]});}
            var Q148;
            {var subQ0=sQuery(id+"F0.wireOp",EDGE,"E18.1.1");var subQ1=sQuery(id+"F0.wireOp",EDGE,"E18.1.0");var subQ2=sQuery(id+"F0.wireOp",EDGE,"E4");var subQ3=makeQuery(id+"F0.imprint","IMPRINT",EDGE,{"disambiguationData":[TD([[makeQuery(id+"F0.imprint","INTERSECT",VERTEX,{"derivedFrom":[subQ2,subQ1]}),1.0]])],"derivedFrom":subQ2});Q148=makeQuery(id+"F9.opChamfer","BLEND_EDGE",EDGE,{"blendedFrom":[makeQuery(id+"F2.opExtrude","CAP_EDGE",EDGE,{"disambiguationData":[OSD([subQ2]),TDD([subQ3])],"isStart":true}),makeQuery(id+"F2.boolean.opBoolean","SPLIT",FACE,{"disambiguationData":[TD([makeQuery(id+"F2.opExtrude","CAP_FACE",FACE,{"disambiguationData":[OSD([subQ2,subQ1,subQ0,sQuery(id+"F0.wireOp",EDGE,"E20")])],"isStart":true})])],"derivedFrom":makeQuery(id+"F2.opExtrude","SWEPT_FACE",FACE,{"disambiguationData":[OSD([subQ2]),TDD([subQ3])]})})],"blendedInto":[makeQuery(id+"F2.boolean.opBoolean","SPLIT",FACE,{"disambiguationData":[TD([makeQuery(id+"F2.opExtrude","CAP_FACE",FACE,{"disambiguationData":[OSD([subQ2,subQ1,subQ0,sQuery(id+"F0.wireOp",EDGE,"E20")])],"isStart":true})])],"derivedFrom":makeQuery(id+"F2.opExtrude","SWEPT_FACE",FACE,{"disambiguationData":[OSD([subQ2]),TDD([subQ3])]})})]});}
            var Q149;
            {var subQ0=sQuery(id+"F0.wireOp",EDGE,"E17");var subQ1=sQuery(id+"F0.wireOp",EDGE,"E20");var subQ2=sQuery(id+"F0.wireOp",EDGE,"E16");var subQ3=makeQuery(id+"F0.imprint","IMPRINT",EDGE,{"disambiguationData":[TD([[makeQuery(id+"F0.imprint","INTERSECT",VERTEX,{"derivedFrom":[subQ2,subQ1]}),1.0]])],"derivedFrom":subQ1});Q149=makeQuery(id+"F8.opChamfer","BLEND_EDGE",EDGE,{"blendedFrom":[makeQuery(id+"F2.opExtrude","CAP_EDGE",EDGE,{"disambiguationData":[OSD([subQ1]),TDD([subQ3])],"isStart":true}),makeQuery(id+"F2.boolean.opBoolean","SPLIT",FACE,{"disambiguationData":[TD([makeQuery(id+"F2.opExtrude","CAP_FACE",FACE,{"disambiguationData":[OSD([sQuery(id+"F0.wireOp",EDGE,"E4"),subQ2,subQ0,subQ1])],"isStart":true})])],"derivedFrom":makeQuery(id+"F2.opExtrude","SWEPT_FACE",FACE,{"disambiguationData":[OSD([subQ1]),TDD([subQ3])]})})],"blendedInto":[makeQuery(id+"F2.boolean.opBoolean","SPLIT",FACE,{"disambiguationData":[TD([makeQuery(id+"F2.opExtrude","CAP_FACE",FACE,{"disambiguationData":[OSD([sQuery(id+"F0.wireOp",EDGE,"E4"),subQ2,subQ0,subQ1])],"isStart":true})])],"derivedFrom":makeQuery(id+"F2.opExtrude","SWEPT_FACE",FACE,{"disambiguationData":[OSD([subQ1]),TDD([subQ3])]})})]});}
            var Q150;
            {var subQ0=sQuery(id+"F0.wireOp",EDGE,"E16");var subQ1=sQuery(id+"F0.wireOp",EDGE,"E4");var subQ2=sQuery(id+"F0.wireOp",EDGE,"E17");var subQ3=sQuery(id+"F0.wireOp",EDGE,"E20");var subQ4=makeQuery(id+"F0.imprint","IMPRINT",EDGE,{"disambiguationData":[TD([[makeQuery(id+"F0.imprint","INTERSECT",VERTEX,{"derivedFrom":[subQ0,subQ3]}),1.0]])],"derivedFrom":subQ3});Q150=makeQuery(id+"F8.opChamfer","BLEND_EDGE",EDGE,{"blendedFrom":[makeQuery(id+"F2.opExtrude","CAP_EDGE",EDGE,{"disambiguationData":[OSD([subQ3]),TDD([subQ4])],"isStart":true}),makeQuery(id+"F2.boolean.opBoolean","SPLIT",FACE,{"disambiguationData":[TD([makeQuery(id+"F2.opExtrude","CAP_FACE",FACE,{"disambiguationData":[OSD([subQ1,subQ0,subQ2,subQ3])],"isStart":true})])],"derivedFrom":makeQuery(id+"F2.opExtrude","SWEPT_FACE",FACE,{"disambiguationData":[OSD([subQ2])]})})],"blendedInto":[makeQuery(id+"F2.boolean.opBoolean","SPLIT",FACE,{"disambiguationData":[TD([makeQuery(id+"F2.opExtrude","CAP_FACE",FACE,{"disambiguationData":[OSD([subQ1,subQ0,subQ2,subQ3])],"isStart":true})])],"derivedFrom":makeQuery(id+"F2.opExtrude","SWEPT_FACE",FACE,{"disambiguationData":[OSD([subQ2])]})})]});}
            var Q151;
            {var subQ0=sQuery(id+"F0.wireOp",EDGE,"E16");var subQ1=sQuery(id+"F0.wireOp",EDGE,"E4");var subQ2=sQuery(id+"F0.wireOp",EDGE,"E17");var subQ3=sQuery(id+"F0.wireOp",EDGE,"E20");var subQ4=makeQuery(id+"F0.imprint","IMPRINT",EDGE,{"disambiguationData":[TD([[makeQuery(id+"F0.imprint","INTERSECT",VERTEX,{"derivedFrom":[subQ0,subQ3]}),1.0]])],"derivedFrom":subQ3});Q151=makeQuery(id+"F8.opChamfer","BLEND_EDGE",EDGE,{"blendedFrom":[makeQuery(id+"F2.opExtrude","CAP_EDGE",EDGE,{"disambiguationData":[OSD([subQ3]),TDD([subQ4])],"isStart":true}),makeQuery(id+"F2.boolean.opBoolean","SPLIT",FACE,{"disambiguationData":[TD([makeQuery(id+"F2.opExtrude","CAP_FACE",FACE,{"disambiguationData":[OSD([subQ1,subQ0,subQ2,subQ3])],"isStart":true})])],"derivedFrom":makeQuery(id+"F2.opExtrude","SWEPT_FACE",FACE,{"disambiguationData":[OSD([subQ0])]})})],"blendedInto":[makeQuery(id+"F2.boolean.opBoolean","SPLIT",FACE,{"disambiguationData":[TD([makeQuery(id+"F2.opExtrude","CAP_FACE",FACE,{"disambiguationData":[OSD([subQ1,subQ0,subQ2,subQ3])],"isStart":true})])],"derivedFrom":makeQuery(id+"F2.opExtrude","SWEPT_FACE",FACE,{"disambiguationData":[OSD([subQ0])]})})]});}
            var Q152;
            {var subQ0=sQuery(id+"F0.wireOp",EDGE,"E16");var subQ1=sQuery(id+"F0.wireOp",EDGE,"E4");var subQ2=sQuery(id+"F0.wireOp",EDGE,"E17");var subQ3=makeQuery(id+"F0.imprint","IMPRINT",EDGE,{"disambiguationData":[TD([[makeQuery(id+"F0.imprint","INTERSECT",VERTEX,{"derivedFrom":[subQ1,subQ0]}),1.0]])],"derivedFrom":subQ1});var subQ4=sQuery(id+"F0.wireOp",EDGE,"E20");Q152=makeQuery(id+"F9.opChamfer","BLEND_EDGE",EDGE,{"blendedFrom":[makeQuery(id+"F2.opExtrude","CAP_EDGE",EDGE,{"disambiguationData":[OSD([subQ1]),TDD([subQ3])],"isStart":true}),makeQuery(id+"F2.boolean.opBoolean","SPLIT",FACE,{"disambiguationData":[TD([makeQuery(id+"F2.opExtrude","CAP_FACE",FACE,{"disambiguationData":[OSD([subQ1,subQ0,subQ2,subQ4])],"isStart":true})])],"derivedFrom":makeQuery(id+"F2.opExtrude","SWEPT_FACE",FACE,{"disambiguationData":[OSD([subQ2])]})})],"blendedInto":[makeQuery(id+"F2.boolean.opBoolean","SPLIT",FACE,{"disambiguationData":[TD([makeQuery(id+"F2.opExtrude","CAP_FACE",FACE,{"disambiguationData":[OSD([subQ1,subQ0,subQ2,subQ4])],"isStart":true})])],"derivedFrom":makeQuery(id+"F2.opExtrude","SWEPT_FACE",FACE,{"disambiguationData":[OSD([subQ2])]})})]});}
            var Q153;
            {var subQ0=sQuery(id+"F0.wireOp",EDGE,"E16");var subQ1=sQuery(id+"F0.wireOp",EDGE,"E4");var subQ2=sQuery(id+"F0.wireOp",EDGE,"E17");var subQ3=makeQuery(id+"F0.imprint","IMPRINT",EDGE,{"disambiguationData":[TD([[makeQuery(id+"F0.imprint","INTERSECT",VERTEX,{"derivedFrom":[subQ1,subQ0]}),1.0]])],"derivedFrom":subQ1});var subQ4=sQuery(id+"F0.wireOp",EDGE,"E20");Q153=makeQuery(id+"F9.opChamfer","BLEND_EDGE",EDGE,{"blendedFrom":[makeQuery(id+"F2.opExtrude","CAP_EDGE",EDGE,{"disambiguationData":[OSD([subQ1]),TDD([subQ3])],"isStart":true}),makeQuery(id+"F2.boolean.opBoolean","SPLIT",FACE,{"disambiguationData":[TD([makeQuery(id+"F2.opExtrude","CAP_FACE",FACE,{"disambiguationData":[OSD([subQ1,subQ0,subQ2,subQ4])],"isStart":true})])],"derivedFrom":makeQuery(id+"F2.opExtrude","SWEPT_FACE",FACE,{"disambiguationData":[OSD([subQ0])]})})],"blendedInto":[makeQuery(id+"F2.boolean.opBoolean","SPLIT",FACE,{"disambiguationData":[TD([makeQuery(id+"F2.opExtrude","CAP_FACE",FACE,{"disambiguationData":[OSD([subQ1,subQ0,subQ2,subQ4])],"isStart":true})])],"derivedFrom":makeQuery(id+"F2.opExtrude","SWEPT_FACE",FACE,{"disambiguationData":[OSD([subQ0])]})})]});}
            var Q154;
            {var subQ0=sQuery(id+"F0.wireOp",EDGE,"E17");var subQ1=sQuery(id+"F0.wireOp",EDGE,"E16");var subQ2=sQuery(id+"F0.wireOp",EDGE,"E4");var subQ3=makeQuery(id+"F0.imprint","IMPRINT",EDGE,{"disambiguationData":[TD([[makeQuery(id+"F0.imprint","INTERSECT",VERTEX,{"derivedFrom":[subQ2,subQ1]}),1.0]])],"derivedFrom":subQ2});Q154=makeQuery(id+"F9.opChamfer","BLEND_EDGE",EDGE,{"blendedFrom":[makeQuery(id+"F2.opExtrude","CAP_EDGE",EDGE,{"disambiguationData":[OSD([subQ2]),TDD([subQ3])],"isStart":true}),makeQuery(id+"F2.boolean.opBoolean","SPLIT",FACE,{"disambiguationData":[TD([makeQuery(id+"F2.opExtrude","CAP_FACE",FACE,{"disambiguationData":[OSD([subQ2,subQ1,subQ0,sQuery(id+"F0.wireOp",EDGE,"E20")])],"isStart":true})])],"derivedFrom":makeQuery(id+"F2.opExtrude","SWEPT_FACE",FACE,{"disambiguationData":[OSD([subQ2]),TDD([subQ3])]})})],"blendedInto":[makeQuery(id+"F2.boolean.opBoolean","SPLIT",FACE,{"disambiguationData":[TD([makeQuery(id+"F2.opExtrude","CAP_FACE",FACE,{"disambiguationData":[OSD([subQ2,subQ1,subQ0,sQuery(id+"F0.wireOp",EDGE,"E20")])],"isStart":true})])],"derivedFrom":makeQuery(id+"F2.opExtrude","SWEPT_FACE",FACE,{"disambiguationData":[OSD([subQ2]),TDD([subQ3])]})})]});}
            var Q155;
            {var subQ0=sQuery(id+"F0.wireOp",EDGE,"E20");var subQ1=sQuery(id+"F0.wireOp",EDGE,"E19.3.9.0");var subQ2=sQuery(id+"F0.wireOp",EDGE,"E19.1.9.0");var subQ3=sQuery(id+"F0.wireOp",EDGE,"E4");var subQ4=makeQuery(id+"F0.imprint","IMPRINT",EDGE,{"disambiguationData":[TD([[makeQuery(id+"F0.imprint","INTERSECT",VERTEX,{"derivedFrom":[subQ3,subQ2]}),1.0]])],"derivedFrom":subQ3});Q155=makeQuery(id+"F9.opChamfer","BLEND_EDGE",EDGE,{"blendedFrom":[makeQuery(id+"F2.opExtrude","CAP_EDGE",EDGE,{"disambiguationData":[OSD([subQ3]),TDD([subQ4])],"isStart":true}),makeQuery(id+"F2.boolean.opBoolean","SPLIT",FACE,{"disambiguationData":[TD([makeQuery(id+"F2.opExtrude","CAP_FACE",FACE,{"disambiguationData":[OSD([subQ3,subQ2,subQ1,subQ0])],"isStart":true})])],"derivedFrom":makeQuery(id+"F2.opExtrude","SWEPT_FACE",FACE,{"disambiguationData":[OSD([subQ2])]})})],"blendedInto":[makeQuery(id+"F2.boolean.opBoolean","SPLIT",FACE,{"disambiguationData":[TD([makeQuery(id+"F2.opExtrude","CAP_FACE",FACE,{"disambiguationData":[OSD([subQ3,subQ2,subQ1,subQ0])],"isStart":true})])],"derivedFrom":makeQuery(id+"F2.opExtrude","SWEPT_FACE",FACE,{"disambiguationData":[OSD([subQ2])]})})]});}
            var Q156;
            {var subQ0=sQuery(id+"F0.wireOp",EDGE,"E20");var subQ1=sQuery(id+"F0.wireOp",EDGE,"E19.3.9.0");var subQ2=sQuery(id+"F0.wireOp",EDGE,"E19.1.9.0");var subQ3=sQuery(id+"F0.wireOp",EDGE,"E4");var subQ4=makeQuery(id+"F0.imprint","IMPRINT",EDGE,{"disambiguationData":[TD([[makeQuery(id+"F0.imprint","INTERSECT",VERTEX,{"derivedFrom":[subQ2,subQ0]}),1.0]])],"derivedFrom":subQ0});Q156=makeQuery(id+"F8.opChamfer","BLEND_EDGE",EDGE,{"blendedFrom":[makeQuery(id+"F2.opExtrude","CAP_EDGE",EDGE,{"disambiguationData":[OSD([subQ0]),TDD([subQ4])],"isStart":true}),makeQuery(id+"F2.boolean.opBoolean","SPLIT",FACE,{"disambiguationData":[TD([makeQuery(id+"F2.opExtrude","CAP_FACE",FACE,{"disambiguationData":[OSD([subQ3,subQ2,subQ1,subQ0])],"isStart":true})])],"derivedFrom":makeQuery(id+"F2.opExtrude","SWEPT_FACE",FACE,{"disambiguationData":[OSD([subQ2])]})})],"blendedInto":[makeQuery(id+"F2.boolean.opBoolean","SPLIT",FACE,{"disambiguationData":[TD([makeQuery(id+"F2.opExtrude","CAP_FACE",FACE,{"disambiguationData":[OSD([subQ3,subQ2,subQ1,subQ0])],"isStart":true})])],"derivedFrom":makeQuery(id+"F2.opExtrude","SWEPT_FACE",FACE,{"disambiguationData":[OSD([subQ2])]})})]});}
            var Q157;
            {var subQ0=sQuery(id+"F0.wireOp",EDGE,"E20");var subQ1=sQuery(id+"F0.wireOp",EDGE,"E19.3.9.0");var subQ2=sQuery(id+"F0.wireOp",EDGE,"E19.1.9.0");var subQ3=sQuery(id+"F0.wireOp",EDGE,"E4");var subQ4=makeQuery(id+"F0.imprint","IMPRINT",EDGE,{"disambiguationData":[TD([[makeQuery(id+"F0.imprint","INTERSECT",VERTEX,{"derivedFrom":[subQ2,subQ0]}),1.0]])],"derivedFrom":subQ0});Q157=makeQuery(id+"F8.opChamfer","BLEND_EDGE",EDGE,{"blendedFrom":[makeQuery(id+"F2.opExtrude","CAP_EDGE",EDGE,{"disambiguationData":[OSD([subQ0]),TDD([subQ4])],"isStart":true}),makeQuery(id+"F2.boolean.opBoolean","SPLIT",FACE,{"disambiguationData":[TD([makeQuery(id+"F2.opExtrude","CAP_FACE",FACE,{"disambiguationData":[OSD([subQ3,subQ2,subQ1,subQ0])],"isStart":true})])],"derivedFrom":makeQuery(id+"F2.opExtrude","SWEPT_FACE",FACE,{"disambiguationData":[OSD([subQ1])]})})],"blendedInto":[makeQuery(id+"F2.boolean.opBoolean","SPLIT",FACE,{"disambiguationData":[TD([makeQuery(id+"F2.opExtrude","CAP_FACE",FACE,{"disambiguationData":[OSD([subQ3,subQ2,subQ1,subQ0])],"isStart":true})])],"derivedFrom":makeQuery(id+"F2.opExtrude","SWEPT_FACE",FACE,{"disambiguationData":[OSD([subQ1])]})})]});}
            var Q158;
            {var subQ0=sQuery(id+"F0.wireOp",EDGE,"E20");var subQ1=sQuery(id+"F0.wireOp",EDGE,"E19.3.9.0");var subQ2=sQuery(id+"F0.wireOp",EDGE,"E19.1.9.0");var subQ3=sQuery(id+"F0.wireOp",EDGE,"E4");var subQ4=makeQuery(id+"F0.imprint","IMPRINT",EDGE,{"disambiguationData":[TD([[makeQuery(id+"F0.imprint","INTERSECT",VERTEX,{"derivedFrom":[subQ3,subQ2]}),1.0]])],"derivedFrom":subQ3});Q158=makeQuery(id+"F9.opChamfer","BLEND_EDGE",EDGE,{"blendedFrom":[makeQuery(id+"F2.opExtrude","CAP_EDGE",EDGE,{"disambiguationData":[OSD([subQ3]),TDD([subQ4])],"isStart":true}),makeQuery(id+"F2.boolean.opBoolean","SPLIT",FACE,{"disambiguationData":[TD([makeQuery(id+"F2.opExtrude","CAP_FACE",FACE,{"disambiguationData":[OSD([subQ3,subQ2,subQ1,subQ0])],"isStart":true})])],"derivedFrom":makeQuery(id+"F2.opExtrude","SWEPT_FACE",FACE,{"disambiguationData":[OSD([subQ1])]})})],"blendedInto":[makeQuery(id+"F2.boolean.opBoolean","SPLIT",FACE,{"disambiguationData":[TD([makeQuery(id+"F2.opExtrude","CAP_FACE",FACE,{"disambiguationData":[OSD([subQ3,subQ2,subQ1,subQ0])],"isStart":true})])],"derivedFrom":makeQuery(id+"F2.opExtrude","SWEPT_FACE",FACE,{"disambiguationData":[OSD([subQ1])]})})]});}
            fillet(context, id + "F10", {"entities" : qUnion([Q0, Q1, Q2, Q3, Q4, Q5, Q6, Q7, Q8, Q9, Q10, Q11, Q12, Q13, Q14, Q15, Q16, Q17, Q18, Q19, Q20, Q21, Q22, Q23, Q24, Q25, Q26, Q27, Q28, Q29, Q30, Q31, Q32, Q33, Q34, Q35, Q36, Q37, Q38, Q39, Q40, Q41, Q42, Q43, Q44, Q45, Q46, Q47, Q48, Q49, Q50, Q51, Q52, Q53, Q54, Q55, Q56, Q57, Q58, Q59, Q60, Q61, Q62, Q63, Q64, Q65, Q66, Q67, Q68, Q69, Q70, Q71, Q72, Q73, Q74, Q75, Q76, Q77, Q78, Q79, Q80, Q81, Q82, Q83, Q84, Q85, Q86, Q87, Q88, Q89, Q90, Q91, Q92, Q93, Q94, Q95, Q96, Q97, Q98, Q99, Q100, Q101, Q102, Q103, Q104, Q105, Q106, Q107, Q108, Q109, Q110, Q111, Q112, Q113, Q114, Q115, Q116, Q117, Q118, Q119, Q120, Q121, Q122, Q123, Q124, Q125, Q126, Q127, Q128, Q129, Q130, Q131, Q132, Q133, Q134, Q135, Q136, Q137, Q138, Q139, Q140, Q141, Q142, Q143, Q144, Q145, Q146, Q147, Q148, Q149, Q150, Q151, Q152, Q153, Q154, Q155, Q156, Q157, Q158]), "radius" : 0.45 * mm, "tangentPropagation" : true, "allowEdgeOverflow" : false});
        }
        {
            var Q0;
            {var subQ0=sQuery(id+"F0.wireOp",EDGE,"E20");var subQ1=sQuery(id+"F0.wireOp",EDGE,"E16");var subQ3=sQuery(id+"F0.wireOp",EDGE,"E4");Q0=makeQuery(id+"F7.opChamfer","BLEND_EDGE",EDGE,{"blendedFrom":[makeQuery(id+"F2.opExtrude","CAP_EDGE",EDGE,{"disambiguationData":[OSD([subQ3]),TDD([makeQuery(id+"F0.imprint","IMPRINT",EDGE,{"disambiguationData":[TD([[makeQuery(id+"F0.imprint","INTERSECT",VERTEX,{"derivedFrom":[subQ3,subQ1]}),1.0]])],"derivedFrom":subQ3})])],"isStart":false}),makeQuery(id+"F2.opExtrude","CAP_EDGE",EDGE,{"disambiguationData":[OSD([subQ0]),TDD([makeQuery(id+"F0.imprint","IMPRINT",EDGE,{"disambiguationData":[TD([[makeQuery(id+"F0.imprint","INTERSECT",VERTEX,{"derivedFrom":[subQ1,subQ0]}),1.0]])],"derivedFrom":subQ0})])],"isStart":false})],"blendedInto":[]});}
            var Q1;
            {var subQ0=sQuery(id+"F0.wireOp",EDGE,"E18.1.0");var subQ1=sQuery(id+"F0.wireOp",EDGE,"E4");var subQ3=sQuery(id+"F0.wireOp",EDGE,"E20");Q1=makeQuery(id+"F9.opChamfer","BLEND_EDGE",EDGE,{"blendedFrom":[makeQuery(id+"F2.opExtrude","CAP_EDGE",EDGE,{"disambiguationData":[OSD([subQ3]),TDD([makeQuery(id+"F0.imprint","IMPRINT",EDGE,{"disambiguationData":[TD([[makeQuery(id+"F0.imprint","INTERSECT",VERTEX,{"derivedFrom":[subQ0,subQ3]}),1.0]])],"derivedFrom":subQ3})])],"isStart":false}),makeQuery(id+"F8.opChamfer","BLEND_FACE",FACE,{"disambiguationData":[OSD([subQ1]),TDD([makeQuery(id+"F2.opExtrude","CAP_EDGE",EDGE,{"disambiguationData":[OSD([subQ1]),TDD([makeQuery(id+"F0.imprint","IMPRINT",EDGE,{"disambiguationData":[TD([[makeQuery(id+"F0.imprint","INTERSECT",VERTEX,{"derivedFrom":[subQ1,subQ0]}),1.0]])],"derivedFrom":subQ1})])],"isStart":false})])]})],"blendedInto":[makeQuery(id+"F8.opChamfer","BLEND_FACE",FACE,{"disambiguationData":[OSD([subQ1]),TDD([makeQuery(id+"F2.opExtrude","CAP_EDGE",EDGE,{"disambiguationData":[OSD([subQ1]),TDD([makeQuery(id+"F0.imprint","IMPRINT",EDGE,{"disambiguationData":[TD([[makeQuery(id+"F0.imprint","INTERSECT",VERTEX,{"derivedFrom":[subQ1,subQ0]}),1.0]])],"derivedFrom":subQ1})])],"isStart":false})])]})]});}
            var Q2;
            {var subQ0=sQuery(id+"F0.wireOp",EDGE,"E18.2.0");var subQ1=sQuery(id+"F0.wireOp",EDGE,"E4");var subQ3=sQuery(id+"F0.wireOp",EDGE,"E20");Q2=makeQuery(id+"F9.opChamfer","BLEND_EDGE",EDGE,{"blendedFrom":[makeQuery(id+"F2.opExtrude","CAP_EDGE",EDGE,{"disambiguationData":[OSD([subQ3]),TDD([makeQuery(id+"F0.imprint","IMPRINT",EDGE,{"disambiguationData":[TD([[makeQuery(id+"F0.imprint","INTERSECT",VERTEX,{"derivedFrom":[subQ0,subQ3]}),1.0]])],"derivedFrom":subQ3})])],"isStart":false}),makeQuery(id+"F8.opChamfer","BLEND_FACE",FACE,{"disambiguationData":[OSD([subQ1]),TDD([makeQuery(id+"F2.opExtrude","CAP_EDGE",EDGE,{"disambiguationData":[OSD([subQ1]),TDD([makeQuery(id+"F0.imprint","IMPRINT",EDGE,{"disambiguationData":[TD([[makeQuery(id+"F0.imprint","INTERSECT",VERTEX,{"derivedFrom":[subQ1,subQ0]}),1.0]])],"derivedFrom":subQ1})])],"isStart":false})])]})],"blendedInto":[makeQuery(id+"F8.opChamfer","BLEND_FACE",FACE,{"disambiguationData":[OSD([subQ1]),TDD([makeQuery(id+"F2.opExtrude","CAP_EDGE",EDGE,{"disambiguationData":[OSD([subQ1]),TDD([makeQuery(id+"F0.imprint","IMPRINT",EDGE,{"disambiguationData":[TD([[makeQuery(id+"F0.imprint","INTERSECT",VERTEX,{"derivedFrom":[subQ1,subQ0]}),1.0]])],"derivedFrom":subQ1})])],"isStart":false})])]})]});}
            var Q3;
            {var subQ0=sQuery(id+"F0.wireOp",EDGE,"E19.1.3.0");var subQ1=sQuery(id+"F0.wireOp",EDGE,"E4");var subQ3=sQuery(id+"F0.wireOp",EDGE,"E20");Q3=makeQuery(id+"F9.opChamfer","BLEND_EDGE",EDGE,{"blendedFrom":[makeQuery(id+"F2.opExtrude","CAP_EDGE",EDGE,{"disambiguationData":[OSD([subQ3]),TDD([makeQuery(id+"F0.imprint","IMPRINT",EDGE,{"disambiguationData":[TD([[makeQuery(id+"F0.imprint","INTERSECT",VERTEX,{"derivedFrom":[subQ0,subQ3]}),1.0]])],"derivedFrom":subQ3})])],"isStart":false}),makeQuery(id+"F8.opChamfer","BLEND_FACE",FACE,{"disambiguationData":[OSD([subQ1]),TDD([makeQuery(id+"F2.opExtrude","CAP_EDGE",EDGE,{"disambiguationData":[OSD([subQ1]),TDD([makeQuery(id+"F0.imprint","IMPRINT",EDGE,{"disambiguationData":[TD([[makeQuery(id+"F0.imprint","INTERSECT",VERTEX,{"derivedFrom":[subQ1,subQ0]}),1.0]])],"derivedFrom":subQ1})])],"isStart":false})])]})],"blendedInto":[makeQuery(id+"F8.opChamfer","BLEND_FACE",FACE,{"disambiguationData":[OSD([subQ1]),TDD([makeQuery(id+"F2.opExtrude","CAP_EDGE",EDGE,{"disambiguationData":[OSD([subQ1]),TDD([makeQuery(id+"F0.imprint","IMPRINT",EDGE,{"disambiguationData":[TD([[makeQuery(id+"F0.imprint","INTERSECT",VERTEX,{"derivedFrom":[subQ1,subQ0]}),1.0]])],"derivedFrom":subQ1})])],"isStart":false})])]})]});}
            var Q4;
            {var subQ0=sQuery(id+"F0.wireOp",EDGE,"E19.1.4.0");var subQ1=sQuery(id+"F0.wireOp",EDGE,"E4");var subQ3=sQuery(id+"F0.wireOp",EDGE,"E20");Q4=makeQuery(id+"F9.opChamfer","BLEND_EDGE",EDGE,{"blendedFrom":[makeQuery(id+"F2.opExtrude","CAP_EDGE",EDGE,{"disambiguationData":[OSD([subQ3]),TDD([makeQuery(id+"F0.imprint","IMPRINT",EDGE,{"disambiguationData":[TD([[makeQuery(id+"F0.imprint","INTERSECT",VERTEX,{"derivedFrom":[subQ0,subQ3]}),1.0]])],"derivedFrom":subQ3})])],"isStart":false}),makeQuery(id+"F8.opChamfer","BLEND_FACE",FACE,{"disambiguationData":[OSD([subQ1]),TDD([makeQuery(id+"F2.opExtrude","CAP_EDGE",EDGE,{"disambiguationData":[OSD([subQ1]),TDD([makeQuery(id+"F0.imprint","IMPRINT",EDGE,{"disambiguationData":[TD([[makeQuery(id+"F0.imprint","INTERSECT",VERTEX,{"derivedFrom":[subQ1,subQ0]}),1.0]])],"derivedFrom":subQ1})])],"isStart":false})])]})],"blendedInto":[makeQuery(id+"F8.opChamfer","BLEND_FACE",FACE,{"disambiguationData":[OSD([subQ1]),TDD([makeQuery(id+"F2.opExtrude","CAP_EDGE",EDGE,{"disambiguationData":[OSD([subQ1]),TDD([makeQuery(id+"F0.imprint","IMPRINT",EDGE,{"disambiguationData":[TD([[makeQuery(id+"F0.imprint","INTERSECT",VERTEX,{"derivedFrom":[subQ1,subQ0]}),1.0]])],"derivedFrom":subQ1})])],"isStart":false})])]})]});}
            var Q5;
            {var subQ0=sQuery(id+"F0.wireOp",EDGE,"E19.1.5.0");var subQ1=sQuery(id+"F0.wireOp",EDGE,"E4");var subQ3=sQuery(id+"F0.wireOp",EDGE,"E20");Q5=makeQuery(id+"F9.opChamfer","BLEND_EDGE",EDGE,{"blendedFrom":[makeQuery(id+"F2.opExtrude","CAP_EDGE",EDGE,{"disambiguationData":[OSD([subQ3]),TDD([makeQuery(id+"F0.imprint","IMPRINT",EDGE,{"disambiguationData":[TD([[makeQuery(id+"F0.imprint","INTERSECT",VERTEX,{"derivedFrom":[subQ0,subQ3]}),1.0]])],"derivedFrom":subQ3})])],"isStart":false}),makeQuery(id+"F8.opChamfer","BLEND_FACE",FACE,{"disambiguationData":[OSD([subQ1]),TDD([makeQuery(id+"F2.opExtrude","CAP_EDGE",EDGE,{"disambiguationData":[OSD([subQ1]),TDD([makeQuery(id+"F0.imprint","IMPRINT",EDGE,{"disambiguationData":[TD([[makeQuery(id+"F0.imprint","INTERSECT",VERTEX,{"derivedFrom":[subQ1,subQ0]}),1.0]])],"derivedFrom":subQ1})])],"isStart":false})])]})],"blendedInto":[makeQuery(id+"F8.opChamfer","BLEND_FACE",FACE,{"disambiguationData":[OSD([subQ1]),TDD([makeQuery(id+"F2.opExtrude","CAP_EDGE",EDGE,{"disambiguationData":[OSD([subQ1]),TDD([makeQuery(id+"F0.imprint","IMPRINT",EDGE,{"disambiguationData":[TD([[makeQuery(id+"F0.imprint","INTERSECT",VERTEX,{"derivedFrom":[subQ1,subQ0]}),1.0]])],"derivedFrom":subQ1})])],"isStart":false})])]})]});}
            var Q6;
            {var subQ0=sQuery(id+"F0.wireOp",EDGE,"E19.1.6.0");var subQ1=sQuery(id+"F0.wireOp",EDGE,"E4");var subQ3=sQuery(id+"F0.wireOp",EDGE,"E20");Q6=makeQuery(id+"F9.opChamfer","BLEND_EDGE",EDGE,{"blendedFrom":[makeQuery(id+"F2.opExtrude","CAP_EDGE",EDGE,{"disambiguationData":[OSD([subQ3]),TDD([makeQuery(id+"F0.imprint","IMPRINT",EDGE,{"disambiguationData":[TD([[makeQuery(id+"F0.imprint","INTERSECT",VERTEX,{"derivedFrom":[subQ0,subQ3]}),1.0]])],"derivedFrom":subQ3})])],"isStart":false}),makeQuery(id+"F8.opChamfer","BLEND_FACE",FACE,{"disambiguationData":[OSD([subQ1]),TDD([makeQuery(id+"F2.opExtrude","CAP_EDGE",EDGE,{"disambiguationData":[OSD([subQ1]),TDD([makeQuery(id+"F0.imprint","IMPRINT",EDGE,{"disambiguationData":[TD([[makeQuery(id+"F0.imprint","INTERSECT",VERTEX,{"derivedFrom":[subQ1,subQ0]}),1.0]])],"derivedFrom":subQ1})])],"isStart":false})])]})],"blendedInto":[makeQuery(id+"F8.opChamfer","BLEND_FACE",FACE,{"disambiguationData":[OSD([subQ1]),TDD([makeQuery(id+"F2.opExtrude","CAP_EDGE",EDGE,{"disambiguationData":[OSD([subQ1]),TDD([makeQuery(id+"F0.imprint","IMPRINT",EDGE,{"disambiguationData":[TD([[makeQuery(id+"F0.imprint","INTERSECT",VERTEX,{"derivedFrom":[subQ1,subQ0]}),1.0]])],"derivedFrom":subQ1})])],"isStart":false})])]})]});}
            var Q7;
            {var subQ0=sQuery(id+"F0.wireOp",EDGE,"E19.1.7.0");var subQ1=sQuery(id+"F0.wireOp",EDGE,"E4");var subQ3=sQuery(id+"F0.wireOp",EDGE,"E20");Q7=makeQuery(id+"F9.opChamfer","BLEND_EDGE",EDGE,{"blendedFrom":[makeQuery(id+"F2.opExtrude","CAP_EDGE",EDGE,{"disambiguationData":[OSD([subQ3]),TDD([makeQuery(id+"F0.imprint","IMPRINT",EDGE,{"disambiguationData":[TD([[makeQuery(id+"F0.imprint","INTERSECT",VERTEX,{"derivedFrom":[subQ0,subQ3]}),1.0]])],"derivedFrom":subQ3})])],"isStart":false}),makeQuery(id+"F8.opChamfer","BLEND_FACE",FACE,{"disambiguationData":[OSD([subQ1]),TDD([makeQuery(id+"F2.opExtrude","CAP_EDGE",EDGE,{"disambiguationData":[OSD([subQ1]),TDD([makeQuery(id+"F0.imprint","IMPRINT",EDGE,{"disambiguationData":[TD([[makeQuery(id+"F0.imprint","INTERSECT",VERTEX,{"derivedFrom":[subQ1,subQ0]}),1.0]])],"derivedFrom":subQ1})])],"isStart":false})])]})],"blendedInto":[makeQuery(id+"F8.opChamfer","BLEND_FACE",FACE,{"disambiguationData":[OSD([subQ1]),TDD([makeQuery(id+"F2.opExtrude","CAP_EDGE",EDGE,{"disambiguationData":[OSD([subQ1]),TDD([makeQuery(id+"F0.imprint","IMPRINT",EDGE,{"disambiguationData":[TD([[makeQuery(id+"F0.imprint","INTERSECT",VERTEX,{"derivedFrom":[subQ1,subQ0]}),1.0]])],"derivedFrom":subQ1})])],"isStart":false})])]})]});}
            var Q8;
            {var subQ0=sQuery(id+"F0.wireOp",EDGE,"E19.1.8.0");var subQ1=sQuery(id+"F0.wireOp",EDGE,"E4");var subQ3=sQuery(id+"F0.wireOp",EDGE,"E20");Q8=makeQuery(id+"F9.opChamfer","BLEND_EDGE",EDGE,{"blendedFrom":[makeQuery(id+"F2.opExtrude","CAP_EDGE",EDGE,{"disambiguationData":[OSD([subQ3]),TDD([makeQuery(id+"F0.imprint","IMPRINT",EDGE,{"disambiguationData":[TD([[makeQuery(id+"F0.imprint","INTERSECT",VERTEX,{"derivedFrom":[subQ0,subQ3]}),1.0]])],"derivedFrom":subQ3})])],"isStart":false}),makeQuery(id+"F8.opChamfer","BLEND_FACE",FACE,{"disambiguationData":[OSD([subQ1]),TDD([makeQuery(id+"F2.opExtrude","CAP_EDGE",EDGE,{"disambiguationData":[OSD([subQ1]),TDD([makeQuery(id+"F0.imprint","IMPRINT",EDGE,{"disambiguationData":[TD([[makeQuery(id+"F0.imprint","INTERSECT",VERTEX,{"derivedFrom":[subQ1,subQ0]}),1.0]])],"derivedFrom":subQ1})])],"isStart":false})])]})],"blendedInto":[makeQuery(id+"F8.opChamfer","BLEND_FACE",FACE,{"disambiguationData":[OSD([subQ1]),TDD([makeQuery(id+"F2.opExtrude","CAP_EDGE",EDGE,{"disambiguationData":[OSD([subQ1]),TDD([makeQuery(id+"F0.imprint","IMPRINT",EDGE,{"disambiguationData":[TD([[makeQuery(id+"F0.imprint","INTERSECT",VERTEX,{"derivedFrom":[subQ1,subQ0]}),1.0]])],"derivedFrom":subQ1})])],"isStart":false})])]})]});}
            var Q9;
            {var subQ0=sQuery(id+"F0.wireOp",EDGE,"E19.1.9.0");var subQ1=sQuery(id+"F0.wireOp",EDGE,"E4");var subQ3=sQuery(id+"F0.wireOp",EDGE,"E20");Q9=makeQuery(id+"F9.opChamfer","BLEND_EDGE",EDGE,{"blendedFrom":[makeQuery(id+"F2.opExtrude","CAP_EDGE",EDGE,{"disambiguationData":[OSD([subQ3]),TDD([makeQuery(id+"F0.imprint","IMPRINT",EDGE,{"disambiguationData":[TD([[makeQuery(id+"F0.imprint","INTERSECT",VERTEX,{"derivedFrom":[subQ0,subQ3]}),1.0]])],"derivedFrom":subQ3})])],"isStart":false}),makeQuery(id+"F8.opChamfer","BLEND_FACE",FACE,{"disambiguationData":[OSD([subQ1]),TDD([makeQuery(id+"F2.opExtrude","CAP_EDGE",EDGE,{"disambiguationData":[OSD([subQ1]),TDD([makeQuery(id+"F0.imprint","IMPRINT",EDGE,{"disambiguationData":[TD([[makeQuery(id+"F0.imprint","INTERSECT",VERTEX,{"derivedFrom":[subQ1,subQ0]}),1.0]])],"derivedFrom":subQ1})])],"isStart":false})])]})],"blendedInto":[makeQuery(id+"F8.opChamfer","BLEND_FACE",FACE,{"disambiguationData":[OSD([subQ1]),TDD([makeQuery(id+"F2.opExtrude","CAP_EDGE",EDGE,{"disambiguationData":[OSD([subQ1]),TDD([makeQuery(id+"F0.imprint","IMPRINT",EDGE,{"disambiguationData":[TD([[makeQuery(id+"F0.imprint","INTERSECT",VERTEX,{"derivedFrom":[subQ1,subQ0]}),1.0]])],"derivedFrom":subQ1})])],"isStart":false})])]})]});}
            var Q10;
            {var subQ0=sQuery(id+"F0.wireOp",EDGE,"E19.1.10.0");var subQ1=sQuery(id+"F0.wireOp",EDGE,"E4");var subQ3=sQuery(id+"F0.wireOp",EDGE,"E20");Q10=makeQuery(id+"F9.opChamfer","BLEND_EDGE",EDGE,{"blendedFrom":[makeQuery(id+"F2.opExtrude","CAP_EDGE",EDGE,{"disambiguationData":[OSD([subQ3]),TDD([makeQuery(id+"F0.imprint","IMPRINT",EDGE,{"disambiguationData":[TD([[makeQuery(id+"F0.imprint","INTERSECT",VERTEX,{"derivedFrom":[subQ0,subQ3]}),1.0]])],"derivedFrom":subQ3})])],"isStart":false}),makeQuery(id+"F8.opChamfer","BLEND_FACE",FACE,{"disambiguationData":[OSD([subQ1]),TDD([makeQuery(id+"F2.opExtrude","CAP_EDGE",EDGE,{"disambiguationData":[OSD([subQ1]),TDD([makeQuery(id+"F0.imprint","IMPRINT",EDGE,{"disambiguationData":[TD([[makeQuery(id+"F0.imprint","INTERSECT",VERTEX,{"derivedFrom":[subQ1,subQ0]}),1.0]])],"derivedFrom":subQ1})])],"isStart":false})])]})],"blendedInto":[makeQuery(id+"F8.opChamfer","BLEND_FACE",FACE,{"disambiguationData":[OSD([subQ1]),TDD([makeQuery(id+"F2.opExtrude","CAP_EDGE",EDGE,{"disambiguationData":[OSD([subQ1]),TDD([makeQuery(id+"F0.imprint","IMPRINT",EDGE,{"disambiguationData":[TD([[makeQuery(id+"F0.imprint","INTERSECT",VERTEX,{"derivedFrom":[subQ1,subQ0]}),1.0]])],"derivedFrom":subQ1})])],"isStart":false})])]})]});}
            var Q11;
            {var subQ0=sQuery(id+"F0.wireOp",EDGE,"E19.1.11.0");var subQ1=sQuery(id+"F0.wireOp",EDGE,"E4");var subQ3=sQuery(id+"F0.wireOp",EDGE,"E20");Q11=makeQuery(id+"F9.opChamfer","BLEND_EDGE",EDGE,{"blendedFrom":[makeQuery(id+"F2.opExtrude","CAP_EDGE",EDGE,{"disambiguationData":[OSD([subQ3]),TDD([makeQuery(id+"F0.imprint","IMPRINT",EDGE,{"disambiguationData":[TD([[makeQuery(id+"F0.imprint","INTERSECT",VERTEX,{"derivedFrom":[subQ0,subQ3]}),1.0]])],"derivedFrom":subQ3})])],"isStart":false}),makeQuery(id+"F8.opChamfer","BLEND_FACE",FACE,{"disambiguationData":[OSD([subQ1]),TDD([makeQuery(id+"F2.opExtrude","CAP_EDGE",EDGE,{"disambiguationData":[OSD([subQ1]),TDD([makeQuery(id+"F0.imprint","IMPRINT",EDGE,{"disambiguationData":[TD([[makeQuery(id+"F0.imprint","INTERSECT",VERTEX,{"derivedFrom":[subQ1,subQ0]}),1.0]])],"derivedFrom":subQ1})])],"isStart":false})])]})],"blendedInto":[makeQuery(id+"F8.opChamfer","BLEND_FACE",FACE,{"disambiguationData":[OSD([subQ1]),TDD([makeQuery(id+"F2.opExtrude","CAP_EDGE",EDGE,{"disambiguationData":[OSD([subQ1]),TDD([makeQuery(id+"F0.imprint","IMPRINT",EDGE,{"disambiguationData":[TD([[makeQuery(id+"F0.imprint","INTERSECT",VERTEX,{"derivedFrom":[subQ1,subQ0]}),1.0]])],"derivedFrom":subQ1})])],"isStart":false})])]})]});}
            var Q12;
            {var subQ0=sQuery(id+"F0.wireOp",EDGE,"E19.1.12.0");var subQ1=sQuery(id+"F0.wireOp",EDGE,"E4");var subQ3=sQuery(id+"F0.wireOp",EDGE,"E20");Q12=makeQuery(id+"F9.opChamfer","BLEND_EDGE",EDGE,{"blendedFrom":[makeQuery(id+"F2.opExtrude","CAP_EDGE",EDGE,{"disambiguationData":[OSD([subQ3]),TDD([makeQuery(id+"F0.imprint","IMPRINT",EDGE,{"disambiguationData":[TD([[makeQuery(id+"F0.imprint","INTERSECT",VERTEX,{"derivedFrom":[subQ0,subQ3]}),1.0]])],"derivedFrom":subQ3})])],"isStart":false}),makeQuery(id+"F8.opChamfer","BLEND_FACE",FACE,{"disambiguationData":[OSD([subQ1]),TDD([makeQuery(id+"F2.opExtrude","CAP_EDGE",EDGE,{"disambiguationData":[OSD([subQ1]),TDD([makeQuery(id+"F0.imprint","IMPRINT",EDGE,{"disambiguationData":[TD([[makeQuery(id+"F0.imprint","INTERSECT",VERTEX,{"derivedFrom":[subQ1,subQ0]}),1.0]])],"derivedFrom":subQ1})])],"isStart":false})])]})],"blendedInto":[makeQuery(id+"F8.opChamfer","BLEND_FACE",FACE,{"disambiguationData":[OSD([subQ1]),TDD([makeQuery(id+"F2.opExtrude","CAP_EDGE",EDGE,{"disambiguationData":[OSD([subQ1]),TDD([makeQuery(id+"F0.imprint","IMPRINT",EDGE,{"disambiguationData":[TD([[makeQuery(id+"F0.imprint","INTERSECT",VERTEX,{"derivedFrom":[subQ1,subQ0]}),1.0]])],"derivedFrom":subQ1})])],"isStart":false})])]})]});}
            var Q13;
            {var subQ0=sQuery(id+"F0.wireOp",EDGE,"E20");var subQ1=sQuery(id+"F0.wireOp",EDGE,"E19.1.12.0");var subQ3=sQuery(id+"F0.wireOp",EDGE,"E4");Q13=makeQuery(id+"F9.opChamfer","BLEND_EDGE",EDGE,{"blendedFrom":[makeQuery(id+"F2.opExtrude","CAP_EDGE",EDGE,{"disambiguationData":[OSD([subQ3]),TDD([makeQuery(id+"F0.imprint","IMPRINT",EDGE,{"disambiguationData":[TD([[makeQuery(id+"F0.imprint","INTERSECT",VERTEX,{"derivedFrom":[subQ3,subQ1]}),1.0]])],"derivedFrom":subQ3})])],"isStart":true}),makeQuery(id+"F8.opChamfer","BLEND_FACE",FACE,{"disambiguationData":[OSD([subQ0]),TDD([makeQuery(id+"F2.opExtrude","CAP_EDGE",EDGE,{"disambiguationData":[OSD([subQ0]),TDD([makeQuery(id+"F0.imprint","IMPRINT",EDGE,{"disambiguationData":[TD([[makeQuery(id+"F0.imprint","INTERSECT",VERTEX,{"derivedFrom":[subQ1,subQ0]}),1.0]])],"derivedFrom":subQ0})])],"isStart":true})])]})],"blendedInto":[makeQuery(id+"F8.opChamfer","BLEND_FACE",FACE,{"disambiguationData":[OSD([subQ0]),TDD([makeQuery(id+"F2.opExtrude","CAP_EDGE",EDGE,{"disambiguationData":[OSD([subQ0]),TDD([makeQuery(id+"F0.imprint","IMPRINT",EDGE,{"disambiguationData":[TD([[makeQuery(id+"F0.imprint","INTERSECT",VERTEX,{"derivedFrom":[subQ1,subQ0]}),1.0]])],"derivedFrom":subQ0})])],"isStart":true})])]})]});}
            var Q14;
            {var subQ0=sQuery(id+"F0.wireOp",EDGE,"E20");var subQ1=sQuery(id+"F0.wireOp",EDGE,"E19.1.11.0");var subQ3=sQuery(id+"F0.wireOp",EDGE,"E4");Q14=makeQuery(id+"F9.opChamfer","BLEND_EDGE",EDGE,{"blendedFrom":[makeQuery(id+"F2.opExtrude","CAP_EDGE",EDGE,{"disambiguationData":[OSD([subQ3]),TDD([makeQuery(id+"F0.imprint","IMPRINT",EDGE,{"disambiguationData":[TD([[makeQuery(id+"F0.imprint","INTERSECT",VERTEX,{"derivedFrom":[subQ3,subQ1]}),1.0]])],"derivedFrom":subQ3})])],"isStart":true}),makeQuery(id+"F8.opChamfer","BLEND_FACE",FACE,{"disambiguationData":[OSD([subQ0]),TDD([makeQuery(id+"F2.opExtrude","CAP_EDGE",EDGE,{"disambiguationData":[OSD([subQ0]),TDD([makeQuery(id+"F0.imprint","IMPRINT",EDGE,{"disambiguationData":[TD([[makeQuery(id+"F0.imprint","INTERSECT",VERTEX,{"derivedFrom":[subQ1,subQ0]}),1.0]])],"derivedFrom":subQ0})])],"isStart":true})])]})],"blendedInto":[makeQuery(id+"F8.opChamfer","BLEND_FACE",FACE,{"disambiguationData":[OSD([subQ0]),TDD([makeQuery(id+"F2.opExtrude","CAP_EDGE",EDGE,{"disambiguationData":[OSD([subQ0]),TDD([makeQuery(id+"F0.imprint","IMPRINT",EDGE,{"disambiguationData":[TD([[makeQuery(id+"F0.imprint","INTERSECT",VERTEX,{"derivedFrom":[subQ1,subQ0]}),1.0]])],"derivedFrom":subQ0})])],"isStart":true})])]})]});}
            var Q15;
            {var subQ0=sQuery(id+"F0.wireOp",EDGE,"E20");var subQ1=sQuery(id+"F0.wireOp",EDGE,"E19.1.10.0");var subQ3=sQuery(id+"F0.wireOp",EDGE,"E4");Q15=makeQuery(id+"F9.opChamfer","BLEND_EDGE",EDGE,{"blendedFrom":[makeQuery(id+"F2.opExtrude","CAP_EDGE",EDGE,{"disambiguationData":[OSD([subQ3]),TDD([makeQuery(id+"F0.imprint","IMPRINT",EDGE,{"disambiguationData":[TD([[makeQuery(id+"F0.imprint","INTERSECT",VERTEX,{"derivedFrom":[subQ3,subQ1]}),1.0]])],"derivedFrom":subQ3})])],"isStart":true}),makeQuery(id+"F8.opChamfer","BLEND_FACE",FACE,{"disambiguationData":[OSD([subQ0]),TDD([makeQuery(id+"F2.opExtrude","CAP_EDGE",EDGE,{"disambiguationData":[OSD([subQ0]),TDD([makeQuery(id+"F0.imprint","IMPRINT",EDGE,{"disambiguationData":[TD([[makeQuery(id+"F0.imprint","INTERSECT",VERTEX,{"derivedFrom":[subQ1,subQ0]}),1.0]])],"derivedFrom":subQ0})])],"isStart":true})])]})],"blendedInto":[makeQuery(id+"F8.opChamfer","BLEND_FACE",FACE,{"disambiguationData":[OSD([subQ0]),TDD([makeQuery(id+"F2.opExtrude","CAP_EDGE",EDGE,{"disambiguationData":[OSD([subQ0]),TDD([makeQuery(id+"F0.imprint","IMPRINT",EDGE,{"disambiguationData":[TD([[makeQuery(id+"F0.imprint","INTERSECT",VERTEX,{"derivedFrom":[subQ1,subQ0]}),1.0]])],"derivedFrom":subQ0})])],"isStart":true})])]})]});}
            var Q16;
            {var subQ0=sQuery(id+"F0.wireOp",EDGE,"E20");var subQ1=sQuery(id+"F0.wireOp",EDGE,"E19.1.8.0");var subQ3=sQuery(id+"F0.wireOp",EDGE,"E4");Q16=makeQuery(id+"F9.opChamfer","BLEND_EDGE",EDGE,{"blendedFrom":[makeQuery(id+"F2.opExtrude","CAP_EDGE",EDGE,{"disambiguationData":[OSD([subQ3]),TDD([makeQuery(id+"F0.imprint","IMPRINT",EDGE,{"disambiguationData":[TD([[makeQuery(id+"F0.imprint","INTERSECT",VERTEX,{"derivedFrom":[subQ3,subQ1]}),1.0]])],"derivedFrom":subQ3})])],"isStart":true}),makeQuery(id+"F8.opChamfer","BLEND_FACE",FACE,{"disambiguationData":[OSD([subQ0]),TDD([makeQuery(id+"F2.opExtrude","CAP_EDGE",EDGE,{"disambiguationData":[OSD([subQ0]),TDD([makeQuery(id+"F0.imprint","IMPRINT",EDGE,{"disambiguationData":[TD([[makeQuery(id+"F0.imprint","INTERSECT",VERTEX,{"derivedFrom":[subQ1,subQ0]}),1.0]])],"derivedFrom":subQ0})])],"isStart":true})])]})],"blendedInto":[makeQuery(id+"F8.opChamfer","BLEND_FACE",FACE,{"disambiguationData":[OSD([subQ0]),TDD([makeQuery(id+"F2.opExtrude","CAP_EDGE",EDGE,{"disambiguationData":[OSD([subQ0]),TDD([makeQuery(id+"F0.imprint","IMPRINT",EDGE,{"disambiguationData":[TD([[makeQuery(id+"F0.imprint","INTERSECT",VERTEX,{"derivedFrom":[subQ1,subQ0]}),1.0]])],"derivedFrom":subQ0})])],"isStart":true})])]})]});}
            var Q17;
            {var subQ0=sQuery(id+"F0.wireOp",EDGE,"E20");var subQ1=sQuery(id+"F0.wireOp",EDGE,"E19.1.7.0");var subQ3=sQuery(id+"F0.wireOp",EDGE,"E4");Q17=makeQuery(id+"F9.opChamfer","BLEND_EDGE",EDGE,{"blendedFrom":[makeQuery(id+"F2.opExtrude","CAP_EDGE",EDGE,{"disambiguationData":[OSD([subQ3]),TDD([makeQuery(id+"F0.imprint","IMPRINT",EDGE,{"disambiguationData":[TD([[makeQuery(id+"F0.imprint","INTERSECT",VERTEX,{"derivedFrom":[subQ3,subQ1]}),1.0]])],"derivedFrom":subQ3})])],"isStart":true}),makeQuery(id+"F8.opChamfer","BLEND_FACE",FACE,{"disambiguationData":[OSD([subQ0]),TDD([makeQuery(id+"F2.opExtrude","CAP_EDGE",EDGE,{"disambiguationData":[OSD([subQ0]),TDD([makeQuery(id+"F0.imprint","IMPRINT",EDGE,{"disambiguationData":[TD([[makeQuery(id+"F0.imprint","INTERSECT",VERTEX,{"derivedFrom":[subQ1,subQ0]}),1.0]])],"derivedFrom":subQ0})])],"isStart":true})])]})],"blendedInto":[makeQuery(id+"F8.opChamfer","BLEND_FACE",FACE,{"disambiguationData":[OSD([subQ0]),TDD([makeQuery(id+"F2.opExtrude","CAP_EDGE",EDGE,{"disambiguationData":[OSD([subQ0]),TDD([makeQuery(id+"F0.imprint","IMPRINT",EDGE,{"disambiguationData":[TD([[makeQuery(id+"F0.imprint","INTERSECT",VERTEX,{"derivedFrom":[subQ1,subQ0]}),1.0]])],"derivedFrom":subQ0})])],"isStart":true})])]})]});}
            var Q18;
            {var subQ0=sQuery(id+"F0.wireOp",EDGE,"E20");var subQ1=sQuery(id+"F0.wireOp",EDGE,"E19.1.6.0");var subQ3=sQuery(id+"F0.wireOp",EDGE,"E4");Q18=makeQuery(id+"F9.opChamfer","BLEND_EDGE",EDGE,{"blendedFrom":[makeQuery(id+"F2.opExtrude","CAP_EDGE",EDGE,{"disambiguationData":[OSD([subQ3]),TDD([makeQuery(id+"F0.imprint","IMPRINT",EDGE,{"disambiguationData":[TD([[makeQuery(id+"F0.imprint","INTERSECT",VERTEX,{"derivedFrom":[subQ3,subQ1]}),1.0]])],"derivedFrom":subQ3})])],"isStart":true}),makeQuery(id+"F8.opChamfer","BLEND_FACE",FACE,{"disambiguationData":[OSD([subQ0]),TDD([makeQuery(id+"F2.opExtrude","CAP_EDGE",EDGE,{"disambiguationData":[OSD([subQ0]),TDD([makeQuery(id+"F0.imprint","IMPRINT",EDGE,{"disambiguationData":[TD([[makeQuery(id+"F0.imprint","INTERSECT",VERTEX,{"derivedFrom":[subQ1,subQ0]}),1.0]])],"derivedFrom":subQ0})])],"isStart":true})])]})],"blendedInto":[makeQuery(id+"F8.opChamfer","BLEND_FACE",FACE,{"disambiguationData":[OSD([subQ0]),TDD([makeQuery(id+"F2.opExtrude","CAP_EDGE",EDGE,{"disambiguationData":[OSD([subQ0]),TDD([makeQuery(id+"F0.imprint","IMPRINT",EDGE,{"disambiguationData":[TD([[makeQuery(id+"F0.imprint","INTERSECT",VERTEX,{"derivedFrom":[subQ1,subQ0]}),1.0]])],"derivedFrom":subQ0})])],"isStart":true})])]})]});}
            var Q19;
            {var subQ0=sQuery(id+"F0.wireOp",EDGE,"E20");var subQ1=sQuery(id+"F0.wireOp",EDGE,"E19.1.5.0");var subQ3=sQuery(id+"F0.wireOp",EDGE,"E4");Q19=makeQuery(id+"F9.opChamfer","BLEND_EDGE",EDGE,{"blendedFrom":[makeQuery(id+"F2.opExtrude","CAP_EDGE",EDGE,{"disambiguationData":[OSD([subQ3]),TDD([makeQuery(id+"F0.imprint","IMPRINT",EDGE,{"disambiguationData":[TD([[makeQuery(id+"F0.imprint","INTERSECT",VERTEX,{"derivedFrom":[subQ3,subQ1]}),1.0]])],"derivedFrom":subQ3})])],"isStart":true}),makeQuery(id+"F8.opChamfer","BLEND_FACE",FACE,{"disambiguationData":[OSD([subQ0]),TDD([makeQuery(id+"F2.opExtrude","CAP_EDGE",EDGE,{"disambiguationData":[OSD([subQ0]),TDD([makeQuery(id+"F0.imprint","IMPRINT",EDGE,{"disambiguationData":[TD([[makeQuery(id+"F0.imprint","INTERSECT",VERTEX,{"derivedFrom":[subQ1,subQ0]}),1.0]])],"derivedFrom":subQ0})])],"isStart":true})])]})],"blendedInto":[makeQuery(id+"F8.opChamfer","BLEND_FACE",FACE,{"disambiguationData":[OSD([subQ0]),TDD([makeQuery(id+"F2.opExtrude","CAP_EDGE",EDGE,{"disambiguationData":[OSD([subQ0]),TDD([makeQuery(id+"F0.imprint","IMPRINT",EDGE,{"disambiguationData":[TD([[makeQuery(id+"F0.imprint","INTERSECT",VERTEX,{"derivedFrom":[subQ1,subQ0]}),1.0]])],"derivedFrom":subQ0})])],"isStart":true})])]})]});}
            var Q20;
            {var subQ0=sQuery(id+"F0.wireOp",EDGE,"E20");var subQ1=sQuery(id+"F0.wireOp",EDGE,"E19.1.4.0");var subQ3=sQuery(id+"F0.wireOp",EDGE,"E4");Q20=makeQuery(id+"F9.opChamfer","BLEND_EDGE",EDGE,{"blendedFrom":[makeQuery(id+"F2.opExtrude","CAP_EDGE",EDGE,{"disambiguationData":[OSD([subQ3]),TDD([makeQuery(id+"F0.imprint","IMPRINT",EDGE,{"disambiguationData":[TD([[makeQuery(id+"F0.imprint","INTERSECT",VERTEX,{"derivedFrom":[subQ3,subQ1]}),1.0]])],"derivedFrom":subQ3})])],"isStart":true}),makeQuery(id+"F8.opChamfer","BLEND_FACE",FACE,{"disambiguationData":[OSD([subQ0]),TDD([makeQuery(id+"F2.opExtrude","CAP_EDGE",EDGE,{"disambiguationData":[OSD([subQ0]),TDD([makeQuery(id+"F0.imprint","IMPRINT",EDGE,{"disambiguationData":[TD([[makeQuery(id+"F0.imprint","INTERSECT",VERTEX,{"derivedFrom":[subQ1,subQ0]}),1.0]])],"derivedFrom":subQ0})])],"isStart":true})])]})],"blendedInto":[makeQuery(id+"F8.opChamfer","BLEND_FACE",FACE,{"disambiguationData":[OSD([subQ0]),TDD([makeQuery(id+"F2.opExtrude","CAP_EDGE",EDGE,{"disambiguationData":[OSD([subQ0]),TDD([makeQuery(id+"F0.imprint","IMPRINT",EDGE,{"disambiguationData":[TD([[makeQuery(id+"F0.imprint","INTERSECT",VERTEX,{"derivedFrom":[subQ1,subQ0]}),1.0]])],"derivedFrom":subQ0})])],"isStart":true})])]})]});}
            var Q21;
            {var subQ0=sQuery(id+"F0.wireOp",EDGE,"E20");var subQ1=sQuery(id+"F0.wireOp",EDGE,"E19.1.3.0");var subQ3=sQuery(id+"F0.wireOp",EDGE,"E4");Q21=makeQuery(id+"F9.opChamfer","BLEND_EDGE",EDGE,{"blendedFrom":[makeQuery(id+"F2.opExtrude","CAP_EDGE",EDGE,{"disambiguationData":[OSD([subQ3]),TDD([makeQuery(id+"F0.imprint","IMPRINT",EDGE,{"disambiguationData":[TD([[makeQuery(id+"F0.imprint","INTERSECT",VERTEX,{"derivedFrom":[subQ3,subQ1]}),1.0]])],"derivedFrom":subQ3})])],"isStart":true}),makeQuery(id+"F8.opChamfer","BLEND_FACE",FACE,{"disambiguationData":[OSD([subQ0]),TDD([makeQuery(id+"F2.opExtrude","CAP_EDGE",EDGE,{"disambiguationData":[OSD([subQ0]),TDD([makeQuery(id+"F0.imprint","IMPRINT",EDGE,{"disambiguationData":[TD([[makeQuery(id+"F0.imprint","INTERSECT",VERTEX,{"derivedFrom":[subQ1,subQ0]}),1.0]])],"derivedFrom":subQ0})])],"isStart":true})])]})],"blendedInto":[makeQuery(id+"F8.opChamfer","BLEND_FACE",FACE,{"disambiguationData":[OSD([subQ0]),TDD([makeQuery(id+"F2.opExtrude","CAP_EDGE",EDGE,{"disambiguationData":[OSD([subQ0]),TDD([makeQuery(id+"F0.imprint","IMPRINT",EDGE,{"disambiguationData":[TD([[makeQuery(id+"F0.imprint","INTERSECT",VERTEX,{"derivedFrom":[subQ1,subQ0]}),1.0]])],"derivedFrom":subQ0})])],"isStart":true})])]})]});}
            var Q22;
            {var subQ0=sQuery(id+"F0.wireOp",EDGE,"E20");var subQ1=sQuery(id+"F0.wireOp",EDGE,"E18.2.0");var subQ3=sQuery(id+"F0.wireOp",EDGE,"E4");Q22=makeQuery(id+"F9.opChamfer","BLEND_EDGE",EDGE,{"blendedFrom":[makeQuery(id+"F2.opExtrude","CAP_EDGE",EDGE,{"disambiguationData":[OSD([subQ3]),TDD([makeQuery(id+"F0.imprint","IMPRINT",EDGE,{"disambiguationData":[TD([[makeQuery(id+"F0.imprint","INTERSECT",VERTEX,{"derivedFrom":[subQ3,subQ1]}),1.0]])],"derivedFrom":subQ3})])],"isStart":true}),makeQuery(id+"F8.opChamfer","BLEND_FACE",FACE,{"disambiguationData":[OSD([subQ0]),TDD([makeQuery(id+"F2.opExtrude","CAP_EDGE",EDGE,{"disambiguationData":[OSD([subQ0]),TDD([makeQuery(id+"F0.imprint","IMPRINT",EDGE,{"disambiguationData":[TD([[makeQuery(id+"F0.imprint","INTERSECT",VERTEX,{"derivedFrom":[subQ1,subQ0]}),1.0]])],"derivedFrom":subQ0})])],"isStart":true})])]})],"blendedInto":[makeQuery(id+"F8.opChamfer","BLEND_FACE",FACE,{"disambiguationData":[OSD([subQ0]),TDD([makeQuery(id+"F2.opExtrude","CAP_EDGE",EDGE,{"disambiguationData":[OSD([subQ0]),TDD([makeQuery(id+"F0.imprint","IMPRINT",EDGE,{"disambiguationData":[TD([[makeQuery(id+"F0.imprint","INTERSECT",VERTEX,{"derivedFrom":[subQ1,subQ0]}),1.0]])],"derivedFrom":subQ0})])],"isStart":true})])]})]});}
            var Q23;
            {var subQ0=sQuery(id+"F0.wireOp",EDGE,"E20");var subQ1=sQuery(id+"F0.wireOp",EDGE,"E18.1.0");var subQ3=sQuery(id+"F0.wireOp",EDGE,"E4");Q23=makeQuery(id+"F9.opChamfer","BLEND_EDGE",EDGE,{"blendedFrom":[makeQuery(id+"F2.opExtrude","CAP_EDGE",EDGE,{"disambiguationData":[OSD([subQ3]),TDD([makeQuery(id+"F0.imprint","IMPRINT",EDGE,{"disambiguationData":[TD([[makeQuery(id+"F0.imprint","INTERSECT",VERTEX,{"derivedFrom":[subQ3,subQ1]}),1.0]])],"derivedFrom":subQ3})])],"isStart":true}),makeQuery(id+"F8.opChamfer","BLEND_FACE",FACE,{"disambiguationData":[OSD([subQ0]),TDD([makeQuery(id+"F2.opExtrude","CAP_EDGE",EDGE,{"disambiguationData":[OSD([subQ0]),TDD([makeQuery(id+"F0.imprint","IMPRINT",EDGE,{"disambiguationData":[TD([[makeQuery(id+"F0.imprint","INTERSECT",VERTEX,{"derivedFrom":[subQ1,subQ0]}),1.0]])],"derivedFrom":subQ0})])],"isStart":true})])]})],"blendedInto":[makeQuery(id+"F8.opChamfer","BLEND_FACE",FACE,{"disambiguationData":[OSD([subQ0]),TDD([makeQuery(id+"F2.opExtrude","CAP_EDGE",EDGE,{"disambiguationData":[OSD([subQ0]),TDD([makeQuery(id+"F0.imprint","IMPRINT",EDGE,{"disambiguationData":[TD([[makeQuery(id+"F0.imprint","INTERSECT",VERTEX,{"derivedFrom":[subQ1,subQ0]}),1.0]])],"derivedFrom":subQ0})])],"isStart":true})])]})]});}
            var Q24;
            {var subQ0=sQuery(id+"F0.wireOp",EDGE,"E20");var subQ1=sQuery(id+"F0.wireOp",EDGE,"E16");var subQ3=sQuery(id+"F0.wireOp",EDGE,"E4");Q24=makeQuery(id+"F9.opChamfer","BLEND_EDGE",EDGE,{"blendedFrom":[makeQuery(id+"F2.opExtrude","CAP_EDGE",EDGE,{"disambiguationData":[OSD([subQ3]),TDD([makeQuery(id+"F0.imprint","IMPRINT",EDGE,{"disambiguationData":[TD([[makeQuery(id+"F0.imprint","INTERSECT",VERTEX,{"derivedFrom":[subQ3,subQ1]}),1.0]])],"derivedFrom":subQ3})])],"isStart":true}),makeQuery(id+"F8.opChamfer","BLEND_FACE",FACE,{"disambiguationData":[OSD([subQ0]),TDD([makeQuery(id+"F2.opExtrude","CAP_EDGE",EDGE,{"disambiguationData":[OSD([subQ0]),TDD([makeQuery(id+"F0.imprint","IMPRINT",EDGE,{"disambiguationData":[TD([[makeQuery(id+"F0.imprint","INTERSECT",VERTEX,{"derivedFrom":[subQ1,subQ0]}),1.0]])],"derivedFrom":subQ0})])],"isStart":true})])]})],"blendedInto":[makeQuery(id+"F8.opChamfer","BLEND_FACE",FACE,{"disambiguationData":[OSD([subQ0]),TDD([makeQuery(id+"F2.opExtrude","CAP_EDGE",EDGE,{"disambiguationData":[OSD([subQ0]),TDD([makeQuery(id+"F0.imprint","IMPRINT",EDGE,{"disambiguationData":[TD([[makeQuery(id+"F0.imprint","INTERSECT",VERTEX,{"derivedFrom":[subQ1,subQ0]}),1.0]])],"derivedFrom":subQ0})])],"isStart":true})])]})]});}
            var Q25;
            {var subQ0=sQuery(id+"F0.wireOp",EDGE,"E20");var subQ1=sQuery(id+"F0.wireOp",EDGE,"E19.1.9.0");var subQ3=sQuery(id+"F0.wireOp",EDGE,"E4");Q25=makeQuery(id+"F9.opChamfer","BLEND_EDGE",EDGE,{"blendedFrom":[makeQuery(id+"F2.opExtrude","CAP_EDGE",EDGE,{"disambiguationData":[OSD([subQ3]),TDD([makeQuery(id+"F0.imprint","IMPRINT",EDGE,{"disambiguationData":[TD([[makeQuery(id+"F0.imprint","INTERSECT",VERTEX,{"derivedFrom":[subQ3,subQ1]}),1.0]])],"derivedFrom":subQ3})])],"isStart":true}),makeQuery(id+"F8.opChamfer","BLEND_FACE",FACE,{"disambiguationData":[OSD([subQ0]),TDD([makeQuery(id+"F2.opExtrude","CAP_EDGE",EDGE,{"disambiguationData":[OSD([subQ0]),TDD([makeQuery(id+"F0.imprint","IMPRINT",EDGE,{"disambiguationData":[TD([[makeQuery(id+"F0.imprint","INTERSECT",VERTEX,{"derivedFrom":[subQ1,subQ0]}),1.0]])],"derivedFrom":subQ0})])],"isStart":true})])]})],"blendedInto":[makeQuery(id+"F8.opChamfer","BLEND_FACE",FACE,{"disambiguationData":[OSD([subQ0]),TDD([makeQuery(id+"F2.opExtrude","CAP_EDGE",EDGE,{"disambiguationData":[OSD([subQ0]),TDD([makeQuery(id+"F0.imprint","IMPRINT",EDGE,{"disambiguationData":[TD([[makeQuery(id+"F0.imprint","INTERSECT",VERTEX,{"derivedFrom":[subQ1,subQ0]}),1.0]])],"derivedFrom":subQ0})])],"isStart":true})])]})]});}
            fillet(context, id + "F11", {"entities" : qUnion([Q0, Q1, Q2, Q3, Q4, Q5, Q6, Q7, Q8, Q9, Q10, Q11, Q12, Q13, Q14, Q15, Q16, Q17, Q18, Q19, Q20, Q21, Q22, Q23, Q24, Q25]), "radius" : 14 * mm, "tangentPropagation" : true, "allowEdgeOverflow" : false});
        }
        {
            var Q0;
            {var subQ3=sQuery(id+"F0.wireOp",EDGE,"E48");Q0=makeQuery(id+"F0.imprint","IMPRINT",FACE,{"disambiguationData":[TD([[makeQuery(id+"F0.imprint","IMPRINT",EDGE,{"derivedFrom":subQ3}),1.0]])]});}
            extrude(context, id + "F12", {"entities" : qUnion([Q0]), "operationType" : NewBodyOperationType.REMOVE, "depth" : 25 * mm});
        }
    });
